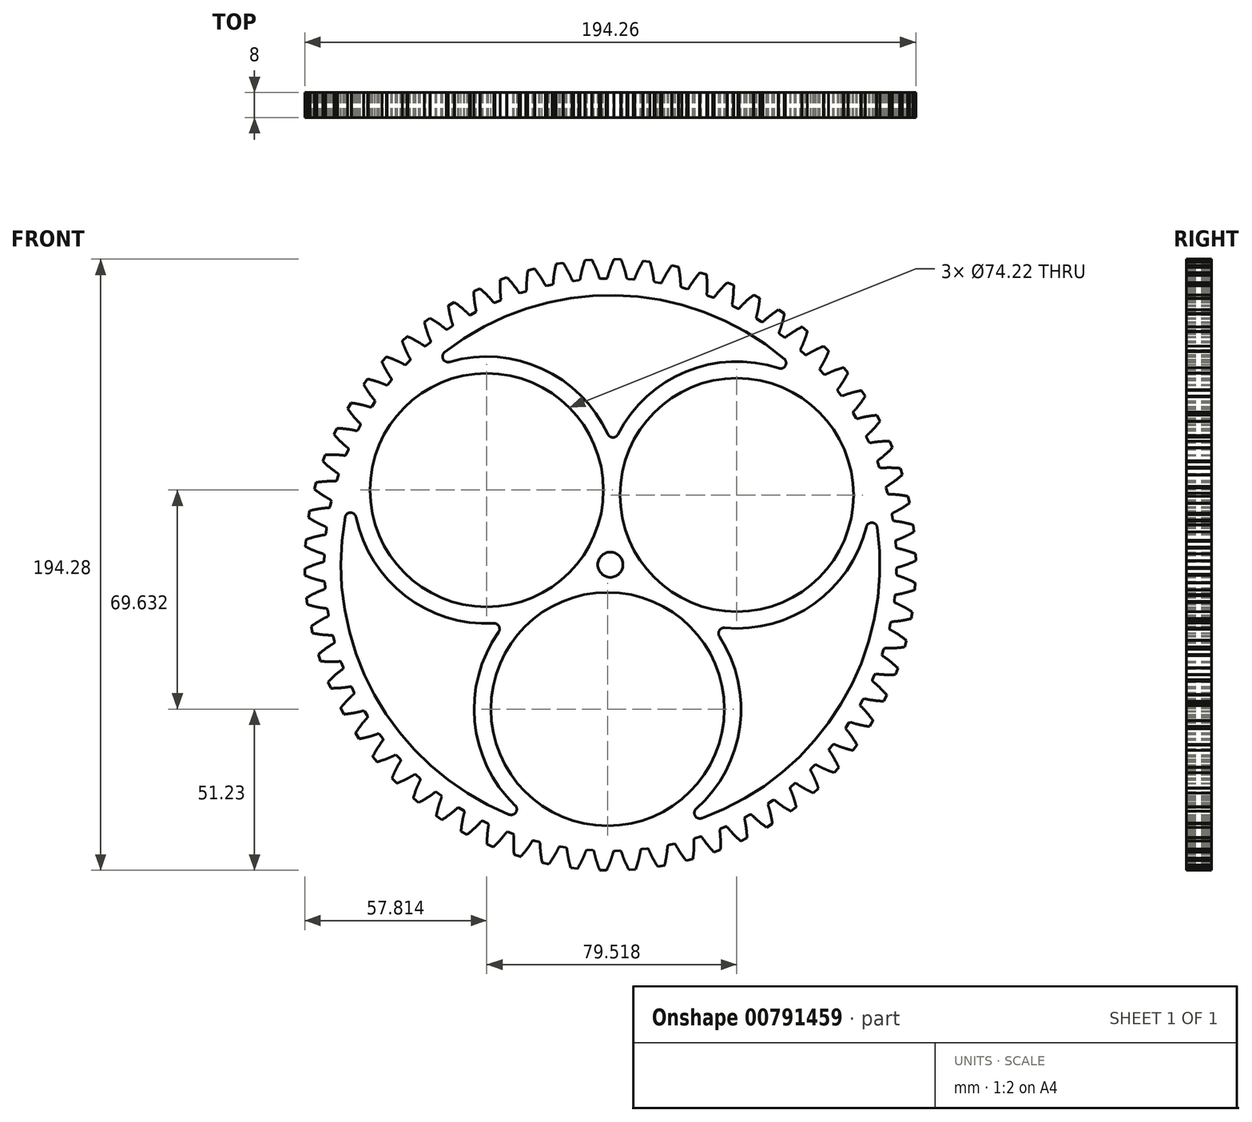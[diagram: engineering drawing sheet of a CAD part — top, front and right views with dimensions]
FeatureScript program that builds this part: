
annotation { "Feature Type Name" : "Feature", "Feature Type Description" : "" }
export const myFeature = defineFeature(function(context is Context, id is Id, definition is map)
    precondition{}
    {
        {
            var Q0;
            Q0=qCreatedBy(makeId("Front.planeOp"),FACE);
            var sketch = newSketch(context, id + "F0", { "sketchPlane" : qUnion([Q0])});
            skCircle(sketch, "E0", {"center": v(0, 0) * mm, "radius": 94.29 * mm, "construction": true});
            skArc(sketch, "E1", {"start": v(29.1, -80.6) * mm, "mid": v(73.36, -44.27) * mm, "end": v(84.86, 11.84) * mm});
            skCircle(sketch, "E2", {"center": v(-0.89, -45.9) * mm, "radius": 37.1 * mm});
            skArc(sketch, "E3", {"start": v(27.31, -77.6) * mm, "mid": v(41.16, -51.56) * mm, "end": v(34.68, -22.79) * mm});
            skArc(sketch, "E4", {"start": v(36.33, -20.06) * mm, "mid": v(64.8, -12.37) * mm, "end": v(81.39, 12.02) * mm});
            skCircle(sketch, "E5", {"center": v(40.2, 22.19) * mm, "radius": 37.1 * mm});
            skArc(sketch, "E6", {"start": v(36.33, -20.06) * mm, "mid": v(34.65, -20.9) * mm, "end": v(34.68, -22.79) * mm});
            skArc(sketch, "E7", {"start": v(84.86, 11.84) * mm, "mid": v(83.2, 13.36) * mm, "end": v(81.39, 12.02) * mm});
            skArc(sketch, "E8", {"start": v(27.31, -77.6) * mm, "mid": v(26.97, -79.83) * mm, "end": v(29.1, -80.6) * mm});
            skCircle(sketch, "E9", {"center": v(-39.32, 23.72) * mm, "radius": 37.1 * mm});
            skArc(sketch, "E10", {"start": v(-0.8, 41.5) * mm, "mid": v(0.78, 40.46) * mm, "end": v(2.4, 41.43) * mm});
            skArc(sketch, "E11", {"start": v(-52.68, 67.58) * mm, "mid": v(-53.17, 65.37) * mm, "end": v(-51.1, 64.48) * mm});
            skArc(sketch, "E12", {"start": v(53.55, 62.46) * mm, "mid": v(55.65, 63.27) * mm, "end": v(55.25, 65.5) * mm});
            skArc(sketch, "E13", {"start": v(53.55, 62.46) * mm, "mid": v(24.07, 61.43) * mm, "end": v(2.4, 41.43) * mm});
            skArc(sketch, "E14", {"start": v(-0.8, 41.5) * mm, "mid": v(-21.69, 62.3) * mm, "end": v(-51.1, 64.48) * mm});
            skArc(sketch, "E15", {"start": v(55.25, 65.5) * mm, "mid": v(1.65, 85.67) * mm, "end": v(-52.68, 67.58) * mm});
            skArc(sketch, "E16", {"start": v(-35.54, -21.43) * mm, "mid": v(-35.43, -19.56) * mm, "end": v(-37.08, -18.64) * mm});
            skArc(sketch, "E17", {"start": v(-32.18, -79.41) * mm, "mid": v(-30.03, -78.73) * mm, "end": v(-30.29, -76.5) * mm});
            skArc(sketch, "E18", {"start": v(-80.86, 15.15) * mm, "mid": v(-82.62, 16.56) * mm, "end": v(-84.34, 15.1) * mm});
            skArc(sketch, "E19", {"start": v(-80.86, 15.15) * mm, "mid": v(-65.23, -9.86) * mm, "end": v(-37.08, -18.64) * mm});
            skArc(sketch, "E20", {"start": v(-35.54, -21.43) * mm, "mid": v(-43.12, -49.94) * mm, "end": v(-30.29, -76.5) * mm});
            skArc(sketch, "E21", {"start": v(-84.34, 15.1) * mm, "mid": v(-75.02, -41.4) * mm, "end": v(-32.18, -79.41) * mm});
            skCircle(sketch, "E22", {"center": v(0, 0) * mm, "radius": 4 * mm});
            skLineSegment(sketch, "E23", {"start": v(-91, 1.29) * mm, "end": v(-91.2, 0.86) * mm});
            skLineSegment(sketch, "E24", {"start": v(-91.2, 0.86) * mm, "end": v(-91.31, 0.84) * mm});
            skLineSegment(sketch, "E25", {"start": v(-91.31, 0.84) * mm, "end": v(-91.43, 0.8) * mm});
            skLineSegment(sketch, "E26", {"start": v(-91.43, 0.8) * mm, "end": v(-91.55, 0.78) * mm});
            skLineSegment(sketch, "E27", {"start": v(-91.55, 0.78) * mm, "end": v(-91.67, 0.75) * mm});
            skLineSegment(sketch, "E28", {"start": v(-91.67, 0.75) * mm, "end": v(-91.79, 0.72) * mm});
            skLineSegment(sketch, "E29", {"start": v(-91.79, 0.72) * mm, "end": v(-91.91, 0.68) * mm});
            skLineSegment(sketch, "E30", {"start": v(-91.91, 0.68) * mm, "end": v(-92.04, 0.65) * mm});
            skLineSegment(sketch, "E31", {"start": v(-92.04, 0.65) * mm, "end": v(-92.17, 0.61) * mm});
            skLineSegment(sketch, "E32", {"start": v(-92.17, 0.61) * mm, "end": v(-92.3, 0.58) * mm});
            skLineSegment(sketch, "E33", {"start": v(-92.3, 0.58) * mm, "end": v(-92.43, 0.54) * mm});
            skLineSegment(sketch, "E34", {"start": v(-92.43, 0.54) * mm, "end": v(-92.56, 0.5) * mm});
            skLineSegment(sketch, "E35", {"start": v(-92.56, 0.5) * mm, "end": v(-92.7, 0.46) * mm});
            skLineSegment(sketch, "E36", {"start": v(-92.7, 0.46) * mm, "end": v(-92.84, 0.42) * mm});
            skLineSegment(sketch, "E37", {"start": v(-92.84, 0.42) * mm, "end": v(-92.98, 0.37) * mm});
            skLineSegment(sketch, "E38", {"start": v(-92.98, 0.37) * mm, "end": v(-93.12, 0.33) * mm});
            skLineSegment(sketch, "E39", {"start": v(-93.12, 0.33) * mm, "end": v(-93.27, 0.28) * mm});
            skLineSegment(sketch, "E40", {"start": v(-93.27, 0.28) * mm, "end": v(-93.42, 0.23) * mm});
            skLineSegment(sketch, "E41", {"start": v(-93.42, 0.23) * mm, "end": v(-93.57, 0.18) * mm});
            skLineSegment(sketch, "E42", {"start": v(-93.57, 0.18) * mm, "end": v(-93.72, 0.13) * mm});
            skLineSegment(sketch, "E43", {"start": v(-93.72, 0.13) * mm, "end": v(-93.87, 0.08) * mm});
            skLineSegment(sketch, "E44", {"start": v(-93.87, 0.08) * mm, "end": v(-94.03, 0.02) * mm});
            skLineSegment(sketch, "E45", {"start": v(-94.03, 0.02) * mm, "end": v(-94.19, -0.04) * mm});
            skLineSegment(sketch, "E46", {"start": v(-94.19, -0.04) * mm, "end": v(-94.35, -0.1) * mm});
            skLineSegment(sketch, "E47", {"start": v(-94.35, -0.1) * mm, "end": v(-94.5, -0.15) * mm});
            skLineSegment(sketch, "E48", {"start": v(-94.5, -0.15) * mm, "end": v(-94.67, -0.22) * mm});
            skLineSegment(sketch, "E49", {"start": v(-94.67, -0.22) * mm, "end": v(-94.84, -0.28) * mm});
            skLineSegment(sketch, "E50", {"start": v(-94.84, -0.28) * mm, "end": v(-95, -0.34) * mm});
            skLineSegment(sketch, "E51", {"start": v(-95, -0.34) * mm, "end": v(-95.18, -0.41) * mm});
            skLineSegment(sketch, "E52", {"start": v(-95.18, -0.41) * mm, "end": v(-95.35, -0.48) * mm});
            skLineSegment(sketch, "E53", {"start": v(-95.35, -0.48) * mm, "end": v(-95.52, -0.55) * mm});
            skLineSegment(sketch, "E54", {"start": v(-95.52, -0.55) * mm, "end": v(-95.7, -0.62) * mm});
            skLineSegment(sketch, "E55", {"start": v(-95.7, -0.62) * mm, "end": v(-95.88, -0.7) * mm});
            skLineSegment(sketch, "E56", {"start": v(-95.88, -0.7) * mm, "end": v(-96.06, -0.77) * mm});
            skLineSegment(sketch, "E57", {"start": v(-96.06, -0.77) * mm, "end": v(-96.24, -0.85) * mm});
            skLineSegment(sketch, "E58", {"start": v(-96.24, -0.85) * mm, "end": v(-96.42, -0.93) * mm});
            skLineSegment(sketch, "E59", {"start": v(-96.42, -0.93) * mm, "end": v(-96.6, -1.01) * mm});
            skLineSegment(sketch, "E60", {"start": v(-96.6, -1.01) * mm, "end": v(-96.8, -1.1) * mm});
            skLineSegment(sketch, "E61", {"start": v(-96.8, -1.1) * mm, "end": v(-96.98, -1.19) * mm});
            skLineSegment(sketch, "E62", {"start": v(-96.98, -1.19) * mm, "end": v(-97.13, -1.27) * mm});
            skLineSegment(sketch, "E63", {"start": v(-97.13, -1.27) * mm, "end": v(-97.08, -3.42) * mm});
            skLineSegment(sketch, "E64", {"start": v(-97.08, -3.42) * mm, "end": v(-96.92, -3.5) * mm});
            skLineSegment(sketch, "E65", {"start": v(-96.92, -3.5) * mm, "end": v(-96.73, -3.58) * mm});
            skLineSegment(sketch, "E66", {"start": v(-96.73, -3.58) * mm, "end": v(-96.54, -3.66) * mm});
            skLineSegment(sketch, "E67", {"start": v(-96.54, -3.66) * mm, "end": v(-96.35, -3.73) * mm});
            skLineSegment(sketch, "E68", {"start": v(-96.35, -3.73) * mm, "end": v(-96.17, -3.8) * mm});
            skLineSegment(sketch, "E69", {"start": v(-96.17, -3.8) * mm, "end": v(-95.98, -3.87) * mm});
            skLineSegment(sketch, "E70", {"start": v(-95.98, -3.87) * mm, "end": v(-95.8, -3.94) * mm});
            skLineSegment(sketch, "E71", {"start": v(-95.8, -3.94) * mm, "end": v(-95.62, -4) * mm});
            skLineSegment(sketch, "E72", {"start": v(-95.62, -4) * mm, "end": v(-95.44, -4.07) * mm});
            skLineSegment(sketch, "E73", {"start": v(-95.44, -4.07) * mm, "end": v(-95.26, -4.13) * mm});
            skLineSegment(sketch, "E74", {"start": v(-95.26, -4.13) * mm, "end": v(-95.09, -4.2) * mm});
            skLineSegment(sketch, "E75", {"start": v(-95.09, -4.2) * mm, "end": v(-94.91, -4.25) * mm});
            skLineSegment(sketch, "E76", {"start": v(-94.91, -4.25) * mm, "end": v(-94.74, -4.3) * mm});
            skLineSegment(sketch, "E77", {"start": v(-94.74, -4.3) * mm, "end": v(-94.57, -4.36) * mm});
            skLineSegment(sketch, "E78", {"start": v(-94.57, -4.36) * mm, "end": v(-94.4, -4.41) * mm});
            skLineSegment(sketch, "E79", {"start": v(-94.4, -4.41) * mm, "end": v(-94.24, -4.47) * mm});
            skLineSegment(sketch, "E80", {"start": v(-94.24, -4.47) * mm, "end": v(-94.08, -4.52) * mm});
            skLineSegment(sketch, "E81", {"start": v(-94.08, -4.52) * mm, "end": v(-93.92, -4.57) * mm});
            skLineSegment(sketch, "E82", {"start": v(-93.92, -4.57) * mm, "end": v(-93.76, -4.61) * mm});
            skLineSegment(sketch, "E83", {"start": v(-93.76, -4.61) * mm, "end": v(-93.6, -4.66) * mm});
            skLineSegment(sketch, "E84", {"start": v(-93.6, -4.66) * mm, "end": v(-93.45, -4.7) * mm});
            skLineSegment(sketch, "E85", {"start": v(-93.45, -4.7) * mm, "end": v(-93.3, -4.75) * mm});
            skLineSegment(sketch, "E86", {"start": v(-93.3, -4.75) * mm, "end": v(-93.15, -4.79) * mm});
            skLineSegment(sketch, "E87", {"start": v(-93.15, -4.79) * mm, "end": v(-93, -4.83) * mm});
            skLineSegment(sketch, "E88", {"start": v(-93, -4.83) * mm, "end": v(-92.85, -4.87) * mm});
            skLineSegment(sketch, "E89", {"start": v(-92.85, -4.87) * mm, "end": v(-92.71, -4.9) * mm});
            skLineSegment(sketch, "E90", {"start": v(-92.71, -4.9) * mm, "end": v(-92.57, -4.94) * mm});
            skLineSegment(sketch, "E91", {"start": v(-92.57, -4.94) * mm, "end": v(-92.43, -4.97) * mm});
            skLineSegment(sketch, "E92", {"start": v(-92.43, -4.97) * mm, "end": v(-92.3, -5) * mm});
            skLineSegment(sketch, "E93", {"start": v(-92.3, -5) * mm, "end": v(-92.16, -5.04) * mm});
            skLineSegment(sketch, "E94", {"start": v(-92.16, -5.04) * mm, "end": v(-92.03, -5.07) * mm});
            skLineSegment(sketch, "E95", {"start": v(-92.03, -5.07) * mm, "end": v(-91.9, -5.1) * mm});
            skLineSegment(sketch, "E96", {"start": v(-91.9, -5.1) * mm, "end": v(-91.77, -5.13) * mm});
            skLineSegment(sketch, "E97", {"start": v(-91.77, -5.13) * mm, "end": v(-91.65, -5.15) * mm});
            skLineSegment(sketch, "E98", {"start": v(-91.65, -5.15) * mm, "end": v(-91.52, -5.18) * mm});
            skLineSegment(sketch, "E99", {"start": v(-91.52, -5.18) * mm, "end": v(-91.4, -5.2) * mm});
            skLineSegment(sketch, "E100", {"start": v(-91.4, -5.2) * mm, "end": v(-91.28, -5.23) * mm});
            skLineSegment(sketch, "E101", {"start": v(-91.28, -5.23) * mm, "end": v(-91.17, -5.25) * mm});
            skLineSegment(sketch, "E102", {"start": v(-91.17, -5.25) * mm, "end": v(-91.05, -5.27) * mm});
            skLineSegment(sketch, "E103", {"start": v(-91.05, -5.27) * mm, "end": v(-90.82, -5.68) * mm});
            skLineSegment(sketch, "E104", {"start": v(-90.82, -5.68) * mm, "end": v(-90.7, -7.37) * mm});
            skLineSegment(sketch, "E105", {"start": v(-90.7, -7.37) * mm, "end": v(-90.87, -7.81) * mm});
            skLineSegment(sketch, "E106", {"start": v(-90.87, -7.81) * mm, "end": v(-90.98, -7.85) * mm});
            skLineSegment(sketch, "E107", {"start": v(-90.98, -7.85) * mm, "end": v(-91.1, -7.89) * mm});
            skLineSegment(sketch, "E108", {"start": v(-91.1, -7.89) * mm, "end": v(-91.2, -7.93) * mm});
            skLineSegment(sketch, "E109", {"start": v(-91.2, -7.93) * mm, "end": v(-91.32, -7.97) * mm});
            skLineSegment(sketch, "E110", {"start": v(-91.32, -7.97) * mm, "end": v(-91.44, -8.01) * mm});
            skLineSegment(sketch, "E111", {"start": v(-91.44, -8.01) * mm, "end": v(-91.56, -8.06) * mm});
            skLineSegment(sketch, "E112", {"start": v(-91.56, -8.06) * mm, "end": v(-91.68, -8.1) * mm});
            skLineSegment(sketch, "E113", {"start": v(-91.68, -8.1) * mm, "end": v(-91.8, -8.15) * mm});
            skLineSegment(sketch, "E114", {"start": v(-91.8, -8.15) * mm, "end": v(-91.93, -8.2) * mm});
            skLineSegment(sketch, "E115", {"start": v(-91.93, -8.2) * mm, "end": v(-92.06, -8.25) * mm});
            skLineSegment(sketch, "E116", {"start": v(-92.06, -8.25) * mm, "end": v(-92.2, -8.3) * mm});
            skLineSegment(sketch, "E117", {"start": v(-92.2, -8.3) * mm, "end": v(-92.32, -8.36) * mm});
            skLineSegment(sketch, "E118", {"start": v(-92.32, -8.36) * mm, "end": v(-92.46, -8.41) * mm});
            skLineSegment(sketch, "E119", {"start": v(-92.46, -8.41) * mm, "end": v(-92.6, -8.47) * mm});
            skLineSegment(sketch, "E120", {"start": v(-92.6, -8.47) * mm, "end": v(-92.73, -8.53) * mm});
            skLineSegment(sketch, "E121", {"start": v(-92.73, -8.53) * mm, "end": v(-92.87, -8.59) * mm});
            skLineSegment(sketch, "E122", {"start": v(-92.87, -8.59) * mm, "end": v(-93.02, -8.65) * mm});
            skLineSegment(sketch, "E123", {"start": v(-93.02, -8.65) * mm, "end": v(-93.16, -8.71) * mm});
            skLineSegment(sketch, "E124", {"start": v(-93.16, -8.71) * mm, "end": v(-93.3, -8.78) * mm});
            skLineSegment(sketch, "E125", {"start": v(-93.3, -8.78) * mm, "end": v(-93.46, -8.85) * mm});
            skLineSegment(sketch, "E126", {"start": v(-93.46, -8.85) * mm, "end": v(-93.6, -8.92) * mm});
            skLineSegment(sketch, "E127", {"start": v(-93.6, -8.92) * mm, "end": v(-93.76, -8.99) * mm});
            skLineSegment(sketch, "E128", {"start": v(-93.76, -8.99) * mm, "end": v(-93.91, -9.06) * mm});
            skLineSegment(sketch, "E129", {"start": v(-93.91, -9.06) * mm, "end": v(-94.07, -9.14) * mm});
            skLineSegment(sketch, "E130", {"start": v(-94.07, -9.14) * mm, "end": v(-94.22, -9.21) * mm});
            skLineSegment(sketch, "E131", {"start": v(-94.22, -9.21) * mm, "end": v(-94.38, -9.3) * mm});
            skLineSegment(sketch, "E132", {"start": v(-94.38, -9.3) * mm, "end": v(-94.54, -9.37) * mm});
            skLineSegment(sketch, "E133", {"start": v(-94.54, -9.37) * mm, "end": v(-94.7, -9.46) * mm});
            skLineSegment(sketch, "E134", {"start": v(-94.7, -9.46) * mm, "end": v(-94.87, -9.54) * mm});
            skLineSegment(sketch, "E135", {"start": v(-94.87, -9.54) * mm, "end": v(-95.04, -9.63) * mm});
            skLineSegment(sketch, "E136", {"start": v(-95.04, -9.63) * mm, "end": v(-95.2, -9.72) * mm});
            skLineSegment(sketch, "E137", {"start": v(-95.2, -9.72) * mm, "end": v(-95.38, -9.8) * mm});
            skLineSegment(sketch, "E138", {"start": v(-95.38, -9.8) * mm, "end": v(-95.55, -9.9) * mm});
            skLineSegment(sketch, "E139", {"start": v(-95.55, -9.9) * mm, "end": v(-95.72, -10) * mm});
            skLineSegment(sketch, "E140", {"start": v(-95.72, -10) * mm, "end": v(-95.9, -10.1) * mm});
            skLineSegment(sketch, "E141", {"start": v(-95.9, -10.1) * mm, "end": v(-96.07, -10.2) * mm});
            skLineSegment(sketch, "E142", {"start": v(-96.07, -10.2) * mm, "end": v(-96.25, -10.3) * mm});
            skLineSegment(sketch, "E143", {"start": v(-96.25, -10.3) * mm, "end": v(-96.43, -10.4) * mm});
            skLineSegment(sketch, "E144", {"start": v(-96.43, -10.4) * mm, "end": v(-96.57, -10.5) * mm});
            skLineSegment(sketch, "E145", {"start": v(-96.57, -10.5) * mm, "end": v(-96.32, -12.64) * mm});
            skLineSegment(sketch, "E146", {"start": v(-96.32, -12.64) * mm, "end": v(-96.15, -12.7) * mm});
            skLineSegment(sketch, "E147", {"start": v(-96.15, -12.7) * mm, "end": v(-95.95, -12.76) * mm});
            skLineSegment(sketch, "E148", {"start": v(-95.95, -12.76) * mm, "end": v(-95.76, -12.82) * mm});
            skLineSegment(sketch, "E149", {"start": v(-95.76, -12.82) * mm, "end": v(-95.56, -12.87) * mm});
            skLineSegment(sketch, "E150", {"start": v(-95.56, -12.87) * mm, "end": v(-95.37, -12.92) * mm});
            skLineSegment(sketch, "E151", {"start": v(-95.37, -12.92) * mm, "end": v(-95.18, -12.98) * mm});
            skLineSegment(sketch, "E152", {"start": v(-95.18, -12.98) * mm, "end": v(-94.99, -13.03) * mm});
            skLineSegment(sketch, "E153", {"start": v(-94.99, -13.03) * mm, "end": v(-94.8, -13.07) * mm});
            skLineSegment(sketch, "E154", {"start": v(-94.8, -13.07) * mm, "end": v(-94.62, -13.12) * mm});
            skLineSegment(sketch, "E155", {"start": v(-94.62, -13.12) * mm, "end": v(-94.44, -13.17) * mm});
            skLineSegment(sketch, "E156", {"start": v(-94.44, -13.17) * mm, "end": v(-94.26, -13.2) * mm});
            skLineSegment(sketch, "E157", {"start": v(-94.26, -13.2) * mm, "end": v(-94.08, -13.25) * mm});
            skLineSegment(sketch, "E158", {"start": v(-94.08, -13.25) * mm, "end": v(-93.9, -13.3) * mm});
            skLineSegment(sketch, "E159", {"start": v(-93.9, -13.3) * mm, "end": v(-93.73, -13.33) * mm});
            skLineSegment(sketch, "E160", {"start": v(-93.73, -13.33) * mm, "end": v(-93.56, -13.37) * mm});
            skLineSegment(sketch, "E161", {"start": v(-93.56, -13.37) * mm, "end": v(-93.39, -13.4) * mm});
            skLineSegment(sketch, "E162", {"start": v(-93.39, -13.4) * mm, "end": v(-93.22, -13.44) * mm});
            skLineSegment(sketch, "E163", {"start": v(-93.22, -13.44) * mm, "end": v(-93.06, -13.47) * mm});
            skLineSegment(sketch, "E164", {"start": v(-93.06, -13.47) * mm, "end": v(-92.9, -13.5) * mm});
            skLineSegment(sketch, "E165", {"start": v(-92.9, -13.5) * mm, "end": v(-92.74, -13.54) * mm});
            skLineSegment(sketch, "E166", {"start": v(-92.74, -13.54) * mm, "end": v(-92.58, -13.57) * mm});
            skLineSegment(sketch, "E167", {"start": v(-92.58, -13.57) * mm, "end": v(-92.42, -13.6) * mm});
            skLineSegment(sketch, "E168", {"start": v(-92.42, -13.6) * mm, "end": v(-92.27, -13.62) * mm});
            skLineSegment(sketch, "E169", {"start": v(-92.27, -13.62) * mm, "end": v(-92.12, -13.65) * mm});
            skLineSegment(sketch, "E170", {"start": v(-92.12, -13.65) * mm, "end": v(-91.97, -13.67) * mm});
            skLineSegment(sketch, "E171", {"start": v(-91.97, -13.67) * mm, "end": v(-91.83, -13.7) * mm});
            skLineSegment(sketch, "E172", {"start": v(-91.83, -13.7) * mm, "end": v(-91.68, -13.72) * mm});
            skLineSegment(sketch, "E173", {"start": v(-91.68, -13.72) * mm, "end": v(-91.54, -13.74) * mm});
            skLineSegment(sketch, "E174", {"start": v(-91.54, -13.74) * mm, "end": v(-91.4, -13.76) * mm});
            skLineSegment(sketch, "E175", {"start": v(-91.4, -13.76) * mm, "end": v(-91.26, -13.78) * mm});
            skLineSegment(sketch, "E176", {"start": v(-91.26, -13.78) * mm, "end": v(-91.13, -13.8) * mm});
            skLineSegment(sketch, "E177", {"start": v(-91.13, -13.8) * mm, "end": v(-91, -13.81) * mm});
            skLineSegment(sketch, "E178", {"start": v(-91, -13.81) * mm, "end": v(-90.87, -13.83) * mm});
            skLineSegment(sketch, "E179", {"start": v(-90.87, -13.83) * mm, "end": v(-90.74, -13.84) * mm});
            skLineSegment(sketch, "E180", {"start": v(-90.74, -13.84) * mm, "end": v(-90.62, -13.85) * mm});
            skLineSegment(sketch, "E181", {"start": v(-90.62, -13.85) * mm, "end": v(-90.5, -13.87) * mm});
            skLineSegment(sketch, "E182", {"start": v(-90.5, -13.87) * mm, "end": v(-90.37, -13.88) * mm});
            skLineSegment(sketch, "E183", {"start": v(-90.37, -13.88) * mm, "end": v(-90.26, -13.9) * mm});
            skLineSegment(sketch, "E184", {"start": v(-90.26, -13.9) * mm, "end": v(-90.14, -13.9) * mm});
            skLineSegment(sketch, "E185", {"start": v(-90.14, -13.9) * mm, "end": v(-89.87, -14.3) * mm});
            skLineSegment(sketch, "E186", {"start": v(-89.87, -14.3) * mm, "end": v(-89.6, -15.96) * mm});
            skLineSegment(sketch, "E187", {"start": v(-89.6, -15.96) * mm, "end": v(-89.72, -16.41) * mm});
            skLineSegment(sketch, "E188", {"start": v(-89.72, -16.41) * mm, "end": v(-89.82, -16.46) * mm});
            skLineSegment(sketch, "E189", {"start": v(-89.82, -16.46) * mm, "end": v(-89.93, -16.51) * mm});
            skLineSegment(sketch, "E190", {"start": v(-89.93, -16.51) * mm, "end": v(-90.04, -16.56) * mm});
            skLineSegment(sketch, "E191", {"start": v(-90.04, -16.56) * mm, "end": v(-90.15, -16.61) * mm});
            skLineSegment(sketch, "E192", {"start": v(-90.15, -16.61) * mm, "end": v(-90.26, -16.67) * mm});
            skLineSegment(sketch, "E193", {"start": v(-90.26, -16.67) * mm, "end": v(-90.38, -16.72) * mm});
            skLineSegment(sketch, "E194", {"start": v(-90.38, -16.72) * mm, "end": v(-90.5, -16.78) * mm});
            skLineSegment(sketch, "E195", {"start": v(-90.5, -16.78) * mm, "end": v(-90.62, -16.84) * mm});
            skLineSegment(sketch, "E196", {"start": v(-90.62, -16.84) * mm, "end": v(-90.74, -16.9) * mm});
            skLineSegment(sketch, "E197", {"start": v(-90.74, -16.9) * mm, "end": v(-90.86, -16.96) * mm});
            skLineSegment(sketch, "E198", {"start": v(-90.86, -16.96) * mm, "end": v(-90.99, -17.03) * mm});
            skLineSegment(sketch, "E199", {"start": v(-90.99, -17.03) * mm, "end": v(-91.11, -17.1) * mm});
            skLineSegment(sketch, "E200", {"start": v(-91.11, -17.1) * mm, "end": v(-91.24, -17.16) * mm});
            skLineSegment(sketch, "E201", {"start": v(-91.24, -17.16) * mm, "end": v(-91.37, -17.23) * mm});
            skLineSegment(sketch, "E202", {"start": v(-91.37, -17.23) * mm, "end": v(-91.5, -17.3) * mm});
            skLineSegment(sketch, "E203", {"start": v(-91.5, -17.3) * mm, "end": v(-91.64, -17.38) * mm});
            skLineSegment(sketch, "E204", {"start": v(-91.64, -17.38) * mm, "end": v(-91.77, -17.45) * mm});
            skLineSegment(sketch, "E205", {"start": v(-91.77, -17.45) * mm, "end": v(-91.91, -17.53) * mm});
            skLineSegment(sketch, "E206", {"start": v(-91.91, -17.53) * mm, "end": v(-92.05, -17.6) * mm});
            skLineSegment(sketch, "E207", {"start": v(-92.05, -17.6) * mm, "end": v(-92.2, -17.7) * mm});
            skLineSegment(sketch, "E208", {"start": v(-92.2, -17.7) * mm, "end": v(-92.33, -17.77) * mm});
            skLineSegment(sketch, "E209", {"start": v(-92.33, -17.77) * mm, "end": v(-92.48, -17.86) * mm});
            skLineSegment(sketch, "E210", {"start": v(-92.48, -17.86) * mm, "end": v(-92.62, -17.95) * mm});
            skLineSegment(sketch, "E211", {"start": v(-92.62, -17.95) * mm, "end": v(-92.77, -18.04) * mm});
            skLineSegment(sketch, "E212", {"start": v(-92.77, -18.04) * mm, "end": v(-92.92, -18.13) * mm});
            skLineSegment(sketch, "E213", {"start": v(-92.92, -18.13) * mm, "end": v(-93.07, -18.22) * mm});
            skLineSegment(sketch, "E214", {"start": v(-93.07, -18.22) * mm, "end": v(-93.22, -18.32) * mm});
            skLineSegment(sketch, "E215", {"start": v(-93.22, -18.32) * mm, "end": v(-93.38, -18.42) * mm});
            skLineSegment(sketch, "E216", {"start": v(-93.38, -18.42) * mm, "end": v(-93.53, -18.52) * mm});
            skLineSegment(sketch, "E217", {"start": v(-93.53, -18.52) * mm, "end": v(-93.7, -18.62) * mm});
            skLineSegment(sketch, "E218", {"start": v(-93.7, -18.62) * mm, "end": v(-93.85, -18.72) * mm});
            skLineSegment(sketch, "E219", {"start": v(-93.85, -18.72) * mm, "end": v(-94.01, -18.83) * mm});
            skLineSegment(sketch, "E220", {"start": v(-94.01, -18.83) * mm, "end": v(-94.17, -18.94) * mm});
            skLineSegment(sketch, "E221", {"start": v(-94.17, -18.94) * mm, "end": v(-94.34, -19.05) * mm});
            skLineSegment(sketch, "E222", {"start": v(-94.34, -19.05) * mm, "end": v(-94.5, -19.16) * mm});
            skLineSegment(sketch, "E223", {"start": v(-94.5, -19.16) * mm, "end": v(-94.67, -19.28) * mm});
            skLineSegment(sketch, "E224", {"start": v(-94.67, -19.28) * mm, "end": v(-94.83, -19.4) * mm});
            skLineSegment(sketch, "E225", {"start": v(-94.83, -19.4) * mm, "end": v(-95, -19.52) * mm});
            skLineSegment(sketch, "E226", {"start": v(-95, -19.52) * mm, "end": v(-95.14, -19.63) * mm});
            skLineSegment(sketch, "E227", {"start": v(-95.14, -19.63) * mm, "end": v(-94.68, -21.74) * mm});
            skLineSegment(sketch, "E228", {"start": v(-94.68, -21.74) * mm, "end": v(-94.5, -21.78) * mm});
            skLineSegment(sketch, "E229", {"start": v(-94.5, -21.78) * mm, "end": v(-94.3, -21.82) * mm});
            skLineSegment(sketch, "E230", {"start": v(-94.3, -21.82) * mm, "end": v(-94.1, -21.86) * mm});
            skLineSegment(sketch, "E231", {"start": v(-94.1, -21.86) * mm, "end": v(-93.9, -21.9) * mm});
            skLineSegment(sketch, "E232", {"start": v(-93.9, -21.9) * mm, "end": v(-93.7, -21.93) * mm});
            skLineSegment(sketch, "E233", {"start": v(-93.7, -21.93) * mm, "end": v(-93.51, -21.96) * mm});
            skLineSegment(sketch, "E234", {"start": v(-93.51, -21.96) * mm, "end": v(-93.32, -22) * mm});
            skLineSegment(sketch, "E235", {"start": v(-93.32, -22) * mm, "end": v(-93.13, -22.03) * mm});
            skLineSegment(sketch, "E236", {"start": v(-93.13, -22.03) * mm, "end": v(-92.94, -22.06) * mm});
            skLineSegment(sketch, "E237", {"start": v(-92.94, -22.06) * mm, "end": v(-92.76, -22.08) * mm});
            skLineSegment(sketch, "E238", {"start": v(-92.76, -22.08) * mm, "end": v(-92.57, -22.1) * mm});
            skLineSegment(sketch, "E239", {"start": v(-92.57, -22.1) * mm, "end": v(-92.4, -22.13) * mm});
            skLineSegment(sketch, "E240", {"start": v(-92.4, -22.13) * mm, "end": v(-92.21, -22.16) * mm});
            skLineSegment(sketch, "E241", {"start": v(-92.21, -22.16) * mm, "end": v(-92.04, -22.18) * mm});
            skLineSegment(sketch, "E242", {"start": v(-92.04, -22.18) * mm, "end": v(-91.86, -22.2) * mm});
            skLineSegment(sketch, "E243", {"start": v(-91.86, -22.2) * mm, "end": v(-91.7, -22.22) * mm});
            skLineSegment(sketch, "E244", {"start": v(-91.7, -22.22) * mm, "end": v(-91.52, -22.24) * mm});
            skLineSegment(sketch, "E245", {"start": v(-91.52, -22.24) * mm, "end": v(-91.36, -22.26) * mm});
            skLineSegment(sketch, "E246", {"start": v(-91.36, -22.26) * mm, "end": v(-91.2, -22.27) * mm});
            skLineSegment(sketch, "E247", {"start": v(-91.2, -22.27) * mm, "end": v(-91.03, -22.29) * mm});
            skLineSegment(sketch, "E248", {"start": v(-91.03, -22.29) * mm, "end": v(-90.87, -22.3) * mm});
            skLineSegment(sketch, "E249", {"start": v(-90.87, -22.3) * mm, "end": v(-90.71, -22.32) * mm});
            skLineSegment(sketch, "E250", {"start": v(-90.71, -22.32) * mm, "end": v(-90.56, -22.33) * mm});
            skLineSegment(sketch, "E251", {"start": v(-90.56, -22.33) * mm, "end": v(-90.4, -22.34) * mm});
            skLineSegment(sketch, "E252", {"start": v(-90.4, -22.34) * mm, "end": v(-90.26, -22.35) * mm});
            skLineSegment(sketch, "E253", {"start": v(-90.26, -22.35) * mm, "end": v(-90.1, -22.36) * mm});
            skLineSegment(sketch, "E254", {"start": v(-90.1, -22.36) * mm, "end": v(-89.96, -22.37) * mm});
            skLineSegment(sketch, "E255", {"start": v(-89.96, -22.37) * mm, "end": v(-89.82, -22.38) * mm});
            skLineSegment(sketch, "E256", {"start": v(-89.82, -22.38) * mm, "end": v(-89.68, -22.38) * mm});
            skLineSegment(sketch, "E257", {"start": v(-89.68, -22.38) * mm, "end": v(-89.54, -22.39) * mm});
            skLineSegment(sketch, "E258", {"start": v(-89.54, -22.39) * mm, "end": v(-89.4, -22.4) * mm});
            skLineSegment(sketch, "E259", {"start": v(-89.4, -22.4) * mm, "end": v(-89.27, -22.4) * mm});
            skLineSegment(sketch, "E260", {"start": v(-89.27, -22.4) * mm, "end": v(-89.14, -22.4) * mm});
            skLineSegment(sketch, "E261", {"start": v(-89.14, -22.4) * mm, "end": v(-89.01, -22.4) * mm});
            skLineSegment(sketch, "E262", {"start": v(-89.01, -22.4) * mm, "end": v(-88.89, -22.4) * mm});
            skLineSegment(sketch, "E263", {"start": v(-88.89, -22.4) * mm, "end": v(-88.77, -22.4) * mm});
            skLineSegment(sketch, "E264", {"start": v(-88.77, -22.4) * mm, "end": v(-88.64, -22.4) * mm});
            skLineSegment(sketch, "E265", {"start": v(-88.64, -22.4) * mm, "end": v(-88.53, -22.4) * mm});
            skLineSegment(sketch, "E266", {"start": v(-88.53, -22.4) * mm, "end": v(-88.41, -22.4) * mm});
            skLineSegment(sketch, "E267", {"start": v(-88.41, -22.4) * mm, "end": v(-88.1, -22.77) * mm});
            skLineSegment(sketch, "E268", {"start": v(-88.1, -22.77) * mm, "end": v(-87.67, -24.4) * mm});
            skLineSegment(sketch, "E269", {"start": v(-87.67, -24.4) * mm, "end": v(-87.75, -24.87) * mm});
            skLineSegment(sketch, "E270", {"start": v(-87.75, -24.87) * mm, "end": v(-87.85, -24.93) * mm});
            skLineSegment(sketch, "E271", {"start": v(-87.85, -24.93) * mm, "end": v(-87.95, -24.98) * mm});
            skLineSegment(sketch, "E272", {"start": v(-87.95, -24.98) * mm, "end": v(-88.06, -25.05) * mm});
            skLineSegment(sketch, "E273", {"start": v(-88.06, -25.05) * mm, "end": v(-88.16, -25.1) * mm});
            skLineSegment(sketch, "E274", {"start": v(-88.16, -25.1) * mm, "end": v(-88.27, -25.17) * mm});
            skLineSegment(sketch, "E275", {"start": v(-88.27, -25.17) * mm, "end": v(-88.38, -25.24) * mm});
            skLineSegment(sketch, "E276", {"start": v(-88.38, -25.24) * mm, "end": v(-88.5, -25.3) * mm});
            skLineSegment(sketch, "E277", {"start": v(-88.5, -25.3) * mm, "end": v(-88.6, -25.38) * mm});
            skLineSegment(sketch, "E278", {"start": v(-88.6, -25.38) * mm, "end": v(-88.72, -25.45) * mm});
            skLineSegment(sketch, "E279", {"start": v(-88.72, -25.45) * mm, "end": v(-88.84, -25.52) * mm});
            skLineSegment(sketch, "E280", {"start": v(-88.84, -25.52) * mm, "end": v(-88.95, -25.6) * mm});
            skLineSegment(sketch, "E281", {"start": v(-88.95, -25.6) * mm, "end": v(-89.07, -25.68) * mm});
            skLineSegment(sketch, "E282", {"start": v(-89.07, -25.68) * mm, "end": v(-89.2, -25.76) * mm});
            skLineSegment(sketch, "E283", {"start": v(-89.2, -25.76) * mm, "end": v(-89.32, -25.84) * mm});
            skLineSegment(sketch, "E284", {"start": v(-89.32, -25.84) * mm, "end": v(-89.44, -25.92) * mm});
            skLineSegment(sketch, "E285", {"start": v(-89.44, -25.92) * mm, "end": v(-89.57, -26) * mm});
            skLineSegment(sketch, "E286", {"start": v(-89.57, -26) * mm, "end": v(-89.7, -26.1) * mm});
            skLineSegment(sketch, "E287", {"start": v(-89.7, -26.1) * mm, "end": v(-89.83, -26.19) * mm});
            skLineSegment(sketch, "E288", {"start": v(-89.83, -26.19) * mm, "end": v(-89.96, -26.28) * mm});
            skLineSegment(sketch, "E289", {"start": v(-89.96, -26.28) * mm, "end": v(-90.1, -26.37) * mm});
            skLineSegment(sketch, "E290", {"start": v(-90.1, -26.37) * mm, "end": v(-90.23, -26.47) * mm});
            skLineSegment(sketch, "E291", {"start": v(-90.23, -26.47) * mm, "end": v(-90.36, -26.57) * mm});
            skLineSegment(sketch, "E292", {"start": v(-90.36, -26.57) * mm, "end": v(-90.5, -26.67) * mm});
            skLineSegment(sketch, "E293", {"start": v(-90.5, -26.67) * mm, "end": v(-90.64, -26.77) * mm});
            skLineSegment(sketch, "E294", {"start": v(-90.64, -26.77) * mm, "end": v(-90.78, -26.88) * mm});
            skLineSegment(sketch, "E295", {"start": v(-90.78, -26.88) * mm, "end": v(-90.92, -26.99) * mm});
            skLineSegment(sketch, "E296", {"start": v(-90.92, -26.99) * mm, "end": v(-91.06, -27.1) * mm});
            skLineSegment(sketch, "E297", {"start": v(-91.06, -27.1) * mm, "end": v(-91.2, -27.2) * mm});
            skLineSegment(sketch, "E298", {"start": v(-91.2, -27.2) * mm, "end": v(-91.35, -27.32) * mm});
            skLineSegment(sketch, "E299", {"start": v(-91.35, -27.32) * mm, "end": v(-91.5, -27.44) * mm});
            skLineSegment(sketch, "E300", {"start": v(-91.5, -27.44) * mm, "end": v(-91.65, -27.56) * mm});
            skLineSegment(sketch, "E301", {"start": v(-91.65, -27.56) * mm, "end": v(-91.8, -27.68) * mm});
            skLineSegment(sketch, "E302", {"start": v(-91.8, -27.68) * mm, "end": v(-91.95, -27.8) * mm});
            skLineSegment(sketch, "E303", {"start": v(-91.95, -27.8) * mm, "end": v(-92.1, -27.93) * mm});
            skLineSegment(sketch, "E304", {"start": v(-92.1, -27.93) * mm, "end": v(-92.25, -28.06) * mm});
            skLineSegment(sketch, "E305", {"start": v(-92.25, -28.06) * mm, "end": v(-92.4, -28.2) * mm});
            skLineSegment(sketch, "E306", {"start": v(-92.4, -28.2) * mm, "end": v(-92.56, -28.32) * mm});
            skLineSegment(sketch, "E307", {"start": v(-92.56, -28.32) * mm, "end": v(-92.72, -28.46) * mm});
            skLineSegment(sketch, "E308", {"start": v(-92.72, -28.46) * mm, "end": v(-92.84, -28.59) * mm});
            skLineSegment(sketch, "E309", {"start": v(-92.84, -28.59) * mm, "end": v(-92.19, -30.64) * mm});
            skLineSegment(sketch, "E310", {"start": v(-92.19, -30.64) * mm, "end": v(-92.01, -30.67) * mm});
            skLineSegment(sketch, "E311", {"start": v(-92.01, -30.67) * mm, "end": v(-91.8, -30.69) * mm});
            skLineSegment(sketch, "E312", {"start": v(-91.8, -30.69) * mm, "end": v(-91.6, -30.7) * mm});
            skLineSegment(sketch, "E313", {"start": v(-91.6, -30.7) * mm, "end": v(-91.4, -30.72) * mm});
            skLineSegment(sketch, "E314", {"start": v(-91.4, -30.72) * mm, "end": v(-91.2, -30.74) * mm});
            skLineSegment(sketch, "E315", {"start": v(-91.2, -30.74) * mm, "end": v(-91, -30.75) * mm});
            skLineSegment(sketch, "E316", {"start": v(-91, -30.75) * mm, "end": v(-90.8, -30.77) * mm});
            skLineSegment(sketch, "E317", {"start": v(-90.8, -30.77) * mm, "end": v(-90.62, -30.78) * mm});
            skLineSegment(sketch, "E318", {"start": v(-90.62, -30.78) * mm, "end": v(-90.43, -30.8) * mm});
            skLineSegment(sketch, "E319", {"start": v(-90.43, -30.8) * mm, "end": v(-90.24, -30.8) * mm});
            skLineSegment(sketch, "E320", {"start": v(-90.24, -30.8) * mm, "end": v(-90.05, -30.8) * mm});
            skLineSegment(sketch, "E321", {"start": v(-90.05, -30.8) * mm, "end": v(-89.87, -30.82) * mm});
            skLineSegment(sketch, "E322", {"start": v(-89.87, -30.82) * mm, "end": v(-89.7, -30.82) * mm});
            skLineSegment(sketch, "E323", {"start": v(-89.7, -30.82) * mm, "end": v(-89.51, -30.83) * mm});
            skLineSegment(sketch, "E324", {"start": v(-89.51, -30.83) * mm, "end": v(-89.34, -30.83) * mm});
            skLineSegment(sketch, "E325", {"start": v(-89.34, -30.83) * mm, "end": v(-89.17, -30.84) * mm});
            skLineSegment(sketch, "E326", {"start": v(-89.17, -30.84) * mm, "end": v(-89, -30.84) * mm});
            skLineSegment(sketch, "E327", {"start": v(-89, -30.84) * mm, "end": v(-88.83, -30.84) * mm});
            skLineSegment(sketch, "E328", {"start": v(-88.83, -30.84) * mm, "end": v(-88.66, -30.84) * mm});
            skLineSegment(sketch, "E329", {"start": v(-88.66, -30.84) * mm, "end": v(-88.5, -30.84) * mm});
            skLineSegment(sketch, "E330", {"start": v(-88.5, -30.84) * mm, "end": v(-88.34, -30.84) * mm});
            skLineSegment(sketch, "E331", {"start": v(-88.34, -30.84) * mm, "end": v(-88.18, -30.84) * mm});
            skLineSegment(sketch, "E332", {"start": v(-88.18, -30.84) * mm, "end": v(-88.03, -30.84) * mm});
            skLineSegment(sketch, "E333", {"start": v(-88.03, -30.84) * mm, "end": v(-87.87, -30.83) * mm});
            skLineSegment(sketch, "E334", {"start": v(-87.87, -30.83) * mm, "end": v(-87.72, -30.83) * mm});
            skLineSegment(sketch, "E335", {"start": v(-87.72, -30.83) * mm, "end": v(-87.57, -30.82) * mm});
            skLineSegment(sketch, "E336", {"start": v(-87.57, -30.82) * mm, "end": v(-87.43, -30.82) * mm});
            skLineSegment(sketch, "E337", {"start": v(-87.43, -30.82) * mm, "end": v(-87.29, -30.81) * mm});
            skLineSegment(sketch, "E338", {"start": v(-87.29, -30.81) * mm, "end": v(-87.15, -30.8) * mm});
            skLineSegment(sketch, "E339", {"start": v(-87.15, -30.8) * mm, "end": v(-87, -30.8) * mm});
            skLineSegment(sketch, "E340", {"start": v(-87, -30.8) * mm, "end": v(-86.87, -30.8) * mm});
            skLineSegment(sketch, "E341", {"start": v(-86.87, -30.8) * mm, "end": v(-86.74, -30.78) * mm});
            skLineSegment(sketch, "E342", {"start": v(-86.74, -30.78) * mm, "end": v(-86.6, -30.77) * mm});
            skLineSegment(sketch, "E343", {"start": v(-86.6, -30.77) * mm, "end": v(-86.48, -30.76) * mm});
            skLineSegment(sketch, "E344", {"start": v(-86.48, -30.76) * mm, "end": v(-86.36, -30.75) * mm});
            skLineSegment(sketch, "E345", {"start": v(-86.36, -30.75) * mm, "end": v(-86.23, -30.74) * mm});
            skLineSegment(sketch, "E346", {"start": v(-86.23, -30.74) * mm, "end": v(-86.11, -30.73) * mm});
            skLineSegment(sketch, "E347", {"start": v(-86.11, -30.73) * mm, "end": v(-86, -30.72) * mm});
            skLineSegment(sketch, "E348", {"start": v(-86, -30.72) * mm, "end": v(-85.88, -30.7) * mm});
            skLineSegment(sketch, "E349", {"start": v(-85.88, -30.7) * mm, "end": v(-85.54, -31.04) * mm});
            skLineSegment(sketch, "E350", {"start": v(-85.54, -31.04) * mm, "end": v(-84.95, -32.62) * mm});
            skLineSegment(sketch, "E351", {"start": v(-84.95, -32.62) * mm, "end": v(-84.99, -33.1) * mm});
            skLineSegment(sketch, "E352", {"start": v(-84.99, -33.1) * mm, "end": v(-85.08, -33.16) * mm});
            skLineSegment(sketch, "E353", {"start": v(-85.08, -33.16) * mm, "end": v(-85.18, -33.23) * mm});
            skLineSegment(sketch, "E354", {"start": v(-85.18, -33.23) * mm, "end": v(-85.28, -33.3) * mm});
            skLineSegment(sketch, "E355", {"start": v(-85.28, -33.3) * mm, "end": v(-85.38, -33.37) * mm});
            skLineSegment(sketch, "E356", {"start": v(-85.38, -33.37) * mm, "end": v(-85.48, -33.45) * mm});
            skLineSegment(sketch, "E357", {"start": v(-85.48, -33.45) * mm, "end": v(-85.58, -33.53) * mm});
            skLineSegment(sketch, "E358", {"start": v(-85.58, -33.53) * mm, "end": v(-85.69, -33.6) * mm});
            skLineSegment(sketch, "E359", {"start": v(-85.69, -33.6) * mm, "end": v(-85.8, -33.68) * mm});
            skLineSegment(sketch, "E360", {"start": v(-85.8, -33.68) * mm, "end": v(-85.9, -33.77) * mm});
            skLineSegment(sketch, "E361", {"start": v(-85.9, -33.77) * mm, "end": v(-86, -33.85) * mm});
            skLineSegment(sketch, "E362", {"start": v(-86, -33.85) * mm, "end": v(-86.12, -33.94) * mm});
            skLineSegment(sketch, "E363", {"start": v(-86.12, -33.94) * mm, "end": v(-86.23, -34.03) * mm});
            skLineSegment(sketch, "E364", {"start": v(-86.23, -34.03) * mm, "end": v(-86.34, -34.12) * mm});
            skLineSegment(sketch, "E365", {"start": v(-86.34, -34.12) * mm, "end": v(-86.46, -34.21) * mm});
            skLineSegment(sketch, "E366", {"start": v(-86.46, -34.21) * mm, "end": v(-86.58, -34.3) * mm});
            skLineSegment(sketch, "E367", {"start": v(-86.58, -34.3) * mm, "end": v(-86.7, -34.4) * mm});
            skLineSegment(sketch, "E368", {"start": v(-86.7, -34.4) * mm, "end": v(-86.81, -34.5) * mm});
            skLineSegment(sketch, "E369", {"start": v(-86.81, -34.5) * mm, "end": v(-86.93, -34.6) * mm});
            skLineSegment(sketch, "E370", {"start": v(-86.93, -34.6) * mm, "end": v(-87.05, -34.71) * mm});
            skLineSegment(sketch, "E371", {"start": v(-87.05, -34.71) * mm, "end": v(-87.18, -34.82) * mm});
            skLineSegment(sketch, "E372", {"start": v(-87.18, -34.82) * mm, "end": v(-87.3, -34.93) * mm});
            skLineSegment(sketch, "E373", {"start": v(-87.3, -34.93) * mm, "end": v(-87.43, -35.04) * mm});
            skLineSegment(sketch, "E374", {"start": v(-87.43, -35.04) * mm, "end": v(-87.55, -35.15) * mm});
            skLineSegment(sketch, "E375", {"start": v(-87.55, -35.15) * mm, "end": v(-87.68, -35.27) * mm});
            skLineSegment(sketch, "E376", {"start": v(-87.68, -35.27) * mm, "end": v(-87.81, -35.39) * mm});
            skLineSegment(sketch, "E377", {"start": v(-87.81, -35.39) * mm, "end": v(-87.94, -35.5) * mm});
            skLineSegment(sketch, "E378", {"start": v(-87.94, -35.5) * mm, "end": v(-88.07, -35.63) * mm});
            skLineSegment(sketch, "E379", {"start": v(-88.07, -35.63) * mm, "end": v(-88.2, -35.76) * mm});
            skLineSegment(sketch, "E380", {"start": v(-88.2, -35.76) * mm, "end": v(-88.34, -35.88) * mm});
            skLineSegment(sketch, "E381", {"start": v(-88.34, -35.88) * mm, "end": v(-88.48, -36.01) * mm});
            skLineSegment(sketch, "E382", {"start": v(-88.48, -36.01) * mm, "end": v(-88.61, -36.15) * mm});
            skLineSegment(sketch, "E383", {"start": v(-88.61, -36.15) * mm, "end": v(-88.75, -36.28) * mm});
            skLineSegment(sketch, "E384", {"start": v(-88.75, -36.28) * mm, "end": v(-88.89, -36.42) * mm});
            skLineSegment(sketch, "E385", {"start": v(-88.89, -36.42) * mm, "end": v(-89.03, -36.56) * mm});
            skLineSegment(sketch, "E386", {"start": v(-89.03, -36.56) * mm, "end": v(-89.17, -36.7) * mm});
            skLineSegment(sketch, "E387", {"start": v(-89.17, -36.7) * mm, "end": v(-89.3, -36.85) * mm});
            skLineSegment(sketch, "E388", {"start": v(-89.3, -36.85) * mm, "end": v(-89.45, -37) * mm});
            skLineSegment(sketch, "E389", {"start": v(-89.45, -37) * mm, "end": v(-89.6, -37.14) * mm});
            skLineSegment(sketch, "E390", {"start": v(-89.6, -37.14) * mm, "end": v(-89.7, -37.28) * mm});
            skLineSegment(sketch, "E391", {"start": v(-89.7, -37.28) * mm, "end": v(-88.86, -39.26) * mm});
            skLineSegment(sketch, "E392", {"start": v(-88.86, -39.26) * mm, "end": v(-88.68, -39.28) * mm});
            skLineSegment(sketch, "E393", {"start": v(-88.68, -39.28) * mm, "end": v(-88.47, -39.28) * mm});
            skLineSegment(sketch, "E394", {"start": v(-88.47, -39.28) * mm, "end": v(-88.27, -39.28) * mm});
            skLineSegment(sketch, "E395", {"start": v(-88.27, -39.28) * mm, "end": v(-88.06, -39.27) * mm});
            skLineSegment(sketch, "E396", {"start": v(-88.06, -39.27) * mm, "end": v(-87.86, -39.27) * mm});
            skLineSegment(sketch, "E397", {"start": v(-87.86, -39.27) * mm, "end": v(-87.67, -39.27) * mm});
            skLineSegment(sketch, "E398", {"start": v(-87.67, -39.27) * mm, "end": v(-87.47, -39.26) * mm});
            skLineSegment(sketch, "E399", {"start": v(-87.47, -39.26) * mm, "end": v(-87.28, -39.25) * mm});
            skLineSegment(sketch, "E400", {"start": v(-87.28, -39.25) * mm, "end": v(-87.09, -39.25) * mm});
            skLineSegment(sketch, "E401", {"start": v(-87.09, -39.25) * mm, "end": v(-86.9, -39.24) * mm});
            skLineSegment(sketch, "E402", {"start": v(-86.9, -39.24) * mm, "end": v(-86.72, -39.23) * mm});
            skLineSegment(sketch, "E403", {"start": v(-86.72, -39.23) * mm, "end": v(-86.53, -39.22) * mm});
            skLineSegment(sketch, "E404", {"start": v(-86.53, -39.22) * mm, "end": v(-86.35, -39.2) * mm});
            skLineSegment(sketch, "E405", {"start": v(-86.35, -39.2) * mm, "end": v(-86.18, -39.2) * mm});
            skLineSegment(sketch, "E406", {"start": v(-86.18, -39.2) * mm, "end": v(-86, -39.19) * mm});
            skLineSegment(sketch, "E407", {"start": v(-86, -39.19) * mm, "end": v(-85.83, -39.17) * mm});
            skLineSegment(sketch, "E408", {"start": v(-85.83, -39.17) * mm, "end": v(-85.66, -39.16) * mm});
            skLineSegment(sketch, "E409", {"start": v(-85.66, -39.16) * mm, "end": v(-85.5, -39.15) * mm});
            skLineSegment(sketch, "E410", {"start": v(-85.5, -39.15) * mm, "end": v(-85.33, -39.13) * mm});
            skLineSegment(sketch, "E411", {"start": v(-85.33, -39.13) * mm, "end": v(-85.17, -39.11) * mm});
            skLineSegment(sketch, "E412", {"start": v(-85.17, -39.11) * mm, "end": v(-85, -39.1) * mm});
            skLineSegment(sketch, "E413", {"start": v(-85, -39.1) * mm, "end": v(-84.85, -39.08) * mm});
            skLineSegment(sketch, "E414", {"start": v(-84.85, -39.08) * mm, "end": v(-84.7, -39.06) * mm});
            skLineSegment(sketch, "E415", {"start": v(-84.7, -39.06) * mm, "end": v(-84.54, -39.05) * mm});
            skLineSegment(sketch, "E416", {"start": v(-84.54, -39.05) * mm, "end": v(-84.4, -39.03) * mm});
            skLineSegment(sketch, "E417", {"start": v(-84.4, -39.03) * mm, "end": v(-84.25, -39) * mm});
            skLineSegment(sketch, "E418", {"start": v(-84.25, -39) * mm, "end": v(-84.1, -39) * mm});
            skLineSegment(sketch, "E419", {"start": v(-84.1, -39) * mm, "end": v(-83.96, -38.97) * mm});
            skLineSegment(sketch, "E420", {"start": v(-83.96, -38.97) * mm, "end": v(-83.82, -38.95) * mm});
            skLineSegment(sketch, "E421", {"start": v(-83.82, -38.95) * mm, "end": v(-83.69, -38.93) * mm});
            skLineSegment(sketch, "E422", {"start": v(-83.69, -38.93) * mm, "end": v(-83.55, -38.9) * mm});
            skLineSegment(sketch, "E423", {"start": v(-83.55, -38.9) * mm, "end": v(-83.42, -38.89) * mm});
            skLineSegment(sketch, "E424", {"start": v(-83.42, -38.89) * mm, "end": v(-83.3, -38.87) * mm});
            skLineSegment(sketch, "E425", {"start": v(-83.3, -38.87) * mm, "end": v(-83.17, -38.84) * mm});
            skLineSegment(sketch, "E426", {"start": v(-83.17, -38.84) * mm, "end": v(-83.04, -38.82) * mm});
            skLineSegment(sketch, "E427", {"start": v(-83.04, -38.82) * mm, "end": v(-82.92, -38.8) * mm});
            skLineSegment(sketch, "E428", {"start": v(-82.92, -38.8) * mm, "end": v(-82.8, -38.78) * mm});
            skLineSegment(sketch, "E429", {"start": v(-82.8, -38.78) * mm, "end": v(-82.69, -38.76) * mm});
            skLineSegment(sketch, "E430", {"start": v(-82.69, -38.76) * mm, "end": v(-82.57, -38.73) * mm});
            skLineSegment(sketch, "E431", {"start": v(-82.57, -38.73) * mm, "end": v(-82.2, -39.03) * mm});
            skLineSegment(sketch, "E432", {"start": v(-82.2, -39.03) * mm, "end": v(-81.47, -40.55) * mm});
            skLineSegment(sketch, "E433", {"start": v(-81.47, -40.55) * mm, "end": v(-81.46, -41.03) * mm});
            skLineSegment(sketch, "E434", {"start": v(-81.46, -41.03) * mm, "end": v(-81.55, -41.1) * mm});
            skLineSegment(sketch, "E435", {"start": v(-81.55, -41.1) * mm, "end": v(-81.64, -41.18) * mm});
            skLineSegment(sketch, "E436", {"start": v(-81.64, -41.18) * mm, "end": v(-81.73, -41.26) * mm});
            skLineSegment(sketch, "E437", {"start": v(-81.73, -41.26) * mm, "end": v(-81.82, -41.34) * mm});
            skLineSegment(sketch, "E438", {"start": v(-81.82, -41.34) * mm, "end": v(-81.91, -41.42) * mm});
            skLineSegment(sketch, "E439", {"start": v(-81.91, -41.42) * mm, "end": v(-82, -41.5) * mm});
            skLineSegment(sketch, "E440", {"start": v(-82, -41.5) * mm, "end": v(-82.1, -41.6) * mm});
            skLineSegment(sketch, "E441", {"start": v(-82.1, -41.6) * mm, "end": v(-82.2, -41.69) * mm});
            skLineSegment(sketch, "E442", {"start": v(-82.2, -41.69) * mm, "end": v(-82.3, -41.78) * mm});
            skLineSegment(sketch, "E443", {"start": v(-82.3, -41.78) * mm, "end": v(-82.4, -41.87) * mm});
            skLineSegment(sketch, "E444", {"start": v(-82.4, -41.87) * mm, "end": v(-82.5, -41.97) * mm});
            skLineSegment(sketch, "E445", {"start": v(-82.5, -41.97) * mm, "end": v(-82.6, -42.07) * mm});
            skLineSegment(sketch, "E446", {"start": v(-82.6, -42.07) * mm, "end": v(-82.7, -42.17) * mm});
            skLineSegment(sketch, "E447", {"start": v(-82.7, -42.17) * mm, "end": v(-82.82, -42.28) * mm});
            skLineSegment(sketch, "E448", {"start": v(-82.82, -42.28) * mm, "end": v(-82.92, -42.38) * mm});
            skLineSegment(sketch, "E449", {"start": v(-82.92, -42.38) * mm, "end": v(-83.03, -42.5) * mm});
            skLineSegment(sketch, "E450", {"start": v(-83.03, -42.5) * mm, "end": v(-83.14, -42.6) * mm});
            skLineSegment(sketch, "E451", {"start": v(-83.14, -42.6) * mm, "end": v(-83.25, -42.71) * mm});
            skLineSegment(sketch, "E452", {"start": v(-83.25, -42.71) * mm, "end": v(-83.36, -42.83) * mm});
            skLineSegment(sketch, "E453", {"start": v(-83.36, -42.83) * mm, "end": v(-83.47, -42.95) * mm});
            skLineSegment(sketch, "E454", {"start": v(-83.47, -42.95) * mm, "end": v(-83.59, -43.07) * mm});
            skLineSegment(sketch, "E455", {"start": v(-83.59, -43.07) * mm, "end": v(-83.7, -43.2) * mm});
            skLineSegment(sketch, "E456", {"start": v(-83.7, -43.2) * mm, "end": v(-83.82, -43.32) * mm});
            skLineSegment(sketch, "E457", {"start": v(-83.82, -43.32) * mm, "end": v(-83.93, -43.44) * mm});
            skLineSegment(sketch, "E458", {"start": v(-83.93, -43.44) * mm, "end": v(-84.05, -43.57) * mm});
            skLineSegment(sketch, "E459", {"start": v(-84.05, -43.57) * mm, "end": v(-84.17, -43.7) * mm});
            skLineSegment(sketch, "E460", {"start": v(-84.17, -43.7) * mm, "end": v(-84.29, -43.84) * mm});
            skLineSegment(sketch, "E461", {"start": v(-84.29, -43.84) * mm, "end": v(-84.4, -43.98) * mm});
            skLineSegment(sketch, "E462", {"start": v(-84.4, -43.98) * mm, "end": v(-84.53, -44.12) * mm});
            skLineSegment(sketch, "E463", {"start": v(-84.53, -44.12) * mm, "end": v(-84.65, -44.26) * mm});
            skLineSegment(sketch, "E464", {"start": v(-84.65, -44.26) * mm, "end": v(-84.77, -44.4) * mm});
            skLineSegment(sketch, "E465", {"start": v(-84.77, -44.4) * mm, "end": v(-84.9, -44.55) * mm});
            skLineSegment(sketch, "E466", {"start": v(-84.9, -44.55) * mm, "end": v(-85.02, -44.7) * mm});
            skLineSegment(sketch, "E467", {"start": v(-85.02, -44.7) * mm, "end": v(-85.15, -44.86) * mm});
            skLineSegment(sketch, "E468", {"start": v(-85.15, -44.86) * mm, "end": v(-85.27, -45.01) * mm});
            skLineSegment(sketch, "E469", {"start": v(-85.27, -45.01) * mm, "end": v(-85.4, -45.17) * mm});
            skLineSegment(sketch, "E470", {"start": v(-85.4, -45.17) * mm, "end": v(-85.53, -45.33) * mm});
            skLineSegment(sketch, "E471", {"start": v(-85.53, -45.33) * mm, "end": v(-85.66, -45.5) * mm});
            skLineSegment(sketch, "E472", {"start": v(-85.66, -45.5) * mm, "end": v(-85.75, -45.64) * mm});
            skLineSegment(sketch, "E473", {"start": v(-85.75, -45.64) * mm, "end": v(-84.72, -47.53) * mm});
            skLineSegment(sketch, "E474", {"start": v(-84.72, -47.53) * mm, "end": v(-84.54, -47.53) * mm});
            skLineSegment(sketch, "E475", {"start": v(-84.54, -47.53) * mm, "end": v(-84.34, -47.5) * mm});
            skLineSegment(sketch, "E476", {"start": v(-84.34, -47.5) * mm, "end": v(-84.13, -47.49) * mm});
            skLineSegment(sketch, "E477", {"start": v(-84.13, -47.49) * mm, "end": v(-83.93, -47.47) * mm});
            skLineSegment(sketch, "E478", {"start": v(-83.93, -47.47) * mm, "end": v(-83.73, -47.44) * mm});
            skLineSegment(sketch, "E479", {"start": v(-83.73, -47.44) * mm, "end": v(-83.54, -47.42) * mm});
            skLineSegment(sketch, "E480", {"start": v(-83.54, -47.42) * mm, "end": v(-83.34, -47.4) * mm});
            skLineSegment(sketch, "E481", {"start": v(-83.34, -47.4) * mm, "end": v(-83.15, -47.37) * mm});
            skLineSegment(sketch, "E482", {"start": v(-83.15, -47.37) * mm, "end": v(-82.96, -47.35) * mm});
            skLineSegment(sketch, "E483", {"start": v(-82.96, -47.35) * mm, "end": v(-82.78, -47.32) * mm});
            skLineSegment(sketch, "E484", {"start": v(-82.78, -47.32) * mm, "end": v(-82.6, -47.3) * mm});
            skLineSegment(sketch, "E485", {"start": v(-82.6, -47.3) * mm, "end": v(-82.41, -47.27) * mm});
            skLineSegment(sketch, "E486", {"start": v(-82.41, -47.27) * mm, "end": v(-82.24, -47.24) * mm});
            skLineSegment(sketch, "E487", {"start": v(-82.24, -47.24) * mm, "end": v(-82.06, -47.21) * mm});
            skLineSegment(sketch, "E488", {"start": v(-82.06, -47.21) * mm, "end": v(-81.89, -47.18) * mm});
            skLineSegment(sketch, "E489", {"start": v(-81.89, -47.18) * mm, "end": v(-81.72, -47.15) * mm});
            skLineSegment(sketch, "E490", {"start": v(-81.72, -47.15) * mm, "end": v(-81.55, -47.12) * mm});
            skLineSegment(sketch, "E491", {"start": v(-81.55, -47.12) * mm, "end": v(-81.39, -47.1) * mm});
            skLineSegment(sketch, "E492", {"start": v(-81.39, -47.1) * mm, "end": v(-81.22, -47.06) * mm});
            skLineSegment(sketch, "E493", {"start": v(-81.22, -47.06) * mm, "end": v(-81.06, -47.03) * mm});
            skLineSegment(sketch, "E494", {"start": v(-81.06, -47.03) * mm, "end": v(-80.9, -47) * mm});
            skLineSegment(sketch, "E495", {"start": v(-80.9, -47) * mm, "end": v(-80.75, -46.97) * mm});
            skLineSegment(sketch, "E496", {"start": v(-80.75, -46.97) * mm, "end": v(-80.6, -46.94) * mm});
            skLineSegment(sketch, "E497", {"start": v(-80.6, -46.94) * mm, "end": v(-80.45, -46.9) * mm});
            skLineSegment(sketch, "E498", {"start": v(-80.45, -46.9) * mm, "end": v(-80.3, -46.87) * mm});
            skLineSegment(sketch, "E499", {"start": v(-80.3, -46.87) * mm, "end": v(-80.16, -46.84) * mm});
            skLineSegment(sketch, "E500", {"start": v(-80.16, -46.84) * mm, "end": v(-80.02, -46.8) * mm});
            skLineSegment(sketch, "E501", {"start": v(-80.02, -46.8) * mm, "end": v(-79.88, -46.77) * mm});
            skLineSegment(sketch, "E502", {"start": v(-79.88, -46.77) * mm, "end": v(-79.74, -46.74) * mm});
            skLineSegment(sketch, "E503", {"start": v(-79.74, -46.74) * mm, "end": v(-79.6, -46.7) * mm});
            skLineSegment(sketch, "E504", {"start": v(-79.6, -46.7) * mm, "end": v(-79.48, -46.68) * mm});
            skLineSegment(sketch, "E505", {"start": v(-79.48, -46.68) * mm, "end": v(-79.35, -46.64) * mm});
            skLineSegment(sketch, "E506", {"start": v(-79.35, -46.64) * mm, "end": v(-79.22, -46.6) * mm});
            skLineSegment(sketch, "E507", {"start": v(-79.22, -46.6) * mm, "end": v(-79.1, -46.57) * mm});
            skLineSegment(sketch, "E508", {"start": v(-79.1, -46.57) * mm, "end": v(-78.98, -46.54) * mm});
            skLineSegment(sketch, "E509", {"start": v(-78.98, -46.54) * mm, "end": v(-78.86, -46.5) * mm});
            skLineSegment(sketch, "E510", {"start": v(-78.86, -46.5) * mm, "end": v(-78.74, -46.47) * mm});
            skLineSegment(sketch, "E511", {"start": v(-78.74, -46.47) * mm, "end": v(-78.63, -46.44) * mm});
            skLineSegment(sketch, "E512", {"start": v(-78.63, -46.44) * mm, "end": v(-78.52, -46.4) * mm});
            skLineSegment(sketch, "E513", {"start": v(-78.52, -46.4) * mm, "end": v(-78.12, -46.67) * mm});
            skLineSegment(sketch, "E514", {"start": v(-78.12, -46.67) * mm, "end": v(-77.24, -48.11) * mm});
            skLineSegment(sketch, "E515", {"start": v(-77.24, -48.11) * mm, "end": v(-77.19, -48.58) * mm});
            skLineSegment(sketch, "E516", {"start": v(-77.19, -48.58) * mm, "end": v(-77.27, -48.67) * mm});
            skLineSegment(sketch, "E517", {"start": v(-77.27, -48.67) * mm, "end": v(-77.35, -48.75) * mm});
            skLineSegment(sketch, "E518", {"start": v(-77.35, -48.75) * mm, "end": v(-77.43, -48.84) * mm});
            skLineSegment(sketch, "E519", {"start": v(-77.43, -48.84) * mm, "end": v(-77.52, -48.93) * mm});
            skLineSegment(sketch, "E520", {"start": v(-77.52, -48.93) * mm, "end": v(-77.6, -49.02) * mm});
            skLineSegment(sketch, "E521", {"start": v(-77.6, -49.02) * mm, "end": v(-77.7, -49.12) * mm});
            skLineSegment(sketch, "E522", {"start": v(-77.7, -49.12) * mm, "end": v(-77.78, -49.21) * mm});
            skLineSegment(sketch, "E523", {"start": v(-77.78, -49.21) * mm, "end": v(-77.87, -49.31) * mm});
            skLineSegment(sketch, "E524", {"start": v(-77.87, -49.31) * mm, "end": v(-77.96, -49.41) * mm});
            skLineSegment(sketch, "E525", {"start": v(-77.96, -49.41) * mm, "end": v(-78.05, -49.52) * mm});
            skLineSegment(sketch, "E526", {"start": v(-78.05, -49.52) * mm, "end": v(-78.14, -49.62) * mm});
            skLineSegment(sketch, "E527", {"start": v(-78.14, -49.62) * mm, "end": v(-78.23, -49.73) * mm});
            skLineSegment(sketch, "E528", {"start": v(-78.23, -49.73) * mm, "end": v(-78.33, -49.84) * mm});
            skLineSegment(sketch, "E529", {"start": v(-78.33, -49.84) * mm, "end": v(-78.42, -49.96) * mm});
            skLineSegment(sketch, "E530", {"start": v(-78.42, -49.96) * mm, "end": v(-78.52, -50.07) * mm});
            skLineSegment(sketch, "E531", {"start": v(-78.52, -50.07) * mm, "end": v(-78.61, -50.2) * mm});
            skLineSegment(sketch, "E532", {"start": v(-78.61, -50.2) * mm, "end": v(-78.71, -50.31) * mm});
            skLineSegment(sketch, "E533", {"start": v(-78.71, -50.31) * mm, "end": v(-78.81, -50.43) * mm});
            skLineSegment(sketch, "E534", {"start": v(-78.81, -50.43) * mm, "end": v(-78.91, -50.56) * mm});
            skLineSegment(sketch, "E535", {"start": v(-78.91, -50.56) * mm, "end": v(-79.01, -50.69) * mm});
            skLineSegment(sketch, "E536", {"start": v(-79.01, -50.69) * mm, "end": v(-79.11, -50.82) * mm});
            skLineSegment(sketch, "E537", {"start": v(-79.11, -50.82) * mm, "end": v(-79.22, -50.95) * mm});
            skLineSegment(sketch, "E538", {"start": v(-79.22, -50.95) * mm, "end": v(-79.32, -51.09) * mm});
            skLineSegment(sketch, "E539", {"start": v(-79.32, -51.09) * mm, "end": v(-79.42, -51.23) * mm});
            skLineSegment(sketch, "E540", {"start": v(-79.42, -51.23) * mm, "end": v(-79.53, -51.37) * mm});
            skLineSegment(sketch, "E541", {"start": v(-79.53, -51.37) * mm, "end": v(-79.63, -51.5) * mm});
            skLineSegment(sketch, "E542", {"start": v(-79.63, -51.5) * mm, "end": v(-79.74, -51.65) * mm});
            skLineSegment(sketch, "E543", {"start": v(-79.74, -51.65) * mm, "end": v(-79.85, -51.8) * mm});
            skLineSegment(sketch, "E544", {"start": v(-79.85, -51.8) * mm, "end": v(-79.95, -51.95) * mm});
            skLineSegment(sketch, "E545", {"start": v(-79.95, -51.95) * mm, "end": v(-80.06, -52.1) * mm});
            skLineSegment(sketch, "E546", {"start": v(-80.06, -52.1) * mm, "end": v(-80.17, -52.26) * mm});
            skLineSegment(sketch, "E547", {"start": v(-80.17, -52.26) * mm, "end": v(-80.28, -52.42) * mm});
            skLineSegment(sketch, "E548", {"start": v(-80.28, -52.42) * mm, "end": v(-80.39, -52.58) * mm});
            skLineSegment(sketch, "E549", {"start": v(-80.39, -52.58) * mm, "end": v(-80.5, -52.75) * mm});
            skLineSegment(sketch, "E550", {"start": v(-80.5, -52.75) * mm, "end": v(-80.6, -52.91) * mm});
            skLineSegment(sketch, "E551", {"start": v(-80.6, -52.91) * mm, "end": v(-80.72, -53.08) * mm});
            skLineSegment(sketch, "E552", {"start": v(-80.72, -53.08) * mm, "end": v(-80.83, -53.25) * mm});
            skLineSegment(sketch, "E553", {"start": v(-80.83, -53.25) * mm, "end": v(-80.94, -53.43) * mm});
            skLineSegment(sketch, "E554", {"start": v(-80.94, -53.43) * mm, "end": v(-81.03, -53.59) * mm});
            skLineSegment(sketch, "E555", {"start": v(-81.03, -53.59) * mm, "end": v(-79.82, -55.37) * mm});
            skLineSegment(sketch, "E556", {"start": v(-79.82, -55.37) * mm, "end": v(-79.64, -55.35) * mm});
            skLineSegment(sketch, "E557", {"start": v(-79.64, -55.35) * mm, "end": v(-79.44, -55.31) * mm});
            skLineSegment(sketch, "E558", {"start": v(-79.44, -55.31) * mm, "end": v(-79.24, -55.27) * mm});
            skLineSegment(sketch, "E559", {"start": v(-79.24, -55.27) * mm, "end": v(-79.04, -55.23) * mm});
            skLineSegment(sketch, "E560", {"start": v(-79.04, -55.23) * mm, "end": v(-78.84, -55.19) * mm});
            skLineSegment(sketch, "E561", {"start": v(-78.84, -55.19) * mm, "end": v(-78.65, -55.15) * mm});
            skLineSegment(sketch, "E562", {"start": v(-78.65, -55.15) * mm, "end": v(-78.46, -55.1) * mm});
            skLineSegment(sketch, "E563", {"start": v(-78.46, -55.1) * mm, "end": v(-78.27, -55.06) * mm});
            skLineSegment(sketch, "E564", {"start": v(-78.27, -55.06) * mm, "end": v(-78.09, -55.02) * mm});
            skLineSegment(sketch, "E565", {"start": v(-78.09, -55.02) * mm, "end": v(-77.9, -54.98) * mm});
            skLineSegment(sketch, "E566", {"start": v(-77.9, -54.98) * mm, "end": v(-77.73, -54.93) * mm});
            skLineSegment(sketch, "E567", {"start": v(-77.73, -54.93) * mm, "end": v(-77.55, -54.89) * mm});
            skLineSegment(sketch, "E568", {"start": v(-77.55, -54.89) * mm, "end": v(-77.37, -54.84) * mm});
            skLineSegment(sketch, "E569", {"start": v(-77.37, -54.84) * mm, "end": v(-77.2, -54.8) * mm});
            skLineSegment(sketch, "E570", {"start": v(-77.2, -54.8) * mm, "end": v(-77.03, -54.75) * mm});
            skLineSegment(sketch, "E571", {"start": v(-77.03, -54.75) * mm, "end": v(-76.87, -54.7) * mm});
            skLineSegment(sketch, "E572", {"start": v(-76.87, -54.7) * mm, "end": v(-76.7, -54.66) * mm});
            skLineSegment(sketch, "E573", {"start": v(-76.7, -54.66) * mm, "end": v(-76.54, -54.62) * mm});
            skLineSegment(sketch, "E574", {"start": v(-76.54, -54.62) * mm, "end": v(-76.38, -54.57) * mm});
            skLineSegment(sketch, "E575", {"start": v(-76.38, -54.57) * mm, "end": v(-76.23, -54.53) * mm});
            skLineSegment(sketch, "E576", {"start": v(-76.23, -54.53) * mm, "end": v(-76.07, -54.48) * mm});
            skLineSegment(sketch, "E577", {"start": v(-76.07, -54.48) * mm, "end": v(-75.92, -54.43) * mm});
            skLineSegment(sketch, "E578", {"start": v(-75.92, -54.43) * mm, "end": v(-75.77, -54.39) * mm});
            skLineSegment(sketch, "E579", {"start": v(-75.77, -54.39) * mm, "end": v(-75.63, -54.34) * mm});
            skLineSegment(sketch, "E580", {"start": v(-75.63, -54.34) * mm, "end": v(-75.48, -54.3) * mm});
            skLineSegment(sketch, "E581", {"start": v(-75.48, -54.3) * mm, "end": v(-75.34, -54.25) * mm});
            skLineSegment(sketch, "E582", {"start": v(-75.34, -54.25) * mm, "end": v(-75.2, -54.2) * mm});
            skLineSegment(sketch, "E583", {"start": v(-75.2, -54.2) * mm, "end": v(-75.07, -54.16) * mm});
            skLineSegment(sketch, "E584", {"start": v(-75.07, -54.16) * mm, "end": v(-74.94, -54.1) * mm});
            skLineSegment(sketch, "E585", {"start": v(-74.94, -54.1) * mm, "end": v(-74.8, -54.06) * mm});
            skLineSegment(sketch, "E586", {"start": v(-74.8, -54.06) * mm, "end": v(-74.68, -54.02) * mm});
            skLineSegment(sketch, "E587", {"start": v(-74.68, -54.02) * mm, "end": v(-74.55, -53.97) * mm});
            skLineSegment(sketch, "E588", {"start": v(-74.55, -53.97) * mm, "end": v(-74.43, -53.93) * mm});
            skLineSegment(sketch, "E589", {"start": v(-74.43, -53.93) * mm, "end": v(-74.31, -53.88) * mm});
            skLineSegment(sketch, "E590", {"start": v(-74.31, -53.88) * mm, "end": v(-74.2, -53.84) * mm});
            skLineSegment(sketch, "E591", {"start": v(-74.2, -53.84) * mm, "end": v(-74.08, -53.8) * mm});
            skLineSegment(sketch, "E592", {"start": v(-74.08, -53.8) * mm, "end": v(-73.97, -53.75) * mm});
            skLineSegment(sketch, "E593", {"start": v(-73.97, -53.75) * mm, "end": v(-73.86, -53.7) * mm});
            skLineSegment(sketch, "E594", {"start": v(-73.86, -53.7) * mm, "end": v(-73.75, -53.66) * mm});
            skLineSegment(sketch, "E595", {"start": v(-73.75, -53.66) * mm, "end": v(-73.33, -53.88) * mm});
            skLineSegment(sketch, "E596", {"start": v(-73.33, -53.88) * mm, "end": v(-72.32, -55.24) * mm});
            skLineSegment(sketch, "E597", {"start": v(-72.32, -55.24) * mm, "end": v(-72.22, -55.7) * mm});
            skLineSegment(sketch, "E598", {"start": v(-72.22, -55.7) * mm, "end": v(-72.3, -55.8) * mm});
            skLineSegment(sketch, "E599", {"start": v(-72.3, -55.8) * mm, "end": v(-72.37, -55.88) * mm});
            skLineSegment(sketch, "E600", {"start": v(-72.37, -55.88) * mm, "end": v(-72.44, -55.98) * mm});
            skLineSegment(sketch, "E601", {"start": v(-72.44, -55.98) * mm, "end": v(-72.52, -56.08) * mm});
            skLineSegment(sketch, "E602", {"start": v(-72.52, -56.08) * mm, "end": v(-72.6, -56.18) * mm});
            skLineSegment(sketch, "E603", {"start": v(-72.6, -56.18) * mm, "end": v(-72.67, -56.28) * mm});
            skLineSegment(sketch, "E604", {"start": v(-72.67, -56.28) * mm, "end": v(-72.75, -56.38) * mm});
            skLineSegment(sketch, "E605", {"start": v(-72.75, -56.38) * mm, "end": v(-72.83, -56.5) * mm});
            skLineSegment(sketch, "E606", {"start": v(-72.83, -56.5) * mm, "end": v(-72.9, -56.6) * mm});
            skLineSegment(sketch, "E607", {"start": v(-72.9, -56.6) * mm, "end": v(-72.99, -56.71) * mm});
            skLineSegment(sketch, "E608", {"start": v(-72.99, -56.71) * mm, "end": v(-73.07, -56.83) * mm});
            skLineSegment(sketch, "E609", {"start": v(-73.07, -56.83) * mm, "end": v(-73.15, -56.94) * mm});
            skLineSegment(sketch, "E610", {"start": v(-73.15, -56.94) * mm, "end": v(-73.23, -57.06) * mm});
            skLineSegment(sketch, "E611", {"start": v(-73.23, -57.06) * mm, "end": v(-73.32, -57.19) * mm});
            skLineSegment(sketch, "E612", {"start": v(-73.32, -57.19) * mm, "end": v(-73.4, -57.3) * mm});
            skLineSegment(sketch, "E613", {"start": v(-73.4, -57.3) * mm, "end": v(-73.49, -57.44) * mm});
            skLineSegment(sketch, "E614", {"start": v(-73.49, -57.44) * mm, "end": v(-73.57, -57.57) * mm});
            skLineSegment(sketch, "E615", {"start": v(-73.57, -57.57) * mm, "end": v(-73.66, -57.7) * mm});
            skLineSegment(sketch, "E616", {"start": v(-73.66, -57.7) * mm, "end": v(-73.75, -57.83) * mm});
            skLineSegment(sketch, "E617", {"start": v(-73.75, -57.83) * mm, "end": v(-73.84, -57.97) * mm});
            skLineSegment(sketch, "E618", {"start": v(-73.84, -57.97) * mm, "end": v(-73.92, -58.1) * mm});
            skLineSegment(sketch, "E619", {"start": v(-73.92, -58.1) * mm, "end": v(-74.01, -58.25) * mm});
            skLineSegment(sketch, "E620", {"start": v(-74.01, -58.25) * mm, "end": v(-74.1, -58.4) * mm});
            skLineSegment(sketch, "E621", {"start": v(-74.1, -58.4) * mm, "end": v(-74.2, -58.54) * mm});
            skLineSegment(sketch, "E622", {"start": v(-74.2, -58.54) * mm, "end": v(-74.28, -58.7) * mm});
            skLineSegment(sketch, "E623", {"start": v(-74.28, -58.7) * mm, "end": v(-74.38, -58.85) * mm});
            skLineSegment(sketch, "E624", {"start": v(-74.38, -58.85) * mm, "end": v(-74.47, -59) * mm});
            skLineSegment(sketch, "E625", {"start": v(-74.47, -59) * mm, "end": v(-74.56, -59.16) * mm});
            skLineSegment(sketch, "E626", {"start": v(-74.56, -59.16) * mm, "end": v(-74.65, -59.32) * mm});
            skLineSegment(sketch, "E627", {"start": v(-74.65, -59.32) * mm, "end": v(-74.75, -59.48) * mm});
            skLineSegment(sketch, "E628", {"start": v(-74.75, -59.48) * mm, "end": v(-74.84, -59.65) * mm});
            skLineSegment(sketch, "E629", {"start": v(-74.84, -59.65) * mm, "end": v(-74.93, -59.82) * mm});
            skLineSegment(sketch, "E630", {"start": v(-74.93, -59.82) * mm, "end": v(-75.03, -59.99) * mm});
            skLineSegment(sketch, "E631", {"start": v(-75.03, -59.99) * mm, "end": v(-75.12, -60.16) * mm});
            skLineSegment(sketch, "E632", {"start": v(-75.12, -60.16) * mm, "end": v(-75.21, -60.34) * mm});
            skLineSegment(sketch, "E633", {"start": v(-75.21, -60.34) * mm, "end": v(-75.3, -60.52) * mm});
            skLineSegment(sketch, "E634", {"start": v(-75.3, -60.52) * mm, "end": v(-75.4, -60.7) * mm});
            skLineSegment(sketch, "E635", {"start": v(-75.4, -60.7) * mm, "end": v(-75.5, -60.88) * mm});
            skLineSegment(sketch, "E636", {"start": v(-75.5, -60.88) * mm, "end": v(-75.57, -61.05) * mm});
            skLineSegment(sketch, "E637", {"start": v(-75.57, -61.05) * mm, "end": v(-74.2, -62.7) * mm});
            skLineSegment(sketch, "E638", {"start": v(-74.2, -62.7) * mm, "end": v(-74.02, -62.67) * mm});
            skLineSegment(sketch, "E639", {"start": v(-74.02, -62.67) * mm, "end": v(-73.82, -62.61) * mm});
            skLineSegment(sketch, "E640", {"start": v(-73.82, -62.61) * mm, "end": v(-73.63, -62.55) * mm});
            skLineSegment(sketch, "E641", {"start": v(-73.63, -62.55) * mm, "end": v(-73.43, -62.5) * mm});
            skLineSegment(sketch, "E642", {"start": v(-73.43, -62.5) * mm, "end": v(-73.24, -62.43) * mm});
            skLineSegment(sketch, "E643", {"start": v(-73.24, -62.43) * mm, "end": v(-73.05, -62.37) * mm});
            skLineSegment(sketch, "E644", {"start": v(-73.05, -62.37) * mm, "end": v(-72.87, -62.31) * mm});
            skLineSegment(sketch, "E645", {"start": v(-72.87, -62.31) * mm, "end": v(-72.68, -62.25) * mm});
            skLineSegment(sketch, "E646", {"start": v(-72.68, -62.25) * mm, "end": v(-72.5, -62.2) * mm});
            skLineSegment(sketch, "E647", {"start": v(-72.5, -62.2) * mm, "end": v(-72.33, -62.13) * mm});
            skLineSegment(sketch, "E648", {"start": v(-72.33, -62.13) * mm, "end": v(-72.15, -62.07) * mm});
            skLineSegment(sketch, "E649", {"start": v(-72.15, -62.07) * mm, "end": v(-71.98, -62.01) * mm});
            skLineSegment(sketch, "E650", {"start": v(-71.98, -62.01) * mm, "end": v(-71.81, -61.95) * mm});
            skLineSegment(sketch, "E651", {"start": v(-71.81, -61.95) * mm, "end": v(-71.64, -61.89) * mm});
            skLineSegment(sketch, "E652", {"start": v(-71.64, -61.89) * mm, "end": v(-71.48, -61.83) * mm});
            skLineSegment(sketch, "E653", {"start": v(-71.48, -61.83) * mm, "end": v(-71.32, -61.77) * mm});
            skLineSegment(sketch, "E654", {"start": v(-71.32, -61.77) * mm, "end": v(-71.16, -61.7) * mm});
            skLineSegment(sketch, "E655", {"start": v(-71.16, -61.7) * mm, "end": v(-71, -61.65) * mm});
            skLineSegment(sketch, "E656", {"start": v(-71, -61.65) * mm, "end": v(-70.85, -61.59) * mm});
            skLineSegment(sketch, "E657", {"start": v(-70.85, -61.59) * mm, "end": v(-70.7, -61.52) * mm});
            skLineSegment(sketch, "E658", {"start": v(-70.7, -61.52) * mm, "end": v(-70.55, -61.46) * mm});
            skLineSegment(sketch, "E659", {"start": v(-70.55, -61.46) * mm, "end": v(-70.4, -61.4) * mm});
            skLineSegment(sketch, "E660", {"start": v(-70.4, -61.4) * mm, "end": v(-70.26, -61.34) * mm});
            skLineSegment(sketch, "E661", {"start": v(-70.26, -61.34) * mm, "end": v(-70.12, -61.28) * mm});
            skLineSegment(sketch, "E662", {"start": v(-70.12, -61.28) * mm, "end": v(-69.98, -61.22) * mm});
            skLineSegment(sketch, "E663", {"start": v(-69.98, -61.22) * mm, "end": v(-69.85, -61.16) * mm});
            skLineSegment(sketch, "E664", {"start": v(-69.85, -61.16) * mm, "end": v(-69.71, -61.1) * mm});
            skLineSegment(sketch, "E665", {"start": v(-69.71, -61.1) * mm, "end": v(-69.58, -61.05) * mm});
            skLineSegment(sketch, "E666", {"start": v(-69.58, -61.05) * mm, "end": v(-69.45, -60.99) * mm});
            skLineSegment(sketch, "E667", {"start": v(-69.45, -60.99) * mm, "end": v(-69.33, -60.93) * mm});
            skLineSegment(sketch, "E668", {"start": v(-69.33, -60.93) * mm, "end": v(-69.2, -60.87) * mm});
            skLineSegment(sketch, "E669", {"start": v(-69.2, -60.87) * mm, "end": v(-69.09, -60.82) * mm});
            skLineSegment(sketch, "E670", {"start": v(-69.09, -60.82) * mm, "end": v(-68.97, -60.76) * mm});
            skLineSegment(sketch, "E671", {"start": v(-68.97, -60.76) * mm, "end": v(-68.85, -60.7) * mm});
            skLineSegment(sketch, "E672", {"start": v(-68.85, -60.7) * mm, "end": v(-68.74, -60.65) * mm});
            skLineSegment(sketch, "E673", {"start": v(-68.74, -60.65) * mm, "end": v(-68.63, -60.6) * mm});
            skLineSegment(sketch, "E674", {"start": v(-68.63, -60.6) * mm, "end": v(-68.52, -60.54) * mm});
            skLineSegment(sketch, "E675", {"start": v(-68.52, -60.54) * mm, "end": v(-68.42, -60.48) * mm});
            skLineSegment(sketch, "E676", {"start": v(-68.42, -60.48) * mm, "end": v(-68.32, -60.43) * mm});
            skLineSegment(sketch, "E677", {"start": v(-68.32, -60.43) * mm, "end": v(-67.88, -60.61) * mm});
            skLineSegment(sketch, "E678", {"start": v(-67.88, -60.61) * mm, "end": v(-66.74, -61.86) * mm});
            skLineSegment(sketch, "E679", {"start": v(-66.74, -61.86) * mm, "end": v(-66.6, -62.31) * mm});
            skLineSegment(sketch, "E680", {"start": v(-66.6, -62.31) * mm, "end": v(-66.66, -62.41) * mm});
            skLineSegment(sketch, "E681", {"start": v(-66.66, -62.41) * mm, "end": v(-66.73, -62.5) * mm});
            skLineSegment(sketch, "E682", {"start": v(-66.73, -62.5) * mm, "end": v(-66.8, -62.61) * mm});
            skLineSegment(sketch, "E683", {"start": v(-66.8, -62.61) * mm, "end": v(-66.86, -62.72) * mm});
            skLineSegment(sketch, "E684", {"start": v(-66.86, -62.72) * mm, "end": v(-66.92, -62.82) * mm});
            skLineSegment(sketch, "E685", {"start": v(-66.92, -62.82) * mm, "end": v(-67, -62.93) * mm});
            skLineSegment(sketch, "E686", {"start": v(-67, -62.93) * mm, "end": v(-67.06, -63.04) * mm});
            skLineSegment(sketch, "E687", {"start": v(-67.06, -63.04) * mm, "end": v(-67.13, -63.16) * mm});
            skLineSegment(sketch, "E688", {"start": v(-67.13, -63.16) * mm, "end": v(-67.2, -63.27) * mm});
            skLineSegment(sketch, "E689", {"start": v(-67.2, -63.27) * mm, "end": v(-67.27, -63.4) * mm});
            skLineSegment(sketch, "E690", {"start": v(-67.27, -63.4) * mm, "end": v(-67.34, -63.52) * mm});
            skLineSegment(sketch, "E691", {"start": v(-67.34, -63.52) * mm, "end": v(-67.4, -63.64) * mm});
            skLineSegment(sketch, "E692", {"start": v(-67.4, -63.64) * mm, "end": v(-67.48, -63.77) * mm});
            skLineSegment(sketch, "E693", {"start": v(-67.48, -63.77) * mm, "end": v(-67.55, -63.9) * mm});
            skLineSegment(sketch, "E694", {"start": v(-67.55, -63.9) * mm, "end": v(-67.62, -64.03) * mm});
            skLineSegment(sketch, "E695", {"start": v(-67.62, -64.03) * mm, "end": v(-67.7, -64.16) * mm});
            skLineSegment(sketch, "E696", {"start": v(-67.7, -64.16) * mm, "end": v(-67.77, -64.3) * mm});
            skLineSegment(sketch, "E697", {"start": v(-67.77, -64.3) * mm, "end": v(-67.84, -64.44) * mm});
            skLineSegment(sketch, "E698", {"start": v(-67.84, -64.44) * mm, "end": v(-67.92, -64.58) * mm});
            skLineSegment(sketch, "E699", {"start": v(-67.92, -64.58) * mm, "end": v(-68, -64.73) * mm});
            skLineSegment(sketch, "E700", {"start": v(-68, -64.73) * mm, "end": v(-68.07, -64.87) * mm});
            skLineSegment(sketch, "E701", {"start": v(-68.07, -64.87) * mm, "end": v(-68.14, -65.02) * mm});
            skLineSegment(sketch, "E702", {"start": v(-68.14, -65.02) * mm, "end": v(-68.22, -65.18) * mm});
            skLineSegment(sketch, "E703", {"start": v(-68.22, -65.18) * mm, "end": v(-68.3, -65.33) * mm});
            skLineSegment(sketch, "E704", {"start": v(-68.3, -65.33) * mm, "end": v(-68.37, -65.49) * mm});
            skLineSegment(sketch, "E705", {"start": v(-68.37, -65.49) * mm, "end": v(-68.45, -65.65) * mm});
            skLineSegment(sketch, "E706", {"start": v(-68.45, -65.65) * mm, "end": v(-68.52, -65.81) * mm});
            skLineSegment(sketch, "E707", {"start": v(-68.52, -65.81) * mm, "end": v(-68.6, -65.98) * mm});
            skLineSegment(sketch, "E708", {"start": v(-68.6, -65.98) * mm, "end": v(-68.68, -66.15) * mm});
            skLineSegment(sketch, "E709", {"start": v(-68.68, -66.15) * mm, "end": v(-68.75, -66.32) * mm});
            skLineSegment(sketch, "E710", {"start": v(-68.75, -66.32) * mm, "end": v(-68.83, -66.5) * mm});
            skLineSegment(sketch, "E711", {"start": v(-68.83, -66.5) * mm, "end": v(-68.9, -66.67) * mm});
            skLineSegment(sketch, "E712", {"start": v(-68.9, -66.67) * mm, "end": v(-68.98, -66.85) * mm});
            skLineSegment(sketch, "E713", {"start": v(-68.98, -66.85) * mm, "end": v(-69.06, -67.03) * mm});
            skLineSegment(sketch, "E714", {"start": v(-69.06, -67.03) * mm, "end": v(-69.14, -67.21) * mm});
            skLineSegment(sketch, "E715", {"start": v(-69.14, -67.21) * mm, "end": v(-69.22, -67.4) * mm});
            skLineSegment(sketch, "E716", {"start": v(-69.22, -67.4) * mm, "end": v(-69.3, -67.59) * mm});
            skLineSegment(sketch, "E717", {"start": v(-69.3, -67.59) * mm, "end": v(-69.37, -67.78) * mm});
            skLineSegment(sketch, "E718", {"start": v(-69.37, -67.78) * mm, "end": v(-69.42, -67.95) * mm});
            skLineSegment(sketch, "E719", {"start": v(-69.42, -67.95) * mm, "end": v(-67.9, -69.47) * mm});
            skLineSegment(sketch, "E720", {"start": v(-67.9, -69.47) * mm, "end": v(-67.73, -69.42) * mm});
            skLineSegment(sketch, "E721", {"start": v(-67.73, -69.42) * mm, "end": v(-67.54, -69.34) * mm});
            skLineSegment(sketch, "E722", {"start": v(-67.54, -69.34) * mm, "end": v(-67.35, -69.27) * mm});
            skLineSegment(sketch, "E723", {"start": v(-67.35, -69.27) * mm, "end": v(-67.16, -69.19) * mm});
            skLineSegment(sketch, "E724", {"start": v(-67.16, -69.19) * mm, "end": v(-66.98, -69.11) * mm});
            skLineSegment(sketch, "E725", {"start": v(-66.98, -69.11) * mm, "end": v(-66.8, -69.04) * mm});
            skLineSegment(sketch, "E726", {"start": v(-66.8, -69.04) * mm, "end": v(-66.61, -68.96) * mm});
            skLineSegment(sketch, "E727", {"start": v(-66.61, -68.96) * mm, "end": v(-66.44, -68.88) * mm});
            skLineSegment(sketch, "E728", {"start": v(-66.44, -68.88) * mm, "end": v(-66.26, -68.8) * mm});
            skLineSegment(sketch, "E729", {"start": v(-66.26, -68.8) * mm, "end": v(-66.1, -68.73) * mm});
            skLineSegment(sketch, "E730", {"start": v(-66.1, -68.73) * mm, "end": v(-65.93, -68.65) * mm});
            skLineSegment(sketch, "E731", {"start": v(-65.93, -68.65) * mm, "end": v(-65.76, -68.57) * mm});
            skLineSegment(sketch, "E732", {"start": v(-65.76, -68.57) * mm, "end": v(-65.6, -68.5) * mm});
            skLineSegment(sketch, "E733", {"start": v(-65.6, -68.5) * mm, "end": v(-65.44, -68.42) * mm});
            skLineSegment(sketch, "E734", {"start": v(-65.44, -68.42) * mm, "end": v(-65.28, -68.34) * mm});
            skLineSegment(sketch, "E735", {"start": v(-65.28, -68.34) * mm, "end": v(-65.12, -68.27) * mm});
            skLineSegment(sketch, "E736", {"start": v(-65.12, -68.27) * mm, "end": v(-64.97, -68.2) * mm});
            skLineSegment(sketch, "E737", {"start": v(-64.97, -68.2) * mm, "end": v(-64.82, -68.12) * mm});
            skLineSegment(sketch, "E738", {"start": v(-64.82, -68.12) * mm, "end": v(-64.67, -68.04) * mm});
            skLineSegment(sketch, "E739", {"start": v(-64.67, -68.04) * mm, "end": v(-64.53, -67.97) * mm});
            skLineSegment(sketch, "E740", {"start": v(-64.53, -67.97) * mm, "end": v(-64.39, -67.9) * mm});
            skLineSegment(sketch, "E741", {"start": v(-64.39, -67.9) * mm, "end": v(-64.25, -67.82) * mm});
            skLineSegment(sketch, "E742", {"start": v(-64.25, -67.82) * mm, "end": v(-64.11, -67.74) * mm});
            skLineSegment(sketch, "E743", {"start": v(-64.11, -67.74) * mm, "end": v(-63.98, -67.67) * mm});
            skLineSegment(sketch, "E744", {"start": v(-63.98, -67.67) * mm, "end": v(-63.84, -67.6) * mm});
            skLineSegment(sketch, "E745", {"start": v(-63.84, -67.6) * mm, "end": v(-63.71, -67.53) * mm});
            skLineSegment(sketch, "E746", {"start": v(-63.71, -67.53) * mm, "end": v(-63.59, -67.46) * mm});
            skLineSegment(sketch, "E747", {"start": v(-63.59, -67.46) * mm, "end": v(-63.46, -67.38) * mm});
            skLineSegment(sketch, "E748", {"start": v(-63.46, -67.38) * mm, "end": v(-63.34, -67.31) * mm});
            skLineSegment(sketch, "E749", {"start": v(-63.34, -67.31) * mm, "end": v(-63.22, -67.24) * mm});
            skLineSegment(sketch, "E750", {"start": v(-63.22, -67.24) * mm, "end": v(-63.1, -67.18) * mm});
            skLineSegment(sketch, "E751", {"start": v(-63.1, -67.18) * mm, "end": v(-63, -67.1) * mm});
            skLineSegment(sketch, "E752", {"start": v(-63, -67.1) * mm, "end": v(-62.88, -67.04) * mm});
            skLineSegment(sketch, "E753", {"start": v(-62.88, -67.04) * mm, "end": v(-62.77, -66.97) * mm});
            skLineSegment(sketch, "E754", {"start": v(-62.77, -66.97) * mm, "end": v(-62.66, -66.9) * mm});
            skLineSegment(sketch, "E755", {"start": v(-62.66, -66.9) * mm, "end": v(-62.56, -66.84) * mm});
            skLineSegment(sketch, "E756", {"start": v(-62.56, -66.84) * mm, "end": v(-62.46, -66.78) * mm});
            skLineSegment(sketch, "E757", {"start": v(-62.46, -66.78) * mm, "end": v(-62.36, -66.71) * mm});
            skLineSegment(sketch, "E758", {"start": v(-62.36, -66.71) * mm, "end": v(-62.26, -66.65) * mm});
            skLineSegment(sketch, "E759", {"start": v(-62.26, -66.65) * mm, "end": v(-61.8, -66.79) * mm});
            skLineSegment(sketch, "E760", {"start": v(-61.8, -66.79) * mm, "end": v(-60.56, -67.92) * mm});
            skLineSegment(sketch, "E761", {"start": v(-60.56, -67.92) * mm, "end": v(-60.38, -68.36) * mm});
            skLineSegment(sketch, "E762", {"start": v(-60.38, -68.36) * mm, "end": v(-60.43, -68.46) * mm});
            skLineSegment(sketch, "E763", {"start": v(-60.43, -68.46) * mm, "end": v(-60.48, -68.57) * mm});
            skLineSegment(sketch, "E764", {"start": v(-60.48, -68.57) * mm, "end": v(-60.54, -68.68) * mm});
            skLineSegment(sketch, "E765", {"start": v(-60.54, -68.68) * mm, "end": v(-60.6, -68.79) * mm});
            skLineSegment(sketch, "E766", {"start": v(-60.6, -68.79) * mm, "end": v(-60.65, -68.9) * mm});
            skLineSegment(sketch, "E767", {"start": v(-60.65, -68.9) * mm, "end": v(-60.7, -69.01) * mm});
            skLineSegment(sketch, "E768", {"start": v(-60.7, -69.01) * mm, "end": v(-60.76, -69.13) * mm});
            skLineSegment(sketch, "E769", {"start": v(-60.76, -69.13) * mm, "end": v(-60.82, -69.25) * mm});
            skLineSegment(sketch, "E770", {"start": v(-60.82, -69.25) * mm, "end": v(-60.88, -69.38) * mm});
            skLineSegment(sketch, "E771", {"start": v(-60.88, -69.38) * mm, "end": v(-60.94, -69.5) * mm});
            skLineSegment(sketch, "E772", {"start": v(-60.94, -69.5) * mm, "end": v(-61, -69.63) * mm});
            skLineSegment(sketch, "E773", {"start": v(-61, -69.63) * mm, "end": v(-61.05, -69.76) * mm});
            skLineSegment(sketch, "E774", {"start": v(-61.05, -69.76) * mm, "end": v(-61.11, -69.9) * mm});
            skLineSegment(sketch, "E775", {"start": v(-61.11, -69.9) * mm, "end": v(-61.17, -70.03) * mm});
            skLineSegment(sketch, "E776", {"start": v(-61.17, -70.03) * mm, "end": v(-61.23, -70.17) * mm});
            skLineSegment(sketch, "E777", {"start": v(-61.23, -70.17) * mm, "end": v(-61.29, -70.3) * mm});
            skLineSegment(sketch, "E778", {"start": v(-61.29, -70.3) * mm, "end": v(-61.35, -70.45) * mm});
            skLineSegment(sketch, "E779", {"start": v(-61.35, -70.45) * mm, "end": v(-61.41, -70.6) * mm});
            skLineSegment(sketch, "E780", {"start": v(-61.41, -70.6) * mm, "end": v(-61.47, -70.74) * mm});
            skLineSegment(sketch, "E781", {"start": v(-61.47, -70.74) * mm, "end": v(-61.53, -70.9) * mm});
            skLineSegment(sketch, "E782", {"start": v(-61.53, -70.9) * mm, "end": v(-61.6, -71.05) * mm});
            skLineSegment(sketch, "E783", {"start": v(-61.6, -71.05) * mm, "end": v(-61.65, -71.2) * mm});
            skLineSegment(sketch, "E784", {"start": v(-61.65, -71.2) * mm, "end": v(-61.71, -71.36) * mm});
            skLineSegment(sketch, "E785", {"start": v(-61.71, -71.36) * mm, "end": v(-61.77, -71.53) * mm});
            skLineSegment(sketch, "E786", {"start": v(-61.77, -71.53) * mm, "end": v(-61.83, -71.7) * mm});
            skLineSegment(sketch, "E787", {"start": v(-61.83, -71.7) * mm, "end": v(-61.9, -71.86) * mm});
            skLineSegment(sketch, "E788", {"start": v(-61.9, -71.86) * mm, "end": v(-61.96, -72.03) * mm});
            skLineSegment(sketch, "E789", {"start": v(-61.96, -72.03) * mm, "end": v(-62.02, -72.2) * mm});
            skLineSegment(sketch, "E790", {"start": v(-62.02, -72.2) * mm, "end": v(-62.08, -72.37) * mm});
            skLineSegment(sketch, "E791", {"start": v(-62.08, -72.37) * mm, "end": v(-62.14, -72.55) * mm});
            skLineSegment(sketch, "E792", {"start": v(-62.14, -72.55) * mm, "end": v(-62.2, -72.73) * mm});
            skLineSegment(sketch, "E793", {"start": v(-62.2, -72.73) * mm, "end": v(-62.26, -72.92) * mm});
            skLineSegment(sketch, "E794", {"start": v(-62.26, -72.92) * mm, "end": v(-62.32, -73.1) * mm});
            skLineSegment(sketch, "E795", {"start": v(-62.32, -73.1) * mm, "end": v(-62.38, -73.29) * mm});
            skLineSegment(sketch, "E796", {"start": v(-62.38, -73.29) * mm, "end": v(-62.44, -73.48) * mm});
            skLineSegment(sketch, "E797", {"start": v(-62.44, -73.48) * mm, "end": v(-62.5, -73.67) * mm});
            skLineSegment(sketch, "E798", {"start": v(-62.5, -73.67) * mm, "end": v(-62.55, -73.87) * mm});
            skLineSegment(sketch, "E799", {"start": v(-62.55, -73.87) * mm, "end": v(-62.61, -74.07) * mm});
            skLineSegment(sketch, "E800", {"start": v(-62.61, -74.07) * mm, "end": v(-62.65, -74.24) * mm});
            skLineSegment(sketch, "E801", {"start": v(-62.65, -74.24) * mm, "end": v(-60.99, -75.61) * mm});
            skLineSegment(sketch, "E802", {"start": v(-60.99, -75.61) * mm, "end": v(-60.82, -75.55) * mm});
            skLineSegment(sketch, "E803", {"start": v(-60.82, -75.55) * mm, "end": v(-60.64, -75.45) * mm});
            skLineSegment(sketch, "E804", {"start": v(-60.64, -75.45) * mm, "end": v(-60.46, -75.36) * mm});
            skLineSegment(sketch, "E805", {"start": v(-60.46, -75.36) * mm, "end": v(-60.28, -75.26) * mm});
            skLineSegment(sketch, "E806", {"start": v(-60.28, -75.26) * mm, "end": v(-60.1, -75.17) * mm});
            skLineSegment(sketch, "E807", {"start": v(-60.1, -75.17) * mm, "end": v(-59.93, -75.07) * mm});
            skLineSegment(sketch, "E808", {"start": v(-59.93, -75.07) * mm, "end": v(-59.76, -74.98) * mm});
            skLineSegment(sketch, "E809", {"start": v(-59.76, -74.98) * mm, "end": v(-59.59, -74.88) * mm});
            skLineSegment(sketch, "E810", {"start": v(-59.59, -74.88) * mm, "end": v(-59.42, -74.8) * mm});
            skLineSegment(sketch, "E811", {"start": v(-59.42, -74.8) * mm, "end": v(-59.26, -74.7) * mm});
            skLineSegment(sketch, "E812", {"start": v(-59.26, -74.7) * mm, "end": v(-59.1, -74.6) * mm});
            skLineSegment(sketch, "E813", {"start": v(-59.1, -74.6) * mm, "end": v(-58.94, -74.51) * mm});
            skLineSegment(sketch, "E814", {"start": v(-58.94, -74.51) * mm, "end": v(-58.79, -74.42) * mm});
            skLineSegment(sketch, "E815", {"start": v(-58.79, -74.42) * mm, "end": v(-58.64, -74.33) * mm});
            skLineSegment(sketch, "E816", {"start": v(-58.64, -74.33) * mm, "end": v(-58.49, -74.24) * mm});
            skLineSegment(sketch, "E817", {"start": v(-58.49, -74.24) * mm, "end": v(-58.34, -74.15) * mm});
            skLineSegment(sketch, "E818", {"start": v(-58.34, -74.15) * mm, "end": v(-58.2, -74.06) * mm});
            skLineSegment(sketch, "E819", {"start": v(-58.2, -74.06) * mm, "end": v(-58.05, -73.97) * mm});
            skLineSegment(sketch, "E820", {"start": v(-58.05, -73.97) * mm, "end": v(-57.91, -73.88) * mm});
            skLineSegment(sketch, "E821", {"start": v(-57.91, -73.88) * mm, "end": v(-57.78, -73.8) * mm});
            skLineSegment(sketch, "E822", {"start": v(-57.78, -73.8) * mm, "end": v(-57.64, -73.7) * mm});
            skLineSegment(sketch, "E823", {"start": v(-57.64, -73.7) * mm, "end": v(-57.5, -73.62) * mm});
            skLineSegment(sketch, "E824", {"start": v(-57.5, -73.62) * mm, "end": v(-57.38, -73.53) * mm});
            skLineSegment(sketch, "E825", {"start": v(-57.38, -73.53) * mm, "end": v(-57.25, -73.45) * mm});
            skLineSegment(sketch, "E826", {"start": v(-57.25, -73.45) * mm, "end": v(-57.13, -73.36) * mm});
            skLineSegment(sketch, "E827", {"start": v(-57.13, -73.36) * mm, "end": v(-57, -73.28) * mm});
            skLineSegment(sketch, "E828", {"start": v(-57, -73.28) * mm, "end": v(-56.89, -73.2) * mm});
            skLineSegment(sketch, "E829", {"start": v(-56.89, -73.2) * mm, "end": v(-56.77, -73.11) * mm});
            skLineSegment(sketch, "E830", {"start": v(-56.77, -73.11) * mm, "end": v(-56.66, -73.03) * mm});
            skLineSegment(sketch, "E831", {"start": v(-56.66, -73.03) * mm, "end": v(-56.54, -72.95) * mm});
            skLineSegment(sketch, "E832", {"start": v(-56.54, -72.95) * mm, "end": v(-56.44, -72.87) * mm});
            skLineSegment(sketch, "E833", {"start": v(-56.44, -72.87) * mm, "end": v(-56.33, -72.8) * mm});
            skLineSegment(sketch, "E834", {"start": v(-56.33, -72.8) * mm, "end": v(-56.22, -72.71) * mm});
            skLineSegment(sketch, "E835", {"start": v(-56.22, -72.71) * mm, "end": v(-56.12, -72.64) * mm});
            skLineSegment(sketch, "E836", {"start": v(-56.12, -72.64) * mm, "end": v(-56.02, -72.56) * mm});
            skLineSegment(sketch, "E837", {"start": v(-56.02, -72.56) * mm, "end": v(-55.92, -72.48) * mm});
            skLineSegment(sketch, "E838", {"start": v(-55.92, -72.48) * mm, "end": v(-55.83, -72.41) * mm});
            skLineSegment(sketch, "E839", {"start": v(-55.83, -72.41) * mm, "end": v(-55.74, -72.34) * mm});
            skLineSegment(sketch, "E840", {"start": v(-55.74, -72.34) * mm, "end": v(-55.64, -72.26) * mm});
            skLineSegment(sketch, "E841", {"start": v(-55.64, -72.26) * mm, "end": v(-55.18, -72.36) * mm});
            skLineSegment(sketch, "E842", {"start": v(-55.18, -72.36) * mm, "end": v(-53.83, -73.37) * mm});
            skLineSegment(sketch, "E843", {"start": v(-53.83, -73.37) * mm, "end": v(-53.6, -73.8) * mm});
            skLineSegment(sketch, "E844", {"start": v(-53.6, -73.8) * mm, "end": v(-53.65, -73.9) * mm});
            skLineSegment(sketch, "E845", {"start": v(-53.65, -73.9) * mm, "end": v(-53.7, -74) * mm});
            skLineSegment(sketch, "E846", {"start": v(-53.7, -74) * mm, "end": v(-53.74, -74.12) * mm});
            skLineSegment(sketch, "E847", {"start": v(-53.74, -74.12) * mm, "end": v(-53.78, -74.24) * mm});
            skLineSegment(sketch, "E848", {"start": v(-53.78, -74.24) * mm, "end": v(-53.83, -74.35) * mm});
            skLineSegment(sketch, "E849", {"start": v(-53.83, -74.35) * mm, "end": v(-53.87, -74.47) * mm});
            skLineSegment(sketch, "E850", {"start": v(-53.87, -74.47) * mm, "end": v(-53.92, -74.6) * mm});
            skLineSegment(sketch, "E851", {"start": v(-53.92, -74.6) * mm, "end": v(-53.96, -74.72) * mm});
            skLineSegment(sketch, "E852", {"start": v(-53.96, -74.72) * mm, "end": v(-54, -74.85) * mm});
            skLineSegment(sketch, "E853", {"start": v(-54, -74.85) * mm, "end": v(-54.05, -74.98) * mm});
            skLineSegment(sketch, "E854", {"start": v(-54.05, -74.98) * mm, "end": v(-54.1, -75.11) * mm});
            skLineSegment(sketch, "E855", {"start": v(-54.1, -75.11) * mm, "end": v(-54.14, -75.25) * mm});
            skLineSegment(sketch, "E856", {"start": v(-54.14, -75.25) * mm, "end": v(-54.2, -75.38) * mm});
            skLineSegment(sketch, "E857", {"start": v(-54.2, -75.38) * mm, "end": v(-54.24, -75.52) * mm});
            skLineSegment(sketch, "E858", {"start": v(-54.24, -75.52) * mm, "end": v(-54.28, -75.67) * mm});
            skLineSegment(sketch, "E859", {"start": v(-54.28, -75.67) * mm, "end": v(-54.33, -75.81) * mm});
            skLineSegment(sketch, "E860", {"start": v(-54.33, -75.81) * mm, "end": v(-54.38, -75.96) * mm});
            skLineSegment(sketch, "E861", {"start": v(-54.38, -75.96) * mm, "end": v(-54.42, -76.11) * mm});
            skLineSegment(sketch, "E862", {"start": v(-54.42, -76.11) * mm, "end": v(-54.47, -76.27) * mm});
            skLineSegment(sketch, "E863", {"start": v(-54.47, -76.27) * mm, "end": v(-54.51, -76.42) * mm});
            skLineSegment(sketch, "E864", {"start": v(-54.51, -76.42) * mm, "end": v(-54.56, -76.58) * mm});
            skLineSegment(sketch, "E865", {"start": v(-54.56, -76.58) * mm, "end": v(-54.6, -76.74) * mm});
            skLineSegment(sketch, "E866", {"start": v(-54.6, -76.74) * mm, "end": v(-54.65, -76.9) * mm});
            skLineSegment(sketch, "E867", {"start": v(-54.65, -76.9) * mm, "end": v(-54.7, -77.07) * mm});
            skLineSegment(sketch, "E868", {"start": v(-54.7, -77.07) * mm, "end": v(-54.74, -77.24) * mm});
            skLineSegment(sketch, "E869", {"start": v(-54.74, -77.24) * mm, "end": v(-54.78, -77.42) * mm});
            skLineSegment(sketch, "E870", {"start": v(-54.78, -77.42) * mm, "end": v(-54.83, -77.6) * mm});
            skLineSegment(sketch, "E871", {"start": v(-54.83, -77.6) * mm, "end": v(-54.87, -77.77) * mm});
            skLineSegment(sketch, "E872", {"start": v(-54.87, -77.77) * mm, "end": v(-54.92, -77.95) * mm});
            skLineSegment(sketch, "E873", {"start": v(-54.92, -77.95) * mm, "end": v(-54.96, -78.13) * mm});
            skLineSegment(sketch, "E874", {"start": v(-54.96, -78.13) * mm, "end": v(-55, -78.32) * mm});
            skLineSegment(sketch, "E875", {"start": v(-55, -78.32) * mm, "end": v(-55.04, -78.5) * mm});
            skLineSegment(sketch, "E876", {"start": v(-55.04, -78.5) * mm, "end": v(-55.09, -78.7) * mm});
            skLineSegment(sketch, "E877", {"start": v(-55.09, -78.7) * mm, "end": v(-55.13, -78.89) * mm});
            skLineSegment(sketch, "E878", {"start": v(-55.13, -78.89) * mm, "end": v(-55.17, -79.08) * mm});
            skLineSegment(sketch, "E879", {"start": v(-55.17, -79.08) * mm, "end": v(-55.2, -79.28) * mm});
            skLineSegment(sketch, "E880", {"start": v(-55.2, -79.28) * mm, "end": v(-55.25, -79.48) * mm});
            skLineSegment(sketch, "E881", {"start": v(-55.25, -79.48) * mm, "end": v(-55.29, -79.69) * mm});
            skLineSegment(sketch, "E882", {"start": v(-55.29, -79.69) * mm, "end": v(-55.3, -79.86) * mm});
            skLineSegment(sketch, "E883", {"start": v(-55.3, -79.86) * mm, "end": v(-53.52, -81.07) * mm});
            skLineSegment(sketch, "E884", {"start": v(-53.52, -81.07) * mm, "end": v(-53.37, -80.99) * mm});
            skLineSegment(sketch, "E885", {"start": v(-53.37, -80.99) * mm, "end": v(-53.2, -80.87) * mm});
            skLineSegment(sketch, "E886", {"start": v(-53.2, -80.87) * mm, "end": v(-53.02, -80.76) * mm});
            skLineSegment(sketch, "E887", {"start": v(-53.02, -80.76) * mm, "end": v(-52.85, -80.65) * mm});
            skLineSegment(sketch, "E888", {"start": v(-52.85, -80.65) * mm, "end": v(-52.69, -80.54) * mm});
            skLineSegment(sketch, "E889", {"start": v(-52.69, -80.54) * mm, "end": v(-52.52, -80.43) * mm});
            skLineSegment(sketch, "E890", {"start": v(-52.52, -80.43) * mm, "end": v(-52.36, -80.32) * mm});
            skLineSegment(sketch, "E891", {"start": v(-52.36, -80.32) * mm, "end": v(-52.2, -80.2) * mm});
            skLineSegment(sketch, "E892", {"start": v(-52.2, -80.2) * mm, "end": v(-52.05, -80.1) * mm});
            skLineSegment(sketch, "E893", {"start": v(-52.05, -80.1) * mm, "end": v(-51.9, -80) * mm});
            skLineSegment(sketch, "E894", {"start": v(-51.9, -80) * mm, "end": v(-51.74, -79.88) * mm});
            skLineSegment(sketch, "E895", {"start": v(-51.74, -79.88) * mm, "end": v(-51.6, -79.78) * mm});
            skLineSegment(sketch, "E896", {"start": v(-51.6, -79.78) * mm, "end": v(-51.45, -79.67) * mm});
            skLineSegment(sketch, "E897", {"start": v(-51.45, -79.67) * mm, "end": v(-51.3, -79.57) * mm});
            skLineSegment(sketch, "E898", {"start": v(-51.3, -79.57) * mm, "end": v(-51.16, -79.46) * mm});
            skLineSegment(sketch, "E899", {"start": v(-51.16, -79.46) * mm, "end": v(-51.03, -79.36) * mm});
            skLineSegment(sketch, "E900", {"start": v(-51.03, -79.36) * mm, "end": v(-50.9, -79.25) * mm});
            skLineSegment(sketch, "E901", {"start": v(-50.9, -79.25) * mm, "end": v(-50.76, -79.15) * mm});
            skLineSegment(sketch, "E902", {"start": v(-50.76, -79.15) * mm, "end": v(-50.63, -79.05) * mm});
            skLineSegment(sketch, "E903", {"start": v(-50.63, -79.05) * mm, "end": v(-50.5, -78.95) * mm});
            skLineSegment(sketch, "E904", {"start": v(-50.5, -78.95) * mm, "end": v(-50.37, -78.85) * mm});
            skLineSegment(sketch, "E905", {"start": v(-50.37, -78.85) * mm, "end": v(-50.25, -78.75) * mm});
            skLineSegment(sketch, "E906", {"start": v(-50.25, -78.75) * mm, "end": v(-50.13, -78.65) * mm});
            skLineSegment(sketch, "E907", {"start": v(-50.13, -78.65) * mm, "end": v(-50.01, -78.56) * mm});
            skLineSegment(sketch, "E908", {"start": v(-50.01, -78.56) * mm, "end": v(-49.9, -78.46) * mm});
            skLineSegment(sketch, "E909", {"start": v(-49.9, -78.46) * mm, "end": v(-49.78, -78.36) * mm});
            skLineSegment(sketch, "E910", {"start": v(-49.78, -78.36) * mm, "end": v(-49.67, -78.27) * mm});
            skLineSegment(sketch, "E911", {"start": v(-49.67, -78.27) * mm, "end": v(-49.56, -78.18) * mm});
            skLineSegment(sketch, "E912", {"start": v(-49.56, -78.18) * mm, "end": v(-49.46, -78.09) * mm});
            skLineSegment(sketch, "E913", {"start": v(-49.46, -78.09) * mm, "end": v(-49.35, -78) * mm});
            skLineSegment(sketch, "E914", {"start": v(-49.35, -78) * mm, "end": v(-49.25, -77.9) * mm});
            skLineSegment(sketch, "E915", {"start": v(-49.25, -77.9) * mm, "end": v(-49.15, -77.82) * mm});
            skLineSegment(sketch, "E916", {"start": v(-49.15, -77.82) * mm, "end": v(-49.06, -77.73) * mm});
            skLineSegment(sketch, "E917", {"start": v(-49.06, -77.73) * mm, "end": v(-48.96, -77.64) * mm});
            skLineSegment(sketch, "E918", {"start": v(-48.96, -77.64) * mm, "end": v(-48.87, -77.56) * mm});
            skLineSegment(sketch, "E919", {"start": v(-48.87, -77.56) * mm, "end": v(-48.78, -77.47) * mm});
            skLineSegment(sketch, "E920", {"start": v(-48.78, -77.47) * mm, "end": v(-48.7, -77.39) * mm});
            skLineSegment(sketch, "E921", {"start": v(-48.7, -77.39) * mm, "end": v(-48.6, -77.3) * mm});
            skLineSegment(sketch, "E922", {"start": v(-48.6, -77.3) * mm, "end": v(-48.52, -77.23) * mm});
            skLineSegment(sketch, "E923", {"start": v(-48.52, -77.23) * mm, "end": v(-48.05, -77.28) * mm});
            skLineSegment(sketch, "E924", {"start": v(-48.05, -77.28) * mm, "end": v(-46.61, -78.16) * mm});
            skLineSegment(sketch, "E925", {"start": v(-46.61, -78.16) * mm, "end": v(-46.35, -78.55) * mm});
            skLineSegment(sketch, "E926", {"start": v(-46.35, -78.55) * mm, "end": v(-46.38, -78.66) * mm});
            skLineSegment(sketch, "E927", {"start": v(-46.38, -78.66) * mm, "end": v(-46.41, -78.78) * mm});
            skLineSegment(sketch, "E928", {"start": v(-46.41, -78.78) * mm, "end": v(-46.45, -78.9) * mm});
            skLineSegment(sketch, "E929", {"start": v(-46.45, -78.9) * mm, "end": v(-46.48, -79.01) * mm});
            skLineSegment(sketch, "E930", {"start": v(-46.48, -79.01) * mm, "end": v(-46.51, -79.13) * mm});
            skLineSegment(sketch, "E931", {"start": v(-46.51, -79.13) * mm, "end": v(-46.55, -79.26) * mm});
            skLineSegment(sketch, "E932", {"start": v(-46.55, -79.26) * mm, "end": v(-46.58, -79.38) * mm});
            skLineSegment(sketch, "E933", {"start": v(-46.58, -79.38) * mm, "end": v(-46.61, -79.51) * mm});
            skLineSegment(sketch, "E934", {"start": v(-46.61, -79.51) * mm, "end": v(-46.65, -79.64) * mm});
            skLineSegment(sketch, "E935", {"start": v(-46.65, -79.64) * mm, "end": v(-46.68, -79.78) * mm});
            skLineSegment(sketch, "E936", {"start": v(-46.68, -79.78) * mm, "end": v(-46.71, -79.91) * mm});
            skLineSegment(sketch, "E937", {"start": v(-46.71, -79.91) * mm, "end": v(-46.75, -80.05) * mm});
            skLineSegment(sketch, "E938", {"start": v(-46.75, -80.05) * mm, "end": v(-46.78, -80.2) * mm});
            skLineSegment(sketch, "E939", {"start": v(-46.78, -80.2) * mm, "end": v(-46.81, -80.34) * mm});
            skLineSegment(sketch, "E940", {"start": v(-46.81, -80.34) * mm, "end": v(-46.84, -80.49) * mm});
            skLineSegment(sketch, "E941", {"start": v(-46.84, -80.49) * mm, "end": v(-46.88, -80.63) * mm});
            skLineSegment(sketch, "E942", {"start": v(-46.88, -80.63) * mm, "end": v(-46.9, -80.79) * mm});
            skLineSegment(sketch, "E943", {"start": v(-46.9, -80.79) * mm, "end": v(-46.94, -80.94) * mm});
            skLineSegment(sketch, "E944", {"start": v(-46.94, -80.94) * mm, "end": v(-46.97, -81.1) * mm});
            skLineSegment(sketch, "E945", {"start": v(-46.97, -81.1) * mm, "end": v(-47, -81.26) * mm});
            skLineSegment(sketch, "E946", {"start": v(-47, -81.26) * mm, "end": v(-47.03, -81.42) * mm});
            skLineSegment(sketch, "E947", {"start": v(-47.03, -81.42) * mm, "end": v(-47.06, -81.59) * mm});
            skLineSegment(sketch, "E948", {"start": v(-47.06, -81.59) * mm, "end": v(-47.1, -81.75) * mm});
            skLineSegment(sketch, "E949", {"start": v(-47.1, -81.75) * mm, "end": v(-47.12, -81.92) * mm});
            skLineSegment(sketch, "E950", {"start": v(-47.12, -81.92) * mm, "end": v(-47.15, -82.1) * mm});
            skLineSegment(sketch, "E951", {"start": v(-47.15, -82.1) * mm, "end": v(-47.18, -82.27) * mm});
            skLineSegment(sketch, "E952", {"start": v(-47.18, -82.27) * mm, "end": v(-47.2, -82.45) * mm});
            skLineSegment(sketch, "E953", {"start": v(-47.2, -82.45) * mm, "end": v(-47.23, -82.63) * mm});
            skLineSegment(sketch, "E954", {"start": v(-47.23, -82.63) * mm, "end": v(-47.26, -82.81) * mm});
            skLineSegment(sketch, "E955", {"start": v(-47.26, -82.81) * mm, "end": v(-47.28, -83) * mm});
            skLineSegment(sketch, "E956", {"start": v(-47.28, -83) * mm, "end": v(-47.3, -83.19) * mm});
            skLineSegment(sketch, "E957", {"start": v(-47.3, -83.19) * mm, "end": v(-47.33, -83.38) * mm});
            skLineSegment(sketch, "E958", {"start": v(-47.33, -83.38) * mm, "end": v(-47.36, -83.57) * mm});
            skLineSegment(sketch, "E959", {"start": v(-47.36, -83.57) * mm, "end": v(-47.38, -83.77) * mm});
            skLineSegment(sketch, "E960", {"start": v(-47.38, -83.77) * mm, "end": v(-47.4, -83.97) * mm});
            skLineSegment(sketch, "E961", {"start": v(-47.4, -83.97) * mm, "end": v(-47.42, -84.17) * mm});
            skLineSegment(sketch, "E962", {"start": v(-47.42, -84.17) * mm, "end": v(-47.44, -84.37) * mm});
            skLineSegment(sketch, "E963", {"start": v(-47.44, -84.37) * mm, "end": v(-47.46, -84.58) * mm});
            skLineSegment(sketch, "E964", {"start": v(-47.46, -84.58) * mm, "end": v(-47.46, -84.76) * mm});
            skLineSegment(sketch, "E965", {"start": v(-47.46, -84.76) * mm, "end": v(-45.58, -85.79) * mm});
            skLineSegment(sketch, "E966", {"start": v(-45.58, -85.79) * mm, "end": v(-45.43, -85.7) * mm});
            skLineSegment(sketch, "E967", {"start": v(-45.43, -85.7) * mm, "end": v(-45.26, -85.56) * mm});
            skLineSegment(sketch, "E968", {"start": v(-45.26, -85.56) * mm, "end": v(-45.1, -85.44) * mm});
            skLineSegment(sketch, "E969", {"start": v(-45.1, -85.44) * mm, "end": v(-44.95, -85.3) * mm});
            skLineSegment(sketch, "E970", {"start": v(-44.95, -85.3) * mm, "end": v(-44.8, -85.18) * mm});
            skLineSegment(sketch, "E971", {"start": v(-44.8, -85.18) * mm, "end": v(-44.64, -85.06) * mm});
            skLineSegment(sketch, "E972", {"start": v(-44.64, -85.06) * mm, "end": v(-44.49, -84.93) * mm});
            skLineSegment(sketch, "E973", {"start": v(-44.49, -84.93) * mm, "end": v(-44.34, -84.8) * mm});
            skLineSegment(sketch, "E974", {"start": v(-44.34, -84.8) * mm, "end": v(-44.2, -84.69) * mm});
            skLineSegment(sketch, "E975", {"start": v(-44.2, -84.69) * mm, "end": v(-44.05, -84.56) * mm});
            skLineSegment(sketch, "E976", {"start": v(-44.05, -84.56) * mm, "end": v(-43.91, -84.44) * mm});
            skLineSegment(sketch, "E977", {"start": v(-43.91, -84.44) * mm, "end": v(-43.78, -84.32) * mm});
            skLineSegment(sketch, "E978", {"start": v(-43.78, -84.32) * mm, "end": v(-43.64, -84.2) * mm});
            skLineSegment(sketch, "E979", {"start": v(-43.64, -84.2) * mm, "end": v(-43.5, -84.08) * mm});
            skLineSegment(sketch, "E980", {"start": v(-43.5, -84.08) * mm, "end": v(-43.38, -83.97) * mm});
            skLineSegment(sketch, "E981", {"start": v(-43.38, -83.97) * mm, "end": v(-43.25, -83.85) * mm});
            skLineSegment(sketch, "E982", {"start": v(-43.25, -83.85) * mm, "end": v(-43.13, -83.73) * mm});
            skLineSegment(sketch, "E983", {"start": v(-43.13, -83.73) * mm, "end": v(-43, -83.62) * mm});
            skLineSegment(sketch, "E984", {"start": v(-43, -83.62) * mm, "end": v(-42.88, -83.5) * mm});
            skLineSegment(sketch, "E985", {"start": v(-42.88, -83.5) * mm, "end": v(-42.77, -83.4) * mm});
            skLineSegment(sketch, "E986", {"start": v(-42.77, -83.4) * mm, "end": v(-42.65, -83.28) * mm});
            skLineSegment(sketch, "E987", {"start": v(-42.65, -83.28) * mm, "end": v(-42.54, -83.17) * mm});
            skLineSegment(sketch, "E988", {"start": v(-42.54, -83.17) * mm, "end": v(-42.43, -83.06) * mm});
            skLineSegment(sketch, "E989", {"start": v(-42.43, -83.06) * mm, "end": v(-42.32, -82.95) * mm});
            skLineSegment(sketch, "E990", {"start": v(-42.32, -82.95) * mm, "end": v(-42.21, -82.85) * mm});
            skLineSegment(sketch, "E991", {"start": v(-42.21, -82.85) * mm, "end": v(-42.1, -82.74) * mm});
            skLineSegment(sketch, "E992", {"start": v(-42.1, -82.74) * mm, "end": v(-42, -82.64) * mm});
            skLineSegment(sketch, "E993", {"start": v(-42, -82.64) * mm, "end": v(-41.9, -82.53) * mm});
            skLineSegment(sketch, "E994", {"start": v(-41.9, -82.53) * mm, "end": v(-41.81, -82.43) * mm});
            skLineSegment(sketch, "E995", {"start": v(-41.81, -82.43) * mm, "end": v(-41.72, -82.33) * mm});
            skLineSegment(sketch, "E996", {"start": v(-41.72, -82.33) * mm, "end": v(-41.62, -82.23) * mm});
            skLineSegment(sketch, "E997", {"start": v(-41.62, -82.23) * mm, "end": v(-41.53, -82.14) * mm});
            skLineSegment(sketch, "E998", {"start": v(-41.53, -82.14) * mm, "end": v(-41.45, -82.04) * mm});
            skLineSegment(sketch, "E999", {"start": v(-41.45, -82.04) * mm, "end": v(-41.36, -81.94) * mm});
            skLineSegment(sketch, "E1000", {"start": v(-41.36, -81.94) * mm, "end": v(-41.28, -81.85) * mm});
            skLineSegment(sketch, "E1001", {"start": v(-41.28, -81.85) * mm, "end": v(-41.2, -81.76) * mm});
            skLineSegment(sketch, "E1002", {"start": v(-41.2, -81.76) * mm, "end": v(-41.12, -81.67) * mm});
            skLineSegment(sketch, "E1003", {"start": v(-41.12, -81.67) * mm, "end": v(-41.04, -81.58) * mm});
            skLineSegment(sketch, "E1004", {"start": v(-41.04, -81.58) * mm, "end": v(-40.96, -81.49) * mm});
            skLineSegment(sketch, "E1005", {"start": v(-40.96, -81.49) * mm, "end": v(-40.49, -81.5) * mm});
            skLineSegment(sketch, "E1006", {"start": v(-40.49, -81.5) * mm, "end": v(-38.97, -82.23) * mm});
            skLineSegment(sketch, "E1007", {"start": v(-38.97, -82.23) * mm, "end": v(-38.67, -82.6) * mm});
            skLineSegment(sketch, "E1008", {"start": v(-38.67, -82.6) * mm, "end": v(-38.7, -82.72) * mm});
            skLineSegment(sketch, "E1009", {"start": v(-38.7, -82.72) * mm, "end": v(-38.72, -82.83) * mm});
            skLineSegment(sketch, "E1010", {"start": v(-38.72, -82.83) * mm, "end": v(-38.74, -82.95) * mm});
            skLineSegment(sketch, "E1011", {"start": v(-38.74, -82.95) * mm, "end": v(-38.76, -83.07) * mm});
            skLineSegment(sketch, "E1012", {"start": v(-38.76, -83.07) * mm, "end": v(-38.78, -83.2) * mm});
            skLineSegment(sketch, "E1013", {"start": v(-38.78, -83.2) * mm, "end": v(-38.8, -83.32) * mm});
            skLineSegment(sketch, "E1014", {"start": v(-38.8, -83.32) * mm, "end": v(-38.82, -83.45) * mm});
            skLineSegment(sketch, "E1015", {"start": v(-38.82, -83.45) * mm, "end": v(-38.85, -83.58) * mm});
            skLineSegment(sketch, "E1016", {"start": v(-38.85, -83.58) * mm, "end": v(-38.87, -83.72) * mm});
            skLineSegment(sketch, "E1017", {"start": v(-38.87, -83.72) * mm, "end": v(-38.89, -83.85) * mm});
            skLineSegment(sketch, "E1018", {"start": v(-38.89, -83.85) * mm, "end": v(-38.9, -84) * mm});
            skLineSegment(sketch, "E1019", {"start": v(-38.9, -84) * mm, "end": v(-38.93, -84.13) * mm});
            skLineSegment(sketch, "E1020", {"start": v(-38.93, -84.13) * mm, "end": v(-38.95, -84.28) * mm});
            skLineSegment(sketch, "E1021", {"start": v(-38.95, -84.28) * mm, "end": v(-38.96, -84.42) * mm});
            skLineSegment(sketch, "E1022", {"start": v(-38.96, -84.42) * mm, "end": v(-38.98, -84.57) * mm});
            skLineSegment(sketch, "E1023", {"start": v(-38.98, -84.57) * mm, "end": v(-39, -84.73) * mm});
            skLineSegment(sketch, "E1024", {"start": v(-39, -84.73) * mm, "end": v(-39.02, -84.88) * mm});
            skLineSegment(sketch, "E1025", {"start": v(-39.02, -84.88) * mm, "end": v(-39.03, -85.04) * mm});
            skLineSegment(sketch, "E1026", {"start": v(-39.03, -85.04) * mm, "end": v(-39.05, -85.2) * mm});
            skLineSegment(sketch, "E1027", {"start": v(-39.05, -85.2) * mm, "end": v(-39.07, -85.36) * mm});
            skLineSegment(sketch, "E1028", {"start": v(-39.07, -85.36) * mm, "end": v(-39.08, -85.52) * mm});
            skLineSegment(sketch, "E1029", {"start": v(-39.08, -85.52) * mm, "end": v(-39.1, -85.7) * mm});
            skLineSegment(sketch, "E1030", {"start": v(-39.1, -85.7) * mm, "end": v(-39.1, -85.86) * mm});
            skLineSegment(sketch, "E1031", {"start": v(-39.1, -85.86) * mm, "end": v(-39.12, -86.03) * mm});
            skLineSegment(sketch, "E1032", {"start": v(-39.12, -86.03) * mm, "end": v(-39.13, -86.2) * mm});
            skLineSegment(sketch, "E1033", {"start": v(-39.13, -86.2) * mm, "end": v(-39.14, -86.38) * mm});
            skLineSegment(sketch, "E1034", {"start": v(-39.14, -86.38) * mm, "end": v(-39.15, -86.56) * mm});
            skLineSegment(sketch, "E1035", {"start": v(-39.15, -86.56) * mm, "end": v(-39.16, -86.75) * mm});
            skLineSegment(sketch, "E1036", {"start": v(-39.16, -86.75) * mm, "end": v(-39.17, -86.93) * mm});
            skLineSegment(sketch, "E1037", {"start": v(-39.17, -86.93) * mm, "end": v(-39.18, -87.12) * mm});
            skLineSegment(sketch, "E1038", {"start": v(-39.18, -87.12) * mm, "end": v(-39.19, -87.3) * mm});
            skLineSegment(sketch, "E1039", {"start": v(-39.19, -87.3) * mm, "end": v(-39.2, -87.5) * mm});
            skLineSegment(sketch, "E1040", {"start": v(-39.2, -87.5) * mm, "end": v(-39.2, -87.7) * mm});
            skLineSegment(sketch, "E1041", {"start": v(-39.2, -87.7) * mm, "end": v(-39.2, -87.9) * mm});
            skLineSegment(sketch, "E1042", {"start": v(-39.2, -87.9) * mm, "end": v(-39.2, -88.1) * mm});
            skLineSegment(sketch, "E1043", {"start": v(-39.2, -88.1) * mm, "end": v(-39.2, -88.3) * mm});
            skLineSegment(sketch, "E1044", {"start": v(-39.2, -88.3) * mm, "end": v(-39.2, -88.5) * mm});
            skLineSegment(sketch, "E1045", {"start": v(-39.2, -88.5) * mm, "end": v(-39.2, -88.7) * mm});
            skLineSegment(sketch, "E1046", {"start": v(-39.2, -88.7) * mm, "end": v(-39.2, -88.89) * mm});
            skLineSegment(sketch, "E1047", {"start": v(-39.2, -88.89) * mm, "end": v(-37.21, -89.73) * mm});
            skLineSegment(sketch, "E1048", {"start": v(-37.21, -89.73) * mm, "end": v(-37.08, -89.62) * mm});
            skLineSegment(sketch, "E1049", {"start": v(-37.08, -89.62) * mm, "end": v(-36.93, -89.48) * mm});
            skLineSegment(sketch, "E1050", {"start": v(-36.93, -89.48) * mm, "end": v(-36.78, -89.34) * mm});
            skLineSegment(sketch, "E1051", {"start": v(-36.78, -89.34) * mm, "end": v(-36.63, -89.2) * mm});
            skLineSegment(sketch, "E1052", {"start": v(-36.63, -89.2) * mm, "end": v(-36.5, -89.05) * mm});
            skLineSegment(sketch, "E1053", {"start": v(-36.5, -89.05) * mm, "end": v(-36.35, -88.91) * mm});
            skLineSegment(sketch, "E1054", {"start": v(-36.35, -88.91) * mm, "end": v(-36.21, -88.78) * mm});
            skLineSegment(sketch, "E1055", {"start": v(-36.21, -88.78) * mm, "end": v(-36.08, -88.64) * mm});
            skLineSegment(sketch, "E1056", {"start": v(-36.08, -88.64) * mm, "end": v(-35.95, -88.5) * mm});
            skLineSegment(sketch, "E1057", {"start": v(-35.95, -88.5) * mm, "end": v(-35.82, -88.37) * mm});
            skLineSegment(sketch, "E1058", {"start": v(-35.82, -88.37) * mm, "end": v(-35.69, -88.23) * mm});
            skLineSegment(sketch, "E1059", {"start": v(-35.69, -88.23) * mm, "end": v(-35.56, -88.1) * mm});
            skLineSegment(sketch, "E1060", {"start": v(-35.56, -88.1) * mm, "end": v(-35.44, -87.97) * mm});
            skLineSegment(sketch, "E1061", {"start": v(-35.44, -87.97) * mm, "end": v(-35.32, -87.84) * mm});
            skLineSegment(sketch, "E1062", {"start": v(-35.32, -87.84) * mm, "end": v(-35.2, -87.7) * mm});
            skLineSegment(sketch, "E1063", {"start": v(-35.2, -87.7) * mm, "end": v(-35.09, -87.58) * mm});
            skLineSegment(sketch, "E1064", {"start": v(-35.09, -87.58) * mm, "end": v(-34.97, -87.45) * mm});
            skLineSegment(sketch, "E1065", {"start": v(-34.97, -87.45) * mm, "end": v(-34.86, -87.33) * mm});
            skLineSegment(sketch, "E1066", {"start": v(-34.86, -87.33) * mm, "end": v(-34.75, -87.2) * mm});
            skLineSegment(sketch, "E1067", {"start": v(-34.75, -87.2) * mm, "end": v(-34.65, -87.08) * mm});
            skLineSegment(sketch, "E1068", {"start": v(-34.65, -87.08) * mm, "end": v(-34.54, -86.96) * mm});
            skLineSegment(sketch, "E1069", {"start": v(-34.54, -86.96) * mm, "end": v(-34.44, -86.84) * mm});
            skLineSegment(sketch, "E1070", {"start": v(-34.44, -86.84) * mm, "end": v(-34.34, -86.72) * mm});
            skLineSegment(sketch, "E1071", {"start": v(-34.34, -86.72) * mm, "end": v(-34.24, -86.6) * mm});
            skLineSegment(sketch, "E1072", {"start": v(-34.24, -86.6) * mm, "end": v(-34.15, -86.48) * mm});
            skLineSegment(sketch, "E1073", {"start": v(-34.15, -86.48) * mm, "end": v(-34.05, -86.37) * mm});
            skLineSegment(sketch, "E1074", {"start": v(-34.05, -86.37) * mm, "end": v(-33.96, -86.26) * mm});
            skLineSegment(sketch, "E1075", {"start": v(-33.96, -86.26) * mm, "end": v(-33.87, -86.14) * mm});
            skLineSegment(sketch, "E1076", {"start": v(-33.87, -86.14) * mm, "end": v(-33.79, -86.03) * mm});
            skLineSegment(sketch, "E1077", {"start": v(-33.79, -86.03) * mm, "end": v(-33.7, -85.93) * mm});
            skLineSegment(sketch, "E1078", {"start": v(-33.7, -85.93) * mm, "end": v(-33.62, -85.82) * mm});
            skLineSegment(sketch, "E1079", {"start": v(-33.62, -85.82) * mm, "end": v(-33.54, -85.71) * mm});
            skLineSegment(sketch, "E1080", {"start": v(-33.54, -85.71) * mm, "end": v(-33.46, -85.6) * mm});
            skLineSegment(sketch, "E1081", {"start": v(-33.46, -85.6) * mm, "end": v(-33.38, -85.5) * mm});
            skLineSegment(sketch, "E1082", {"start": v(-33.38, -85.5) * mm, "end": v(-33.3, -85.4) * mm});
            skLineSegment(sketch, "E1083", {"start": v(-33.3, -85.4) * mm, "end": v(-33.24, -85.3) * mm});
            skLineSegment(sketch, "E1084", {"start": v(-33.24, -85.3) * mm, "end": v(-33.17, -85.2) * mm});
            skLineSegment(sketch, "E1085", {"start": v(-33.17, -85.2) * mm, "end": v(-33.1, -85.1) * mm});
            skLineSegment(sketch, "E1086", {"start": v(-33.1, -85.1) * mm, "end": v(-33.03, -85.01) * mm});
            skLineSegment(sketch, "E1087", {"start": v(-33.03, -85.01) * mm, "end": v(-32.56, -84.98) * mm});
            skLineSegment(sketch, "E1088", {"start": v(-32.56, -84.98) * mm, "end": v(-30.98, -85.57) * mm});
            skLineSegment(sketch, "E1089", {"start": v(-30.98, -85.57) * mm, "end": v(-30.64, -85.9) * mm});
            skLineSegment(sketch, "E1090", {"start": v(-30.64, -85.9) * mm, "end": v(-30.66, -86.02) * mm});
            skLineSegment(sketch, "E1091", {"start": v(-30.66, -86.02) * mm, "end": v(-30.67, -86.14) * mm});
            skLineSegment(sketch, "E1092", {"start": v(-30.67, -86.14) * mm, "end": v(-30.68, -86.26) * mm});
            skLineSegment(sketch, "E1093", {"start": v(-30.68, -86.26) * mm, "end": v(-30.69, -86.38) * mm});
            skLineSegment(sketch, "E1094", {"start": v(-30.69, -86.38) * mm, "end": v(-30.7, -86.5) * mm});
            skLineSegment(sketch, "E1095", {"start": v(-30.7, -86.5) * mm, "end": v(-30.7, -86.63) * mm});
            skLineSegment(sketch, "E1096", {"start": v(-30.7, -86.63) * mm, "end": v(-30.72, -86.76) * mm});
            skLineSegment(sketch, "E1097", {"start": v(-30.72, -86.76) * mm, "end": v(-30.72, -86.9) * mm});
            skLineSegment(sketch, "E1098", {"start": v(-30.72, -86.9) * mm, "end": v(-30.73, -87.03) * mm});
            skLineSegment(sketch, "E1099", {"start": v(-30.73, -87.03) * mm, "end": v(-30.74, -87.17) * mm});
            skLineSegment(sketch, "E1100", {"start": v(-30.74, -87.17) * mm, "end": v(-30.75, -87.3) * mm});
            skLineSegment(sketch, "E1101", {"start": v(-30.75, -87.3) * mm, "end": v(-30.75, -87.45) * mm});
            skLineSegment(sketch, "E1102", {"start": v(-30.75, -87.45) * mm, "end": v(-30.76, -87.6) * mm});
            skLineSegment(sketch, "E1103", {"start": v(-30.76, -87.6) * mm, "end": v(-30.76, -87.75) * mm});
            skLineSegment(sketch, "E1104", {"start": v(-30.76, -87.75) * mm, "end": v(-30.77, -87.9) * mm});
            skLineSegment(sketch, "E1105", {"start": v(-30.77, -87.9) * mm, "end": v(-30.77, -88.05) * mm});
            skLineSegment(sketch, "E1106", {"start": v(-30.77, -88.05) * mm, "end": v(-30.77, -88.2) * mm});
            skLineSegment(sketch, "E1107", {"start": v(-30.77, -88.2) * mm, "end": v(-30.77, -88.36) * mm});
            skLineSegment(sketch, "E1108", {"start": v(-30.77, -88.36) * mm, "end": v(-30.77, -88.52) * mm});
            skLineSegment(sketch, "E1109", {"start": v(-30.77, -88.52) * mm, "end": v(-30.77, -88.69) * mm});
            skLineSegment(sketch, "E1110", {"start": v(-30.77, -88.69) * mm, "end": v(-30.77, -88.85) * mm});
            skLineSegment(sketch, "E1111", {"start": v(-30.77, -88.85) * mm, "end": v(-30.77, -89.02) * mm});
            skLineSegment(sketch, "E1112", {"start": v(-30.77, -89.02) * mm, "end": v(-30.77, -89.19) * mm});
            skLineSegment(sketch, "E1113", {"start": v(-30.77, -89.19) * mm, "end": v(-30.77, -89.36) * mm});
            skLineSegment(sketch, "E1114", {"start": v(-30.77, -89.36) * mm, "end": v(-30.76, -89.54) * mm});
            skLineSegment(sketch, "E1115", {"start": v(-30.76, -89.54) * mm, "end": v(-30.75, -89.71) * mm});
            skLineSegment(sketch, "E1116", {"start": v(-30.75, -89.71) * mm, "end": v(-30.75, -89.9) * mm});
            skLineSegment(sketch, "E1117", {"start": v(-30.75, -89.9) * mm, "end": v(-30.74, -90.08) * mm});
            skLineSegment(sketch, "E1118", {"start": v(-30.74, -90.08) * mm, "end": v(-30.73, -90.26) * mm});
            skLineSegment(sketch, "E1119", {"start": v(-30.73, -90.26) * mm, "end": v(-30.72, -90.45) * mm});
            skLineSegment(sketch, "E1120", {"start": v(-30.72, -90.45) * mm, "end": v(-30.71, -90.64) * mm});
            skLineSegment(sketch, "E1121", {"start": v(-30.71, -90.64) * mm, "end": v(-30.7, -90.83) * mm});
            skLineSegment(sketch, "E1122", {"start": v(-30.7, -90.83) * mm, "end": v(-30.68, -91.03) * mm});
            skLineSegment(sketch, "E1123", {"start": v(-30.68, -91.03) * mm, "end": v(-30.67, -91.22) * mm});
            skLineSegment(sketch, "E1124", {"start": v(-30.67, -91.22) * mm, "end": v(-30.65, -91.42) * mm});
            skLineSegment(sketch, "E1125", {"start": v(-30.65, -91.42) * mm, "end": v(-30.64, -91.62) * mm});
            skLineSegment(sketch, "E1126", {"start": v(-30.64, -91.62) * mm, "end": v(-30.62, -91.83) * mm});
            skLineSegment(sketch, "E1127", {"start": v(-30.62, -91.83) * mm, "end": v(-30.6, -92.03) * mm});
            skLineSegment(sketch, "E1128", {"start": v(-30.6, -92.03) * mm, "end": v(-30.57, -92.2) * mm});
            skLineSegment(sketch, "E1129", {"start": v(-30.57, -92.2) * mm, "end": v(-28.52, -92.86) * mm});
            skLineSegment(sketch, "E1130", {"start": v(-28.52, -92.86) * mm, "end": v(-28.39, -92.74) * mm});
            skLineSegment(sketch, "E1131", {"start": v(-28.39, -92.74) * mm, "end": v(-28.25, -92.58) * mm});
            skLineSegment(sketch, "E1132", {"start": v(-28.25, -92.58) * mm, "end": v(-28.12, -92.43) * mm});
            skLineSegment(sketch, "E1133", {"start": v(-28.12, -92.43) * mm, "end": v(-27.99, -92.27) * mm});
            skLineSegment(sketch, "E1134", {"start": v(-27.99, -92.27) * mm, "end": v(-27.86, -92.12) * mm});
            skLineSegment(sketch, "E1135", {"start": v(-27.86, -92.12) * mm, "end": v(-27.73, -91.97) * mm});
            skLineSegment(sketch, "E1136", {"start": v(-27.73, -91.97) * mm, "end": v(-27.61, -91.82) * mm});
            skLineSegment(sketch, "E1137", {"start": v(-27.61, -91.82) * mm, "end": v(-27.49, -91.67) * mm});
            skLineSegment(sketch, "E1138", {"start": v(-27.49, -91.67) * mm, "end": v(-27.37, -91.52) * mm});
            skLineSegment(sketch, "E1139", {"start": v(-27.37, -91.52) * mm, "end": v(-27.25, -91.37) * mm});
            skLineSegment(sketch, "E1140", {"start": v(-27.25, -91.37) * mm, "end": v(-27.14, -91.23) * mm});
            skLineSegment(sketch, "E1141", {"start": v(-27.14, -91.23) * mm, "end": v(-27.03, -91.08) * mm});
            skLineSegment(sketch, "E1142", {"start": v(-27.03, -91.08) * mm, "end": v(-26.92, -90.94) * mm});
            skLineSegment(sketch, "E1143", {"start": v(-26.92, -90.94) * mm, "end": v(-26.81, -90.8) * mm});
            skLineSegment(sketch, "E1144", {"start": v(-26.81, -90.8) * mm, "end": v(-26.7, -90.66) * mm});
            skLineSegment(sketch, "E1145", {"start": v(-26.7, -90.66) * mm, "end": v(-26.6, -90.52) * mm});
            skLineSegment(sketch, "E1146", {"start": v(-26.6, -90.52) * mm, "end": v(-26.5, -90.38) * mm});
            skLineSegment(sketch, "E1147", {"start": v(-26.5, -90.38) * mm, "end": v(-26.4, -90.25) * mm});
            skLineSegment(sketch, "E1148", {"start": v(-26.4, -90.25) * mm, "end": v(-26.3, -90.11) * mm});
            skLineSegment(sketch, "E1149", {"start": v(-26.3, -90.11) * mm, "end": v(-26.21, -89.98) * mm});
            skLineSegment(sketch, "E1150", {"start": v(-26.21, -89.98) * mm, "end": v(-26.12, -89.85) * mm});
            skLineSegment(sketch, "E1151", {"start": v(-26.12, -89.85) * mm, "end": v(-26.03, -89.72) * mm});
            skLineSegment(sketch, "E1152", {"start": v(-26.03, -89.72) * mm, "end": v(-25.94, -89.6) * mm});
            skLineSegment(sketch, "E1153", {"start": v(-25.94, -89.6) * mm, "end": v(-25.86, -89.46) * mm});
            skLineSegment(sketch, "E1154", {"start": v(-25.86, -89.46) * mm, "end": v(-25.77, -89.34) * mm});
            skLineSegment(sketch, "E1155", {"start": v(-25.77, -89.34) * mm, "end": v(-25.69, -89.22) * mm});
            skLineSegment(sketch, "E1156", {"start": v(-25.69, -89.22) * mm, "end": v(-25.6, -89.1) * mm});
            skLineSegment(sketch, "E1157", {"start": v(-25.6, -89.1) * mm, "end": v(-25.53, -88.97) * mm});
            skLineSegment(sketch, "E1158", {"start": v(-25.53, -88.97) * mm, "end": v(-25.46, -88.86) * mm});
            skLineSegment(sketch, "E1159", {"start": v(-25.46, -88.86) * mm, "end": v(-25.38, -88.74) * mm});
            skLineSegment(sketch, "E1160", {"start": v(-25.38, -88.74) * mm, "end": v(-25.3, -88.62) * mm});
            skLineSegment(sketch, "E1161", {"start": v(-25.3, -88.62) * mm, "end": v(-25.24, -88.51) * mm});
            skLineSegment(sketch, "E1162", {"start": v(-25.24, -88.51) * mm, "end": v(-25.17, -88.4) * mm});
            skLineSegment(sketch, "E1163", {"start": v(-25.17, -88.4) * mm, "end": v(-25.1, -88.3) * mm});
            skLineSegment(sketch, "E1164", {"start": v(-25.1, -88.3) * mm, "end": v(-25.04, -88.18) * mm});
            skLineSegment(sketch, "E1165", {"start": v(-25.04, -88.18) * mm, "end": v(-24.98, -88.08) * mm});
            skLineSegment(sketch, "E1166", {"start": v(-24.98, -88.08) * mm, "end": v(-24.92, -87.97) * mm});
            skLineSegment(sketch, "E1167", {"start": v(-24.92, -87.97) * mm, "end": v(-24.86, -87.87) * mm});
            skLineSegment(sketch, "E1168", {"start": v(-24.86, -87.87) * mm, "end": v(-24.8, -87.77) * mm});
            skLineSegment(sketch, "E1169", {"start": v(-24.8, -87.77) * mm, "end": v(-24.33, -87.69) * mm});
            skLineSegment(sketch, "E1170", {"start": v(-24.33, -87.69) * mm, "end": v(-22.7, -88.12) * mm});
            skLineSegment(sketch, "E1171", {"start": v(-22.7, -88.12) * mm, "end": v(-22.34, -88.43) * mm});
            skLineSegment(sketch, "E1172", {"start": v(-22.34, -88.43) * mm, "end": v(-22.34, -88.54) * mm});
            skLineSegment(sketch, "E1173", {"start": v(-22.34, -88.54) * mm, "end": v(-22.34, -88.66) * mm});
            skLineSegment(sketch, "E1174", {"start": v(-22.34, -88.66) * mm, "end": v(-22.34, -88.78) * mm});
            skLineSegment(sketch, "E1175", {"start": v(-22.34, -88.78) * mm, "end": v(-22.34, -88.9) * mm});
            skLineSegment(sketch, "E1176", {"start": v(-22.34, -88.9) * mm, "end": v(-22.34, -89.03) * mm});
            skLineSegment(sketch, "E1177", {"start": v(-22.34, -89.03) * mm, "end": v(-22.33, -89.16) * mm});
            skLineSegment(sketch, "E1178", {"start": v(-22.33, -89.16) * mm, "end": v(-22.33, -89.3) * mm});
            skLineSegment(sketch, "E1179", {"start": v(-22.33, -89.3) * mm, "end": v(-22.33, -89.42) * mm});
            skLineSegment(sketch, "E1180", {"start": v(-22.33, -89.42) * mm, "end": v(-22.32, -89.56) * mm});
            skLineSegment(sketch, "E1181", {"start": v(-22.32, -89.56) * mm, "end": v(-22.31, -89.7) * mm});
            skLineSegment(sketch, "E1182", {"start": v(-22.31, -89.7) * mm, "end": v(-22.3, -89.84) * mm});
            skLineSegment(sketch, "E1183", {"start": v(-22.3, -89.84) * mm, "end": v(-22.3, -89.98) * mm});
            skLineSegment(sketch, "E1184", {"start": v(-22.3, -89.98) * mm, "end": v(-22.3, -90.12) * mm});
            skLineSegment(sketch, "E1185", {"start": v(-22.3, -90.12) * mm, "end": v(-22.28, -90.27) * mm});
            skLineSegment(sketch, "E1186", {"start": v(-22.28, -90.27) * mm, "end": v(-22.27, -90.42) * mm});
            skLineSegment(sketch, "E1187", {"start": v(-22.27, -90.42) * mm, "end": v(-22.26, -90.58) * mm});
            skLineSegment(sketch, "E1188", {"start": v(-22.26, -90.58) * mm, "end": v(-22.25, -90.73) * mm});
            skLineSegment(sketch, "E1189", {"start": v(-22.25, -90.73) * mm, "end": v(-22.23, -90.89) * mm});
            skLineSegment(sketch, "E1190", {"start": v(-22.23, -90.89) * mm, "end": v(-22.22, -91.05) * mm});
            skLineSegment(sketch, "E1191", {"start": v(-22.22, -91.05) * mm, "end": v(-22.2, -91.2) * mm});
            skLineSegment(sketch, "E1192", {"start": v(-22.2, -91.2) * mm, "end": v(-22.19, -91.37) * mm});
            skLineSegment(sketch, "E1193", {"start": v(-22.19, -91.37) * mm, "end": v(-22.17, -91.54) * mm});
            skLineSegment(sketch, "E1194", {"start": v(-22.17, -91.54) * mm, "end": v(-22.15, -91.7) * mm});
            skLineSegment(sketch, "E1195", {"start": v(-22.15, -91.7) * mm, "end": v(-22.13, -91.88) * mm});
            skLineSegment(sketch, "E1196", {"start": v(-22.13, -91.88) * mm, "end": v(-22.11, -92.06) * mm});
            skLineSegment(sketch, "E1197", {"start": v(-22.11, -92.06) * mm, "end": v(-22.09, -92.23) * mm});
            skLineSegment(sketch, "E1198", {"start": v(-22.09, -92.23) * mm, "end": v(-22.06, -92.41) * mm});
            skLineSegment(sketch, "E1199", {"start": v(-22.06, -92.41) * mm, "end": v(-22.04, -92.6) * mm});
            skLineSegment(sketch, "E1200", {"start": v(-22.04, -92.6) * mm, "end": v(-22.01, -92.77) * mm});
            skLineSegment(sketch, "E1201", {"start": v(-22.01, -92.77) * mm, "end": v(-21.98, -92.96) * mm});
            skLineSegment(sketch, "E1202", {"start": v(-21.98, -92.96) * mm, "end": v(-21.96, -93.15) * mm});
            skLineSegment(sketch, "E1203", {"start": v(-21.96, -93.15) * mm, "end": v(-21.93, -93.34) * mm});
            skLineSegment(sketch, "E1204", {"start": v(-21.93, -93.34) * mm, "end": v(-21.9, -93.53) * mm});
            skLineSegment(sketch, "E1205", {"start": v(-21.9, -93.53) * mm, "end": v(-21.86, -93.72) * mm});
            skLineSegment(sketch, "E1206", {"start": v(-21.86, -93.72) * mm, "end": v(-21.83, -93.92) * mm});
            skLineSegment(sketch, "E1207", {"start": v(-21.83, -93.92) * mm, "end": v(-21.79, -94.12) * mm});
            skLineSegment(sketch, "E1208", {"start": v(-21.79, -94.12) * mm, "end": v(-21.75, -94.32) * mm});
            skLineSegment(sketch, "E1209", {"start": v(-21.75, -94.32) * mm, "end": v(-21.71, -94.53) * mm});
            skLineSegment(sketch, "E1210", {"start": v(-21.71, -94.53) * mm, "end": v(-21.66, -94.7) * mm});
            skLineSegment(sketch, "E1211", {"start": v(-21.66, -94.7) * mm, "end": v(-19.56, -95.15) * mm});
            skLineSegment(sketch, "E1212", {"start": v(-19.56, -95.15) * mm, "end": v(-19.45, -95.02) * mm});
            skLineSegment(sketch, "E1213", {"start": v(-19.45, -95.02) * mm, "end": v(-19.32, -94.85) * mm});
            skLineSegment(sketch, "E1214", {"start": v(-19.32, -94.85) * mm, "end": v(-19.2, -94.68) * mm});
            skLineSegment(sketch, "E1215", {"start": v(-19.2, -94.68) * mm, "end": v(-19.1, -94.52) * mm});
            skLineSegment(sketch, "E1216", {"start": v(-19.1, -94.52) * mm, "end": v(-18.98, -94.35) * mm});
            skLineSegment(sketch, "E1217", {"start": v(-18.98, -94.35) * mm, "end": v(-18.87, -94.19) * mm});
            skLineSegment(sketch, "E1218", {"start": v(-18.87, -94.19) * mm, "end": v(-18.76, -94.03) * mm});
            skLineSegment(sketch, "E1219", {"start": v(-18.76, -94.03) * mm, "end": v(-18.65, -93.87) * mm});
            skLineSegment(sketch, "E1220", {"start": v(-18.65, -93.87) * mm, "end": v(-18.55, -93.7) * mm});
            skLineSegment(sketch, "E1221", {"start": v(-18.55, -93.7) * mm, "end": v(-18.45, -93.55) * mm});
            skLineSegment(sketch, "E1222", {"start": v(-18.45, -93.55) * mm, "end": v(-18.35, -93.4) * mm});
            skLineSegment(sketch, "E1223", {"start": v(-18.35, -93.4) * mm, "end": v(-18.25, -93.24) * mm});
            skLineSegment(sketch, "E1224", {"start": v(-18.25, -93.24) * mm, "end": v(-18.15, -93.09) * mm});
            skLineSegment(sketch, "E1225", {"start": v(-18.15, -93.09) * mm, "end": v(-18.06, -92.94) * mm});
            skLineSegment(sketch, "E1226", {"start": v(-18.06, -92.94) * mm, "end": v(-17.97, -92.79) * mm});
            skLineSegment(sketch, "E1227", {"start": v(-17.97, -92.79) * mm, "end": v(-17.88, -92.64) * mm});
            skLineSegment(sketch, "E1228", {"start": v(-17.88, -92.64) * mm, "end": v(-17.79, -92.5) * mm});
            skLineSegment(sketch, "E1229", {"start": v(-17.79, -92.5) * mm, "end": v(-17.7, -92.35) * mm});
            skLineSegment(sketch, "E1230", {"start": v(-17.7, -92.35) * mm, "end": v(-17.62, -92.2) * mm});
            skLineSegment(sketch, "E1231", {"start": v(-17.62, -92.2) * mm, "end": v(-17.54, -92.06) * mm});
            skLineSegment(sketch, "E1232", {"start": v(-17.54, -92.06) * mm, "end": v(-17.46, -91.92) * mm});
            skLineSegment(sketch, "E1233", {"start": v(-17.46, -91.92) * mm, "end": v(-17.38, -91.79) * mm});
            skLineSegment(sketch, "E1234", {"start": v(-17.38, -91.79) * mm, "end": v(-17.3, -91.65) * mm});
            skLineSegment(sketch, "E1235", {"start": v(-17.3, -91.65) * mm, "end": v(-17.23, -91.52) * mm});
            skLineSegment(sketch, "E1236", {"start": v(-17.23, -91.52) * mm, "end": v(-17.16, -91.38) * mm});
            skLineSegment(sketch, "E1237", {"start": v(-17.16, -91.38) * mm, "end": v(-17.1, -91.25) * mm});
            skLineSegment(sketch, "E1238", {"start": v(-17.1, -91.25) * mm, "end": v(-17.02, -91.13) * mm});
            skLineSegment(sketch, "E1239", {"start": v(-17.02, -91.13) * mm, "end": v(-16.96, -91) * mm});
            skLineSegment(sketch, "E1240", {"start": v(-16.96, -91) * mm, "end": v(-16.9, -90.87) * mm});
            skLineSegment(sketch, "E1241", {"start": v(-16.9, -90.87) * mm, "end": v(-16.83, -90.75) * mm});
            skLineSegment(sketch, "E1242", {"start": v(-16.83, -90.75) * mm, "end": v(-16.77, -90.63) * mm});
            skLineSegment(sketch, "E1243", {"start": v(-16.77, -90.63) * mm, "end": v(-16.71, -90.5) * mm});
            skLineSegment(sketch, "E1244", {"start": v(-16.71, -90.5) * mm, "end": v(-16.65, -90.4) * mm});
            skLineSegment(sketch, "E1245", {"start": v(-16.65, -90.4) * mm, "end": v(-16.6, -90.28) * mm});
            skLineSegment(sketch, "E1246", {"start": v(-16.6, -90.28) * mm, "end": v(-16.55, -90.16) * mm});
            skLineSegment(sketch, "E1247", {"start": v(-16.55, -90.16) * mm, "end": v(-16.5, -90.05) * mm});
            skLineSegment(sketch, "E1248", {"start": v(-16.5, -90.05) * mm, "end": v(-16.44, -89.94) * mm});
            skLineSegment(sketch, "E1249", {"start": v(-16.44, -89.94) * mm, "end": v(-16.4, -89.84) * mm});
            skLineSegment(sketch, "E1250", {"start": v(-16.4, -89.84) * mm, "end": v(-16.35, -89.73) * mm});
            skLineSegment(sketch, "E1251", {"start": v(-16.35, -89.73) * mm, "end": v(-15.89, -89.6) * mm});
            skLineSegment(sketch, "E1252", {"start": v(-15.89, -89.6) * mm, "end": v(-14.22, -89.88) * mm});
            skLineSegment(sketch, "E1253", {"start": v(-14.22, -89.88) * mm, "end": v(-13.83, -90.15) * mm});
            skLineSegment(sketch, "E1254", {"start": v(-13.83, -90.15) * mm, "end": v(-13.82, -90.27) * mm});
            skLineSegment(sketch, "E1255", {"start": v(-13.82, -90.27) * mm, "end": v(-13.81, -90.38) * mm});
            skLineSegment(sketch, "E1256", {"start": v(-13.81, -90.38) * mm, "end": v(-13.8, -90.5) * mm});
            skLineSegment(sketch, "E1257", {"start": v(-13.8, -90.5) * mm, "end": v(-13.79, -90.63) * mm});
            skLineSegment(sketch, "E1258", {"start": v(-13.79, -90.63) * mm, "end": v(-13.77, -90.75) * mm});
            skLineSegment(sketch, "E1259", {"start": v(-13.77, -90.75) * mm, "end": v(-13.76, -90.88) * mm});
            skLineSegment(sketch, "E1260", {"start": v(-13.76, -90.88) * mm, "end": v(-13.74, -91) * mm});
            skLineSegment(sketch, "E1261", {"start": v(-13.74, -91) * mm, "end": v(-13.72, -91.14) * mm});
            skLineSegment(sketch, "E1262", {"start": v(-13.72, -91.14) * mm, "end": v(-13.7, -91.27) * mm});
            skLineSegment(sketch, "E1263", {"start": v(-13.7, -91.27) * mm, "end": v(-13.69, -91.41) * mm});
            skLineSegment(sketch, "E1264", {"start": v(-13.69, -91.41) * mm, "end": v(-13.67, -91.55) * mm});
            skLineSegment(sketch, "E1265", {"start": v(-13.67, -91.55) * mm, "end": v(-13.65, -91.7) * mm});
            skLineSegment(sketch, "E1266", {"start": v(-13.65, -91.7) * mm, "end": v(-13.62, -91.84) * mm});
            skLineSegment(sketch, "E1267", {"start": v(-13.62, -91.84) * mm, "end": v(-13.6, -91.98) * mm});
            skLineSegment(sketch, "E1268", {"start": v(-13.6, -91.98) * mm, "end": v(-13.58, -92.13) * mm});
            skLineSegment(sketch, "E1269", {"start": v(-13.58, -92.13) * mm, "end": v(-13.55, -92.28) * mm});
            skLineSegment(sketch, "E1270", {"start": v(-13.55, -92.28) * mm, "end": v(-13.52, -92.43) * mm});
            skLineSegment(sketch, "E1271", {"start": v(-13.52, -92.43) * mm, "end": v(-13.5, -92.59) * mm});
            skLineSegment(sketch, "E1272", {"start": v(-13.5, -92.59) * mm, "end": v(-13.47, -92.75) * mm});
            skLineSegment(sketch, "E1273", {"start": v(-13.47, -92.75) * mm, "end": v(-13.43, -92.9) * mm});
            skLineSegment(sketch, "E1274", {"start": v(-13.43, -92.9) * mm, "end": v(-13.4, -93.07) * mm});
            skLineSegment(sketch, "E1275", {"start": v(-13.4, -93.07) * mm, "end": v(-13.37, -93.23) * mm});
            skLineSegment(sketch, "E1276", {"start": v(-13.37, -93.23) * mm, "end": v(-13.33, -93.4) * mm});
            skLineSegment(sketch, "E1277", {"start": v(-13.33, -93.4) * mm, "end": v(-13.3, -93.57) * mm});
            skLineSegment(sketch, "E1278", {"start": v(-13.3, -93.57) * mm, "end": v(-13.26, -93.74) * mm});
            skLineSegment(sketch, "E1279", {"start": v(-13.26, -93.74) * mm, "end": v(-13.22, -93.91) * mm});
            skLineSegment(sketch, "E1280", {"start": v(-13.22, -93.91) * mm, "end": v(-13.18, -94.09) * mm});
            skLineSegment(sketch, "E1281", {"start": v(-13.18, -94.09) * mm, "end": v(-13.14, -94.27) * mm});
            skLineSegment(sketch, "E1282", {"start": v(-13.14, -94.27) * mm, "end": v(-13.1, -94.45) * mm});
            skLineSegment(sketch, "E1283", {"start": v(-13.1, -94.45) * mm, "end": v(-13.05, -94.63) * mm});
            skLineSegment(sketch, "E1284", {"start": v(-13.05, -94.63) * mm, "end": v(-13, -94.81) * mm});
            skLineSegment(sketch, "E1285", {"start": v(-13, -94.81) * mm, "end": v(-12.95, -95) * mm});
            skLineSegment(sketch, "E1286", {"start": v(-12.95, -95) * mm, "end": v(-12.9, -95.19) * mm});
            skLineSegment(sketch, "E1287", {"start": v(-12.9, -95.19) * mm, "end": v(-12.85, -95.38) * mm});
            skLineSegment(sketch, "E1288", {"start": v(-12.85, -95.38) * mm, "end": v(-12.8, -95.57) * mm});
            skLineSegment(sketch, "E1289", {"start": v(-12.8, -95.57) * mm, "end": v(-12.74, -95.77) * mm});
            skLineSegment(sketch, "E1290", {"start": v(-12.74, -95.77) * mm, "end": v(-12.69, -95.96) * mm});
            skLineSegment(sketch, "E1291", {"start": v(-12.69, -95.96) * mm, "end": v(-12.63, -96.16) * mm});
            skLineSegment(sketch, "E1292", {"start": v(-12.63, -96.16) * mm, "end": v(-12.56, -96.33) * mm});
            skLineSegment(sketch, "E1293", {"start": v(-12.56, -96.33) * mm, "end": v(-10.43, -96.58) * mm});
            skLineSegment(sketch, "E1294", {"start": v(-10.43, -96.58) * mm, "end": v(-10.33, -96.44) * mm});
            skLineSegment(sketch, "E1295", {"start": v(-10.33, -96.44) * mm, "end": v(-10.22, -96.26) * mm});
            skLineSegment(sketch, "E1296", {"start": v(-10.22, -96.26) * mm, "end": v(-10.12, -96.08) * mm});
            skLineSegment(sketch, "E1297", {"start": v(-10.12, -96.08) * mm, "end": v(-10.02, -95.9) * mm});
            skLineSegment(sketch, "E1298", {"start": v(-10.02, -95.9) * mm, "end": v(-9.92, -95.73) * mm});
            skLineSegment(sketch, "E1299", {"start": v(-9.92, -95.73) * mm, "end": v(-9.83, -95.55) * mm});
            skLineSegment(sketch, "E1300", {"start": v(-9.83, -95.55) * mm, "end": v(-9.74, -95.38) * mm});
            skLineSegment(sketch, "E1301", {"start": v(-9.74, -95.38) * mm, "end": v(-9.64, -95.21) * mm});
            skLineSegment(sketch, "E1302", {"start": v(-9.64, -95.21) * mm, "end": v(-9.56, -95.04) * mm});
            skLineSegment(sketch, "E1303", {"start": v(-9.56, -95.04) * mm, "end": v(-9.47, -94.88) * mm});
            skLineSegment(sketch, "E1304", {"start": v(-9.47, -94.88) * mm, "end": v(-9.38, -94.71) * mm});
            skLineSegment(sketch, "E1305", {"start": v(-9.38, -94.71) * mm, "end": v(-9.3, -94.55) * mm});
            skLineSegment(sketch, "E1306", {"start": v(-9.3, -94.55) * mm, "end": v(-9.22, -94.4) * mm});
            skLineSegment(sketch, "E1307", {"start": v(-9.22, -94.4) * mm, "end": v(-9.14, -94.23) * mm});
            skLineSegment(sketch, "E1308", {"start": v(-9.14, -94.23) * mm, "end": v(-9.07, -94.07) * mm});
            skLineSegment(sketch, "E1309", {"start": v(-9.07, -94.07) * mm, "end": v(-9, -93.92) * mm});
            skLineSegment(sketch, "E1310", {"start": v(-9, -93.92) * mm, "end": v(-8.92, -93.76) * mm});
            skLineSegment(sketch, "E1311", {"start": v(-8.92, -93.76) * mm, "end": v(-8.85, -93.61) * mm});
            skLineSegment(sketch, "E1312", {"start": v(-8.85, -93.61) * mm, "end": v(-8.78, -93.46) * mm});
            skLineSegment(sketch, "E1313", {"start": v(-8.78, -93.46) * mm, "end": v(-8.7, -93.31) * mm});
            skLineSegment(sketch, "E1314", {"start": v(-8.7, -93.31) * mm, "end": v(-8.64, -93.17) * mm});
            skLineSegment(sketch, "E1315", {"start": v(-8.64, -93.17) * mm, "end": v(-8.58, -93.02) * mm});
            skLineSegment(sketch, "E1316", {"start": v(-8.58, -93.02) * mm, "end": v(-8.52, -92.88) * mm});
            skLineSegment(sketch, "E1317", {"start": v(-8.52, -92.88) * mm, "end": v(-8.46, -92.74) * mm});
            skLineSegment(sketch, "E1318", {"start": v(-8.46, -92.74) * mm, "end": v(-8.4, -92.6) * mm});
            skLineSegment(sketch, "E1319", {"start": v(-8.4, -92.6) * mm, "end": v(-8.34, -92.47) * mm});
            skLineSegment(sketch, "E1320", {"start": v(-8.34, -92.47) * mm, "end": v(-8.29, -92.33) * mm});
            skLineSegment(sketch, "E1321", {"start": v(-8.29, -92.33) * mm, "end": v(-8.23, -92.2) * mm});
            skLineSegment(sketch, "E1322", {"start": v(-8.23, -92.2) * mm, "end": v(-8.18, -92.07) * mm});
            skLineSegment(sketch, "E1323", {"start": v(-8.18, -92.07) * mm, "end": v(-8.13, -91.94) * mm});
            skLineSegment(sketch, "E1324", {"start": v(-8.13, -91.94) * mm, "end": v(-8.08, -91.81) * mm});
            skLineSegment(sketch, "E1325", {"start": v(-8.08, -91.81) * mm, "end": v(-8.03, -91.69) * mm});
            skLineSegment(sketch, "E1326", {"start": v(-8.03, -91.69) * mm, "end": v(-7.99, -91.57) * mm});
            skLineSegment(sketch, "E1327", {"start": v(-7.99, -91.57) * mm, "end": v(-7.94, -91.45) * mm});
            skLineSegment(sketch, "E1328", {"start": v(-7.94, -91.45) * mm, "end": v(-7.9, -91.33) * mm});
            skLineSegment(sketch, "E1329", {"start": v(-7.9, -91.33) * mm, "end": v(-7.86, -91.21) * mm});
            skLineSegment(sketch, "E1330", {"start": v(-7.86, -91.21) * mm, "end": v(-7.82, -91.1) * mm});
            skLineSegment(sketch, "E1331", {"start": v(-7.82, -91.1) * mm, "end": v(-7.78, -90.99) * mm});
            skLineSegment(sketch, "E1332", {"start": v(-7.78, -90.99) * mm, "end": v(-7.74, -90.88) * mm});
            skLineSegment(sketch, "E1333", {"start": v(-7.74, -90.88) * mm, "end": v(-7.3, -90.7) * mm});
            skLineSegment(sketch, "E1334", {"start": v(-7.3, -90.7) * mm, "end": v(-5.62, -90.83) * mm});
            skLineSegment(sketch, "E1335", {"start": v(-5.62, -90.83) * mm, "end": v(-5.2, -91.06) * mm});
            skLineSegment(sketch, "E1336", {"start": v(-5.2, -91.06) * mm, "end": v(-5.18, -91.17) * mm});
            skLineSegment(sketch, "E1337", {"start": v(-5.18, -91.17) * mm, "end": v(-5.16, -91.29) * mm});
            skLineSegment(sketch, "E1338", {"start": v(-5.16, -91.29) * mm, "end": v(-5.13, -91.4) * mm});
            skLineSegment(sketch, "E1339", {"start": v(-5.13, -91.4) * mm, "end": v(-5.1, -91.53) * mm});
            skLineSegment(sketch, "E1340", {"start": v(-5.1, -91.53) * mm, "end": v(-5.08, -91.65) * mm});
            skLineSegment(sketch, "E1341", {"start": v(-5.08, -91.65) * mm, "end": v(-5.06, -91.77) * mm});
            skLineSegment(sketch, "E1342", {"start": v(-5.06, -91.77) * mm, "end": v(-5.03, -91.9) * mm});
            skLineSegment(sketch, "E1343", {"start": v(-5.03, -91.9) * mm, "end": v(-5, -92.03) * mm});
            skLineSegment(sketch, "E1344", {"start": v(-5, -92.03) * mm, "end": v(-4.97, -92.16) * mm});
            skLineSegment(sketch, "E1345", {"start": v(-4.97, -92.16) * mm, "end": v(-4.94, -92.3) * mm});
            skLineSegment(sketch, "E1346", {"start": v(-4.94, -92.3) * mm, "end": v(-4.9, -92.44) * mm});
            skLineSegment(sketch, "E1347", {"start": v(-4.9, -92.44) * mm, "end": v(-4.87, -92.57) * mm});
            skLineSegment(sketch, "E1348", {"start": v(-4.87, -92.57) * mm, "end": v(-4.83, -92.71) * mm});
            skLineSegment(sketch, "E1349", {"start": v(-4.83, -92.71) * mm, "end": v(-4.8, -92.86) * mm});
            skLineSegment(sketch, "E1350", {"start": v(-4.8, -92.86) * mm, "end": v(-4.76, -93) * mm});
            skLineSegment(sketch, "E1351", {"start": v(-4.76, -93) * mm, "end": v(-4.72, -93.15) * mm});
            skLineSegment(sketch, "E1352", {"start": v(-4.72, -93.15) * mm, "end": v(-4.68, -93.3) * mm});
            skLineSegment(sketch, "E1353", {"start": v(-4.68, -93.3) * mm, "end": v(-4.63, -93.45) * mm});
            skLineSegment(sketch, "E1354", {"start": v(-4.63, -93.45) * mm, "end": v(-4.59, -93.6) * mm});
            skLineSegment(sketch, "E1355", {"start": v(-4.59, -93.6) * mm, "end": v(-4.54, -93.76) * mm});
            skLineSegment(sketch, "E1356", {"start": v(-4.54, -93.76) * mm, "end": v(-4.5, -93.92) * mm});
            skLineSegment(sketch, "E1357", {"start": v(-4.5, -93.92) * mm, "end": v(-4.45, -94.08) * mm});
            skLineSegment(sketch, "E1358", {"start": v(-4.45, -94.08) * mm, "end": v(-4.4, -94.24) * mm});
            skLineSegment(sketch, "E1359", {"start": v(-4.4, -94.24) * mm, "end": v(-4.34, -94.4) * mm});
            skLineSegment(sketch, "E1360", {"start": v(-4.34, -94.4) * mm, "end": v(-4.29, -94.58) * mm});
            skLineSegment(sketch, "E1361", {"start": v(-4.29, -94.58) * mm, "end": v(-4.23, -94.74) * mm});
            skLineSegment(sketch, "E1362", {"start": v(-4.23, -94.74) * mm, "end": v(-4.18, -94.92) * mm});
            skLineSegment(sketch, "E1363", {"start": v(-4.18, -94.92) * mm, "end": v(-4.12, -95.09) * mm});
            skLineSegment(sketch, "E1364", {"start": v(-4.12, -95.09) * mm, "end": v(-4.06, -95.26) * mm});
            skLineSegment(sketch, "E1365", {"start": v(-4.06, -95.26) * mm, "end": v(-4, -95.44) * mm});
            skLineSegment(sketch, "E1366", {"start": v(-4, -95.44) * mm, "end": v(-3.93, -95.62) * mm});
            skLineSegment(sketch, "E1367", {"start": v(-3.93, -95.62) * mm, "end": v(-3.86, -95.8) * mm});
            skLineSegment(sketch, "E1368", {"start": v(-3.86, -95.8) * mm, "end": v(-3.8, -95.98) * mm});
            skLineSegment(sketch, "E1369", {"start": v(-3.8, -95.98) * mm, "end": v(-3.73, -96.17) * mm});
            skLineSegment(sketch, "E1370", {"start": v(-3.73, -96.17) * mm, "end": v(-3.66, -96.36) * mm});
            skLineSegment(sketch, "E1371", {"start": v(-3.66, -96.36) * mm, "end": v(-3.58, -96.54) * mm});
            skLineSegment(sketch, "E1372", {"start": v(-3.58, -96.54) * mm, "end": v(-3.5, -96.73) * mm});
            skLineSegment(sketch, "E1373", {"start": v(-3.5, -96.73) * mm, "end": v(-3.43, -96.93) * mm});
            skLineSegment(sketch, "E1374", {"start": v(-3.43, -96.93) * mm, "end": v(-3.35, -97.09) * mm});
            skLineSegment(sketch, "E1375", {"start": v(-3.35, -97.09) * mm, "end": v(-1.2, -97.14) * mm});
            skLineSegment(sketch, "E1376", {"start": v(-1.2, -97.14) * mm, "end": v(-1.11, -96.98) * mm});
            skLineSegment(sketch, "E1377", {"start": v(-1.11, -96.98) * mm, "end": v(-1.03, -96.8) * mm});
            skLineSegment(sketch, "E1378", {"start": v(-1.03, -96.8) * mm, "end": v(-0.94, -96.6) * mm});
            skLineSegment(sketch, "E1379", {"start": v(-0.94, -96.6) * mm, "end": v(-0.86, -96.42) * mm});
            skLineSegment(sketch, "E1380", {"start": v(-0.86, -96.42) * mm, "end": v(-0.78, -96.24) * mm});
            skLineSegment(sketch, "E1381", {"start": v(-0.78, -96.24) * mm, "end": v(-0.7, -96.06) * mm});
            skLineSegment(sketch, "E1382", {"start": v(-0.7, -96.06) * mm, "end": v(-0.62, -95.88) * mm});
            skLineSegment(sketch, "E1383", {"start": v(-0.62, -95.88) * mm, "end": v(-0.55, -95.7) * mm});
            skLineSegment(sketch, "E1384", {"start": v(-0.55, -95.7) * mm, "end": v(-0.48, -95.52) * mm});
            skLineSegment(sketch, "E1385", {"start": v(-0.48, -95.52) * mm, "end": v(-0.4, -95.35) * mm});
            skLineSegment(sketch, "E1386", {"start": v(-0.4, -95.35) * mm, "end": v(-0.34, -95.18) * mm});
            skLineSegment(sketch, "E1387", {"start": v(-0.34, -95.18) * mm, "end": v(-0.27, -95) * mm});
            skLineSegment(sketch, "E1388", {"start": v(-0.27, -95) * mm, "end": v(-0.2, -94.84) * mm});
            skLineSegment(sketch, "E1389", {"start": v(-0.2, -94.84) * mm, "end": v(-0.14, -94.67) * mm});
            skLineSegment(sketch, "E1390", {"start": v(-0.14, -94.67) * mm, "end": v(-0.08, -94.5) * mm});
            skLineSegment(sketch, "E1391", {"start": v(-0.08, -94.5) * mm, "end": v(-0.02, -94.35) * mm});
            skLineSegment(sketch, "E1392", {"start": v(-0.02, -94.35) * mm, "end": v(0.04, -94.19) * mm});
            skLineSegment(sketch, "E1393", {"start": v(0.04, -94.19) * mm, "end": v(0.1, -94.03) * mm});
            skLineSegment(sketch, "E1394", {"start": v(0.1, -94.03) * mm, "end": v(0.15, -93.87) * mm});
            skLineSegment(sketch, "E1395", {"start": v(0.15, -93.87) * mm, "end": v(0.2, -93.72) * mm});
            skLineSegment(sketch, "E1396", {"start": v(0.2, -93.72) * mm, "end": v(0.25, -93.57) * mm});
            skLineSegment(sketch, "E1397", {"start": v(0.25, -93.57) * mm, "end": v(0.3, -93.42) * mm});
            skLineSegment(sketch, "E1398", {"start": v(0.3, -93.42) * mm, "end": v(0.35, -93.27) * mm});
            skLineSegment(sketch, "E1399", {"start": v(0.35, -93.27) * mm, "end": v(0.4, -93.12) * mm});
            skLineSegment(sketch, "E1400", {"start": v(0.4, -93.12) * mm, "end": v(0.44, -92.98) * mm});
            skLineSegment(sketch, "E1401", {"start": v(0.44, -92.98) * mm, "end": v(0.49, -92.84) * mm});
            skLineSegment(sketch, "E1402", {"start": v(0.49, -92.84) * mm, "end": v(0.53, -92.7) * mm});
            skLineSegment(sketch, "E1403", {"start": v(0.53, -92.7) * mm, "end": v(0.57, -92.56) * mm});
            skLineSegment(sketch, "E1404", {"start": v(0.57, -92.56) * mm, "end": v(0.6, -92.43) * mm});
            skLineSegment(sketch, "E1405", {"start": v(0.6, -92.43) * mm, "end": v(0.65, -92.3) * mm});
            skLineSegment(sketch, "E1406", {"start": v(0.65, -92.3) * mm, "end": v(0.68, -92.17) * mm});
            skLineSegment(sketch, "E1407", {"start": v(0.68, -92.17) * mm, "end": v(0.72, -92.04) * mm});
            skLineSegment(sketch, "E1408", {"start": v(0.72, -92.04) * mm, "end": v(0.75, -91.91) * mm});
            skLineSegment(sketch, "E1409", {"start": v(0.75, -91.91) * mm, "end": v(0.79, -91.79) * mm});
            skLineSegment(sketch, "E1410", {"start": v(0.79, -91.79) * mm, "end": v(0.82, -91.67) * mm});
            skLineSegment(sketch, "E1411", {"start": v(0.82, -91.67) * mm, "end": v(0.85, -91.55) * mm});
            skLineSegment(sketch, "E1412", {"start": v(0.85, -91.55) * mm, "end": v(0.88, -91.43) * mm});
            skLineSegment(sketch, "E1413", {"start": v(0.88, -91.43) * mm, "end": v(0.9, -91.31) * mm});
            skLineSegment(sketch, "E1414", {"start": v(0.9, -91.31) * mm, "end": v(0.93, -91.2) * mm});
            skLineSegment(sketch, "E1415", {"start": v(0.93, -91.2) * mm, "end": v(1.36, -90.99) * mm});
            skLineSegment(sketch, "E1416", {"start": v(1.36, -90.99) * mm, "end": v(3.04, -90.95) * mm});
            skLineSegment(sketch, "E1417", {"start": v(3.04, -90.95) * mm, "end": v(3.48, -91.14) * mm});
            skLineSegment(sketch, "E1418", {"start": v(3.48, -91.14) * mm, "end": v(3.51, -91.25) * mm});
            skLineSegment(sketch, "E1419", {"start": v(3.51, -91.25) * mm, "end": v(3.54, -91.36) * mm});
            skLineSegment(sketch, "E1420", {"start": v(3.54, -91.36) * mm, "end": v(3.58, -91.48) * mm});
            skLineSegment(sketch, "E1421", {"start": v(3.58, -91.48) * mm, "end": v(3.61, -91.6) * mm});
            skLineSegment(sketch, "E1422", {"start": v(3.61, -91.6) * mm, "end": v(3.65, -91.72) * mm});
            skLineSegment(sketch, "E1423", {"start": v(3.65, -91.72) * mm, "end": v(3.7, -91.84) * mm});
            skLineSegment(sketch, "E1424", {"start": v(3.7, -91.84) * mm, "end": v(3.73, -91.96) * mm});
            skLineSegment(sketch, "E1425", {"start": v(3.73, -91.96) * mm, "end": v(3.77, -92.1) * mm});
            skLineSegment(sketch, "E1426", {"start": v(3.77, -92.1) * mm, "end": v(3.82, -92.22) * mm});
            skLineSegment(sketch, "E1427", {"start": v(3.82, -92.22) * mm, "end": v(3.86, -92.35) * mm});
            skLineSegment(sketch, "E1428", {"start": v(3.86, -92.35) * mm, "end": v(3.9, -92.48) * mm});
            skLineSegment(sketch, "E1429", {"start": v(3.9, -92.48) * mm, "end": v(3.95, -92.62) * mm});
            skLineSegment(sketch, "E1430", {"start": v(3.95, -92.62) * mm, "end": v(4, -92.75) * mm});
            skLineSegment(sketch, "E1431", {"start": v(4, -92.75) * mm, "end": v(4.05, -92.9) * mm});
            skLineSegment(sketch, "E1432", {"start": v(4.05, -92.9) * mm, "end": v(4.1, -93.03) * mm});
            skLineSegment(sketch, "E1433", {"start": v(4.1, -93.03) * mm, "end": v(4.16, -93.18) * mm});
            skLineSegment(sketch, "E1434", {"start": v(4.16, -93.18) * mm, "end": v(4.21, -93.32) * mm});
            skLineSegment(sketch, "E1435", {"start": v(4.21, -93.32) * mm, "end": v(4.27, -93.47) * mm});
            skLineSegment(sketch, "E1436", {"start": v(4.27, -93.47) * mm, "end": v(4.33, -93.62) * mm});
            skLineSegment(sketch, "E1437", {"start": v(4.33, -93.62) * mm, "end": v(4.4, -93.77) * mm});
            skLineSegment(sketch, "E1438", {"start": v(4.4, -93.77) * mm, "end": v(4.45, -93.92) * mm});
            skLineSegment(sketch, "E1439", {"start": v(4.45, -93.92) * mm, "end": v(4.52, -94.08) * mm});
            skLineSegment(sketch, "E1440", {"start": v(4.52, -94.08) * mm, "end": v(4.58, -94.24) * mm});
            skLineSegment(sketch, "E1441", {"start": v(4.58, -94.24) * mm, "end": v(4.65, -94.4) * mm});
            skLineSegment(sketch, "E1442", {"start": v(4.65, -94.4) * mm, "end": v(4.72, -94.56) * mm});
            skLineSegment(sketch, "E1443", {"start": v(4.72, -94.56) * mm, "end": v(4.8, -94.72) * mm});
            skLineSegment(sketch, "E1444", {"start": v(4.8, -94.72) * mm, "end": v(4.86, -94.88) * mm});
            skLineSegment(sketch, "E1445", {"start": v(4.86, -94.88) * mm, "end": v(4.94, -95.05) * mm});
            skLineSegment(sketch, "E1446", {"start": v(4.94, -95.05) * mm, "end": v(5.02, -95.22) * mm});
            skLineSegment(sketch, "E1447", {"start": v(5.02, -95.22) * mm, "end": v(5.1, -95.39) * mm});
            skLineSegment(sketch, "E1448", {"start": v(5.1, -95.39) * mm, "end": v(5.18, -95.56) * mm});
            skLineSegment(sketch, "E1449", {"start": v(5.18, -95.56) * mm, "end": v(5.26, -95.73) * mm});
            skLineSegment(sketch, "E1450", {"start": v(5.26, -95.73) * mm, "end": v(5.34, -95.9) * mm});
            skLineSegment(sketch, "E1451", {"start": v(5.34, -95.9) * mm, "end": v(5.43, -96.09) * mm});
            skLineSegment(sketch, "E1452", {"start": v(5.43, -96.09) * mm, "end": v(5.52, -96.27) * mm});
            skLineSegment(sketch, "E1453", {"start": v(5.52, -96.27) * mm, "end": v(5.61, -96.45) * mm});
            skLineSegment(sketch, "E1454", {"start": v(5.61, -96.45) * mm, "end": v(5.7, -96.63) * mm});
            skLineSegment(sketch, "E1455", {"start": v(5.7, -96.63) * mm, "end": v(5.8, -96.81) * mm});
            skLineSegment(sketch, "E1456", {"start": v(5.8, -96.81) * mm, "end": v(5.9, -96.96) * mm});
            skLineSegment(sketch, "E1457", {"start": v(5.9, -96.96) * mm, "end": v(8.04, -96.8) * mm});
            skLineSegment(sketch, "E1458", {"start": v(8.04, -96.8) * mm, "end": v(8.11, -96.65) * mm});
            skLineSegment(sketch, "E1459", {"start": v(8.11, -96.65) * mm, "end": v(8.18, -96.45) * mm});
            skLineSegment(sketch, "E1460", {"start": v(8.18, -96.45) * mm, "end": v(8.25, -96.26) * mm});
            skLineSegment(sketch, "E1461", {"start": v(8.25, -96.26) * mm, "end": v(8.3, -96.07) * mm});
            skLineSegment(sketch, "E1462", {"start": v(8.3, -96.07) * mm, "end": v(8.37, -95.88) * mm});
            skLineSegment(sketch, "E1463", {"start": v(8.37, -95.88) * mm, "end": v(8.43, -95.69) * mm});
            skLineSegment(sketch, "E1464", {"start": v(8.43, -95.69) * mm, "end": v(8.5, -95.5) * mm});
            skLineSegment(sketch, "E1465", {"start": v(8.5, -95.5) * mm, "end": v(8.55, -95.32) * mm});
            skLineSegment(sketch, "E1466", {"start": v(8.55, -95.32) * mm, "end": v(8.6, -95.14) * mm});
            skLineSegment(sketch, "E1467", {"start": v(8.6, -95.14) * mm, "end": v(8.66, -94.96) * mm});
            skLineSegment(sketch, "E1468", {"start": v(8.66, -94.96) * mm, "end": v(8.7, -94.78) * mm});
            skLineSegment(sketch, "E1469", {"start": v(8.7, -94.78) * mm, "end": v(8.76, -94.6) * mm});
            skLineSegment(sketch, "E1470", {"start": v(8.76, -94.6) * mm, "end": v(8.8, -94.43) * mm});
            skLineSegment(sketch, "E1471", {"start": v(8.8, -94.43) * mm, "end": v(8.86, -94.26) * mm});
            skLineSegment(sketch, "E1472", {"start": v(8.86, -94.26) * mm, "end": v(8.9, -94.09) * mm});
            skLineSegment(sketch, "E1473", {"start": v(8.9, -94.09) * mm, "end": v(8.95, -93.92) * mm});
            skLineSegment(sketch, "E1474", {"start": v(8.95, -93.92) * mm, "end": v(8.99, -93.76) * mm});
            skLineSegment(sketch, "E1475", {"start": v(8.99, -93.76) * mm, "end": v(9.03, -93.6) * mm});
            skLineSegment(sketch, "E1476", {"start": v(9.03, -93.6) * mm, "end": v(9.07, -93.43) * mm});
            skLineSegment(sketch, "E1477", {"start": v(9.07, -93.43) * mm, "end": v(9.1, -93.28) * mm});
            skLineSegment(sketch, "E1478", {"start": v(9.1, -93.28) * mm, "end": v(9.14, -93.12) * mm});
            skLineSegment(sketch, "E1479", {"start": v(9.14, -93.12) * mm, "end": v(9.18, -92.97) * mm});
            skLineSegment(sketch, "E1480", {"start": v(9.18, -92.97) * mm, "end": v(9.21, -92.81) * mm});
            skLineSegment(sketch, "E1481", {"start": v(9.21, -92.81) * mm, "end": v(9.25, -92.66) * mm});
            skLineSegment(sketch, "E1482", {"start": v(9.25, -92.66) * mm, "end": v(9.28, -92.52) * mm});
            skLineSegment(sketch, "E1483", {"start": v(9.28, -92.52) * mm, "end": v(9.3, -92.37) * mm});
            skLineSegment(sketch, "E1484", {"start": v(9.3, -92.37) * mm, "end": v(9.34, -92.23) * mm});
            skLineSegment(sketch, "E1485", {"start": v(9.34, -92.23) * mm, "end": v(9.37, -92.1) * mm});
            skLineSegment(sketch, "E1486", {"start": v(9.37, -92.1) * mm, "end": v(9.4, -91.95) * mm});
            skLineSegment(sketch, "E1487", {"start": v(9.4, -91.95) * mm, "end": v(9.42, -91.82) * mm});
            skLineSegment(sketch, "E1488", {"start": v(9.42, -91.82) * mm, "end": v(9.44, -91.68) * mm});
            skLineSegment(sketch, "E1489", {"start": v(9.44, -91.68) * mm, "end": v(9.46, -91.55) * mm});
            skLineSegment(sketch, "E1490", {"start": v(9.46, -91.55) * mm, "end": v(9.49, -91.42) * mm});
            skLineSegment(sketch, "E1491", {"start": v(9.49, -91.42) * mm, "end": v(9.5, -91.3) * mm});
            skLineSegment(sketch, "E1492", {"start": v(9.5, -91.3) * mm, "end": v(9.53, -91.17) * mm});
            skLineSegment(sketch, "E1493", {"start": v(9.53, -91.17) * mm, "end": v(9.55, -91.05) * mm});
            skLineSegment(sketch, "E1494", {"start": v(9.55, -91.05) * mm, "end": v(9.56, -90.93) * mm});
            skLineSegment(sketch, "E1495", {"start": v(9.56, -90.93) * mm, "end": v(9.58, -90.81) * mm});
            skLineSegment(sketch, "E1496", {"start": v(9.58, -90.81) * mm, "end": v(9.6, -90.7) * mm});
            skLineSegment(sketch, "E1497", {"start": v(9.6, -90.7) * mm, "end": v(10, -90.45) * mm});
            skLineSegment(sketch, "E1498", {"start": v(10, -90.45) * mm, "end": v(11.68, -90.25) * mm});
            skLineSegment(sketch, "E1499", {"start": v(11.68, -90.25) * mm, "end": v(12.13, -90.4) * mm});
            skLineSegment(sketch, "E1500", {"start": v(12.13, -90.4) * mm, "end": v(12.17, -90.5) * mm});
            skLineSegment(sketch, "E1501", {"start": v(12.17, -90.5) * mm, "end": v(12.21, -90.61) * mm});
            skLineSegment(sketch, "E1502", {"start": v(12.21, -90.61) * mm, "end": v(12.26, -90.73) * mm});
            skLineSegment(sketch, "E1503", {"start": v(12.26, -90.73) * mm, "end": v(12.3, -90.84) * mm});
            skLineSegment(sketch, "E1504", {"start": v(12.3, -90.84) * mm, "end": v(12.35, -90.96) * mm});
            skLineSegment(sketch, "E1505", {"start": v(12.35, -90.96) * mm, "end": v(12.4, -91.07) * mm});
            skLineSegment(sketch, "E1506", {"start": v(12.4, -91.07) * mm, "end": v(12.46, -91.2) * mm});
            skLineSegment(sketch, "E1507", {"start": v(12.46, -91.2) * mm, "end": v(12.5, -91.32) * mm});
            skLineSegment(sketch, "E1508", {"start": v(12.5, -91.32) * mm, "end": v(12.56, -91.44) * mm});
            skLineSegment(sketch, "E1509", {"start": v(12.56, -91.44) * mm, "end": v(12.62, -91.56) * mm});
            skLineSegment(sketch, "E1510", {"start": v(12.62, -91.56) * mm, "end": v(12.68, -91.7) * mm});
            skLineSegment(sketch, "E1511", {"start": v(12.68, -91.7) * mm, "end": v(12.74, -91.82) * mm});
            skLineSegment(sketch, "E1512", {"start": v(12.74, -91.82) * mm, "end": v(12.8, -91.95) * mm});
            skLineSegment(sketch, "E1513", {"start": v(12.8, -91.95) * mm, "end": v(12.86, -92.09) * mm});
            skLineSegment(sketch, "E1514", {"start": v(12.86, -92.09) * mm, "end": v(12.93, -92.22) * mm});
            skLineSegment(sketch, "E1515", {"start": v(12.93, -92.22) * mm, "end": v(13, -92.36) * mm});
            skLineSegment(sketch, "E1516", {"start": v(13, -92.36) * mm, "end": v(13.07, -92.5) * mm});
            skLineSegment(sketch, "E1517", {"start": v(13.07, -92.5) * mm, "end": v(13.14, -92.64) * mm});
            skLineSegment(sketch, "E1518", {"start": v(13.14, -92.64) * mm, "end": v(13.21, -92.78) * mm});
            skLineSegment(sketch, "E1519", {"start": v(13.21, -92.78) * mm, "end": v(13.28, -92.93) * mm});
            skLineSegment(sketch, "E1520", {"start": v(13.28, -92.93) * mm, "end": v(13.36, -93.07) * mm});
            skLineSegment(sketch, "E1521", {"start": v(13.36, -93.07) * mm, "end": v(13.44, -93.22) * mm});
            skLineSegment(sketch, "E1522", {"start": v(13.44, -93.22) * mm, "end": v(13.52, -93.37) * mm});
            skLineSegment(sketch, "E1523", {"start": v(13.52, -93.37) * mm, "end": v(13.6, -93.53) * mm});
            skLineSegment(sketch, "E1524", {"start": v(13.6, -93.53) * mm, "end": v(13.69, -93.68) * mm});
            skLineSegment(sketch, "E1525", {"start": v(13.69, -93.68) * mm, "end": v(13.77, -93.83) * mm});
            skLineSegment(sketch, "E1526", {"start": v(13.77, -93.83) * mm, "end": v(13.86, -94) * mm});
            skLineSegment(sketch, "E1527", {"start": v(13.86, -94) * mm, "end": v(13.95, -94.15) * mm});
            skLineSegment(sketch, "E1528", {"start": v(13.95, -94.15) * mm, "end": v(14.04, -94.3) * mm});
            skLineSegment(sketch, "E1529", {"start": v(14.04, -94.3) * mm, "end": v(14.14, -94.47) * mm});
            skLineSegment(sketch, "E1530", {"start": v(14.14, -94.47) * mm, "end": v(14.24, -94.64) * mm});
            skLineSegment(sketch, "E1531", {"start": v(14.24, -94.64) * mm, "end": v(14.34, -94.8) * mm});
            skLineSegment(sketch, "E1532", {"start": v(14.34, -94.8) * mm, "end": v(14.44, -94.97) * mm});
            skLineSegment(sketch, "E1533", {"start": v(14.44, -94.97) * mm, "end": v(14.54, -95.14) * mm});
            skLineSegment(sketch, "E1534", {"start": v(14.54, -95.14) * mm, "end": v(14.65, -95.3) * mm});
            skLineSegment(sketch, "E1535", {"start": v(14.65, -95.3) * mm, "end": v(14.75, -95.48) * mm});
            skLineSegment(sketch, "E1536", {"start": v(14.75, -95.48) * mm, "end": v(14.86, -95.65) * mm});
            skLineSegment(sketch, "E1537", {"start": v(14.86, -95.65) * mm, "end": v(14.97, -95.82) * mm});
            skLineSegment(sketch, "E1538", {"start": v(14.97, -95.82) * mm, "end": v(15.08, -95.96) * mm});
            skLineSegment(sketch, "E1539", {"start": v(15.08, -95.96) * mm, "end": v(17.2, -95.6) * mm});
            skLineSegment(sketch, "E1540", {"start": v(17.2, -95.6) * mm, "end": v(17.26, -95.44) * mm});
            skLineSegment(sketch, "E1541", {"start": v(17.26, -95.44) * mm, "end": v(17.31, -95.24) * mm});
            skLineSegment(sketch, "E1542", {"start": v(17.31, -95.24) * mm, "end": v(17.36, -95.04) * mm});
            skLineSegment(sketch, "E1543", {"start": v(17.36, -95.04) * mm, "end": v(17.4, -94.84) * mm});
            skLineSegment(sketch, "E1544", {"start": v(17.4, -94.84) * mm, "end": v(17.45, -94.65) * mm});
            skLineSegment(sketch, "E1545", {"start": v(17.45, -94.65) * mm, "end": v(17.5, -94.45) * mm});
            skLineSegment(sketch, "E1546", {"start": v(17.5, -94.45) * mm, "end": v(17.53, -94.26) * mm});
            skLineSegment(sketch, "E1547", {"start": v(17.53, -94.26) * mm, "end": v(17.57, -94.07) * mm});
            skLineSegment(sketch, "E1548", {"start": v(17.57, -94.07) * mm, "end": v(17.6, -93.89) * mm});
            skLineSegment(sketch, "E1549", {"start": v(17.6, -93.89) * mm, "end": v(17.64, -93.7) * mm});
            skLineSegment(sketch, "E1550", {"start": v(17.64, -93.7) * mm, "end": v(17.68, -93.52) * mm});
            skLineSegment(sketch, "E1551", {"start": v(17.68, -93.52) * mm, "end": v(17.71, -93.34) * mm});
            skLineSegment(sketch, "E1552", {"start": v(17.71, -93.34) * mm, "end": v(17.75, -93.16) * mm});
            skLineSegment(sketch, "E1553", {"start": v(17.75, -93.16) * mm, "end": v(17.78, -92.99) * mm});
            skLineSegment(sketch, "E1554", {"start": v(17.78, -92.99) * mm, "end": v(17.8, -92.82) * mm});
            skLineSegment(sketch, "E1555", {"start": v(17.8, -92.82) * mm, "end": v(17.83, -92.65) * mm});
            skLineSegment(sketch, "E1556", {"start": v(17.83, -92.65) * mm, "end": v(17.86, -92.48) * mm});
            skLineSegment(sketch, "E1557", {"start": v(17.86, -92.48) * mm, "end": v(17.89, -92.31) * mm});
            skLineSegment(sketch, "E1558", {"start": v(17.89, -92.31) * mm, "end": v(17.91, -92.15) * mm});
            skLineSegment(sketch, "E1559", {"start": v(17.91, -92.15) * mm, "end": v(17.93, -91.99) * mm});
            skLineSegment(sketch, "E1560", {"start": v(17.93, -91.99) * mm, "end": v(17.96, -91.83) * mm});
            skLineSegment(sketch, "E1561", {"start": v(17.96, -91.83) * mm, "end": v(17.98, -91.67) * mm});
            skLineSegment(sketch, "E1562", {"start": v(17.98, -91.67) * mm, "end": v(18, -91.52) * mm});
            skLineSegment(sketch, "E1563", {"start": v(18, -91.52) * mm, "end": v(18.01, -91.37) * mm});
            skLineSegment(sketch, "E1564", {"start": v(18.01, -91.37) * mm, "end": v(18.03, -91.22) * mm});
            skLineSegment(sketch, "E1565", {"start": v(18.03, -91.22) * mm, "end": v(18.05, -91.07) * mm});
            skLineSegment(sketch, "E1566", {"start": v(18.05, -91.07) * mm, "end": v(18.06, -90.93) * mm});
            skLineSegment(sketch, "E1567", {"start": v(18.06, -90.93) * mm, "end": v(18.08, -90.78) * mm});
            skLineSegment(sketch, "E1568", {"start": v(18.08, -90.78) * mm, "end": v(18.1, -90.64) * mm});
            skLineSegment(sketch, "E1569", {"start": v(18.1, -90.64) * mm, "end": v(18.1, -90.5) * mm});
            skLineSegment(sketch, "E1570", {"start": v(18.1, -90.5) * mm, "end": v(18.11, -90.37) * mm});
            skLineSegment(sketch, "E1571", {"start": v(18.11, -90.37) * mm, "end": v(18.12, -90.24) * mm});
            skLineSegment(sketch, "E1572", {"start": v(18.12, -90.24) * mm, "end": v(18.13, -90.1) * mm});
            skLineSegment(sketch, "E1573", {"start": v(18.13, -90.1) * mm, "end": v(18.14, -89.98) * mm});
            skLineSegment(sketch, "E1574", {"start": v(18.14, -89.98) * mm, "end": v(18.15, -89.85) * mm});
            skLineSegment(sketch, "E1575", {"start": v(18.15, -89.85) * mm, "end": v(18.16, -89.73) * mm});
            skLineSegment(sketch, "E1576", {"start": v(18.16, -89.73) * mm, "end": v(18.16, -89.61) * mm});
            skLineSegment(sketch, "E1577", {"start": v(18.16, -89.61) * mm, "end": v(18.17, -89.5) * mm});
            skLineSegment(sketch, "E1578", {"start": v(18.17, -89.5) * mm, "end": v(18.17, -89.38) * mm});
            skLineSegment(sketch, "E1579", {"start": v(18.17, -89.38) * mm, "end": v(18.55, -89.09) * mm});
            skLineSegment(sketch, "E1580", {"start": v(18.55, -89.09) * mm, "end": v(20.2, -88.73) * mm});
            skLineSegment(sketch, "E1581", {"start": v(20.2, -88.73) * mm, "end": v(20.66, -88.83) * mm});
            skLineSegment(sketch, "E1582", {"start": v(20.66, -88.83) * mm, "end": v(20.72, -88.94) * mm});
            skLineSegment(sketch, "E1583", {"start": v(20.72, -88.94) * mm, "end": v(20.77, -89.04) * mm});
            skLineSegment(sketch, "E1584", {"start": v(20.77, -89.04) * mm, "end": v(20.83, -89.15) * mm});
            skLineSegment(sketch, "E1585", {"start": v(20.83, -89.15) * mm, "end": v(20.88, -89.26) * mm});
            skLineSegment(sketch, "E1586", {"start": v(20.88, -89.26) * mm, "end": v(20.94, -89.37) * mm});
            skLineSegment(sketch, "E1587", {"start": v(20.94, -89.37) * mm, "end": v(21, -89.48) * mm});
            skLineSegment(sketch, "E1588", {"start": v(21, -89.48) * mm, "end": v(21.07, -89.6) * mm});
            skLineSegment(sketch, "E1589", {"start": v(21.07, -89.6) * mm, "end": v(21.13, -89.71) * mm});
            skLineSegment(sketch, "E1590", {"start": v(21.13, -89.71) * mm, "end": v(21.2, -89.83) * mm});
            skLineSegment(sketch, "E1591", {"start": v(21.2, -89.83) * mm, "end": v(21.27, -89.95) * mm});
            skLineSegment(sketch, "E1592", {"start": v(21.27, -89.95) * mm, "end": v(21.34, -90.07) * mm});
            skLineSegment(sketch, "E1593", {"start": v(21.34, -90.07) * mm, "end": v(21.4, -90.2) * mm});
            skLineSegment(sketch, "E1594", {"start": v(21.4, -90.2) * mm, "end": v(21.48, -90.32) * mm});
            skLineSegment(sketch, "E1595", {"start": v(21.48, -90.32) * mm, "end": v(21.56, -90.45) * mm});
            skLineSegment(sketch, "E1596", {"start": v(21.56, -90.45) * mm, "end": v(21.64, -90.58) * mm});
            skLineSegment(sketch, "E1597", {"start": v(21.64, -90.58) * mm, "end": v(21.72, -90.7) * mm});
            skLineSegment(sketch, "E1598", {"start": v(21.72, -90.7) * mm, "end": v(21.8, -90.84) * mm});
            skLineSegment(sketch, "E1599", {"start": v(21.8, -90.84) * mm, "end": v(21.88, -90.97) * mm});
            skLineSegment(sketch, "E1600", {"start": v(21.88, -90.97) * mm, "end": v(21.97, -91.1) * mm});
            skLineSegment(sketch, "E1601", {"start": v(21.97, -91.1) * mm, "end": v(22.06, -91.24) * mm});
            skLineSegment(sketch, "E1602", {"start": v(22.06, -91.24) * mm, "end": v(22.15, -91.38) * mm});
            skLineSegment(sketch, "E1603", {"start": v(22.15, -91.38) * mm, "end": v(22.24, -91.52) * mm});
            skLineSegment(sketch, "E1604", {"start": v(22.24, -91.52) * mm, "end": v(22.33, -91.67) * mm});
            skLineSegment(sketch, "E1605", {"start": v(22.33, -91.67) * mm, "end": v(22.43, -91.8) * mm});
            skLineSegment(sketch, "E1606", {"start": v(22.43, -91.8) * mm, "end": v(22.53, -91.95) * mm});
            skLineSegment(sketch, "E1607", {"start": v(22.53, -91.95) * mm, "end": v(22.63, -92.1) * mm});
            skLineSegment(sketch, "E1608", {"start": v(22.63, -92.1) * mm, "end": v(22.73, -92.25) * mm});
            skLineSegment(sketch, "E1609", {"start": v(22.73, -92.25) * mm, "end": v(22.84, -92.4) * mm});
            skLineSegment(sketch, "E1610", {"start": v(22.84, -92.4) * mm, "end": v(22.95, -92.55) * mm});
            skLineSegment(sketch, "E1611", {"start": v(22.95, -92.55) * mm, "end": v(23.06, -92.7) * mm});
            skLineSegment(sketch, "E1612", {"start": v(23.06, -92.7) * mm, "end": v(23.17, -92.85) * mm});
            skLineSegment(sketch, "E1613", {"start": v(23.17, -92.85) * mm, "end": v(23.28, -93) * mm});
            skLineSegment(sketch, "E1614", {"start": v(23.28, -93) * mm, "end": v(23.4, -93.17) * mm});
            skLineSegment(sketch, "E1615", {"start": v(23.4, -93.17) * mm, "end": v(23.52, -93.32) * mm});
            skLineSegment(sketch, "E1616", {"start": v(23.52, -93.32) * mm, "end": v(23.64, -93.48) * mm});
            skLineSegment(sketch, "E1617", {"start": v(23.64, -93.48) * mm, "end": v(23.76, -93.64) * mm});
            skLineSegment(sketch, "E1618", {"start": v(23.76, -93.64) * mm, "end": v(23.89, -93.8) * mm});
            skLineSegment(sketch, "E1619", {"start": v(23.89, -93.8) * mm, "end": v(24.02, -93.97) * mm});
            skLineSegment(sketch, "E1620", {"start": v(24.02, -93.97) * mm, "end": v(24.14, -94.1) * mm});
            skLineSegment(sketch, "E1621", {"start": v(24.14, -94.1) * mm, "end": v(26.22, -93.54) * mm});
            skLineSegment(sketch, "E1622", {"start": v(26.22, -93.54) * mm, "end": v(26.26, -93.37) * mm});
            skLineSegment(sketch, "E1623", {"start": v(26.26, -93.37) * mm, "end": v(26.29, -93.16) * mm});
            skLineSegment(sketch, "E1624", {"start": v(26.29, -93.16) * mm, "end": v(26.31, -92.96) * mm});
            skLineSegment(sketch, "E1625", {"start": v(26.31, -92.96) * mm, "end": v(26.34, -92.76) * mm});
            skLineSegment(sketch, "E1626", {"start": v(26.34, -92.76) * mm, "end": v(26.37, -92.56) * mm});
            skLineSegment(sketch, "E1627", {"start": v(26.37, -92.56) * mm, "end": v(26.39, -92.36) * mm});
            skLineSegment(sketch, "E1628", {"start": v(26.39, -92.36) * mm, "end": v(26.41, -92.17) * mm});
            skLineSegment(sketch, "E1629", {"start": v(26.41, -92.17) * mm, "end": v(26.43, -91.98) * mm});
            skLineSegment(sketch, "E1630", {"start": v(26.43, -91.98) * mm, "end": v(26.45, -91.79) * mm});
            skLineSegment(sketch, "E1631", {"start": v(26.45, -91.79) * mm, "end": v(26.47, -91.6) * mm});
            skLineSegment(sketch, "E1632", {"start": v(26.47, -91.6) * mm, "end": v(26.49, -91.42) * mm});
            skLineSegment(sketch, "E1633", {"start": v(26.49, -91.42) * mm, "end": v(26.5, -91.24) * mm});
            skLineSegment(sketch, "E1634", {"start": v(26.5, -91.24) * mm, "end": v(26.52, -91.06) * mm});
            skLineSegment(sketch, "E1635", {"start": v(26.52, -91.06) * mm, "end": v(26.53, -90.88) * mm});
            skLineSegment(sketch, "E1636", {"start": v(26.53, -90.88) * mm, "end": v(26.55, -90.7) * mm});
            skLineSegment(sketch, "E1637", {"start": v(26.55, -90.7) * mm, "end": v(26.56, -90.53) * mm});
            skLineSegment(sketch, "E1638", {"start": v(26.56, -90.53) * mm, "end": v(26.57, -90.36) * mm});
            skLineSegment(sketch, "E1639", {"start": v(26.57, -90.36) * mm, "end": v(26.58, -90.2) * mm});
            skLineSegment(sketch, "E1640", {"start": v(26.58, -90.2) * mm, "end": v(26.59, -90.03) * mm});
            skLineSegment(sketch, "E1641", {"start": v(26.59, -90.03) * mm, "end": v(26.6, -89.87) * mm});
            skLineSegment(sketch, "E1642", {"start": v(26.6, -89.87) * mm, "end": v(26.6, -89.7) * mm});
            skLineSegment(sketch, "E1643", {"start": v(26.6, -89.7) * mm, "end": v(26.6, -89.55) * mm});
            skLineSegment(sketch, "E1644", {"start": v(26.6, -89.55) * mm, "end": v(26.61, -89.4) * mm});
            skLineSegment(sketch, "E1645", {"start": v(26.61, -89.4) * mm, "end": v(26.62, -89.24) * mm});
            skLineSegment(sketch, "E1646", {"start": v(26.62, -89.24) * mm, "end": v(26.62, -89.09) * mm});
            skLineSegment(sketch, "E1647", {"start": v(26.62, -89.09) * mm, "end": v(26.62, -88.94) * mm});
            skLineSegment(sketch, "E1648", {"start": v(26.62, -88.94) * mm, "end": v(26.62, -88.8) * mm});
            skLineSegment(sketch, "E1649", {"start": v(26.62, -88.8) * mm, "end": v(26.62, -88.65) * mm});
            skLineSegment(sketch, "E1650", {"start": v(26.62, -88.65) * mm, "end": v(26.62, -88.51) * mm});
            skLineSegment(sketch, "E1651", {"start": v(26.62, -88.51) * mm, "end": v(26.62, -88.37) * mm});
            skLineSegment(sketch, "E1652", {"start": v(26.62, -88.37) * mm, "end": v(26.62, -88.24) * mm});
            skLineSegment(sketch, "E1653", {"start": v(26.62, -88.24) * mm, "end": v(26.62, -88.1) * mm});
            skLineSegment(sketch, "E1654", {"start": v(26.62, -88.1) * mm, "end": v(26.62, -87.98) * mm});
            skLineSegment(sketch, "E1655", {"start": v(26.62, -87.98) * mm, "end": v(26.61, -87.85) * mm});
            skLineSegment(sketch, "E1656", {"start": v(26.61, -87.85) * mm, "end": v(26.6, -87.72) * mm});
            skLineSegment(sketch, "E1657", {"start": v(26.6, -87.72) * mm, "end": v(26.6, -87.6) * mm});
            skLineSegment(sketch, "E1658", {"start": v(26.6, -87.6) * mm, "end": v(26.6, -87.48) * mm});
            skLineSegment(sketch, "E1659", {"start": v(26.6, -87.48) * mm, "end": v(26.6, -87.36) * mm});
            skLineSegment(sketch, "E1660", {"start": v(26.6, -87.36) * mm, "end": v(26.59, -87.24) * mm});
            skLineSegment(sketch, "E1661", {"start": v(26.59, -87.24) * mm, "end": v(26.94, -86.92) * mm});
            skLineSegment(sketch, "E1662", {"start": v(26.94, -86.92) * mm, "end": v(28.54, -86.4) * mm});
            skLineSegment(sketch, "E1663", {"start": v(28.54, -86.4) * mm, "end": v(29.02, -86.47) * mm});
            skLineSegment(sketch, "E1664", {"start": v(29.02, -86.47) * mm, "end": v(29.08, -86.57) * mm});
            skLineSegment(sketch, "E1665", {"start": v(29.08, -86.57) * mm, "end": v(29.14, -86.66) * mm});
            skLineSegment(sketch, "E1666", {"start": v(29.14, -86.66) * mm, "end": v(29.2, -86.77) * mm});
            skLineSegment(sketch, "E1667", {"start": v(29.2, -86.77) * mm, "end": v(29.27, -86.87) * mm});
            skLineSegment(sketch, "E1668", {"start": v(29.27, -86.87) * mm, "end": v(29.34, -86.97) * mm});
            skLineSegment(sketch, "E1669", {"start": v(29.34, -86.97) * mm, "end": v(29.42, -87.08) * mm});
            skLineSegment(sketch, "E1670", {"start": v(29.42, -87.08) * mm, "end": v(29.49, -87.19) * mm});
            skLineSegment(sketch, "E1671", {"start": v(29.49, -87.19) * mm, "end": v(29.56, -87.3) * mm});
            skLineSegment(sketch, "E1672", {"start": v(29.56, -87.3) * mm, "end": v(29.64, -87.4) * mm});
            skLineSegment(sketch, "E1673", {"start": v(29.64, -87.4) * mm, "end": v(29.72, -87.52) * mm});
            skLineSegment(sketch, "E1674", {"start": v(29.72, -87.52) * mm, "end": v(29.8, -87.64) * mm});
            skLineSegment(sketch, "E1675", {"start": v(29.8, -87.64) * mm, "end": v(29.89, -87.75) * mm});
            skLineSegment(sketch, "E1676", {"start": v(29.89, -87.75) * mm, "end": v(29.97, -87.87) * mm});
            skLineSegment(sketch, "E1677", {"start": v(29.97, -87.87) * mm, "end": v(30.06, -87.99) * mm});
            skLineSegment(sketch, "E1678", {"start": v(30.06, -87.99) * mm, "end": v(30.15, -88.1) * mm});
            skLineSegment(sketch, "E1679", {"start": v(30.15, -88.1) * mm, "end": v(30.24, -88.23) * mm});
            skLineSegment(sketch, "E1680", {"start": v(30.24, -88.23) * mm, "end": v(30.34, -88.36) * mm});
            skLineSegment(sketch, "E1681", {"start": v(30.34, -88.36) * mm, "end": v(30.43, -88.48) * mm});
            skLineSegment(sketch, "E1682", {"start": v(30.43, -88.48) * mm, "end": v(30.53, -88.6) * mm});
            skLineSegment(sketch, "E1683", {"start": v(30.53, -88.6) * mm, "end": v(30.63, -88.73) * mm});
            skLineSegment(sketch, "E1684", {"start": v(30.63, -88.73) * mm, "end": v(30.73, -88.86) * mm});
            skLineSegment(sketch, "E1685", {"start": v(30.73, -88.86) * mm, "end": v(30.84, -89) * mm});
            skLineSegment(sketch, "E1686", {"start": v(30.84, -89) * mm, "end": v(30.95, -89.13) * mm});
            skLineSegment(sketch, "E1687", {"start": v(30.95, -89.13) * mm, "end": v(31.06, -89.26) * mm});
            skLineSegment(sketch, "E1688", {"start": v(31.06, -89.26) * mm, "end": v(31.17, -89.4) * mm});
            skLineSegment(sketch, "E1689", {"start": v(31.17, -89.4) * mm, "end": v(31.28, -89.53) * mm});
            skLineSegment(sketch, "E1690", {"start": v(31.28, -89.53) * mm, "end": v(31.4, -89.67) * mm});
            skLineSegment(sketch, "E1691", {"start": v(31.4, -89.67) * mm, "end": v(31.52, -89.8) * mm});
            skLineSegment(sketch, "E1692", {"start": v(31.52, -89.8) * mm, "end": v(31.64, -89.95) * mm});
            skLineSegment(sketch, "E1693", {"start": v(31.64, -89.95) * mm, "end": v(31.76, -90.09) * mm});
            skLineSegment(sketch, "E1694", {"start": v(31.76, -90.09) * mm, "end": v(31.89, -90.23) * mm});
            skLineSegment(sketch, "E1695", {"start": v(31.89, -90.23) * mm, "end": v(32.02, -90.37) * mm});
            skLineSegment(sketch, "E1696", {"start": v(32.02, -90.37) * mm, "end": v(32.15, -90.52) * mm});
            skLineSegment(sketch, "E1697", {"start": v(32.15, -90.52) * mm, "end": v(32.28, -90.66) * mm});
            skLineSegment(sketch, "E1698", {"start": v(32.28, -90.66) * mm, "end": v(32.42, -90.81) * mm});
            skLineSegment(sketch, "E1699", {"start": v(32.42, -90.81) * mm, "end": v(32.56, -90.96) * mm});
            skLineSegment(sketch, "E1700", {"start": v(32.56, -90.96) * mm, "end": v(32.7, -91.1) * mm});
            skLineSegment(sketch, "E1701", {"start": v(32.7, -91.1) * mm, "end": v(32.84, -91.26) * mm});
            skLineSegment(sketch, "E1702", {"start": v(32.84, -91.26) * mm, "end": v(32.97, -91.38) * mm});
            skLineSegment(sketch, "E1703", {"start": v(32.97, -91.38) * mm, "end": v(34.99, -90.62) * mm});
            skLineSegment(sketch, "E1704", {"start": v(34.99, -90.62) * mm, "end": v(35.01, -90.45) * mm});
            skLineSegment(sketch, "E1705", {"start": v(35.01, -90.45) * mm, "end": v(35.02, -90.24) * mm});
            skLineSegment(sketch, "E1706", {"start": v(35.02, -90.24) * mm, "end": v(35.03, -90.04) * mm});
            skLineSegment(sketch, "E1707", {"start": v(35.03, -90.04) * mm, "end": v(35.04, -89.83) * mm});
            skLineSegment(sketch, "E1708", {"start": v(35.04, -89.83) * mm, "end": v(35.04, -89.63) * mm});
            skLineSegment(sketch, "E1709", {"start": v(35.04, -89.63) * mm, "end": v(35.05, -89.44) * mm});
            skLineSegment(sketch, "E1710", {"start": v(35.05, -89.44) * mm, "end": v(35.05, -89.24) * mm});
            skLineSegment(sketch, "E1711", {"start": v(35.05, -89.24) * mm, "end": v(35.06, -89.05) * mm});
            skLineSegment(sketch, "E1712", {"start": v(35.06, -89.05) * mm, "end": v(35.06, -88.86) * mm});
            skLineSegment(sketch, "E1713", {"start": v(35.06, -88.86) * mm, "end": v(35.06, -88.67) * mm});
            skLineSegment(sketch, "E1714", {"start": v(35.06, -88.67) * mm, "end": v(35.06, -88.49) * mm});
            skLineSegment(sketch, "E1715", {"start": v(35.06, -88.49) * mm, "end": v(35.06, -88.3) * mm});
            skLineSegment(sketch, "E1716", {"start": v(35.06, -88.3) * mm, "end": v(35.06, -88.12) * mm});
            skLineSegment(sketch, "E1717", {"start": v(35.06, -88.12) * mm, "end": v(35.05, -87.94) * mm});
            skLineSegment(sketch, "E1718", {"start": v(35.05, -87.94) * mm, "end": v(35.05, -87.77) * mm});
            skLineSegment(sketch, "E1719", {"start": v(35.05, -87.77) * mm, "end": v(35.04, -87.6) * mm});
            skLineSegment(sketch, "E1720", {"start": v(35.04, -87.6) * mm, "end": v(35.04, -87.43) * mm});
            skLineSegment(sketch, "E1721", {"start": v(35.04, -87.43) * mm, "end": v(35.03, -87.26) * mm});
            skLineSegment(sketch, "E1722", {"start": v(35.03, -87.26) * mm, "end": v(35.03, -87.1) * mm});
            skLineSegment(sketch, "E1723", {"start": v(35.03, -87.1) * mm, "end": v(35.02, -86.93) * mm});
            skLineSegment(sketch, "E1724", {"start": v(35.02, -86.93) * mm, "end": v(35, -86.77) * mm});
            skLineSegment(sketch, "E1725", {"start": v(35, -86.77) * mm, "end": v(35, -86.61) * mm});
            skLineSegment(sketch, "E1726", {"start": v(35, -86.61) * mm, "end": v(35, -86.46) * mm});
            skLineSegment(sketch, "E1727", {"start": v(35, -86.46) * mm, "end": v(34.98, -86.3) * mm});
            skLineSegment(sketch, "E1728", {"start": v(34.98, -86.3) * mm, "end": v(34.97, -86.16) * mm});
            skLineSegment(sketch, "E1729", {"start": v(34.97, -86.16) * mm, "end": v(34.96, -86) * mm});
            skLineSegment(sketch, "E1730", {"start": v(34.96, -86) * mm, "end": v(34.94, -85.86) * mm});
            skLineSegment(sketch, "E1731", {"start": v(34.94, -85.86) * mm, "end": v(34.93, -85.72) * mm});
            skLineSegment(sketch, "E1732", {"start": v(34.93, -85.72) * mm, "end": v(34.92, -85.58) * mm});
            skLineSegment(sketch, "E1733", {"start": v(34.92, -85.58) * mm, "end": v(34.9, -85.44) * mm});
            skLineSegment(sketch, "E1734", {"start": v(34.9, -85.44) * mm, "end": v(34.89, -85.3) * mm});
            skLineSegment(sketch, "E1735", {"start": v(34.89, -85.3) * mm, "end": v(34.87, -85.18) * mm});
            skLineSegment(sketch, "E1736", {"start": v(34.87, -85.18) * mm, "end": v(34.86, -85.05) * mm});
            skLineSegment(sketch, "E1737", {"start": v(34.86, -85.05) * mm, "end": v(34.84, -84.92) * mm});
            skLineSegment(sketch, "E1738", {"start": v(34.84, -84.92) * mm, "end": v(34.83, -84.8) * mm});
            skLineSegment(sketch, "E1739", {"start": v(34.83, -84.8) * mm, "end": v(34.81, -84.67) * mm});
            skLineSegment(sketch, "E1740", {"start": v(34.81, -84.67) * mm, "end": v(34.8, -84.55) * mm});
            skLineSegment(sketch, "E1741", {"start": v(34.8, -84.55) * mm, "end": v(34.78, -84.44) * mm});
            skLineSegment(sketch, "E1742", {"start": v(34.78, -84.44) * mm, "end": v(34.76, -84.32) * mm});
            skLineSegment(sketch, "E1743", {"start": v(34.76, -84.32) * mm, "end": v(35.08, -83.97) * mm});
            skLineSegment(sketch, "E1744", {"start": v(35.08, -83.97) * mm, "end": v(36.63, -83.3) * mm});
            skLineSegment(sketch, "E1745", {"start": v(36.63, -83.3) * mm, "end": v(37.1, -83.32) * mm});
            skLineSegment(sketch, "E1746", {"start": v(37.1, -83.32) * mm, "end": v(37.17, -83.4) * mm});
            skLineSegment(sketch, "E1747", {"start": v(37.17, -83.4) * mm, "end": v(37.25, -83.5) * mm});
            skLineSegment(sketch, "E1748", {"start": v(37.25, -83.5) * mm, "end": v(37.32, -83.6) * mm});
            skLineSegment(sketch, "E1749", {"start": v(37.32, -83.6) * mm, "end": v(37.4, -83.7) * mm});
            skLineSegment(sketch, "E1750", {"start": v(37.4, -83.7) * mm, "end": v(37.48, -83.8) * mm});
            skLineSegment(sketch, "E1751", {"start": v(37.48, -83.8) * mm, "end": v(37.56, -83.89) * mm});
            skLineSegment(sketch, "E1752", {"start": v(37.56, -83.89) * mm, "end": v(37.64, -83.99) * mm});
            skLineSegment(sketch, "E1753", {"start": v(37.64, -83.99) * mm, "end": v(37.73, -84.1) * mm});
            skLineSegment(sketch, "E1754", {"start": v(37.73, -84.1) * mm, "end": v(37.82, -84.2) * mm});
            skLineSegment(sketch, "E1755", {"start": v(37.82, -84.2) * mm, "end": v(37.9, -84.3) * mm});
            skLineSegment(sketch, "E1756", {"start": v(37.9, -84.3) * mm, "end": v(38, -84.4) * mm});
            skLineSegment(sketch, "E1757", {"start": v(38, -84.4) * mm, "end": v(38.1, -84.51) * mm});
            skLineSegment(sketch, "E1758", {"start": v(38.1, -84.51) * mm, "end": v(38.19, -84.62) * mm});
            skLineSegment(sketch, "E1759", {"start": v(38.19, -84.62) * mm, "end": v(38.29, -84.73) * mm});
            skLineSegment(sketch, "E1760", {"start": v(38.29, -84.73) * mm, "end": v(38.39, -84.84) * mm});
            skLineSegment(sketch, "E1761", {"start": v(38.39, -84.84) * mm, "end": v(38.5, -84.96) * mm});
            skLineSegment(sketch, "E1762", {"start": v(38.5, -84.96) * mm, "end": v(38.6, -85.07) * mm});
            skLineSegment(sketch, "E1763", {"start": v(38.6, -85.07) * mm, "end": v(38.7, -85.19) * mm});
            skLineSegment(sketch, "E1764", {"start": v(38.7, -85.19) * mm, "end": v(38.82, -85.3) * mm});
            skLineSegment(sketch, "E1765", {"start": v(38.82, -85.3) * mm, "end": v(38.93, -85.42) * mm});
            skLineSegment(sketch, "E1766", {"start": v(38.93, -85.42) * mm, "end": v(39.04, -85.54) * mm});
            skLineSegment(sketch, "E1767", {"start": v(39.04, -85.54) * mm, "end": v(39.16, -85.66) * mm});
            skLineSegment(sketch, "E1768", {"start": v(39.16, -85.66) * mm, "end": v(39.28, -85.78) * mm});
            skLineSegment(sketch, "E1769", {"start": v(39.28, -85.78) * mm, "end": v(39.4, -85.9) * mm});
            skLineSegment(sketch, "E1770", {"start": v(39.4, -85.9) * mm, "end": v(39.52, -86.03) * mm});
            skLineSegment(sketch, "E1771", {"start": v(39.52, -86.03) * mm, "end": v(39.65, -86.15) * mm});
            skLineSegment(sketch, "E1772", {"start": v(39.65, -86.15) * mm, "end": v(39.78, -86.28) * mm});
            skLineSegment(sketch, "E1773", {"start": v(39.78, -86.28) * mm, "end": v(39.91, -86.4) * mm});
            skLineSegment(sketch, "E1774", {"start": v(39.91, -86.4) * mm, "end": v(40.05, -86.53) * mm});
            skLineSegment(sketch, "E1775", {"start": v(40.05, -86.53) * mm, "end": v(40.18, -86.66) * mm});
            skLineSegment(sketch, "E1776", {"start": v(40.18, -86.66) * mm, "end": v(40.32, -86.8) * mm});
            skLineSegment(sketch, "E1777", {"start": v(40.32, -86.8) * mm, "end": v(40.46, -86.92) * mm});
            skLineSegment(sketch, "E1778", {"start": v(40.46, -86.92) * mm, "end": v(40.6, -87.05) * mm});
            skLineSegment(sketch, "E1779", {"start": v(40.6, -87.05) * mm, "end": v(40.75, -87.19) * mm});
            skLineSegment(sketch, "E1780", {"start": v(40.75, -87.19) * mm, "end": v(40.9, -87.32) * mm});
            skLineSegment(sketch, "E1781", {"start": v(40.9, -87.32) * mm, "end": v(41.05, -87.45) * mm});
            skLineSegment(sketch, "E1782", {"start": v(41.05, -87.45) * mm, "end": v(41.2, -87.59) * mm});
            skLineSegment(sketch, "E1783", {"start": v(41.2, -87.59) * mm, "end": v(41.37, -87.72) * mm});
            skLineSegment(sketch, "E1784", {"start": v(41.37, -87.72) * mm, "end": v(41.5, -87.83) * mm});
            skLineSegment(sketch, "E1785", {"start": v(41.5, -87.83) * mm, "end": v(43.44, -86.89) * mm});
            skLineSegment(sketch, "E1786", {"start": v(43.44, -86.89) * mm, "end": v(43.45, -86.7) * mm});
            skLineSegment(sketch, "E1787", {"start": v(43.45, -86.7) * mm, "end": v(43.44, -86.5) * mm});
            skLineSegment(sketch, "E1788", {"start": v(43.44, -86.5) * mm, "end": v(43.43, -86.3) * mm});
            skLineSegment(sketch, "E1789", {"start": v(43.43, -86.3) * mm, "end": v(43.42, -86.1) * mm});
            skLineSegment(sketch, "E1790", {"start": v(43.42, -86.1) * mm, "end": v(43.4, -85.9) * mm});
            skLineSegment(sketch, "E1791", {"start": v(43.4, -85.9) * mm, "end": v(43.4, -85.7) * mm});
            skLineSegment(sketch, "E1792", {"start": v(43.4, -85.7) * mm, "end": v(43.38, -85.5) * mm});
            skLineSegment(sketch, "E1793", {"start": v(43.38, -85.5) * mm, "end": v(43.36, -85.31) * mm});
            skLineSegment(sketch, "E1794", {"start": v(43.36, -85.31) * mm, "end": v(43.35, -85.12) * mm});
            skLineSegment(sketch, "E1795", {"start": v(43.35, -85.12) * mm, "end": v(43.33, -84.94) * mm});
            skLineSegment(sketch, "E1796", {"start": v(43.33, -84.94) * mm, "end": v(43.31, -84.75) * mm});
            skLineSegment(sketch, "E1797", {"start": v(43.31, -84.75) * mm, "end": v(43.3, -84.57) * mm});
            skLineSegment(sketch, "E1798", {"start": v(43.3, -84.57) * mm, "end": v(43.27, -84.4) * mm});
            skLineSegment(sketch, "E1799", {"start": v(43.27, -84.4) * mm, "end": v(43.25, -84.21) * mm});
            skLineSegment(sketch, "E1800", {"start": v(43.25, -84.21) * mm, "end": v(43.23, -84.04) * mm});
            skLineSegment(sketch, "E1801", {"start": v(43.23, -84.04) * mm, "end": v(43.21, -83.87) * mm});
            skLineSegment(sketch, "E1802", {"start": v(43.21, -83.87) * mm, "end": v(43.2, -83.7) * mm});
            skLineSegment(sketch, "E1803", {"start": v(43.2, -83.7) * mm, "end": v(43.17, -83.53) * mm});
            skLineSegment(sketch, "E1804", {"start": v(43.17, -83.53) * mm, "end": v(43.15, -83.37) * mm});
            skLineSegment(sketch, "E1805", {"start": v(43.15, -83.37) * mm, "end": v(43.12, -83.2) * mm});
            skLineSegment(sketch, "E1806", {"start": v(43.12, -83.2) * mm, "end": v(43.1, -83.05) * mm});
            skLineSegment(sketch, "E1807", {"start": v(43.1, -83.05) * mm, "end": v(43.07, -82.9) * mm});
            skLineSegment(sketch, "E1808", {"start": v(43.07, -82.9) * mm, "end": v(43.05, -82.74) * mm});
            skLineSegment(sketch, "E1809", {"start": v(43.05, -82.74) * mm, "end": v(43.03, -82.6) * mm});
            skLineSegment(sketch, "E1810", {"start": v(43.03, -82.6) * mm, "end": v(43, -82.44) * mm});
            skLineSegment(sketch, "E1811", {"start": v(43, -82.44) * mm, "end": v(42.97, -82.3) * mm});
            skLineSegment(sketch, "E1812", {"start": v(42.97, -82.3) * mm, "end": v(42.95, -82.15) * mm});
            skLineSegment(sketch, "E1813", {"start": v(42.95, -82.15) * mm, "end": v(42.92, -82.01) * mm});
            skLineSegment(sketch, "E1814", {"start": v(42.92, -82.01) * mm, "end": v(42.9, -81.87) * mm});
            skLineSegment(sketch, "E1815", {"start": v(42.9, -81.87) * mm, "end": v(42.87, -81.74) * mm});
            skLineSegment(sketch, "E1816", {"start": v(42.87, -81.74) * mm, "end": v(42.84, -81.6) * mm});
            skLineSegment(sketch, "E1817", {"start": v(42.84, -81.6) * mm, "end": v(42.81, -81.48) * mm});
            skLineSegment(sketch, "E1818", {"start": v(42.81, -81.48) * mm, "end": v(42.79, -81.35) * mm});
            skLineSegment(sketch, "E1819", {"start": v(42.79, -81.35) * mm, "end": v(42.76, -81.22) * mm});
            skLineSegment(sketch, "E1820", {"start": v(42.76, -81.22) * mm, "end": v(42.73, -81.1) * mm});
            skLineSegment(sketch, "E1821", {"start": v(42.73, -81.1) * mm, "end": v(42.7, -80.98) * mm});
            skLineSegment(sketch, "E1822", {"start": v(42.7, -80.98) * mm, "end": v(42.67, -80.86) * mm});
            skLineSegment(sketch, "E1823", {"start": v(42.67, -80.86) * mm, "end": v(42.65, -80.75) * mm});
            skLineSegment(sketch, "E1824", {"start": v(42.65, -80.75) * mm, "end": v(42.62, -80.64) * mm});
            skLineSegment(sketch, "E1825", {"start": v(42.62, -80.64) * mm, "end": v(42.9, -80.25) * mm});
            skLineSegment(sketch, "E1826", {"start": v(42.9, -80.25) * mm, "end": v(44.38, -79.44) * mm});
            skLineSegment(sketch, "E1827", {"start": v(44.38, -79.44) * mm, "end": v(44.85, -79.41) * mm});
            skLineSegment(sketch, "E1828", {"start": v(44.85, -79.41) * mm, "end": v(44.93, -79.5) * mm});
            skLineSegment(sketch, "E1829", {"start": v(44.93, -79.5) * mm, "end": v(45.02, -79.58) * mm});
            skLineSegment(sketch, "E1830", {"start": v(45.02, -79.58) * mm, "end": v(45.1, -79.67) * mm});
            skLineSegment(sketch, "E1831", {"start": v(45.1, -79.67) * mm, "end": v(45.19, -79.76) * mm});
            skLineSegment(sketch, "E1832", {"start": v(45.19, -79.76) * mm, "end": v(45.27, -79.85) * mm});
            skLineSegment(sketch, "E1833", {"start": v(45.27, -79.85) * mm, "end": v(45.36, -79.94) * mm});
            skLineSegment(sketch, "E1834", {"start": v(45.36, -79.94) * mm, "end": v(45.46, -80.03) * mm});
            skLineSegment(sketch, "E1835", {"start": v(45.46, -80.03) * mm, "end": v(45.55, -80.12) * mm});
            skLineSegment(sketch, "E1836", {"start": v(45.55, -80.12) * mm, "end": v(45.65, -80.22) * mm});
            skLineSegment(sketch, "E1837", {"start": v(45.65, -80.22) * mm, "end": v(45.75, -80.32) * mm});
            skLineSegment(sketch, "E1838", {"start": v(45.75, -80.32) * mm, "end": v(45.85, -80.41) * mm});
            skLineSegment(sketch, "E1839", {"start": v(45.85, -80.41) * mm, "end": v(45.95, -80.51) * mm});
            skLineSegment(sketch, "E1840", {"start": v(45.95, -80.51) * mm, "end": v(46.06, -80.6) * mm});
            skLineSegment(sketch, "E1841", {"start": v(46.06, -80.6) * mm, "end": v(46.17, -80.7) * mm});
            skLineSegment(sketch, "E1842", {"start": v(46.17, -80.7) * mm, "end": v(46.28, -80.81) * mm});
            skLineSegment(sketch, "E1843", {"start": v(46.28, -80.81) * mm, "end": v(46.4, -80.91) * mm});
            skLineSegment(sketch, "E1844", {"start": v(46.4, -80.91) * mm, "end": v(46.5, -81.02) * mm});
            skLineSegment(sketch, "E1845", {"start": v(46.5, -81.02) * mm, "end": v(46.63, -81.12) * mm});
            skLineSegment(sketch, "E1846", {"start": v(46.63, -81.12) * mm, "end": v(46.75, -81.23) * mm});
            skLineSegment(sketch, "E1847", {"start": v(46.75, -81.23) * mm, "end": v(46.87, -81.33) * mm});
            skLineSegment(sketch, "E1848", {"start": v(46.87, -81.33) * mm, "end": v(47, -81.44) * mm});
            skLineSegment(sketch, "E1849", {"start": v(47, -81.44) * mm, "end": v(47.12, -81.55) * mm});
            skLineSegment(sketch, "E1850", {"start": v(47.12, -81.55) * mm, "end": v(47.26, -81.66) * mm});
            skLineSegment(sketch, "E1851", {"start": v(47.26, -81.66) * mm, "end": v(47.39, -81.77) * mm});
            skLineSegment(sketch, "E1852", {"start": v(47.39, -81.77) * mm, "end": v(47.52, -81.88) * mm});
            skLineSegment(sketch, "E1853", {"start": v(47.52, -81.88) * mm, "end": v(47.66, -82) * mm});
            skLineSegment(sketch, "E1854", {"start": v(47.66, -82) * mm, "end": v(47.8, -82.1) * mm});
            skLineSegment(sketch, "E1855", {"start": v(47.8, -82.1) * mm, "end": v(47.94, -82.22) * mm});
            skLineSegment(sketch, "E1856", {"start": v(47.94, -82.22) * mm, "end": v(48.1, -82.33) * mm});
            skLineSegment(sketch, "E1857", {"start": v(48.1, -82.33) * mm, "end": v(48.24, -82.45) * mm});
            skLineSegment(sketch, "E1858", {"start": v(48.24, -82.45) * mm, "end": v(48.39, -82.57) * mm});
            skLineSegment(sketch, "E1859", {"start": v(48.39, -82.57) * mm, "end": v(48.54, -82.68) * mm});
            skLineSegment(sketch, "E1860", {"start": v(48.54, -82.68) * mm, "end": v(48.7, -82.8) * mm});
            skLineSegment(sketch, "E1861", {"start": v(48.7, -82.8) * mm, "end": v(48.86, -82.92) * mm});
            skLineSegment(sketch, "E1862", {"start": v(48.86, -82.92) * mm, "end": v(49.02, -83.04) * mm});
            skLineSegment(sketch, "E1863", {"start": v(49.02, -83.04) * mm, "end": v(49.18, -83.15) * mm});
            skLineSegment(sketch, "E1864", {"start": v(49.18, -83.15) * mm, "end": v(49.35, -83.27) * mm});
            skLineSegment(sketch, "E1865", {"start": v(49.35, -83.27) * mm, "end": v(49.52, -83.4) * mm});
            skLineSegment(sketch, "E1866", {"start": v(49.52, -83.4) * mm, "end": v(49.67, -83.48) * mm});
            skLineSegment(sketch, "E1867", {"start": v(49.67, -83.48) * mm, "end": v(51.5, -82.36) * mm});
            skLineSegment(sketch, "E1868", {"start": v(51.5, -82.36) * mm, "end": v(51.5, -82.19) * mm});
            skLineSegment(sketch, "E1869", {"start": v(51.5, -82.19) * mm, "end": v(51.47, -81.98) * mm});
            skLineSegment(sketch, "E1870", {"start": v(51.47, -81.98) * mm, "end": v(51.44, -81.78) * mm});
            skLineSegment(sketch, "E1871", {"start": v(51.44, -81.78) * mm, "end": v(51.4, -81.58) * mm});
            skLineSegment(sketch, "E1872", {"start": v(51.4, -81.58) * mm, "end": v(51.37, -81.38) * mm});
            skLineSegment(sketch, "E1873", {"start": v(51.37, -81.38) * mm, "end": v(51.34, -81.19) * mm});
            skLineSegment(sketch, "E1874", {"start": v(51.34, -81.19) * mm, "end": v(51.3, -81) * mm});
            skLineSegment(sketch, "E1875", {"start": v(51.3, -81) * mm, "end": v(51.28, -80.8) * mm});
            skLineSegment(sketch, "E1876", {"start": v(51.28, -80.8) * mm, "end": v(51.24, -80.62) * mm});
            skLineSegment(sketch, "E1877", {"start": v(51.24, -80.62) * mm, "end": v(51.2, -80.43) * mm});
            skLineSegment(sketch, "E1878", {"start": v(51.2, -80.43) * mm, "end": v(51.17, -80.25) * mm});
            skLineSegment(sketch, "E1879", {"start": v(51.17, -80.25) * mm, "end": v(51.14, -80.07) * mm});
            skLineSegment(sketch, "E1880", {"start": v(51.14, -80.07) * mm, "end": v(51.1, -79.9) * mm});
            skLineSegment(sketch, "E1881", {"start": v(51.1, -79.9) * mm, "end": v(51.06, -79.72) * mm});
            skLineSegment(sketch, "E1882", {"start": v(51.06, -79.72) * mm, "end": v(51.03, -79.55) * mm});
            skLineSegment(sketch, "E1883", {"start": v(51.03, -79.55) * mm, "end": v(50.99, -79.38) * mm});
            skLineSegment(sketch, "E1884", {"start": v(50.99, -79.38) * mm, "end": v(50.95, -79.22) * mm});
            skLineSegment(sketch, "E1885", {"start": v(50.95, -79.22) * mm, "end": v(50.91, -79.05) * mm});
            skLineSegment(sketch, "E1886", {"start": v(50.91, -79.05) * mm, "end": v(50.88, -78.9) * mm});
            skLineSegment(sketch, "E1887", {"start": v(50.88, -78.9) * mm, "end": v(50.84, -78.73) * mm});
            skLineSegment(sketch, "E1888", {"start": v(50.84, -78.73) * mm, "end": v(50.8, -78.58) * mm});
            skLineSegment(sketch, "E1889", {"start": v(50.8, -78.58) * mm, "end": v(50.76, -78.42) * mm});
            skLineSegment(sketch, "E1890", {"start": v(50.76, -78.42) * mm, "end": v(50.72, -78.27) * mm});
            skLineSegment(sketch, "E1891", {"start": v(50.72, -78.27) * mm, "end": v(50.68, -78.13) * mm});
            skLineSegment(sketch, "E1892", {"start": v(50.68, -78.13) * mm, "end": v(50.64, -77.98) * mm});
            skLineSegment(sketch, "E1893", {"start": v(50.64, -77.98) * mm, "end": v(50.6, -77.84) * mm});
            skLineSegment(sketch, "E1894", {"start": v(50.6, -77.84) * mm, "end": v(50.56, -77.7) * mm});
            skLineSegment(sketch, "E1895", {"start": v(50.56, -77.7) * mm, "end": v(50.52, -77.56) * mm});
            skLineSegment(sketch, "E1896", {"start": v(50.52, -77.56) * mm, "end": v(50.48, -77.43) * mm});
            skLineSegment(sketch, "E1897", {"start": v(50.48, -77.43) * mm, "end": v(50.44, -77.3) * mm});
            skLineSegment(sketch, "E1898", {"start": v(50.44, -77.3) * mm, "end": v(50.4, -77.16) * mm});
            skLineSegment(sketch, "E1899", {"start": v(50.4, -77.16) * mm, "end": v(50.36, -77.04) * mm});
            skLineSegment(sketch, "E1900", {"start": v(50.36, -77.04) * mm, "end": v(50.32, -76.91) * mm});
            skLineSegment(sketch, "E1901", {"start": v(50.32, -76.91) * mm, "end": v(50.29, -76.8) * mm});
            skLineSegment(sketch, "E1902", {"start": v(50.29, -76.8) * mm, "end": v(50.25, -76.67) * mm});
            skLineSegment(sketch, "E1903", {"start": v(50.25, -76.67) * mm, "end": v(50.2, -76.56) * mm});
            skLineSegment(sketch, "E1904", {"start": v(50.2, -76.56) * mm, "end": v(50.17, -76.44) * mm});
            skLineSegment(sketch, "E1905", {"start": v(50.17, -76.44) * mm, "end": v(50.13, -76.33) * mm});
            skLineSegment(sketch, "E1906", {"start": v(50.13, -76.33) * mm, "end": v(50.1, -76.22) * mm});
            skLineSegment(sketch, "E1907", {"start": v(50.1, -76.22) * mm, "end": v(50.33, -75.81) * mm});
            skLineSegment(sketch, "E1908", {"start": v(50.33, -75.81) * mm, "end": v(51.73, -74.87) * mm});
            skLineSegment(sketch, "E1909", {"start": v(51.73, -74.87) * mm, "end": v(52.2, -74.8) * mm});
            skLineSegment(sketch, "E1910", {"start": v(52.2, -74.8) * mm, "end": v(52.29, -74.87) * mm});
            skLineSegment(sketch, "E1911", {"start": v(52.29, -74.87) * mm, "end": v(52.38, -74.94) * mm});
            skLineSegment(sketch, "E1912", {"start": v(52.38, -74.94) * mm, "end": v(52.47, -75.02) * mm});
            skLineSegment(sketch, "E1913", {"start": v(52.47, -75.02) * mm, "end": v(52.56, -75.1) * mm});
            skLineSegment(sketch, "E1914", {"start": v(52.56, -75.1) * mm, "end": v(52.66, -75.18) * mm});
            skLineSegment(sketch, "E1915", {"start": v(52.66, -75.18) * mm, "end": v(52.76, -75.27) * mm});
            skLineSegment(sketch, "E1916", {"start": v(52.76, -75.27) * mm, "end": v(52.86, -75.35) * mm});
            skLineSegment(sketch, "E1917", {"start": v(52.86, -75.35) * mm, "end": v(52.96, -75.43) * mm});
            skLineSegment(sketch, "E1918", {"start": v(52.96, -75.43) * mm, "end": v(53.07, -75.52) * mm});
            skLineSegment(sketch, "E1919", {"start": v(53.07, -75.52) * mm, "end": v(53.18, -75.6) * mm});
            skLineSegment(sketch, "E1920", {"start": v(53.18, -75.6) * mm, "end": v(53.29, -75.69) * mm});
            skLineSegment(sketch, "E1921", {"start": v(53.29, -75.69) * mm, "end": v(53.4, -75.78) * mm});
            skLineSegment(sketch, "E1922", {"start": v(53.4, -75.78) * mm, "end": v(53.51, -75.87) * mm});
            skLineSegment(sketch, "E1923", {"start": v(53.51, -75.87) * mm, "end": v(53.63, -75.96) * mm});
            skLineSegment(sketch, "E1924", {"start": v(53.63, -75.96) * mm, "end": v(53.75, -76.05) * mm});
            skLineSegment(sketch, "E1925", {"start": v(53.75, -76.05) * mm, "end": v(53.87, -76.14) * mm});
            skLineSegment(sketch, "E1926", {"start": v(53.87, -76.14) * mm, "end": v(54, -76.23) * mm});
            skLineSegment(sketch, "E1927", {"start": v(54, -76.23) * mm, "end": v(54.13, -76.32) * mm});
            skLineSegment(sketch, "E1928", {"start": v(54.13, -76.32) * mm, "end": v(54.26, -76.42) * mm});
            skLineSegment(sketch, "E1929", {"start": v(54.26, -76.42) * mm, "end": v(54.4, -76.51) * mm});
            skLineSegment(sketch, "E1930", {"start": v(54.4, -76.51) * mm, "end": v(54.53, -76.6) * mm});
            skLineSegment(sketch, "E1931", {"start": v(54.53, -76.6) * mm, "end": v(54.66, -76.7) * mm});
            skLineSegment(sketch, "E1932", {"start": v(54.66, -76.7) * mm, "end": v(54.8, -76.8) * mm});
            skLineSegment(sketch, "E1933", {"start": v(54.8, -76.8) * mm, "end": v(54.95, -76.9) * mm});
            skLineSegment(sketch, "E1934", {"start": v(54.95, -76.9) * mm, "end": v(55.1, -77) * mm});
            skLineSegment(sketch, "E1935", {"start": v(55.1, -77) * mm, "end": v(55.24, -77.1) * mm});
            skLineSegment(sketch, "E1936", {"start": v(55.24, -77.1) * mm, "end": v(55.4, -77.2) * mm});
            skLineSegment(sketch, "E1937", {"start": v(55.4, -77.2) * mm, "end": v(55.54, -77.3) * mm});
            skLineSegment(sketch, "E1938", {"start": v(55.54, -77.3) * mm, "end": v(55.7, -77.4) * mm});
            skLineSegment(sketch, "E1939", {"start": v(55.7, -77.4) * mm, "end": v(55.86, -77.5) * mm});
            skLineSegment(sketch, "E1940", {"start": v(55.86, -77.5) * mm, "end": v(56.02, -77.6) * mm});
            skLineSegment(sketch, "E1941", {"start": v(56.02, -77.6) * mm, "end": v(56.18, -77.7) * mm});
            skLineSegment(sketch, "E1942", {"start": v(56.18, -77.7) * mm, "end": v(56.35, -77.8) * mm});
            skLineSegment(sketch, "E1943", {"start": v(56.35, -77.8) * mm, "end": v(56.52, -77.9) * mm});
            skLineSegment(sketch, "E1944", {"start": v(56.52, -77.9) * mm, "end": v(56.69, -78) * mm});
            skLineSegment(sketch, "E1945", {"start": v(56.69, -78) * mm, "end": v(56.86, -78.1) * mm});
            skLineSegment(sketch, "E1946", {"start": v(56.86, -78.1) * mm, "end": v(57.04, -78.2) * mm});
            skLineSegment(sketch, "E1947", {"start": v(57.04, -78.2) * mm, "end": v(57.22, -78.31) * mm});
            skLineSegment(sketch, "E1948", {"start": v(57.22, -78.31) * mm, "end": v(57.38, -78.38) * mm});
            skLineSegment(sketch, "E1949", {"start": v(57.38, -78.38) * mm, "end": v(59.1, -77.1) * mm});
            skLineSegment(sketch, "E1950", {"start": v(59.1, -77.1) * mm, "end": v(59.08, -76.92) * mm});
            skLineSegment(sketch, "E1951", {"start": v(59.08, -76.92) * mm, "end": v(59.03, -76.72) * mm});
            skLineSegment(sketch, "E1952", {"start": v(59.03, -76.72) * mm, "end": v(58.98, -76.52) * mm});
            skLineSegment(sketch, "E1953", {"start": v(58.98, -76.52) * mm, "end": v(58.93, -76.32) * mm});
            skLineSegment(sketch, "E1954", {"start": v(58.93, -76.32) * mm, "end": v(58.88, -76.13) * mm});
            skLineSegment(sketch, "E1955", {"start": v(58.88, -76.13) * mm, "end": v(58.83, -75.94) * mm});
            skLineSegment(sketch, "E1956", {"start": v(58.83, -75.94) * mm, "end": v(58.78, -75.75) * mm});
            skLineSegment(sketch, "E1957", {"start": v(58.78, -75.75) * mm, "end": v(58.72, -75.56) * mm});
            skLineSegment(sketch, "E1958", {"start": v(58.72, -75.56) * mm, "end": v(58.67, -75.38) * mm});
            skLineSegment(sketch, "E1959", {"start": v(58.67, -75.38) * mm, "end": v(58.62, -75.2) * mm});
            skLineSegment(sketch, "E1960", {"start": v(58.62, -75.2) * mm, "end": v(58.57, -75.02) * mm});
            skLineSegment(sketch, "E1961", {"start": v(58.57, -75.02) * mm, "end": v(58.52, -74.85) * mm});
            skLineSegment(sketch, "E1962", {"start": v(58.52, -74.85) * mm, "end": v(58.46, -74.68) * mm});
            skLineSegment(sketch, "E1963", {"start": v(58.46, -74.68) * mm, "end": v(58.41, -74.5) * mm});
            skLineSegment(sketch, "E1964", {"start": v(58.41, -74.5) * mm, "end": v(58.36, -74.34) * mm});
            skLineSegment(sketch, "E1965", {"start": v(58.36, -74.34) * mm, "end": v(58.3, -74.18) * mm});
            skLineSegment(sketch, "E1966", {"start": v(58.3, -74.18) * mm, "end": v(58.25, -74.01) * mm});
            skLineSegment(sketch, "E1967", {"start": v(58.25, -74.01) * mm, "end": v(58.2, -73.85) * mm});
            skLineSegment(sketch, "E1968", {"start": v(58.2, -73.85) * mm, "end": v(58.14, -73.7) * mm});
            skLineSegment(sketch, "E1969", {"start": v(58.14, -73.7) * mm, "end": v(58.1, -73.54) * mm});
            skLineSegment(sketch, "E1970", {"start": v(58.1, -73.54) * mm, "end": v(58.04, -73.4) * mm});
            skLineSegment(sketch, "E1971", {"start": v(58.04, -73.4) * mm, "end": v(57.98, -73.24) * mm});
            skLineSegment(sketch, "E1972", {"start": v(57.98, -73.24) * mm, "end": v(57.93, -73.1) * mm});
            skLineSegment(sketch, "E1973", {"start": v(57.93, -73.1) * mm, "end": v(57.88, -72.96) * mm});
            skLineSegment(sketch, "E1974", {"start": v(57.88, -72.96) * mm, "end": v(57.82, -72.81) * mm});
            skLineSegment(sketch, "E1975", {"start": v(57.82, -72.81) * mm, "end": v(57.77, -72.68) * mm});
            skLineSegment(sketch, "E1976", {"start": v(57.77, -72.68) * mm, "end": v(57.72, -72.54) * mm});
            skLineSegment(sketch, "E1977", {"start": v(57.72, -72.54) * mm, "end": v(57.67, -72.4) * mm});
            skLineSegment(sketch, "E1978", {"start": v(57.67, -72.4) * mm, "end": v(57.61, -72.28) * mm});
            skLineSegment(sketch, "E1979", {"start": v(57.61, -72.28) * mm, "end": v(57.56, -72.15) * mm});
            skLineSegment(sketch, "E1980", {"start": v(57.56, -72.15) * mm, "end": v(57.51, -72.02) * mm});
            skLineSegment(sketch, "E1981", {"start": v(57.51, -72.02) * mm, "end": v(57.46, -71.9) * mm});
            skLineSegment(sketch, "E1982", {"start": v(57.46, -71.9) * mm, "end": v(57.4, -71.78) * mm});
            skLineSegment(sketch, "E1983", {"start": v(57.4, -71.78) * mm, "end": v(57.36, -71.66) * mm});
            skLineSegment(sketch, "E1984", {"start": v(57.36, -71.66) * mm, "end": v(57.3, -71.55) * mm});
            skLineSegment(sketch, "E1985", {"start": v(57.3, -71.55) * mm, "end": v(57.26, -71.44) * mm});
            skLineSegment(sketch, "E1986", {"start": v(57.26, -71.44) * mm, "end": v(57.2, -71.33) * mm});
            skLineSegment(sketch, "E1987", {"start": v(57.2, -71.33) * mm, "end": v(57.16, -71.22) * mm});
            skLineSegment(sketch, "E1988", {"start": v(57.16, -71.22) * mm, "end": v(57.1, -71.11) * mm});
            skLineSegment(sketch, "E1989", {"start": v(57.1, -71.11) * mm, "end": v(57.31, -70.68) * mm});
            skLineSegment(sketch, "E1990", {"start": v(57.31, -70.68) * mm, "end": v(58.61, -69.6) * mm});
            skLineSegment(sketch, "E1991", {"start": v(58.61, -69.6) * mm, "end": v(59.07, -69.5) * mm});
            skLineSegment(sketch, "E1992", {"start": v(59.07, -69.5) * mm, "end": v(59.17, -69.56) * mm});
            skLineSegment(sketch, "E1993", {"start": v(59.17, -69.56) * mm, "end": v(59.26, -69.63) * mm});
            skLineSegment(sketch, "E1994", {"start": v(59.26, -69.63) * mm, "end": v(59.36, -69.7) * mm});
            skLineSegment(sketch, "E1995", {"start": v(59.36, -69.7) * mm, "end": v(59.46, -69.77) * mm});
            skLineSegment(sketch, "E1996", {"start": v(59.46, -69.77) * mm, "end": v(59.57, -69.84) * mm});
            skLineSegment(sketch, "E1997", {"start": v(59.57, -69.84) * mm, "end": v(59.67, -69.9) * mm});
            skLineSegment(sketch, "E1998", {"start": v(59.67, -69.9) * mm, "end": v(59.78, -69.98) * mm});
            skLineSegment(sketch, "E1999", {"start": v(59.78, -69.98) * mm, "end": v(59.9, -70.06) * mm});
            skLineSegment(sketch, "E2000", {"start": v(59.9, -70.06) * mm, "end": v(60, -70.13) * mm});
            skLineSegment(sketch, "E2001", {"start": v(60, -70.13) * mm, "end": v(60.12, -70.2) * mm});
            skLineSegment(sketch, "E2002", {"start": v(60.12, -70.2) * mm, "end": v(60.24, -70.28) * mm});
            skLineSegment(sketch, "E2003", {"start": v(60.24, -70.28) * mm, "end": v(60.36, -70.36) * mm});
            skLineSegment(sketch, "E2004", {"start": v(60.36, -70.36) * mm, "end": v(60.48, -70.44) * mm});
            skLineSegment(sketch, "E2005", {"start": v(60.48, -70.44) * mm, "end": v(60.6, -70.51) * mm});
            skLineSegment(sketch, "E2006", {"start": v(60.6, -70.51) * mm, "end": v(60.74, -70.6) * mm});
            skLineSegment(sketch, "E2007", {"start": v(60.74, -70.6) * mm, "end": v(60.87, -70.67) * mm});
            skLineSegment(sketch, "E2008", {"start": v(60.87, -70.67) * mm, "end": v(61, -70.75) * mm});
            skLineSegment(sketch, "E2009", {"start": v(61, -70.75) * mm, "end": v(61.14, -70.83) * mm});
            skLineSegment(sketch, "E2010", {"start": v(61.14, -70.83) * mm, "end": v(61.28, -70.91) * mm});
            skLineSegment(sketch, "E2011", {"start": v(61.28, -70.91) * mm, "end": v(61.42, -71) * mm});
            skLineSegment(sketch, "E2012", {"start": v(61.42, -71) * mm, "end": v(61.56, -71.08) * mm});
            skLineSegment(sketch, "E2013", {"start": v(61.56, -71.08) * mm, "end": v(61.7, -71.16) * mm});
            skLineSegment(sketch, "E2014", {"start": v(61.7, -71.16) * mm, "end": v(61.86, -71.24) * mm});
            skLineSegment(sketch, "E2015", {"start": v(61.86, -71.24) * mm, "end": v(62, -71.32) * mm});
            skLineSegment(sketch, "E2016", {"start": v(62, -71.32) * mm, "end": v(62.16, -71.4) * mm});
            skLineSegment(sketch, "E2017", {"start": v(62.16, -71.4) * mm, "end": v(62.32, -71.5) * mm});
            skLineSegment(sketch, "E2018", {"start": v(62.32, -71.5) * mm, "end": v(62.48, -71.58) * mm});
            skLineSegment(sketch, "E2019", {"start": v(62.48, -71.58) * mm, "end": v(62.64, -71.66) * mm});
            skLineSegment(sketch, "E2020", {"start": v(62.64, -71.66) * mm, "end": v(62.8, -71.75) * mm});
            skLineSegment(sketch, "E2021", {"start": v(62.8, -71.75) * mm, "end": v(62.97, -71.83) * mm});
            skLineSegment(sketch, "E2022", {"start": v(62.97, -71.83) * mm, "end": v(63.14, -71.92) * mm});
            skLineSegment(sketch, "E2023", {"start": v(63.14, -71.92) * mm, "end": v(63.31, -72) * mm});
            skLineSegment(sketch, "E2024", {"start": v(63.31, -72) * mm, "end": v(63.49, -72.09) * mm});
            skLineSegment(sketch, "E2025", {"start": v(63.49, -72.09) * mm, "end": v(63.67, -72.17) * mm});
            skLineSegment(sketch, "E2026", {"start": v(63.67, -72.17) * mm, "end": v(63.85, -72.26) * mm});
            skLineSegment(sketch, "E2027", {"start": v(63.85, -72.26) * mm, "end": v(64.03, -72.34) * mm});
            skLineSegment(sketch, "E2028", {"start": v(64.03, -72.34) * mm, "end": v(64.22, -72.43) * mm});
            skLineSegment(sketch, "E2029", {"start": v(64.22, -72.43) * mm, "end": v(64.4, -72.52) * mm});
            skLineSegment(sketch, "E2030", {"start": v(64.4, -72.52) * mm, "end": v(64.57, -72.58) * mm});
            skLineSegment(sketch, "E2031", {"start": v(64.57, -72.58) * mm, "end": v(66.16, -71.13) * mm});
            skLineSegment(sketch, "E2032", {"start": v(66.16, -71.13) * mm, "end": v(66.12, -70.96) * mm});
            skLineSegment(sketch, "E2033", {"start": v(66.12, -70.96) * mm, "end": v(66.05, -70.76) * mm});
            skLineSegment(sketch, "E2034", {"start": v(66.05, -70.76) * mm, "end": v(65.98, -70.57) * mm});
            skLineSegment(sketch, "E2035", {"start": v(65.98, -70.57) * mm, "end": v(65.92, -70.38) * mm});
            skLineSegment(sketch, "E2036", {"start": v(65.92, -70.38) * mm, "end": v(65.85, -70.19) * mm});
            skLineSegment(sketch, "E2037", {"start": v(65.85, -70.19) * mm, "end": v(65.78, -70) * mm});
            skLineSegment(sketch, "E2038", {"start": v(65.78, -70) * mm, "end": v(65.71, -69.82) * mm});
            skLineSegment(sketch, "E2039", {"start": v(65.71, -69.82) * mm, "end": v(65.64, -69.64) * mm});
            skLineSegment(sketch, "E2040", {"start": v(65.64, -69.64) * mm, "end": v(65.57, -69.46) * mm});
            skLineSegment(sketch, "E2041", {"start": v(65.57, -69.46) * mm, "end": v(65.5, -69.29) * mm});
            skLineSegment(sketch, "E2042", {"start": v(65.5, -69.29) * mm, "end": v(65.43, -69.12) * mm});
            skLineSegment(sketch, "E2043", {"start": v(65.43, -69.12) * mm, "end": v(65.37, -68.95) * mm});
            skLineSegment(sketch, "E2044", {"start": v(65.37, -68.95) * mm, "end": v(65.3, -68.78) * mm});
            skLineSegment(sketch, "E2045", {"start": v(65.3, -68.78) * mm, "end": v(65.23, -68.62) * mm});
            skLineSegment(sketch, "E2046", {"start": v(65.23, -68.62) * mm, "end": v(65.16, -68.46) * mm});
            skLineSegment(sketch, "E2047", {"start": v(65.16, -68.46) * mm, "end": v(65.1, -68.3) * mm});
            skLineSegment(sketch, "E2048", {"start": v(65.1, -68.3) * mm, "end": v(65.02, -68.14) * mm});
            skLineSegment(sketch, "E2049", {"start": v(65.02, -68.14) * mm, "end": v(64.95, -67.99) * mm});
            skLineSegment(sketch, "E2050", {"start": v(64.95, -67.99) * mm, "end": v(64.89, -67.84) * mm});
            skLineSegment(sketch, "E2051", {"start": v(64.89, -67.84) * mm, "end": v(64.82, -67.69) * mm});
            skLineSegment(sketch, "E2052", {"start": v(64.82, -67.69) * mm, "end": v(64.75, -67.54) * mm});
            skLineSegment(sketch, "E2053", {"start": v(64.75, -67.54) * mm, "end": v(64.68, -67.4) * mm});
            skLineSegment(sketch, "E2054", {"start": v(64.68, -67.4) * mm, "end": v(64.62, -67.26) * mm});
            skLineSegment(sketch, "E2055", {"start": v(64.62, -67.26) * mm, "end": v(64.55, -67.12) * mm});
            skLineSegment(sketch, "E2056", {"start": v(64.55, -67.12) * mm, "end": v(64.48, -66.99) * mm});
            skLineSegment(sketch, "E2057", {"start": v(64.48, -66.99) * mm, "end": v(64.42, -66.86) * mm});
            skLineSegment(sketch, "E2058", {"start": v(64.42, -66.86) * mm, "end": v(64.35, -66.73) * mm});
            skLineSegment(sketch, "E2059", {"start": v(64.35, -66.73) * mm, "end": v(64.29, -66.6) * mm});
            skLineSegment(sketch, "E2060", {"start": v(64.29, -66.6) * mm, "end": v(64.22, -66.47) * mm});
            skLineSegment(sketch, "E2061", {"start": v(64.22, -66.47) * mm, "end": v(64.16, -66.35) * mm});
            skLineSegment(sketch, "E2062", {"start": v(64.16, -66.35) * mm, "end": v(64.1, -66.23) * mm});
            skLineSegment(sketch, "E2063", {"start": v(64.1, -66.23) * mm, "end": v(64.03, -66.11) * mm});
            skLineSegment(sketch, "E2064", {"start": v(64.03, -66.11) * mm, "end": v(63.97, -66) * mm});
            skLineSegment(sketch, "E2065", {"start": v(63.97, -66) * mm, "end": v(63.9, -65.89) * mm});
            skLineSegment(sketch, "E2066", {"start": v(63.9, -65.89) * mm, "end": v(63.85, -65.78) * mm});
            skLineSegment(sketch, "E2067", {"start": v(63.85, -65.78) * mm, "end": v(63.79, -65.67) * mm});
            skLineSegment(sketch, "E2068", {"start": v(63.79, -65.67) * mm, "end": v(63.73, -65.57) * mm});
            skLineSegment(sketch, "E2069", {"start": v(63.73, -65.57) * mm, "end": v(63.67, -65.46) * mm});
            skLineSegment(sketch, "E2070", {"start": v(63.67, -65.46) * mm, "end": v(63.61, -65.36) * mm});
            skLineSegment(sketch, "E2071", {"start": v(63.61, -65.36) * mm, "end": v(63.77, -64.92) * mm});
            skLineSegment(sketch, "E2072", {"start": v(63.77, -64.92) * mm, "end": v(64.97, -63.72) * mm});
            skLineSegment(sketch, "E2073", {"start": v(64.97, -63.72) * mm, "end": v(65.41, -63.56) * mm});
            skLineSegment(sketch, "E2074", {"start": v(65.41, -63.56) * mm, "end": v(65.51, -63.62) * mm});
            skLineSegment(sketch, "E2075", {"start": v(65.51, -63.62) * mm, "end": v(65.61, -63.68) * mm});
            skLineSegment(sketch, "E2076", {"start": v(65.61, -63.68) * mm, "end": v(65.72, -63.74) * mm});
            skLineSegment(sketch, "E2077", {"start": v(65.72, -63.74) * mm, "end": v(65.83, -63.8) * mm});
            skLineSegment(sketch, "E2078", {"start": v(65.83, -63.8) * mm, "end": v(65.94, -63.86) * mm});
            skLineSegment(sketch, "E2079", {"start": v(65.94, -63.86) * mm, "end": v(66.05, -63.92) * mm});
            skLineSegment(sketch, "E2080", {"start": v(66.05, -63.92) * mm, "end": v(66.16, -63.98) * mm});
            skLineSegment(sketch, "E2081", {"start": v(66.16, -63.98) * mm, "end": v(66.28, -64.05) * mm});
            skLineSegment(sketch, "E2082", {"start": v(66.28, -64.05) * mm, "end": v(66.4, -64.1) * mm});
            skLineSegment(sketch, "E2083", {"start": v(66.4, -64.1) * mm, "end": v(66.52, -64.17) * mm});
            skLineSegment(sketch, "E2084", {"start": v(66.52, -64.17) * mm, "end": v(66.65, -64.24) * mm});
            skLineSegment(sketch, "E2085", {"start": v(66.65, -64.24) * mm, "end": v(66.77, -64.3) * mm});
            skLineSegment(sketch, "E2086", {"start": v(66.77, -64.3) * mm, "end": v(66.9, -64.37) * mm});
            skLineSegment(sketch, "E2087", {"start": v(66.9, -64.37) * mm, "end": v(67.04, -64.43) * mm});
            skLineSegment(sketch, "E2088", {"start": v(67.04, -64.43) * mm, "end": v(67.17, -64.5) * mm});
            skLineSegment(sketch, "E2089", {"start": v(67.17, -64.5) * mm, "end": v(67.31, -64.57) * mm});
            skLineSegment(sketch, "E2090", {"start": v(67.31, -64.57) * mm, "end": v(67.45, -64.63) * mm});
            skLineSegment(sketch, "E2091", {"start": v(67.45, -64.63) * mm, "end": v(67.6, -64.7) * mm});
            skLineSegment(sketch, "E2092", {"start": v(67.6, -64.7) * mm, "end": v(67.74, -64.77) * mm});
            skLineSegment(sketch, "E2093", {"start": v(67.74, -64.77) * mm, "end": v(67.89, -64.83) * mm});
            skLineSegment(sketch, "E2094", {"start": v(67.89, -64.83) * mm, "end": v(68.04, -64.9) * mm});
            skLineSegment(sketch, "E2095", {"start": v(68.04, -64.9) * mm, "end": v(68.2, -64.97) * mm});
            skLineSegment(sketch, "E2096", {"start": v(68.2, -64.97) * mm, "end": v(68.35, -65.04) * mm});
            skLineSegment(sketch, "E2097", {"start": v(68.35, -65.04) * mm, "end": v(68.5, -65.1) * mm});
            skLineSegment(sketch, "E2098", {"start": v(68.5, -65.1) * mm, "end": v(68.67, -65.18) * mm});
            skLineSegment(sketch, "E2099", {"start": v(68.67, -65.18) * mm, "end": v(68.83, -65.24) * mm});
            skLineSegment(sketch, "E2100", {"start": v(68.83, -65.24) * mm, "end": v(69, -65.31) * mm});
            skLineSegment(sketch, "E2101", {"start": v(69, -65.31) * mm, "end": v(69.17, -65.38) * mm});
            skLineSegment(sketch, "E2102", {"start": v(69.17, -65.38) * mm, "end": v(69.34, -65.45) * mm});
            skLineSegment(sketch, "E2103", {"start": v(69.34, -65.45) * mm, "end": v(69.51, -65.52) * mm});
            skLineSegment(sketch, "E2104", {"start": v(69.51, -65.52) * mm, "end": v(69.7, -65.59) * mm});
            skLineSegment(sketch, "E2105", {"start": v(69.7, -65.59) * mm, "end": v(69.87, -65.66) * mm});
            skLineSegment(sketch, "E2106", {"start": v(69.87, -65.66) * mm, "end": v(70.05, -65.73) * mm});
            skLineSegment(sketch, "E2107", {"start": v(70.05, -65.73) * mm, "end": v(70.24, -65.8) * mm});
            skLineSegment(sketch, "E2108", {"start": v(70.24, -65.8) * mm, "end": v(70.43, -65.86) * mm});
            skLineSegment(sketch, "E2109", {"start": v(70.43, -65.86) * mm, "end": v(70.62, -65.93) * mm});
            skLineSegment(sketch, "E2110", {"start": v(70.62, -65.93) * mm, "end": v(70.81, -66) * mm});
            skLineSegment(sketch, "E2111", {"start": v(70.81, -66) * mm, "end": v(71, -66.07) * mm});
            skLineSegment(sketch, "E2112", {"start": v(71, -66.07) * mm, "end": v(71.18, -66.1) * mm});
            skLineSegment(sketch, "E2113", {"start": v(71.18, -66.1) * mm, "end": v(72.62, -64.52) * mm});
            skLineSegment(sketch, "E2114", {"start": v(72.62, -64.52) * mm, "end": v(72.57, -64.35) * mm});
            skLineSegment(sketch, "E2115", {"start": v(72.57, -64.35) * mm, "end": v(72.48, -64.16) * mm});
            skLineSegment(sketch, "E2116", {"start": v(72.48, -64.16) * mm, "end": v(72.4, -63.97) * mm});
            skLineSegment(sketch, "E2117", {"start": v(72.4, -63.97) * mm, "end": v(72.3, -63.8) * mm});
            skLineSegment(sketch, "E2118", {"start": v(72.3, -63.8) * mm, "end": v(72.22, -63.61) * mm});
            skLineSegment(sketch, "E2119", {"start": v(72.22, -63.61) * mm, "end": v(72.14, -63.43) * mm});
            skLineSegment(sketch, "E2120", {"start": v(72.14, -63.43) * mm, "end": v(72.05, -63.26) * mm});
            skLineSegment(sketch, "E2121", {"start": v(72.05, -63.26) * mm, "end": v(71.96, -63.09) * mm});
            skLineSegment(sketch, "E2122", {"start": v(71.96, -63.09) * mm, "end": v(71.88, -62.92) * mm});
            skLineSegment(sketch, "E2123", {"start": v(71.88, -62.92) * mm, "end": v(71.8, -62.75) * mm});
            skLineSegment(sketch, "E2124", {"start": v(71.8, -62.75) * mm, "end": v(71.7, -62.58) * mm});
            skLineSegment(sketch, "E2125", {"start": v(71.7, -62.58) * mm, "end": v(71.62, -62.42) * mm});
            skLineSegment(sketch, "E2126", {"start": v(71.62, -62.42) * mm, "end": v(71.54, -62.26) * mm});
            skLineSegment(sketch, "E2127", {"start": v(71.54, -62.26) * mm, "end": v(71.46, -62.1) * mm});
            skLineSegment(sketch, "E2128", {"start": v(71.46, -62.1) * mm, "end": v(71.37, -61.95) * mm});
            skLineSegment(sketch, "E2129", {"start": v(71.37, -61.95) * mm, "end": v(71.29, -61.8) * mm});
            skLineSegment(sketch, "E2130", {"start": v(71.29, -61.8) * mm, "end": v(71.2, -61.65) * mm});
            skLineSegment(sketch, "E2131", {"start": v(71.2, -61.65) * mm, "end": v(71.12, -61.5) * mm});
            skLineSegment(sketch, "E2132", {"start": v(71.12, -61.5) * mm, "end": v(71.04, -61.36) * mm});
            skLineSegment(sketch, "E2133", {"start": v(71.04, -61.36) * mm, "end": v(70.96, -61.22) * mm});
            skLineSegment(sketch, "E2134", {"start": v(70.96, -61.22) * mm, "end": v(70.88, -61.08) * mm});
            skLineSegment(sketch, "E2135", {"start": v(70.88, -61.08) * mm, "end": v(70.8, -60.95) * mm});
            skLineSegment(sketch, "E2136", {"start": v(70.8, -60.95) * mm, "end": v(70.72, -60.81) * mm});
            skLineSegment(sketch, "E2137", {"start": v(70.72, -60.81) * mm, "end": v(70.64, -60.68) * mm});
            skLineSegment(sketch, "E2138", {"start": v(70.64, -60.68) * mm, "end": v(70.56, -60.56) * mm});
            skLineSegment(sketch, "E2139", {"start": v(70.56, -60.56) * mm, "end": v(70.48, -60.43) * mm});
            skLineSegment(sketch, "E2140", {"start": v(70.48, -60.43) * mm, "end": v(70.4, -60.3) * mm});
            skLineSegment(sketch, "E2141", {"start": v(70.4, -60.3) * mm, "end": v(70.33, -60.19) * mm});
            skLineSegment(sketch, "E2142", {"start": v(70.33, -60.19) * mm, "end": v(70.25, -60.07) * mm});
            skLineSegment(sketch, "E2143", {"start": v(70.25, -60.07) * mm, "end": v(70.18, -59.95) * mm});
            skLineSegment(sketch, "E2144", {"start": v(70.18, -59.95) * mm, "end": v(70.1, -59.84) * mm});
            skLineSegment(sketch, "E2145", {"start": v(70.1, -59.84) * mm, "end": v(70.03, -59.73) * mm});
            skLineSegment(sketch, "E2146", {"start": v(70.03, -59.73) * mm, "end": v(69.96, -59.62) * mm});
            skLineSegment(sketch, "E2147", {"start": v(69.96, -59.62) * mm, "end": v(69.88, -59.51) * mm});
            skLineSegment(sketch, "E2148", {"start": v(69.88, -59.51) * mm, "end": v(69.81, -59.41) * mm});
            skLineSegment(sketch, "E2149", {"start": v(69.81, -59.41) * mm, "end": v(69.74, -59.3) * mm});
            skLineSegment(sketch, "E2150", {"start": v(69.74, -59.3) * mm, "end": v(69.67, -59.21) * mm});
            skLineSegment(sketch, "E2151", {"start": v(69.67, -59.21) * mm, "end": v(69.6, -59.11) * mm});
            skLineSegment(sketch, "E2152", {"start": v(69.6, -59.11) * mm, "end": v(69.54, -59.02) * mm});
            skLineSegment(sketch, "E2153", {"start": v(69.54, -59.02) * mm, "end": v(69.65, -58.56) * mm});
            skLineSegment(sketch, "E2154", {"start": v(69.65, -58.56) * mm, "end": v(70.73, -57.26) * mm});
            skLineSegment(sketch, "E2155", {"start": v(70.73, -57.26) * mm, "end": v(71.16, -57.05) * mm});
            skLineSegment(sketch, "E2156", {"start": v(71.16, -57.05) * mm, "end": v(71.26, -57.1) * mm});
            skLineSegment(sketch, "E2157", {"start": v(71.26, -57.1) * mm, "end": v(71.37, -57.15) * mm});
            skLineSegment(sketch, "E2158", {"start": v(71.37, -57.15) * mm, "end": v(71.48, -57.2) * mm});
            skLineSegment(sketch, "E2159", {"start": v(71.48, -57.2) * mm, "end": v(71.6, -57.25) * mm});
            skLineSegment(sketch, "E2160", {"start": v(71.6, -57.25) * mm, "end": v(71.7, -57.3) * mm});
            skLineSegment(sketch, "E2161", {"start": v(71.7, -57.3) * mm, "end": v(71.83, -57.35) * mm});
            skLineSegment(sketch, "E2162", {"start": v(71.83, -57.35) * mm, "end": v(71.95, -57.4) * mm});
            skLineSegment(sketch, "E2163", {"start": v(71.95, -57.4) * mm, "end": v(72.07, -57.46) * mm});
            skLineSegment(sketch, "E2164", {"start": v(72.07, -57.46) * mm, "end": v(72.2, -57.5) * mm});
            skLineSegment(sketch, "E2165", {"start": v(72.2, -57.5) * mm, "end": v(72.32, -57.56) * mm});
            skLineSegment(sketch, "E2166", {"start": v(72.32, -57.56) * mm, "end": v(72.45, -57.61) * mm});
            skLineSegment(sketch, "E2167", {"start": v(72.45, -57.61) * mm, "end": v(72.58, -57.66) * mm});
            skLineSegment(sketch, "E2168", {"start": v(72.58, -57.66) * mm, "end": v(72.72, -57.72) * mm});
            skLineSegment(sketch, "E2169", {"start": v(72.72, -57.72) * mm, "end": v(72.86, -57.77) * mm});
            skLineSegment(sketch, "E2170", {"start": v(72.86, -57.77) * mm, "end": v(73, -57.82) * mm});
            skLineSegment(sketch, "E2171", {"start": v(73, -57.82) * mm, "end": v(73.14, -57.88) * mm});
            skLineSegment(sketch, "E2172", {"start": v(73.14, -57.88) * mm, "end": v(73.29, -57.93) * mm});
            skLineSegment(sketch, "E2173", {"start": v(73.29, -57.93) * mm, "end": v(73.44, -57.98) * mm});
            skLineSegment(sketch, "E2174", {"start": v(73.44, -57.98) * mm, "end": v(73.59, -58.03) * mm});
            skLineSegment(sketch, "E2175", {"start": v(73.59, -58.03) * mm, "end": v(73.74, -58.09) * mm});
            skLineSegment(sketch, "E2176", {"start": v(73.74, -58.09) * mm, "end": v(73.9, -58.14) * mm});
            skLineSegment(sketch, "E2177", {"start": v(73.9, -58.14) * mm, "end": v(74.06, -58.2) * mm});
            skLineSegment(sketch, "E2178", {"start": v(74.06, -58.2) * mm, "end": v(74.22, -58.25) * mm});
            skLineSegment(sketch, "E2179", {"start": v(74.22, -58.25) * mm, "end": v(74.38, -58.3) * mm});
            skLineSegment(sketch, "E2180", {"start": v(74.38, -58.3) * mm, "end": v(74.55, -58.35) * mm});
            skLineSegment(sketch, "E2181", {"start": v(74.55, -58.35) * mm, "end": v(74.72, -58.4) * mm});
            skLineSegment(sketch, "E2182", {"start": v(74.72, -58.4) * mm, "end": v(74.9, -58.46) * mm});
            skLineSegment(sketch, "E2183", {"start": v(74.9, -58.46) * mm, "end": v(75.07, -58.51) * mm});
            skLineSegment(sketch, "E2184", {"start": v(75.07, -58.51) * mm, "end": v(75.25, -58.56) * mm});
            skLineSegment(sketch, "E2185", {"start": v(75.25, -58.56) * mm, "end": v(75.43, -58.61) * mm});
            skLineSegment(sketch, "E2186", {"start": v(75.43, -58.61) * mm, "end": v(75.6, -58.67) * mm});
            skLineSegment(sketch, "E2187", {"start": v(75.6, -58.67) * mm, "end": v(75.8, -58.72) * mm});
            skLineSegment(sketch, "E2188", {"start": v(75.8, -58.72) * mm, "end": v(75.98, -58.77) * mm});
            skLineSegment(sketch, "E2189", {"start": v(75.98, -58.77) * mm, "end": v(76.17, -58.82) * mm});
            skLineSegment(sketch, "E2190", {"start": v(76.17, -58.82) * mm, "end": v(76.37, -58.87) * mm});
            skLineSegment(sketch, "E2191", {"start": v(76.37, -58.87) * mm, "end": v(76.56, -58.92) * mm});
            skLineSegment(sketch, "E2192", {"start": v(76.56, -58.92) * mm, "end": v(76.76, -58.97) * mm});
            skLineSegment(sketch, "E2193", {"start": v(76.76, -58.97) * mm, "end": v(76.96, -59.02) * mm});
            skLineSegment(sketch, "E2194", {"start": v(76.96, -59.02) * mm, "end": v(77.14, -59.04) * mm});
            skLineSegment(sketch, "E2195", {"start": v(77.14, -59.04) * mm, "end": v(78.43, -57.32) * mm});
            skLineSegment(sketch, "E2196", {"start": v(78.43, -57.32) * mm, "end": v(78.35, -57.16) * mm});
            skLineSegment(sketch, "E2197", {"start": v(78.35, -57.16) * mm, "end": v(78.25, -56.98) * mm});
            skLineSegment(sketch, "E2198", {"start": v(78.25, -56.98) * mm, "end": v(78.15, -56.8) * mm});
            skLineSegment(sketch, "E2199", {"start": v(78.15, -56.8) * mm, "end": v(78.04, -56.63) * mm});
            skLineSegment(sketch, "E2200", {"start": v(78.04, -56.63) * mm, "end": v(77.94, -56.46) * mm});
            skLineSegment(sketch, "E2201", {"start": v(77.94, -56.46) * mm, "end": v(77.84, -56.29) * mm});
            skLineSegment(sketch, "E2202", {"start": v(77.84, -56.29) * mm, "end": v(77.74, -56.12) * mm});
            skLineSegment(sketch, "E2203", {"start": v(77.74, -56.12) * mm, "end": v(77.63, -55.96) * mm});
            skLineSegment(sketch, "E2204", {"start": v(77.63, -55.96) * mm, "end": v(77.53, -55.8) * mm});
            skLineSegment(sketch, "E2205", {"start": v(77.53, -55.8) * mm, "end": v(77.43, -55.64) * mm});
            skLineSegment(sketch, "E2206", {"start": v(77.43, -55.64) * mm, "end": v(77.33, -55.48) * mm});
            skLineSegment(sketch, "E2207", {"start": v(77.33, -55.48) * mm, "end": v(77.23, -55.33) * mm});
            skLineSegment(sketch, "E2208", {"start": v(77.23, -55.33) * mm, "end": v(77.13, -55.18) * mm});
            skLineSegment(sketch, "E2209", {"start": v(77.13, -55.18) * mm, "end": v(77.04, -55.03) * mm});
            skLineSegment(sketch, "E2210", {"start": v(77.04, -55.03) * mm, "end": v(76.94, -54.89) * mm});
            skLineSegment(sketch, "E2211", {"start": v(76.94, -54.89) * mm, "end": v(76.84, -54.74) * mm});
            skLineSegment(sketch, "E2212", {"start": v(76.84, -54.74) * mm, "end": v(76.74, -54.6) * mm});
            skLineSegment(sketch, "E2213", {"start": v(76.74, -54.6) * mm, "end": v(76.65, -54.47) * mm});
            skLineSegment(sketch, "E2214", {"start": v(76.65, -54.47) * mm, "end": v(76.55, -54.33) * mm});
            skLineSegment(sketch, "E2215", {"start": v(76.55, -54.33) * mm, "end": v(76.46, -54.2) * mm});
            skLineSegment(sketch, "E2216", {"start": v(76.46, -54.2) * mm, "end": v(76.36, -54.07) * mm});
            skLineSegment(sketch, "E2217", {"start": v(76.36, -54.07) * mm, "end": v(76.27, -53.94) * mm});
            skLineSegment(sketch, "E2218", {"start": v(76.27, -53.94) * mm, "end": v(76.18, -53.82) * mm});
            skLineSegment(sketch, "E2219", {"start": v(76.18, -53.82) * mm, "end": v(76.09, -53.7) * mm});
            skLineSegment(sketch, "E2220", {"start": v(76.09, -53.7) * mm, "end": v(76, -53.57) * mm});
            skLineSegment(sketch, "E2221", {"start": v(76, -53.57) * mm, "end": v(75.9, -53.46) * mm});
            skLineSegment(sketch, "E2222", {"start": v(75.9, -53.46) * mm, "end": v(75.82, -53.34) * mm});
            skLineSegment(sketch, "E2223", {"start": v(75.82, -53.34) * mm, "end": v(75.73, -53.23) * mm});
            skLineSegment(sketch, "E2224", {"start": v(75.73, -53.23) * mm, "end": v(75.64, -53.12) * mm});
            skLineSegment(sketch, "E2225", {"start": v(75.64, -53.12) * mm, "end": v(75.56, -53) * mm});
            skLineSegment(sketch, "E2226", {"start": v(75.56, -53) * mm, "end": v(75.47, -52.9) * mm});
            skLineSegment(sketch, "E2227", {"start": v(75.47, -52.9) * mm, "end": v(75.39, -52.8) * mm});
            skLineSegment(sketch, "E2228", {"start": v(75.39, -52.8) * mm, "end": v(75.3, -52.7) * mm});
            skLineSegment(sketch, "E2229", {"start": v(75.3, -52.7) * mm, "end": v(75.22, -52.6) * mm});
            skLineSegment(sketch, "E2230", {"start": v(75.22, -52.6) * mm, "end": v(75.14, -52.5) * mm});
            skLineSegment(sketch, "E2231", {"start": v(75.14, -52.5) * mm, "end": v(75.06, -52.41) * mm});
            skLineSegment(sketch, "E2232", {"start": v(75.06, -52.41) * mm, "end": v(74.98, -52.32) * mm});
            skLineSegment(sketch, "E2233", {"start": v(74.98, -52.32) * mm, "end": v(74.9, -52.23) * mm});
            skLineSegment(sketch, "E2234", {"start": v(74.9, -52.23) * mm, "end": v(74.83, -52.14) * mm});
            skLineSegment(sketch, "E2235", {"start": v(74.83, -52.14) * mm, "end": v(74.9, -51.67) * mm});
            skLineSegment(sketch, "E2236", {"start": v(74.9, -51.67) * mm, "end": v(75.85, -50.28) * mm});
            skLineSegment(sketch, "E2237", {"start": v(75.85, -50.28) * mm, "end": v(76.26, -50.03) * mm});
            skLineSegment(sketch, "E2238", {"start": v(76.26, -50.03) * mm, "end": v(76.37, -50.07) * mm});
            skLineSegment(sketch, "E2239", {"start": v(76.37, -50.07) * mm, "end": v(76.48, -50.1) * mm});
            skLineSegment(sketch, "E2240", {"start": v(76.48, -50.1) * mm, "end": v(76.6, -50.15) * mm});
            skLineSegment(sketch, "E2241", {"start": v(76.6, -50.15) * mm, "end": v(76.71, -50.19) * mm});
            skLineSegment(sketch, "E2242", {"start": v(76.71, -50.19) * mm, "end": v(76.83, -50.23) * mm});
            skLineSegment(sketch, "E2243", {"start": v(76.83, -50.23) * mm, "end": v(76.95, -50.27) * mm});
            skLineSegment(sketch, "E2244", {"start": v(76.95, -50.27) * mm, "end": v(77.08, -50.3) * mm});
            skLineSegment(sketch, "E2245", {"start": v(77.08, -50.3) * mm, "end": v(77.2, -50.34) * mm});
            skLineSegment(sketch, "E2246", {"start": v(77.2, -50.34) * mm, "end": v(77.33, -50.38) * mm});
            skLineSegment(sketch, "E2247", {"start": v(77.33, -50.38) * mm, "end": v(77.47, -50.42) * mm});
            skLineSegment(sketch, "E2248", {"start": v(77.47, -50.42) * mm, "end": v(77.6, -50.46) * mm});
            skLineSegment(sketch, "E2249", {"start": v(77.6, -50.46) * mm, "end": v(77.74, -50.5) * mm});
            skLineSegment(sketch, "E2250", {"start": v(77.74, -50.5) * mm, "end": v(77.88, -50.54) * mm});
            skLineSegment(sketch, "E2251", {"start": v(77.88, -50.54) * mm, "end": v(78.02, -50.58) * mm});
            skLineSegment(sketch, "E2252", {"start": v(78.02, -50.58) * mm, "end": v(78.17, -50.62) * mm});
            skLineSegment(sketch, "E2253", {"start": v(78.17, -50.62) * mm, "end": v(78.31, -50.66) * mm});
            skLineSegment(sketch, "E2254", {"start": v(78.31, -50.66) * mm, "end": v(78.46, -50.7) * mm});
            skLineSegment(sketch, "E2255", {"start": v(78.46, -50.7) * mm, "end": v(78.62, -50.74) * mm});
            skLineSegment(sketch, "E2256", {"start": v(78.62, -50.74) * mm, "end": v(78.77, -50.78) * mm});
            skLineSegment(sketch, "E2257", {"start": v(78.77, -50.78) * mm, "end": v(78.93, -50.82) * mm});
            skLineSegment(sketch, "E2258", {"start": v(78.93, -50.82) * mm, "end": v(79.1, -50.85) * mm});
            skLineSegment(sketch, "E2259", {"start": v(79.1, -50.85) * mm, "end": v(79.25, -50.9) * mm});
            skLineSegment(sketch, "E2260", {"start": v(79.25, -50.9) * mm, "end": v(79.42, -50.93) * mm});
            skLineSegment(sketch, "E2261", {"start": v(79.42, -50.93) * mm, "end": v(79.59, -50.97) * mm});
            skLineSegment(sketch, "E2262", {"start": v(79.59, -50.97) * mm, "end": v(79.76, -51) * mm});
            skLineSegment(sketch, "E2263", {"start": v(79.76, -51) * mm, "end": v(79.93, -51.04) * mm});
            skLineSegment(sketch, "E2264", {"start": v(79.93, -51.04) * mm, "end": v(80.11, -51.07) * mm});
            skLineSegment(sketch, "E2265", {"start": v(80.11, -51.07) * mm, "end": v(80.3, -51.11) * mm});
            skLineSegment(sketch, "E2266", {"start": v(80.3, -51.11) * mm, "end": v(80.47, -51.15) * mm});
            skLineSegment(sketch, "E2267", {"start": v(80.47, -51.15) * mm, "end": v(80.66, -51.18) * mm});
            skLineSegment(sketch, "E2268", {"start": v(80.66, -51.18) * mm, "end": v(80.84, -51.21) * mm});
            skLineSegment(sketch, "E2269", {"start": v(80.84, -51.21) * mm, "end": v(81.03, -51.25) * mm});
            skLineSegment(sketch, "E2270", {"start": v(81.03, -51.25) * mm, "end": v(81.23, -51.28) * mm});
            skLineSegment(sketch, "E2271", {"start": v(81.23, -51.28) * mm, "end": v(81.42, -51.31) * mm});
            skLineSegment(sketch, "E2272", {"start": v(81.42, -51.31) * mm, "end": v(81.62, -51.34) * mm});
            skLineSegment(sketch, "E2273", {"start": v(81.62, -51.34) * mm, "end": v(81.82, -51.37) * mm});
            skLineSegment(sketch, "E2274", {"start": v(81.82, -51.37) * mm, "end": v(82.02, -51.4) * mm});
            skLineSegment(sketch, "E2275", {"start": v(82.02, -51.4) * mm, "end": v(82.23, -51.43) * mm});
            skLineSegment(sketch, "E2276", {"start": v(82.23, -51.43) * mm, "end": v(82.4, -51.44) * mm});
            skLineSegment(sketch, "E2277", {"start": v(82.4, -51.44) * mm, "end": v(83.52, -49.6) * mm});
            skLineSegment(sketch, "E2278", {"start": v(83.52, -49.6) * mm, "end": v(83.43, -49.45) * mm});
            skLineSegment(sketch, "E2279", {"start": v(83.43, -49.45) * mm, "end": v(83.31, -49.28) * mm});
            skLineSegment(sketch, "E2280", {"start": v(83.31, -49.28) * mm, "end": v(83.2, -49.12) * mm});
            skLineSegment(sketch, "E2281", {"start": v(83.2, -49.12) * mm, "end": v(83.07, -48.95) * mm});
            skLineSegment(sketch, "E2282", {"start": v(83.07, -48.95) * mm, "end": v(82.95, -48.8) * mm});
            skLineSegment(sketch, "E2283", {"start": v(82.95, -48.8) * mm, "end": v(82.84, -48.64) * mm});
            skLineSegment(sketch, "E2284", {"start": v(82.84, -48.64) * mm, "end": v(82.72, -48.48) * mm});
            skLineSegment(sketch, "E2285", {"start": v(82.72, -48.48) * mm, "end": v(82.6, -48.33) * mm});
            skLineSegment(sketch, "E2286", {"start": v(82.6, -48.33) * mm, "end": v(82.49, -48.18) * mm});
            skLineSegment(sketch, "E2287", {"start": v(82.49, -48.18) * mm, "end": v(82.37, -48.03) * mm});
            skLineSegment(sketch, "E2288", {"start": v(82.37, -48.03) * mm, "end": v(82.26, -47.88) * mm});
            skLineSegment(sketch, "E2289", {"start": v(82.26, -47.88) * mm, "end": v(82.14, -47.74) * mm});
            skLineSegment(sketch, "E2290", {"start": v(82.14, -47.74) * mm, "end": v(82.03, -47.6) * mm});
            skLineSegment(sketch, "E2291", {"start": v(82.03, -47.6) * mm, "end": v(81.92, -47.46) * mm});
            skLineSegment(sketch, "E2292", {"start": v(81.92, -47.46) * mm, "end": v(81.8, -47.33) * mm});
            skLineSegment(sketch, "E2293", {"start": v(81.8, -47.33) * mm, "end": v(81.7, -47.2) * mm});
            skLineSegment(sketch, "E2294", {"start": v(81.7, -47.2) * mm, "end": v(81.59, -47.06) * mm});
            skLineSegment(sketch, "E2295", {"start": v(81.59, -47.06) * mm, "end": v(81.48, -46.93) * mm});
            skLineSegment(sketch, "E2296", {"start": v(81.48, -46.93) * mm, "end": v(81.37, -46.8) * mm});
            skLineSegment(sketch, "E2297", {"start": v(81.37, -46.8) * mm, "end": v(81.26, -46.69) * mm});
            skLineSegment(sketch, "E2298", {"start": v(81.26, -46.69) * mm, "end": v(81.16, -46.57) * mm});
            skLineSegment(sketch, "E2299", {"start": v(81.16, -46.57) * mm, "end": v(81.05, -46.45) * mm});
            skLineSegment(sketch, "E2300", {"start": v(81.05, -46.45) * mm, "end": v(80.95, -46.33) * mm});
            skLineSegment(sketch, "E2301", {"start": v(80.95, -46.33) * mm, "end": v(80.85, -46.22) * mm});
            skLineSegment(sketch, "E2302", {"start": v(80.85, -46.22) * mm, "end": v(80.75, -46.1) * mm});
            skLineSegment(sketch, "E2303", {"start": v(80.75, -46.1) * mm, "end": v(80.64, -46) * mm});
            skLineSegment(sketch, "E2304", {"start": v(80.64, -46) * mm, "end": v(80.55, -45.9) * mm});
            skLineSegment(sketch, "E2305", {"start": v(80.55, -45.9) * mm, "end": v(80.45, -45.79) * mm});
            skLineSegment(sketch, "E2306", {"start": v(80.45, -45.79) * mm, "end": v(80.35, -45.69) * mm});
            skLineSegment(sketch, "E2307", {"start": v(80.35, -45.69) * mm, "end": v(80.25, -45.59) * mm});
            skLineSegment(sketch, "E2308", {"start": v(80.25, -45.59) * mm, "end": v(80.16, -45.5) * mm});
            skLineSegment(sketch, "E2309", {"start": v(80.16, -45.5) * mm, "end": v(80.07, -45.4) * mm});
            skLineSegment(sketch, "E2310", {"start": v(80.07, -45.4) * mm, "end": v(79.97, -45.3) * mm});
            skLineSegment(sketch, "E2311", {"start": v(79.97, -45.3) * mm, "end": v(79.88, -45.21) * mm});
            skLineSegment(sketch, "E2312", {"start": v(79.88, -45.21) * mm, "end": v(79.8, -45.12) * mm});
            skLineSegment(sketch, "E2313", {"start": v(79.8, -45.12) * mm, "end": v(79.7, -45.04) * mm});
            skLineSegment(sketch, "E2314", {"start": v(79.7, -45.04) * mm, "end": v(79.62, -44.96) * mm});
            skLineSegment(sketch, "E2315", {"start": v(79.62, -44.96) * mm, "end": v(79.53, -44.87) * mm});
            skLineSegment(sketch, "E2316", {"start": v(79.53, -44.87) * mm, "end": v(79.45, -44.8) * mm});
            skLineSegment(sketch, "E2317", {"start": v(79.45, -44.8) * mm, "end": v(79.48, -44.32) * mm});
            skLineSegment(sketch, "E2318", {"start": v(79.48, -44.32) * mm, "end": v(80.29, -42.84) * mm});
            skLineSegment(sketch, "E2319", {"start": v(80.29, -42.84) * mm, "end": v(80.67, -42.56) * mm});
            skLineSegment(sketch, "E2320", {"start": v(80.67, -42.56) * mm, "end": v(80.78, -42.58) * mm});
            skLineSegment(sketch, "E2321", {"start": v(80.78, -42.58) * mm, "end": v(80.9, -42.61) * mm});
            skLineSegment(sketch, "E2322", {"start": v(80.9, -42.61) * mm, "end": v(81.01, -42.64) * mm});
            skLineSegment(sketch, "E2323", {"start": v(81.01, -42.64) * mm, "end": v(81.13, -42.67) * mm});
            skLineSegment(sketch, "E2324", {"start": v(81.13, -42.67) * mm, "end": v(81.26, -42.7) * mm});
            skLineSegment(sketch, "E2325", {"start": v(81.26, -42.7) * mm, "end": v(81.38, -42.72) * mm});
            skLineSegment(sketch, "E2326", {"start": v(81.38, -42.72) * mm, "end": v(81.5, -42.75) * mm});
            skLineSegment(sketch, "E2327", {"start": v(81.5, -42.75) * mm, "end": v(81.64, -42.78) * mm});
            skLineSegment(sketch, "E2328", {"start": v(81.64, -42.78) * mm, "end": v(81.77, -42.8) * mm});
            skLineSegment(sketch, "E2329", {"start": v(81.77, -42.8) * mm, "end": v(81.9, -42.83) * mm});
            skLineSegment(sketch, "E2330", {"start": v(81.9, -42.83) * mm, "end": v(82.05, -42.86) * mm});
            skLineSegment(sketch, "E2331", {"start": v(82.05, -42.86) * mm, "end": v(82.19, -42.88) * mm});
            skLineSegment(sketch, "E2332", {"start": v(82.19, -42.88) * mm, "end": v(82.33, -42.91) * mm});
            skLineSegment(sketch, "E2333", {"start": v(82.33, -42.91) * mm, "end": v(82.47, -42.94) * mm});
            skLineSegment(sketch, "E2334", {"start": v(82.47, -42.94) * mm, "end": v(82.62, -42.96) * mm});
            skLineSegment(sketch, "E2335", {"start": v(82.62, -42.96) * mm, "end": v(82.77, -42.99) * mm});
            skLineSegment(sketch, "E2336", {"start": v(82.77, -42.99) * mm, "end": v(82.93, -43.01) * mm});
            skLineSegment(sketch, "E2337", {"start": v(82.93, -43.01) * mm, "end": v(83.08, -43.04) * mm});
            skLineSegment(sketch, "E2338", {"start": v(83.08, -43.04) * mm, "end": v(83.24, -43.06) * mm});
            skLineSegment(sketch, "E2339", {"start": v(83.24, -43.06) * mm, "end": v(83.4, -43.08) * mm});
            skLineSegment(sketch, "E2340", {"start": v(83.4, -43.08) * mm, "end": v(83.57, -43.1) * mm});
            skLineSegment(sketch, "E2341", {"start": v(83.57, -43.1) * mm, "end": v(83.73, -43.13) * mm});
            skLineSegment(sketch, "E2342", {"start": v(83.73, -43.13) * mm, "end": v(83.9, -43.15) * mm});
            skLineSegment(sketch, "E2343", {"start": v(83.9, -43.15) * mm, "end": v(84.07, -43.17) * mm});
            skLineSegment(sketch, "E2344", {"start": v(84.07, -43.17) * mm, "end": v(84.25, -43.19) * mm});
            skLineSegment(sketch, "E2345", {"start": v(84.25, -43.19) * mm, "end": v(84.42, -43.2) * mm});
            skLineSegment(sketch, "E2346", {"start": v(84.42, -43.2) * mm, "end": v(84.6, -43.23) * mm});
            skLineSegment(sketch, "E2347", {"start": v(84.6, -43.23) * mm, "end": v(84.79, -43.25) * mm});
            skLineSegment(sketch, "E2348", {"start": v(84.79, -43.25) * mm, "end": v(84.97, -43.26) * mm});
            skLineSegment(sketch, "E2349", {"start": v(84.97, -43.26) * mm, "end": v(85.16, -43.28) * mm});
            skLineSegment(sketch, "E2350", {"start": v(85.16, -43.28) * mm, "end": v(85.35, -43.3) * mm});
            skLineSegment(sketch, "E2351", {"start": v(85.35, -43.3) * mm, "end": v(85.54, -43.31) * mm});
            skLineSegment(sketch, "E2352", {"start": v(85.54, -43.31) * mm, "end": v(85.73, -43.33) * mm});
            skLineSegment(sketch, "E2353", {"start": v(85.73, -43.33) * mm, "end": v(85.93, -43.34) * mm});
            skLineSegment(sketch, "E2354", {"start": v(85.93, -43.34) * mm, "end": v(86.13, -43.35) * mm});
            skLineSegment(sketch, "E2355", {"start": v(86.13, -43.35) * mm, "end": v(86.33, -43.36) * mm});
            skLineSegment(sketch, "E2356", {"start": v(86.33, -43.36) * mm, "end": v(86.54, -43.38) * mm});
            skLineSegment(sketch, "E2357", {"start": v(86.54, -43.38) * mm, "end": v(86.74, -43.39) * mm});
            skLineSegment(sketch, "E2358", {"start": v(86.74, -43.39) * mm, "end": v(86.92, -43.38) * mm});
            skLineSegment(sketch, "E2359", {"start": v(86.92, -43.38) * mm, "end": v(87.86, -41.44) * mm});
            skLineSegment(sketch, "E2360", {"start": v(87.86, -41.44) * mm, "end": v(87.76, -41.3) * mm});
            skLineSegment(sketch, "E2361", {"start": v(87.76, -41.3) * mm, "end": v(87.62, -41.14) * mm});
            skLineSegment(sketch, "E2362", {"start": v(87.62, -41.14) * mm, "end": v(87.48, -40.99) * mm});
            skLineSegment(sketch, "E2363", {"start": v(87.48, -40.99) * mm, "end": v(87.35, -40.84) * mm});
            skLineSegment(sketch, "E2364", {"start": v(87.35, -40.84) * mm, "end": v(87.22, -40.69) * mm});
            skLineSegment(sketch, "E2365", {"start": v(87.22, -40.69) * mm, "end": v(87.08, -40.54) * mm});
            skLineSegment(sketch, "E2366", {"start": v(87.08, -40.54) * mm, "end": v(86.95, -40.4) * mm});
            skLineSegment(sketch, "E2367", {"start": v(86.95, -40.4) * mm, "end": v(86.82, -40.26) * mm});
            skLineSegment(sketch, "E2368", {"start": v(86.82, -40.26) * mm, "end": v(86.7, -40.12) * mm});
            skLineSegment(sketch, "E2369", {"start": v(86.7, -40.12) * mm, "end": v(86.56, -39.98) * mm});
            skLineSegment(sketch, "E2370", {"start": v(86.56, -39.98) * mm, "end": v(86.44, -39.85) * mm});
            skLineSegment(sketch, "E2371", {"start": v(86.44, -39.85) * mm, "end": v(86.3, -39.71) * mm});
            skLineSegment(sketch, "E2372", {"start": v(86.3, -39.71) * mm, "end": v(86.18, -39.59) * mm});
            skLineSegment(sketch, "E2373", {"start": v(86.18, -39.59) * mm, "end": v(86.06, -39.46) * mm});
            skLineSegment(sketch, "E2374", {"start": v(86.06, -39.46) * mm, "end": v(85.93, -39.34) * mm});
            skLineSegment(sketch, "E2375", {"start": v(85.93, -39.34) * mm, "end": v(85.81, -39.21) * mm});
            skLineSegment(sketch, "E2376", {"start": v(85.81, -39.21) * mm, "end": v(85.7, -39.1) * mm});
            skLineSegment(sketch, "E2377", {"start": v(85.7, -39.1) * mm, "end": v(85.57, -38.98) * mm});
            skLineSegment(sketch, "E2378", {"start": v(85.57, -38.98) * mm, "end": v(85.45, -38.86) * mm});
            skLineSegment(sketch, "E2379", {"start": v(85.45, -38.86) * mm, "end": v(85.33, -38.75) * mm});
            skLineSegment(sketch, "E2380", {"start": v(85.33, -38.75) * mm, "end": v(85.22, -38.64) * mm});
            skLineSegment(sketch, "E2381", {"start": v(85.22, -38.64) * mm, "end": v(85.1, -38.53) * mm});
            skLineSegment(sketch, "E2382", {"start": v(85.1, -38.53) * mm, "end": v(84.99, -38.43) * mm});
            skLineSegment(sketch, "E2383", {"start": v(84.99, -38.43) * mm, "end": v(84.87, -38.32) * mm});
            skLineSegment(sketch, "E2384", {"start": v(84.87, -38.32) * mm, "end": v(84.76, -38.22) * mm});
            skLineSegment(sketch, "E2385", {"start": v(84.76, -38.22) * mm, "end": v(84.65, -38.12) * mm});
            skLineSegment(sketch, "E2386", {"start": v(84.65, -38.12) * mm, "end": v(84.54, -38.03) * mm});
            skLineSegment(sketch, "E2387", {"start": v(84.54, -38.03) * mm, "end": v(84.44, -37.93) * mm});
            skLineSegment(sketch, "E2388", {"start": v(84.44, -37.93) * mm, "end": v(84.33, -37.84) * mm});
            skLineSegment(sketch, "E2389", {"start": v(84.33, -37.84) * mm, "end": v(84.22, -37.75) * mm});
            skLineSegment(sketch, "E2390", {"start": v(84.22, -37.75) * mm, "end": v(84.12, -37.66) * mm});
            skLineSegment(sketch, "E2391", {"start": v(84.12, -37.66) * mm, "end": v(84.02, -37.58) * mm});
            skLineSegment(sketch, "E2392", {"start": v(84.02, -37.58) * mm, "end": v(83.92, -37.5) * mm});
            skLineSegment(sketch, "E2393", {"start": v(83.92, -37.5) * mm, "end": v(83.82, -37.41) * mm});
            skLineSegment(sketch, "E2394", {"start": v(83.82, -37.41) * mm, "end": v(83.72, -37.34) * mm});
            skLineSegment(sketch, "E2395", {"start": v(83.72, -37.34) * mm, "end": v(83.63, -37.26) * mm});
            skLineSegment(sketch, "E2396", {"start": v(83.63, -37.26) * mm, "end": v(83.53, -37.18) * mm});
            skLineSegment(sketch, "E2397", {"start": v(83.53, -37.18) * mm, "end": v(83.44, -37.11) * mm});
            skLineSegment(sketch, "E2398", {"start": v(83.44, -37.11) * mm, "end": v(83.35, -37.04) * mm});
            skLineSegment(sketch, "E2399", {"start": v(83.35, -37.04) * mm, "end": v(83.33, -36.56) * mm});
            skLineSegment(sketch, "E2400", {"start": v(83.33, -36.56) * mm, "end": v(84, -35.01) * mm});
            skLineSegment(sketch, "E2401", {"start": v(84, -35.01) * mm, "end": v(84.35, -34.7) * mm});
            skLineSegment(sketch, "E2402", {"start": v(84.35, -34.7) * mm, "end": v(84.46, -34.71) * mm});
            skLineSegment(sketch, "E2403", {"start": v(84.46, -34.71) * mm, "end": v(84.58, -34.73) * mm});
            skLineSegment(sketch, "E2404", {"start": v(84.58, -34.73) * mm, "end": v(84.7, -34.75) * mm});
            skLineSegment(sketch, "E2405", {"start": v(84.7, -34.75) * mm, "end": v(84.82, -34.76) * mm});
            skLineSegment(sketch, "E2406", {"start": v(84.82, -34.76) * mm, "end": v(84.95, -34.78) * mm});
            skLineSegment(sketch, "E2407", {"start": v(84.95, -34.78) * mm, "end": v(85.07, -34.8) * mm});
            skLineSegment(sketch, "E2408", {"start": v(85.07, -34.8) * mm, "end": v(85.2, -34.8) * mm});
            skLineSegment(sketch, "E2409", {"start": v(85.2, -34.8) * mm, "end": v(85.34, -34.82) * mm});
            skLineSegment(sketch, "E2410", {"start": v(85.34, -34.82) * mm, "end": v(85.47, -34.84) * mm});
            skLineSegment(sketch, "E2411", {"start": v(85.47, -34.84) * mm, "end": v(85.6, -34.85) * mm});
            skLineSegment(sketch, "E2412", {"start": v(85.6, -34.85) * mm, "end": v(85.75, -34.87) * mm});
            skLineSegment(sketch, "E2413", {"start": v(85.75, -34.87) * mm, "end": v(85.9, -34.88) * mm});
            skLineSegment(sketch, "E2414", {"start": v(85.9, -34.88) * mm, "end": v(86.04, -34.9) * mm});
            skLineSegment(sketch, "E2415", {"start": v(86.04, -34.9) * mm, "end": v(86.18, -34.9) * mm});
            skLineSegment(sketch, "E2416", {"start": v(86.18, -34.9) * mm, "end": v(86.33, -34.91) * mm});
            skLineSegment(sketch, "E2417", {"start": v(86.33, -34.91) * mm, "end": v(86.49, -34.92) * mm});
            skLineSegment(sketch, "E2418", {"start": v(86.49, -34.92) * mm, "end": v(86.64, -34.93) * mm});
            skLineSegment(sketch, "E2419", {"start": v(86.64, -34.93) * mm, "end": v(86.8, -34.94) * mm});
            skLineSegment(sketch, "E2420", {"start": v(86.8, -34.94) * mm, "end": v(86.96, -34.95) * mm});
            skLineSegment(sketch, "E2421", {"start": v(86.96, -34.95) * mm, "end": v(87.12, -34.96) * mm});
            skLineSegment(sketch, "E2422", {"start": v(87.12, -34.96) * mm, "end": v(87.29, -34.97) * mm});
            skLineSegment(sketch, "E2423", {"start": v(87.29, -34.97) * mm, "end": v(87.45, -34.97) * mm});
            skLineSegment(sketch, "E2424", {"start": v(87.45, -34.97) * mm, "end": v(87.62, -34.98) * mm});
            skLineSegment(sketch, "E2425", {"start": v(87.62, -34.98) * mm, "end": v(87.8, -34.98) * mm});
            skLineSegment(sketch, "E2426", {"start": v(87.8, -34.98) * mm, "end": v(87.97, -34.99) * mm});
            skLineSegment(sketch, "E2427", {"start": v(87.97, -34.99) * mm, "end": v(88.15, -34.99) * mm});
            skLineSegment(sketch, "E2428", {"start": v(88.15, -34.99) * mm, "end": v(88.33, -35) * mm});
            skLineSegment(sketch, "E2429", {"start": v(88.33, -35) * mm, "end": v(88.51, -35) * mm});
            skLineSegment(sketch, "E2430", {"start": v(88.51, -35) * mm, "end": v(88.7, -35) * mm});
            skLineSegment(sketch, "E2431", {"start": v(88.7, -35) * mm, "end": v(88.88, -35) * mm});
            skLineSegment(sketch, "E2432", {"start": v(88.88, -35) * mm, "end": v(89.08, -34.99) * mm});
            skLineSegment(sketch, "E2433", {"start": v(89.08, -34.99) * mm, "end": v(89.27, -34.99) * mm});
            skLineSegment(sketch, "E2434", {"start": v(89.27, -34.99) * mm, "end": v(89.46, -34.98) * mm});
            skLineSegment(sketch, "E2435", {"start": v(89.46, -34.98) * mm, "end": v(89.66, -34.98) * mm});
            skLineSegment(sketch, "E2436", {"start": v(89.66, -34.98) * mm, "end": v(89.86, -34.97) * mm});
            skLineSegment(sketch, "E2437", {"start": v(89.86, -34.97) * mm, "end": v(90.06, -34.96) * mm});
            skLineSegment(sketch, "E2438", {"start": v(90.06, -34.96) * mm, "end": v(90.27, -34.95) * mm});
            skLineSegment(sketch, "E2439", {"start": v(90.27, -34.95) * mm, "end": v(90.47, -34.94) * mm});
            skLineSegment(sketch, "E2440", {"start": v(90.47, -34.94) * mm, "end": v(90.65, -34.92) * mm});
            skLineSegment(sketch, "E2441", {"start": v(90.65, -34.92) * mm, "end": v(91.4, -32.9) * mm});
            skLineSegment(sketch, "E2442", {"start": v(91.4, -32.9) * mm, "end": v(91.28, -32.77) * mm});
            skLineSegment(sketch, "E2443", {"start": v(91.28, -32.77) * mm, "end": v(91.13, -32.63) * mm});
            skLineSegment(sketch, "E2444", {"start": v(91.13, -32.63) * mm, "end": v(90.98, -32.49) * mm});
            skLineSegment(sketch, "E2445", {"start": v(90.98, -32.49) * mm, "end": v(90.84, -32.35) * mm});
            skLineSegment(sketch, "E2446", {"start": v(90.84, -32.35) * mm, "end": v(90.69, -32.21) * mm});
            skLineSegment(sketch, "E2447", {"start": v(90.69, -32.21) * mm, "end": v(90.54, -32.08) * mm});
            skLineSegment(sketch, "E2448", {"start": v(90.54, -32.08) * mm, "end": v(90.4, -31.95) * mm});
            skLineSegment(sketch, "E2449", {"start": v(90.4, -31.95) * mm, "end": v(90.26, -31.82) * mm});
            skLineSegment(sketch, "E2450", {"start": v(90.26, -31.82) * mm, "end": v(90.11, -31.7) * mm});
            skLineSegment(sketch, "E2451", {"start": v(90.11, -31.7) * mm, "end": v(89.97, -31.57) * mm});
            skLineSegment(sketch, "E2452", {"start": v(89.97, -31.57) * mm, "end": v(89.83, -31.45) * mm});
            skLineSegment(sketch, "E2453", {"start": v(89.83, -31.45) * mm, "end": v(89.7, -31.33) * mm});
            skLineSegment(sketch, "E2454", {"start": v(89.7, -31.33) * mm, "end": v(89.56, -31.21) * mm});
            skLineSegment(sketch, "E2455", {"start": v(89.56, -31.21) * mm, "end": v(89.42, -31.1) * mm});
            skLineSegment(sketch, "E2456", {"start": v(89.42, -31.1) * mm, "end": v(89.28, -30.99) * mm});
            skLineSegment(sketch, "E2457", {"start": v(89.28, -30.99) * mm, "end": v(89.15, -30.88) * mm});
            skLineSegment(sketch, "E2458", {"start": v(89.15, -30.88) * mm, "end": v(89.02, -30.77) * mm});
            skLineSegment(sketch, "E2459", {"start": v(89.02, -30.77) * mm, "end": v(88.89, -30.67) * mm});
            skLineSegment(sketch, "E2460", {"start": v(88.89, -30.67) * mm, "end": v(88.76, -30.56) * mm});
            skLineSegment(sketch, "E2461", {"start": v(88.76, -30.56) * mm, "end": v(88.63, -30.46) * mm});
            skLineSegment(sketch, "E2462", {"start": v(88.63, -30.46) * mm, "end": v(88.5, -30.36) * mm});
            skLineSegment(sketch, "E2463", {"start": v(88.5, -30.36) * mm, "end": v(88.38, -30.27) * mm});
            skLineSegment(sketch, "E2464", {"start": v(88.38, -30.27) * mm, "end": v(88.25, -30.17) * mm});
            skLineSegment(sketch, "E2465", {"start": v(88.25, -30.17) * mm, "end": v(88.13, -30.08) * mm});
            skLineSegment(sketch, "E2466", {"start": v(88.13, -30.08) * mm, "end": v(88.01, -30) * mm});
            skLineSegment(sketch, "E2467", {"start": v(88.01, -30) * mm, "end": v(87.9, -29.9) * mm});
            skLineSegment(sketch, "E2468", {"start": v(87.9, -29.9) * mm, "end": v(87.78, -29.82) * mm});
            skLineSegment(sketch, "E2469", {"start": v(87.78, -29.82) * mm, "end": v(87.66, -29.74) * mm});
            skLineSegment(sketch, "E2470", {"start": v(87.66, -29.74) * mm, "end": v(87.54, -29.65) * mm});
            skLineSegment(sketch, "E2471", {"start": v(87.54, -29.65) * mm, "end": v(87.43, -29.58) * mm});
            skLineSegment(sketch, "E2472", {"start": v(87.43, -29.58) * mm, "end": v(87.32, -29.5) * mm});
            skLineSegment(sketch, "E2473", {"start": v(87.32, -29.5) * mm, "end": v(87.21, -29.42) * mm});
            skLineSegment(sketch, "E2474", {"start": v(87.21, -29.42) * mm, "end": v(87.1, -29.35) * mm});
            skLineSegment(sketch, "E2475", {"start": v(87.1, -29.35) * mm, "end": v(87, -29.28) * mm});
            skLineSegment(sketch, "E2476", {"start": v(87, -29.28) * mm, "end": v(86.9, -29.2) * mm});
            skLineSegment(sketch, "E2477", {"start": v(86.9, -29.2) * mm, "end": v(86.79, -29.14) * mm});
            skLineSegment(sketch, "E2478", {"start": v(86.79, -29.14) * mm, "end": v(86.69, -29.07) * mm});
            skLineSegment(sketch, "E2479", {"start": v(86.69, -29.07) * mm, "end": v(86.59, -29.01) * mm});
            skLineSegment(sketch, "E2480", {"start": v(86.59, -29.01) * mm, "end": v(86.5, -28.95) * mm});
            skLineSegment(sketch, "E2481", {"start": v(86.5, -28.95) * mm, "end": v(86.43, -28.48) * mm});
            skLineSegment(sketch, "E2482", {"start": v(86.43, -28.48) * mm, "end": v(86.94, -26.87) * mm});
            skLineSegment(sketch, "E2483", {"start": v(86.94, -26.87) * mm, "end": v(87.27, -26.52) * mm});
            skLineSegment(sketch, "E2484", {"start": v(87.27, -26.52) * mm, "end": v(87.38, -26.53) * mm});
            skLineSegment(sketch, "E2485", {"start": v(87.38, -26.53) * mm, "end": v(87.5, -26.53) * mm});
            skLineSegment(sketch, "E2486", {"start": v(87.5, -26.53) * mm, "end": v(87.62, -26.54) * mm});
            skLineSegment(sketch, "E2487", {"start": v(87.62, -26.54) * mm, "end": v(87.74, -26.54) * mm});
            skLineSegment(sketch, "E2488", {"start": v(87.74, -26.54) * mm, "end": v(87.87, -26.55) * mm});
            skLineSegment(sketch, "E2489", {"start": v(87.87, -26.55) * mm, "end": v(88, -26.55) * mm});
            skLineSegment(sketch, "E2490", {"start": v(88, -26.55) * mm, "end": v(88.13, -26.55) * mm});
            skLineSegment(sketch, "E2491", {"start": v(88.13, -26.55) * mm, "end": v(88.26, -26.55) * mm});
            skLineSegment(sketch, "E2492", {"start": v(88.26, -26.55) * mm, "end": v(88.4, -26.56) * mm});
            skLineSegment(sketch, "E2493", {"start": v(88.4, -26.56) * mm, "end": v(88.53, -26.56) * mm});
            skLineSegment(sketch, "E2494", {"start": v(88.53, -26.56) * mm, "end": v(88.67, -26.56) * mm});
            skLineSegment(sketch, "E2495", {"start": v(88.67, -26.56) * mm, "end": v(88.82, -26.56) * mm});
            skLineSegment(sketch, "E2496", {"start": v(88.82, -26.56) * mm, "end": v(88.96, -26.55) * mm});
            skLineSegment(sketch, "E2497", {"start": v(88.96, -26.55) * mm, "end": v(89.11, -26.55) * mm});
            skLineSegment(sketch, "E2498", {"start": v(89.11, -26.55) * mm, "end": v(89.26, -26.55) * mm});
            skLineSegment(sketch, "E2499", {"start": v(89.26, -26.55) * mm, "end": v(89.41, -26.55) * mm});
            skLineSegment(sketch, "E2500", {"start": v(89.41, -26.55) * mm, "end": v(89.57, -26.54) * mm});
            skLineSegment(sketch, "E2501", {"start": v(89.57, -26.54) * mm, "end": v(89.73, -26.53) * mm});
            skLineSegment(sketch, "E2502", {"start": v(89.73, -26.53) * mm, "end": v(89.89, -26.53) * mm});
            skLineSegment(sketch, "E2503", {"start": v(89.89, -26.53) * mm, "end": v(90.05, -26.52) * mm});
            skLineSegment(sketch, "E2504", {"start": v(90.05, -26.52) * mm, "end": v(90.21, -26.51) * mm});
            skLineSegment(sketch, "E2505", {"start": v(90.21, -26.51) * mm, "end": v(90.38, -26.5) * mm});
            skLineSegment(sketch, "E2506", {"start": v(90.38, -26.5) * mm, "end": v(90.55, -26.5) * mm});
            skLineSegment(sketch, "E2507", {"start": v(90.55, -26.5) * mm, "end": v(90.72, -26.48) * mm});
            skLineSegment(sketch, "E2508", {"start": v(90.72, -26.48) * mm, "end": v(90.9, -26.47) * mm});
            skLineSegment(sketch, "E2509", {"start": v(90.9, -26.47) * mm, "end": v(91.08, -26.45) * mm});
            skLineSegment(sketch, "E2510", {"start": v(91.08, -26.45) * mm, "end": v(91.26, -26.44) * mm});
            skLineSegment(sketch, "E2511", {"start": v(91.26, -26.44) * mm, "end": v(91.44, -26.42) * mm});
            skLineSegment(sketch, "E2512", {"start": v(91.44, -26.42) * mm, "end": v(91.62, -26.4) * mm});
            skLineSegment(sketch, "E2513", {"start": v(91.62, -26.4) * mm, "end": v(91.8, -26.38) * mm});
            skLineSegment(sketch, "E2514", {"start": v(91.8, -26.38) * mm, "end": v(92, -26.36) * mm});
            skLineSegment(sketch, "E2515", {"start": v(92, -26.36) * mm, "end": v(92.19, -26.34) * mm});
            skLineSegment(sketch, "E2516", {"start": v(92.19, -26.34) * mm, "end": v(92.38, -26.32) * mm});
            skLineSegment(sketch, "E2517", {"start": v(92.38, -26.32) * mm, "end": v(92.58, -26.3) * mm});
            skLineSegment(sketch, "E2518", {"start": v(92.58, -26.3) * mm, "end": v(92.78, -26.27) * mm});
            skLineSegment(sketch, "E2519", {"start": v(92.78, -26.27) * mm, "end": v(92.98, -26.24) * mm});
            skLineSegment(sketch, "E2520", {"start": v(92.98, -26.24) * mm, "end": v(93.18, -26.21) * mm});
            skLineSegment(sketch, "E2521", {"start": v(93.18, -26.21) * mm, "end": v(93.39, -26.19) * mm});
            skLineSegment(sketch, "E2522", {"start": v(93.39, -26.19) * mm, "end": v(93.56, -26.14) * mm});
            skLineSegment(sketch, "E2523", {"start": v(93.56, -26.14) * mm, "end": v(94.11, -24.07) * mm});
            skLineSegment(sketch, "E2524", {"start": v(94.11, -24.07) * mm, "end": v(93.99, -23.94) * mm});
            skLineSegment(sketch, "E2525", {"start": v(93.99, -23.94) * mm, "end": v(93.82, -23.82) * mm});
            skLineSegment(sketch, "E2526", {"start": v(93.82, -23.82) * mm, "end": v(93.66, -23.7) * mm});
            skLineSegment(sketch, "E2527", {"start": v(93.66, -23.7) * mm, "end": v(93.5, -23.57) * mm});
            skLineSegment(sketch, "E2528", {"start": v(93.5, -23.57) * mm, "end": v(93.34, -23.45) * mm});
            skLineSegment(sketch, "E2529", {"start": v(93.34, -23.45) * mm, "end": v(93.18, -23.33) * mm});
            skLineSegment(sketch, "E2530", {"start": v(93.18, -23.33) * mm, "end": v(93.03, -23.21) * mm});
            skLineSegment(sketch, "E2531", {"start": v(93.03, -23.21) * mm, "end": v(92.87, -23.1) * mm});
            skLineSegment(sketch, "E2532", {"start": v(92.87, -23.1) * mm, "end": v(92.72, -22.99) * mm});
            skLineSegment(sketch, "E2533", {"start": v(92.72, -22.99) * mm, "end": v(92.57, -22.88) * mm});
            skLineSegment(sketch, "E2534", {"start": v(92.57, -22.88) * mm, "end": v(92.41, -22.77) * mm});
            skLineSegment(sketch, "E2535", {"start": v(92.41, -22.77) * mm, "end": v(92.27, -22.66) * mm});
            skLineSegment(sketch, "E2536", {"start": v(92.27, -22.66) * mm, "end": v(92.12, -22.56) * mm});
            skLineSegment(sketch, "E2537", {"start": v(92.12, -22.56) * mm, "end": v(91.97, -22.46) * mm});
            skLineSegment(sketch, "E2538", {"start": v(91.97, -22.46) * mm, "end": v(91.83, -22.36) * mm});
            skLineSegment(sketch, "E2539", {"start": v(91.83, -22.36) * mm, "end": v(91.68, -22.26) * mm});
            skLineSegment(sketch, "E2540", {"start": v(91.68, -22.26) * mm, "end": v(91.54, -22.17) * mm});
            skLineSegment(sketch, "E2541", {"start": v(91.54, -22.17) * mm, "end": v(91.4, -22.08) * mm});
            skLineSegment(sketch, "E2542", {"start": v(91.4, -22.08) * mm, "end": v(91.26, -21.99) * mm});
            skLineSegment(sketch, "E2543", {"start": v(91.26, -21.99) * mm, "end": v(91.12, -21.9) * mm});
            skLineSegment(sketch, "E2544", {"start": v(91.12, -21.9) * mm, "end": v(90.99, -21.81) * mm});
            skLineSegment(sketch, "E2545", {"start": v(90.99, -21.81) * mm, "end": v(90.86, -21.73) * mm});
            skLineSegment(sketch, "E2546", {"start": v(90.86, -21.73) * mm, "end": v(90.72, -21.65) * mm});
            skLineSegment(sketch, "E2547", {"start": v(90.72, -21.65) * mm, "end": v(90.6, -21.57) * mm});
            skLineSegment(sketch, "E2548", {"start": v(90.6, -21.57) * mm, "end": v(90.46, -21.5) * mm});
            skLineSegment(sketch, "E2549", {"start": v(90.46, -21.5) * mm, "end": v(90.34, -21.42) * mm});
            skLineSegment(sketch, "E2550", {"start": v(90.34, -21.42) * mm, "end": v(90.21, -21.34) * mm});
            skLineSegment(sketch, "E2551", {"start": v(90.21, -21.34) * mm, "end": v(90.09, -21.27) * mm});
            skLineSegment(sketch, "E2552", {"start": v(90.09, -21.27) * mm, "end": v(89.97, -21.2) * mm});
            skLineSegment(sketch, "E2553", {"start": v(89.97, -21.2) * mm, "end": v(89.85, -21.13) * mm});
            skLineSegment(sketch, "E2554", {"start": v(89.85, -21.13) * mm, "end": v(89.73, -21.06) * mm});
            skLineSegment(sketch, "E2555", {"start": v(89.73, -21.06) * mm, "end": v(89.61, -21) * mm});
            skLineSegment(sketch, "E2556", {"start": v(89.61, -21) * mm, "end": v(89.5, -20.94) * mm});
            skLineSegment(sketch, "E2557", {"start": v(89.5, -20.94) * mm, "end": v(89.39, -20.88) * mm});
            skLineSegment(sketch, "E2558", {"start": v(89.39, -20.88) * mm, "end": v(89.27, -20.82) * mm});
            skLineSegment(sketch, "E2559", {"start": v(89.27, -20.82) * mm, "end": v(89.17, -20.76) * mm});
            skLineSegment(sketch, "E2560", {"start": v(89.17, -20.76) * mm, "end": v(89.06, -20.7) * mm});
            skLineSegment(sketch, "E2561", {"start": v(89.06, -20.7) * mm, "end": v(88.95, -20.65) * mm});
            skLineSegment(sketch, "E2562", {"start": v(88.95, -20.65) * mm, "end": v(88.85, -20.6) * mm});
            skLineSegment(sketch, "E2563", {"start": v(88.85, -20.6) * mm, "end": v(88.74, -20.13) * mm});
            skLineSegment(sketch, "E2564", {"start": v(88.74, -20.13) * mm, "end": v(89.1, -18.48) * mm});
            skLineSegment(sketch, "E2565", {"start": v(89.1, -18.48) * mm, "end": v(89.4, -18.1) * mm});
            skLineSegment(sketch, "E2566", {"start": v(89.4, -18.1) * mm, "end": v(89.5, -18.1) * mm});
            skLineSegment(sketch, "E2567", {"start": v(89.5, -18.1) * mm, "end": v(89.62, -18.1) * mm});
            skLineSegment(sketch, "E2568", {"start": v(89.62, -18.1) * mm, "end": v(89.75, -18.09) * mm});
            skLineSegment(sketch, "E2569", {"start": v(89.75, -18.09) * mm, "end": v(89.87, -18.08) * mm});
            skLineSegment(sketch, "E2570", {"start": v(89.87, -18.08) * mm, "end": v(90, -18.07) * mm});
            skLineSegment(sketch, "E2571", {"start": v(90, -18.07) * mm, "end": v(90.12, -18.07) * mm});
            skLineSegment(sketch, "E2572", {"start": v(90.12, -18.07) * mm, "end": v(90.25, -18.06) * mm});
            skLineSegment(sketch, "E2573", {"start": v(90.25, -18.06) * mm, "end": v(90.38, -18.05) * mm});
            skLineSegment(sketch, "E2574", {"start": v(90.38, -18.05) * mm, "end": v(90.52, -18.03) * mm});
            skLineSegment(sketch, "E2575", {"start": v(90.52, -18.03) * mm, "end": v(90.66, -18.02) * mm});
            skLineSegment(sketch, "E2576", {"start": v(90.66, -18.02) * mm, "end": v(90.8, -18) * mm});
            skLineSegment(sketch, "E2577", {"start": v(90.8, -18) * mm, "end": v(90.94, -18) * mm});
            skLineSegment(sketch, "E2578", {"start": v(90.94, -18) * mm, "end": v(91.08, -17.98) * mm});
            skLineSegment(sketch, "E2579", {"start": v(91.08, -17.98) * mm, "end": v(91.23, -17.96) * mm});
            skLineSegment(sketch, "E2580", {"start": v(91.23, -17.96) * mm, "end": v(91.38, -17.94) * mm});
            skLineSegment(sketch, "E2581", {"start": v(91.38, -17.94) * mm, "end": v(91.53, -17.93) * mm});
            skLineSegment(sketch, "E2582", {"start": v(91.53, -17.93) * mm, "end": v(91.69, -17.9) * mm});
            skLineSegment(sketch, "E2583", {"start": v(91.69, -17.9) * mm, "end": v(91.84, -17.89) * mm});
            skLineSegment(sketch, "E2584", {"start": v(91.84, -17.89) * mm, "end": v(92, -17.86) * mm});
            skLineSegment(sketch, "E2585", {"start": v(92, -17.86) * mm, "end": v(92.16, -17.84) * mm});
            skLineSegment(sketch, "E2586", {"start": v(92.16, -17.84) * mm, "end": v(92.33, -17.82) * mm});
            skLineSegment(sketch, "E2587", {"start": v(92.33, -17.82) * mm, "end": v(92.5, -17.79) * mm});
            skLineSegment(sketch, "E2588", {"start": v(92.5, -17.79) * mm, "end": v(92.66, -17.76) * mm});
            skLineSegment(sketch, "E2589", {"start": v(92.66, -17.76) * mm, "end": v(92.83, -17.73) * mm});
            skLineSegment(sketch, "E2590", {"start": v(92.83, -17.73) * mm, "end": v(93, -17.7) * mm});
            skLineSegment(sketch, "E2591", {"start": v(93, -17.7) * mm, "end": v(93.18, -17.67) * mm});
            skLineSegment(sketch, "E2592", {"start": v(93.18, -17.67) * mm, "end": v(93.36, -17.64) * mm});
            skLineSegment(sketch, "E2593", {"start": v(93.36, -17.64) * mm, "end": v(93.53, -17.6) * mm});
            skLineSegment(sketch, "E2594", {"start": v(93.53, -17.6) * mm, "end": v(93.72, -17.57) * mm});
            skLineSegment(sketch, "E2595", {"start": v(93.72, -17.57) * mm, "end": v(93.9, -17.54) * mm});
            skLineSegment(sketch, "E2596", {"start": v(93.9, -17.54) * mm, "end": v(94.09, -17.5) * mm});
            skLineSegment(sketch, "E2597", {"start": v(94.09, -17.5) * mm, "end": v(94.28, -17.46) * mm});
            skLineSegment(sketch, "E2598", {"start": v(94.28, -17.46) * mm, "end": v(94.47, -17.42) * mm});
            skLineSegment(sketch, "E2599", {"start": v(94.47, -17.42) * mm, "end": v(94.66, -17.38) * mm});
            skLineSegment(sketch, "E2600", {"start": v(94.66, -17.38) * mm, "end": v(94.85, -17.33) * mm});
            skLineSegment(sketch, "E2601", {"start": v(94.85, -17.33) * mm, "end": v(95.05, -17.29) * mm});
            skLineSegment(sketch, "E2602", {"start": v(95.05, -17.29) * mm, "end": v(95.25, -17.24) * mm});
            skLineSegment(sketch, "E2603", {"start": v(95.25, -17.24) * mm, "end": v(95.45, -17.19) * mm});
            skLineSegment(sketch, "E2604", {"start": v(95.45, -17.19) * mm, "end": v(95.62, -17.13) * mm});
            skLineSegment(sketch, "E2605", {"start": v(95.62, -17.13) * mm, "end": v(95.98, -15.01) * mm});
            skLineSegment(sketch, "E2606", {"start": v(95.98, -15.01) * mm, "end": v(95.84, -14.9) * mm});
            skLineSegment(sketch, "E2607", {"start": v(95.84, -14.9) * mm, "end": v(95.66, -14.79) * mm});
            skLineSegment(sketch, "E2608", {"start": v(95.66, -14.79) * mm, "end": v(95.49, -14.68) * mm});
            skLineSegment(sketch, "E2609", {"start": v(95.49, -14.68) * mm, "end": v(95.32, -14.57) * mm});
            skLineSegment(sketch, "E2610", {"start": v(95.32, -14.57) * mm, "end": v(95.15, -14.47) * mm});
            skLineSegment(sketch, "E2611", {"start": v(95.15, -14.47) * mm, "end": v(94.98, -14.36) * mm});
            skLineSegment(sketch, "E2612", {"start": v(94.98, -14.36) * mm, "end": v(94.81, -14.26) * mm});
            skLineSegment(sketch, "E2613", {"start": v(94.81, -14.26) * mm, "end": v(94.65, -14.16) * mm});
            skLineSegment(sketch, "E2614", {"start": v(94.65, -14.16) * mm, "end": v(94.48, -14.07) * mm});
            skLineSegment(sketch, "E2615", {"start": v(94.48, -14.07) * mm, "end": v(94.32, -13.97) * mm});
            skLineSegment(sketch, "E2616", {"start": v(94.32, -13.97) * mm, "end": v(94.16, -13.88) * mm});
            skLineSegment(sketch, "E2617", {"start": v(94.16, -13.88) * mm, "end": v(94, -13.8) * mm});
            skLineSegment(sketch, "E2618", {"start": v(94, -13.8) * mm, "end": v(93.84, -13.7) * mm});
            skLineSegment(sketch, "E2619", {"start": v(93.84, -13.7) * mm, "end": v(93.69, -13.62) * mm});
            skLineSegment(sketch, "E2620", {"start": v(93.69, -13.62) * mm, "end": v(93.54, -13.53) * mm});
            skLineSegment(sketch, "E2621", {"start": v(93.54, -13.53) * mm, "end": v(93.38, -13.45) * mm});
            skLineSegment(sketch, "E2622", {"start": v(93.38, -13.45) * mm, "end": v(93.23, -13.37) * mm});
            skLineSegment(sketch, "E2623", {"start": v(93.23, -13.37) * mm, "end": v(93.09, -13.3) * mm});
            skLineSegment(sketch, "E2624", {"start": v(93.09, -13.3) * mm, "end": v(92.94, -13.21) * mm});
            skLineSegment(sketch, "E2625", {"start": v(92.94, -13.21) * mm, "end": v(92.8, -13.14) * mm});
            skLineSegment(sketch, "E2626", {"start": v(92.8, -13.14) * mm, "end": v(92.65, -13.07) * mm});
            skLineSegment(sketch, "E2627", {"start": v(92.65, -13.07) * mm, "end": v(92.5, -13) * mm});
            skLineSegment(sketch, "E2628", {"start": v(92.5, -13) * mm, "end": v(92.37, -12.93) * mm});
            skLineSegment(sketch, "E2629", {"start": v(92.37, -12.93) * mm, "end": v(92.23, -12.86) * mm});
            skLineSegment(sketch, "E2630", {"start": v(92.23, -12.86) * mm, "end": v(92.1, -12.8) * mm});
            skLineSegment(sketch, "E2631", {"start": v(92.1, -12.8) * mm, "end": v(91.96, -12.73) * mm});
            skLineSegment(sketch, "E2632", {"start": v(91.96, -12.73) * mm, "end": v(91.83, -12.67) * mm});
            skLineSegment(sketch, "E2633", {"start": v(91.83, -12.67) * mm, "end": v(91.7, -12.6) * mm});
            skLineSegment(sketch, "E2634", {"start": v(91.7, -12.6) * mm, "end": v(91.57, -12.55) * mm});
            skLineSegment(sketch, "E2635", {"start": v(91.57, -12.55) * mm, "end": v(91.45, -12.5) * mm});
            skLineSegment(sketch, "E2636", {"start": v(91.45, -12.5) * mm, "end": v(91.32, -12.44) * mm});
            skLineSegment(sketch, "E2637", {"start": v(91.32, -12.44) * mm, "end": v(91.2, -12.39) * mm});
            skLineSegment(sketch, "E2638", {"start": v(91.2, -12.39) * mm, "end": v(91.08, -12.33) * mm});
            skLineSegment(sketch, "E2639", {"start": v(91.08, -12.33) * mm, "end": v(90.96, -12.28) * mm});
            skLineSegment(sketch, "E2640", {"start": v(90.96, -12.28) * mm, "end": v(90.85, -12.24) * mm});
            skLineSegment(sketch, "E2641", {"start": v(90.85, -12.24) * mm, "end": v(90.74, -12.19) * mm});
            skLineSegment(sketch, "E2642", {"start": v(90.74, -12.19) * mm, "end": v(90.62, -12.14) * mm});
            skLineSegment(sketch, "E2643", {"start": v(90.62, -12.14) * mm, "end": v(90.51, -12.1) * mm});
            skLineSegment(sketch, "E2644", {"start": v(90.51, -12.1) * mm, "end": v(90.4, -12.06) * mm});
            skLineSegment(sketch, "E2645", {"start": v(90.4, -12.06) * mm, "end": v(90.26, -11.6) * mm});
            skLineSegment(sketch, "E2646", {"start": v(90.26, -11.6) * mm, "end": v(90.46, -9.93) * mm});
            skLineSegment(sketch, "E2647", {"start": v(90.46, -9.93) * mm, "end": v(90.7, -9.53) * mm});
            skLineSegment(sketch, "E2648", {"start": v(90.7, -9.53) * mm, "end": v(90.82, -9.51) * mm});
            skLineSegment(sketch, "E2649", {"start": v(90.82, -9.51) * mm, "end": v(90.94, -9.5) * mm});
            skLineSegment(sketch, "E2650", {"start": v(90.94, -9.5) * mm, "end": v(91.06, -9.48) * mm});
            skLineSegment(sketch, "E2651", {"start": v(91.06, -9.48) * mm, "end": v(91.18, -9.46) * mm});
            skLineSegment(sketch, "E2652", {"start": v(91.18, -9.46) * mm, "end": v(91.3, -9.44) * mm});
            skLineSegment(sketch, "E2653", {"start": v(91.3, -9.44) * mm, "end": v(91.43, -9.42) * mm});
            skLineSegment(sketch, "E2654", {"start": v(91.43, -9.42) * mm, "end": v(91.56, -9.4) * mm});
            skLineSegment(sketch, "E2655", {"start": v(91.56, -9.4) * mm, "end": v(91.7, -9.37) * mm});
            skLineSegment(sketch, "E2656", {"start": v(91.7, -9.37) * mm, "end": v(91.82, -9.35) * mm});
            skLineSegment(sketch, "E2657", {"start": v(91.82, -9.35) * mm, "end": v(91.96, -9.32) * mm});
            skLineSegment(sketch, "E2658", {"start": v(91.96, -9.32) * mm, "end": v(92.1, -9.3) * mm});
            skLineSegment(sketch, "E2659", {"start": v(92.1, -9.3) * mm, "end": v(92.24, -9.27) * mm});
            skLineSegment(sketch, "E2660", {"start": v(92.24, -9.27) * mm, "end": v(92.38, -9.24) * mm});
            skLineSegment(sketch, "E2661", {"start": v(92.38, -9.24) * mm, "end": v(92.53, -9.2) * mm});
            skLineSegment(sketch, "E2662", {"start": v(92.53, -9.2) * mm, "end": v(92.67, -9.18) * mm});
            skLineSegment(sketch, "E2663", {"start": v(92.67, -9.18) * mm, "end": v(92.82, -9.14) * mm});
            skLineSegment(sketch, "E2664", {"start": v(92.82, -9.14) * mm, "end": v(92.97, -9.1) * mm});
            skLineSegment(sketch, "E2665", {"start": v(92.97, -9.1) * mm, "end": v(93.13, -9.07) * mm});
            skLineSegment(sketch, "E2666", {"start": v(93.13, -9.07) * mm, "end": v(93.28, -9.04) * mm});
            skLineSegment(sketch, "E2667", {"start": v(93.28, -9.04) * mm, "end": v(93.44, -9) * mm});
            skLineSegment(sketch, "E2668", {"start": v(93.44, -9) * mm, "end": v(93.6, -8.96) * mm});
            skLineSegment(sketch, "E2669", {"start": v(93.6, -8.96) * mm, "end": v(93.76, -8.92) * mm});
            skLineSegment(sketch, "E2670", {"start": v(93.76, -8.92) * mm, "end": v(93.93, -8.87) * mm});
            skLineSegment(sketch, "E2671", {"start": v(93.93, -8.87) * mm, "end": v(94.1, -8.83) * mm});
            skLineSegment(sketch, "E2672", {"start": v(94.1, -8.83) * mm, "end": v(94.26, -8.78) * mm});
            skLineSegment(sketch, "E2673", {"start": v(94.26, -8.78) * mm, "end": v(94.44, -8.74) * mm});
            skLineSegment(sketch, "E2674", {"start": v(94.44, -8.74) * mm, "end": v(94.6, -8.69) * mm});
            skLineSegment(sketch, "E2675", {"start": v(94.6, -8.69) * mm, "end": v(94.79, -8.64) * mm});
            skLineSegment(sketch, "E2676", {"start": v(94.79, -8.64) * mm, "end": v(94.96, -8.59) * mm});
            skLineSegment(sketch, "E2677", {"start": v(94.96, -8.59) * mm, "end": v(95.14, -8.53) * mm});
            skLineSegment(sketch, "E2678", {"start": v(95.14, -8.53) * mm, "end": v(95.32, -8.48) * mm});
            skLineSegment(sketch, "E2679", {"start": v(95.32, -8.48) * mm, "end": v(95.5, -8.42) * mm});
            skLineSegment(sketch, "E2680", {"start": v(95.5, -8.42) * mm, "end": v(95.7, -8.36) * mm});
            skLineSegment(sketch, "E2681", {"start": v(95.7, -8.36) * mm, "end": v(95.88, -8.3) * mm});
            skLineSegment(sketch, "E2682", {"start": v(95.88, -8.3) * mm, "end": v(96.07, -8.24) * mm});
            skLineSegment(sketch, "E2683", {"start": v(96.07, -8.24) * mm, "end": v(96.26, -8.17) * mm});
            skLineSegment(sketch, "E2684", {"start": v(96.26, -8.17) * mm, "end": v(96.46, -8.1) * mm});
            skLineSegment(sketch, "E2685", {"start": v(96.46, -8.1) * mm, "end": v(96.65, -8.04) * mm});
            skLineSegment(sketch, "E2686", {"start": v(96.65, -8.04) * mm, "end": v(96.82, -7.97) * mm});
            skLineSegment(sketch, "E2687", {"start": v(96.82, -7.97) * mm, "end": v(96.97, -5.82) * mm});
            skLineSegment(sketch, "E2688", {"start": v(96.97, -5.82) * mm, "end": v(96.82, -5.72) * mm});
            skLineSegment(sketch, "E2689", {"start": v(96.82, -5.72) * mm, "end": v(96.63, -5.63) * mm});
            skLineSegment(sketch, "E2690", {"start": v(96.63, -5.63) * mm, "end": v(96.45, -5.54) * mm});
            skLineSegment(sketch, "E2691", {"start": v(96.45, -5.54) * mm, "end": v(96.27, -5.45) * mm});
            skLineSegment(sketch, "E2692", {"start": v(96.27, -5.45) * mm, "end": v(96.1, -5.36) * mm});
            skLineSegment(sketch, "E2693", {"start": v(96.1, -5.36) * mm, "end": v(95.91, -5.27) * mm});
            skLineSegment(sketch, "E2694", {"start": v(95.91, -5.27) * mm, "end": v(95.74, -5.19) * mm});
            skLineSegment(sketch, "E2695", {"start": v(95.74, -5.19) * mm, "end": v(95.56, -5.1) * mm});
            skLineSegment(sketch, "E2696", {"start": v(95.56, -5.1) * mm, "end": v(95.4, -5.02) * mm});
            skLineSegment(sketch, "E2697", {"start": v(95.4, -5.02) * mm, "end": v(95.22, -4.94) * mm});
            skLineSegment(sketch, "E2698", {"start": v(95.22, -4.94) * mm, "end": v(95.05, -4.87) * mm});
            skLineSegment(sketch, "E2699", {"start": v(95.05, -4.87) * mm, "end": v(94.89, -4.8) * mm});
            skLineSegment(sketch, "E2700", {"start": v(94.89, -4.8) * mm, "end": v(94.72, -4.72) * mm});
            skLineSegment(sketch, "E2701", {"start": v(94.72, -4.72) * mm, "end": v(94.56, -4.65) * mm});
            skLineSegment(sketch, "E2702", {"start": v(94.56, -4.65) * mm, "end": v(94.4, -4.58) * mm});
            skLineSegment(sketch, "E2703", {"start": v(94.4, -4.58) * mm, "end": v(94.24, -4.51) * mm});
            skLineSegment(sketch, "E2704", {"start": v(94.24, -4.51) * mm, "end": v(94.08, -4.45) * mm});
            skLineSegment(sketch, "E2705", {"start": v(94.08, -4.45) * mm, "end": v(93.93, -4.38) * mm});
            skLineSegment(sketch, "E2706", {"start": v(93.93, -4.38) * mm, "end": v(93.77, -4.32) * mm});
            skLineSegment(sketch, "E2707", {"start": v(93.77, -4.32) * mm, "end": v(93.62, -4.26) * mm});
            skLineSegment(sketch, "E2708", {"start": v(93.62, -4.26) * mm, "end": v(93.47, -4.2) * mm});
            skLineSegment(sketch, "E2709", {"start": v(93.47, -4.2) * mm, "end": v(93.33, -4.14) * mm});
            skLineSegment(sketch, "E2710", {"start": v(93.33, -4.14) * mm, "end": v(93.18, -4.09) * mm});
            skLineSegment(sketch, "E2711", {"start": v(93.18, -4.09) * mm, "end": v(93.04, -4.03) * mm});
            skLineSegment(sketch, "E2712", {"start": v(93.04, -4.03) * mm, "end": v(92.9, -3.98) * mm});
            skLineSegment(sketch, "E2713", {"start": v(92.9, -3.98) * mm, "end": v(92.76, -3.93) * mm});
            skLineSegment(sketch, "E2714", {"start": v(92.76, -3.93) * mm, "end": v(92.62, -3.88) * mm});
            skLineSegment(sketch, "E2715", {"start": v(92.62, -3.88) * mm, "end": v(92.49, -3.84) * mm});
            skLineSegment(sketch, "E2716", {"start": v(92.49, -3.84) * mm, "end": v(92.35, -3.79) * mm});
            skLineSegment(sketch, "E2717", {"start": v(92.35, -3.79) * mm, "end": v(92.22, -3.75) * mm});
            skLineSegment(sketch, "E2718", {"start": v(92.22, -3.75) * mm, "end": v(92.1, -3.7) * mm});
            skLineSegment(sketch, "E2719", {"start": v(92.1, -3.7) * mm, "end": v(91.97, -3.66) * mm});
            skLineSegment(sketch, "E2720", {"start": v(91.97, -3.66) * mm, "end": v(91.84, -3.62) * mm});
            skLineSegment(sketch, "E2721", {"start": v(91.84, -3.62) * mm, "end": v(91.72, -3.58) * mm});
            skLineSegment(sketch, "E2722", {"start": v(91.72, -3.58) * mm, "end": v(91.6, -3.54) * mm});
            skLineSegment(sketch, "E2723", {"start": v(91.6, -3.54) * mm, "end": v(91.48, -3.5) * mm});
            skLineSegment(sketch, "E2724", {"start": v(91.48, -3.5) * mm, "end": v(91.37, -3.47) * mm});
            skLineSegment(sketch, "E2725", {"start": v(91.37, -3.47) * mm, "end": v(91.25, -3.44) * mm});
            skLineSegment(sketch, "E2726", {"start": v(91.25, -3.44) * mm, "end": v(91.14, -3.4) * mm});
            skLineSegment(sketch, "E2727", {"start": v(91.14, -3.4) * mm, "end": v(90.95, -2.97) * mm});
            skLineSegment(sketch, "E2728", {"start": v(90.95, -2.97) * mm, "end": v(91, -1.29) * mm});
            skLineSegment(sketch, "E2729", {"start": v(91, -1.29) * mm, "end": v(91.2, -0.86) * mm});
            skLineSegment(sketch, "E2730", {"start": v(91.2, -0.86) * mm, "end": v(91.31, -0.84) * mm});
            skLineSegment(sketch, "E2731", {"start": v(91.31, -0.84) * mm, "end": v(91.43, -0.8) * mm});
            skLineSegment(sketch, "E2732", {"start": v(91.43, -0.8) * mm, "end": v(91.55, -0.78) * mm});
            skLineSegment(sketch, "E2733", {"start": v(91.55, -0.78) * mm, "end": v(91.67, -0.75) * mm});
            skLineSegment(sketch, "E2734", {"start": v(91.67, -0.75) * mm, "end": v(91.79, -0.72) * mm});
            skLineSegment(sketch, "E2735", {"start": v(91.79, -0.72) * mm, "end": v(91.91, -0.68) * mm});
            skLineSegment(sketch, "E2736", {"start": v(91.91, -0.68) * mm, "end": v(92.04, -0.65) * mm});
            skLineSegment(sketch, "E2737", {"start": v(92.04, -0.65) * mm, "end": v(92.17, -0.61) * mm});
            skLineSegment(sketch, "E2738", {"start": v(92.17, -0.61) * mm, "end": v(92.3, -0.58) * mm});
            skLineSegment(sketch, "E2739", {"start": v(92.3, -0.58) * mm, "end": v(92.43, -0.54) * mm});
            skLineSegment(sketch, "E2740", {"start": v(92.43, -0.54) * mm, "end": v(92.56, -0.5) * mm});
            skLineSegment(sketch, "E2741", {"start": v(92.56, -0.5) * mm, "end": v(92.7, -0.46) * mm});
            skLineSegment(sketch, "E2742", {"start": v(92.7, -0.46) * mm, "end": v(92.84, -0.42) * mm});
            skLineSegment(sketch, "E2743", {"start": v(92.84, -0.42) * mm, "end": v(92.98, -0.37) * mm});
            skLineSegment(sketch, "E2744", {"start": v(92.98, -0.37) * mm, "end": v(93.12, -0.33) * mm});
            skLineSegment(sketch, "E2745", {"start": v(93.12, -0.33) * mm, "end": v(93.27, -0.28) * mm});
            skLineSegment(sketch, "E2746", {"start": v(93.27, -0.28) * mm, "end": v(93.42, -0.23) * mm});
            skLineSegment(sketch, "E2747", {"start": v(93.42, -0.23) * mm, "end": v(93.57, -0.18) * mm});
            skLineSegment(sketch, "E2748", {"start": v(93.57, -0.18) * mm, "end": v(93.72, -0.13) * mm});
            skLineSegment(sketch, "E2749", {"start": v(93.72, -0.13) * mm, "end": v(93.87, -0.08) * mm});
            skLineSegment(sketch, "E2750", {"start": v(93.87, -0.08) * mm, "end": v(94.03, -0.02) * mm});
            skLineSegment(sketch, "E2751", {"start": v(94.03, -0.02) * mm, "end": v(94.19, 0.04) * mm});
            skLineSegment(sketch, "E2752", {"start": v(94.19, 0.04) * mm, "end": v(94.35, 0.1) * mm});
            skLineSegment(sketch, "E2753", {"start": v(94.35, 0.1) * mm, "end": v(94.5, 0.15) * mm});
            skLineSegment(sketch, "E2754", {"start": v(94.5, 0.15) * mm, "end": v(94.67, 0.22) * mm});
            skLineSegment(sketch, "E2755", {"start": v(94.67, 0.22) * mm, "end": v(94.84, 0.28) * mm});
            skLineSegment(sketch, "E2756", {"start": v(94.84, 0.28) * mm, "end": v(95, 0.34) * mm});
            skLineSegment(sketch, "E2757", {"start": v(95, 0.34) * mm, "end": v(95.18, 0.41) * mm});
            skLineSegment(sketch, "E2758", {"start": v(95.18, 0.41) * mm, "end": v(95.35, 0.48) * mm});
            skLineSegment(sketch, "E2759", {"start": v(95.35, 0.48) * mm, "end": v(95.52, 0.55) * mm});
            skLineSegment(sketch, "E2760", {"start": v(95.52, 0.55) * mm, "end": v(95.7, 0.62) * mm});
            skLineSegment(sketch, "E2761", {"start": v(95.7, 0.62) * mm, "end": v(95.88, 0.7) * mm});
            skLineSegment(sketch, "E2762", {"start": v(95.88, 0.7) * mm, "end": v(96.06, 0.77) * mm});
            skLineSegment(sketch, "E2763", {"start": v(96.06, 0.77) * mm, "end": v(96.24, 0.85) * mm});
            skLineSegment(sketch, "E2764", {"start": v(96.24, 0.85) * mm, "end": v(96.42, 0.93) * mm});
            skLineSegment(sketch, "E2765", {"start": v(96.42, 0.93) * mm, "end": v(96.6, 1.01) * mm});
            skLineSegment(sketch, "E2766", {"start": v(96.6, 1.01) * mm, "end": v(96.8, 1.1) * mm});
            skLineSegment(sketch, "E2767", {"start": v(96.8, 1.1) * mm, "end": v(96.98, 1.19) * mm});
            skLineSegment(sketch, "E2768", {"start": v(96.98, 1.19) * mm, "end": v(97.13, 1.27) * mm});
            skLineSegment(sketch, "E2769", {"start": v(97.13, 1.27) * mm, "end": v(97.08, 3.42) * mm});
            skLineSegment(sketch, "E2770", {"start": v(97.08, 3.42) * mm, "end": v(96.92, 3.5) * mm});
            skLineSegment(sketch, "E2771", {"start": v(96.92, 3.5) * mm, "end": v(96.73, 3.58) * mm});
            skLineSegment(sketch, "E2772", {"start": v(96.73, 3.58) * mm, "end": v(96.54, 3.66) * mm});
            skLineSegment(sketch, "E2773", {"start": v(96.54, 3.66) * mm, "end": v(96.35, 3.73) * mm});
            skLineSegment(sketch, "E2774", {"start": v(96.35, 3.73) * mm, "end": v(96.17, 3.8) * mm});
            skLineSegment(sketch, "E2775", {"start": v(96.17, 3.8) * mm, "end": v(95.98, 3.87) * mm});
            skLineSegment(sketch, "E2776", {"start": v(95.98, 3.87) * mm, "end": v(95.8, 3.94) * mm});
            skLineSegment(sketch, "E2777", {"start": v(95.8, 3.94) * mm, "end": v(95.62, 4) * mm});
            skLineSegment(sketch, "E2778", {"start": v(95.62, 4) * mm, "end": v(95.44, 4.07) * mm});
            skLineSegment(sketch, "E2779", {"start": v(95.44, 4.07) * mm, "end": v(95.26, 4.13) * mm});
            skLineSegment(sketch, "E2780", {"start": v(95.26, 4.13) * mm, "end": v(95.09, 4.2) * mm});
            skLineSegment(sketch, "E2781", {"start": v(95.09, 4.2) * mm, "end": v(94.91, 4.25) * mm});
            skLineSegment(sketch, "E2782", {"start": v(94.91, 4.25) * mm, "end": v(94.74, 4.3) * mm});
            skLineSegment(sketch, "E2783", {"start": v(94.74, 4.3) * mm, "end": v(94.57, 4.36) * mm});
            skLineSegment(sketch, "E2784", {"start": v(94.57, 4.36) * mm, "end": v(94.4, 4.41) * mm});
            skLineSegment(sketch, "E2785", {"start": v(94.4, 4.41) * mm, "end": v(94.24, 4.47) * mm});
            skLineSegment(sketch, "E2786", {"start": v(94.24, 4.47) * mm, "end": v(94.08, 4.52) * mm});
            skLineSegment(sketch, "E2787", {"start": v(94.08, 4.52) * mm, "end": v(93.92, 4.57) * mm});
            skLineSegment(sketch, "E2788", {"start": v(93.92, 4.57) * mm, "end": v(93.76, 4.61) * mm});
            skLineSegment(sketch, "E2789", {"start": v(93.76, 4.61) * mm, "end": v(93.6, 4.66) * mm});
            skLineSegment(sketch, "E2790", {"start": v(93.6, 4.66) * mm, "end": v(93.45, 4.7) * mm});
            skLineSegment(sketch, "E2791", {"start": v(93.45, 4.7) * mm, "end": v(93.3, 4.75) * mm});
            skLineSegment(sketch, "E2792", {"start": v(93.3, 4.75) * mm, "end": v(93.15, 4.79) * mm});
            skLineSegment(sketch, "E2793", {"start": v(93.15, 4.79) * mm, "end": v(93, 4.83) * mm});
            skLineSegment(sketch, "E2794", {"start": v(93, 4.83) * mm, "end": v(92.85, 4.87) * mm});
            skLineSegment(sketch, "E2795", {"start": v(92.85, 4.87) * mm, "end": v(92.71, 4.9) * mm});
            skLineSegment(sketch, "E2796", {"start": v(92.71, 4.9) * mm, "end": v(92.57, 4.94) * mm});
            skLineSegment(sketch, "E2797", {"start": v(92.57, 4.94) * mm, "end": v(92.43, 4.97) * mm});
            skLineSegment(sketch, "E2798", {"start": v(92.43, 4.97) * mm, "end": v(92.3, 5) * mm});
            skLineSegment(sketch, "E2799", {"start": v(92.3, 5) * mm, "end": v(92.16, 5.04) * mm});
            skLineSegment(sketch, "E2800", {"start": v(92.16, 5.04) * mm, "end": v(92.03, 5.07) * mm});
            skLineSegment(sketch, "E2801", {"start": v(92.03, 5.07) * mm, "end": v(91.9, 5.1) * mm});
            skLineSegment(sketch, "E2802", {"start": v(91.9, 5.1) * mm, "end": v(91.77, 5.13) * mm});
            skLineSegment(sketch, "E2803", {"start": v(91.77, 5.13) * mm, "end": v(91.65, 5.15) * mm});
            skLineSegment(sketch, "E2804", {"start": v(91.65, 5.15) * mm, "end": v(91.52, 5.18) * mm});
            skLineSegment(sketch, "E2805", {"start": v(91.52, 5.18) * mm, "end": v(91.4, 5.2) * mm});
            skLineSegment(sketch, "E2806", {"start": v(91.4, 5.2) * mm, "end": v(91.28, 5.23) * mm});
            skLineSegment(sketch, "E2807", {"start": v(91.28, 5.23) * mm, "end": v(91.17, 5.25) * mm});
            skLineSegment(sketch, "E2808", {"start": v(91.17, 5.25) * mm, "end": v(91.05, 5.27) * mm});
            skLineSegment(sketch, "E2809", {"start": v(91.05, 5.27) * mm, "end": v(90.82, 5.68) * mm});
            skLineSegment(sketch, "E2810", {"start": v(90.82, 5.68) * mm, "end": v(90.7, 7.37) * mm});
            skLineSegment(sketch, "E2811", {"start": v(90.7, 7.37) * mm, "end": v(90.87, 7.81) * mm});
            skLineSegment(sketch, "E2812", {"start": v(90.87, 7.81) * mm, "end": v(90.98, 7.85) * mm});
            skLineSegment(sketch, "E2813", {"start": v(90.98, 7.85) * mm, "end": v(91.1, 7.89) * mm});
            skLineSegment(sketch, "E2814", {"start": v(91.1, 7.89) * mm, "end": v(91.2, 7.93) * mm});
            skLineSegment(sketch, "E2815", {"start": v(91.2, 7.93) * mm, "end": v(91.32, 7.97) * mm});
            skLineSegment(sketch, "E2816", {"start": v(91.32, 7.97) * mm, "end": v(91.44, 8.01) * mm});
            skLineSegment(sketch, "E2817", {"start": v(91.44, 8.01) * mm, "end": v(91.56, 8.06) * mm});
            skLineSegment(sketch, "E2818", {"start": v(91.56, 8.06) * mm, "end": v(91.68, 8.1) * mm});
            skLineSegment(sketch, "E2819", {"start": v(91.68, 8.1) * mm, "end": v(91.8, 8.15) * mm});
            skLineSegment(sketch, "E2820", {"start": v(91.8, 8.15) * mm, "end": v(91.93, 8.2) * mm});
            skLineSegment(sketch, "E2821", {"start": v(91.93, 8.2) * mm, "end": v(92.06, 8.25) * mm});
            skLineSegment(sketch, "E2822", {"start": v(92.06, 8.25) * mm, "end": v(92.2, 8.3) * mm});
            skLineSegment(sketch, "E2823", {"start": v(92.2, 8.3) * mm, "end": v(92.32, 8.36) * mm});
            skLineSegment(sketch, "E2824", {"start": v(92.32, 8.36) * mm, "end": v(92.46, 8.41) * mm});
            skLineSegment(sketch, "E2825", {"start": v(92.46, 8.41) * mm, "end": v(92.6, 8.47) * mm});
            skLineSegment(sketch, "E2826", {"start": v(92.6, 8.47) * mm, "end": v(92.73, 8.53) * mm});
            skLineSegment(sketch, "E2827", {"start": v(92.73, 8.53) * mm, "end": v(92.87, 8.59) * mm});
            skLineSegment(sketch, "E2828", {"start": v(92.87, 8.59) * mm, "end": v(93.02, 8.65) * mm});
            skLineSegment(sketch, "E2829", {"start": v(93.02, 8.65) * mm, "end": v(93.16, 8.71) * mm});
            skLineSegment(sketch, "E2830", {"start": v(93.16, 8.71) * mm, "end": v(93.3, 8.78) * mm});
            skLineSegment(sketch, "E2831", {"start": v(93.3, 8.78) * mm, "end": v(93.46, 8.85) * mm});
            skLineSegment(sketch, "E2832", {"start": v(93.46, 8.85) * mm, "end": v(93.6, 8.92) * mm});
            skLineSegment(sketch, "E2833", {"start": v(93.6, 8.92) * mm, "end": v(93.76, 8.99) * mm});
            skLineSegment(sketch, "E2834", {"start": v(93.76, 8.99) * mm, "end": v(93.91, 9.06) * mm});
            skLineSegment(sketch, "E2835", {"start": v(93.91, 9.06) * mm, "end": v(94.07, 9.14) * mm});
            skLineSegment(sketch, "E2836", {"start": v(94.07, 9.14) * mm, "end": v(94.22, 9.21) * mm});
            skLineSegment(sketch, "E2837", {"start": v(94.22, 9.21) * mm, "end": v(94.38, 9.3) * mm});
            skLineSegment(sketch, "E2838", {"start": v(94.38, 9.3) * mm, "end": v(94.54, 9.37) * mm});
            skLineSegment(sketch, "E2839", {"start": v(94.54, 9.37) * mm, "end": v(94.7, 9.46) * mm});
            skLineSegment(sketch, "E2840", {"start": v(94.7, 9.46) * mm, "end": v(94.87, 9.54) * mm});
            skLineSegment(sketch, "E2841", {"start": v(94.87, 9.54) * mm, "end": v(95.04, 9.63) * mm});
            skLineSegment(sketch, "E2842", {"start": v(95.04, 9.63) * mm, "end": v(95.2, 9.72) * mm});
            skLineSegment(sketch, "E2843", {"start": v(95.2, 9.72) * mm, "end": v(95.38, 9.8) * mm});
            skLineSegment(sketch, "E2844", {"start": v(95.38, 9.8) * mm, "end": v(95.55, 9.9) * mm});
            skLineSegment(sketch, "E2845", {"start": v(95.55, 9.9) * mm, "end": v(95.72, 10) * mm});
            skLineSegment(sketch, "E2846", {"start": v(95.72, 10) * mm, "end": v(95.9, 10.1) * mm});
            skLineSegment(sketch, "E2847", {"start": v(95.9, 10.1) * mm, "end": v(96.07, 10.2) * mm});
            skLineSegment(sketch, "E2848", {"start": v(96.07, 10.2) * mm, "end": v(96.25, 10.3) * mm});
            skLineSegment(sketch, "E2849", {"start": v(96.25, 10.3) * mm, "end": v(96.43, 10.4) * mm});
            skLineSegment(sketch, "E2850", {"start": v(96.43, 10.4) * mm, "end": v(96.57, 10.5) * mm});
            skLineSegment(sketch, "E2851", {"start": v(96.57, 10.5) * mm, "end": v(96.32, 12.64) * mm});
            skLineSegment(sketch, "E2852", {"start": v(96.32, 12.64) * mm, "end": v(96.15, 12.7) * mm});
            skLineSegment(sketch, "E2853", {"start": v(96.15, 12.7) * mm, "end": v(95.95, 12.76) * mm});
            skLineSegment(sketch, "E2854", {"start": v(95.95, 12.76) * mm, "end": v(95.76, 12.82) * mm});
            skLineSegment(sketch, "E2855", {"start": v(95.76, 12.82) * mm, "end": v(95.56, 12.87) * mm});
            skLineSegment(sketch, "E2856", {"start": v(95.56, 12.87) * mm, "end": v(95.37, 12.92) * mm});
            skLineSegment(sketch, "E2857", {"start": v(95.37, 12.92) * mm, "end": v(95.18, 12.98) * mm});
            skLineSegment(sketch, "E2858", {"start": v(95.18, 12.98) * mm, "end": v(94.99, 13.03) * mm});
            skLineSegment(sketch, "E2859", {"start": v(94.99, 13.03) * mm, "end": v(94.8, 13.07) * mm});
            skLineSegment(sketch, "E2860", {"start": v(94.8, 13.07) * mm, "end": v(94.62, 13.12) * mm});
            skLineSegment(sketch, "E2861", {"start": v(94.62, 13.12) * mm, "end": v(94.44, 13.17) * mm});
            skLineSegment(sketch, "E2862", {"start": v(94.44, 13.17) * mm, "end": v(94.26, 13.2) * mm});
            skLineSegment(sketch, "E2863", {"start": v(94.26, 13.2) * mm, "end": v(94.08, 13.25) * mm});
            skLineSegment(sketch, "E2864", {"start": v(94.08, 13.25) * mm, "end": v(93.9, 13.3) * mm});
            skLineSegment(sketch, "E2865", {"start": v(93.9, 13.3) * mm, "end": v(93.73, 13.33) * mm});
            skLineSegment(sketch, "E2866", {"start": v(93.73, 13.33) * mm, "end": v(93.56, 13.37) * mm});
            skLineSegment(sketch, "E2867", {"start": v(93.56, 13.37) * mm, "end": v(93.39, 13.4) * mm});
            skLineSegment(sketch, "E2868", {"start": v(93.39, 13.4) * mm, "end": v(93.22, 13.44) * mm});
            skLineSegment(sketch, "E2869", {"start": v(93.22, 13.44) * mm, "end": v(93.06, 13.47) * mm});
            skLineSegment(sketch, "E2870", {"start": v(93.06, 13.47) * mm, "end": v(92.9, 13.5) * mm});
            skLineSegment(sketch, "E2871", {"start": v(92.9, 13.5) * mm, "end": v(92.74, 13.54) * mm});
            skLineSegment(sketch, "E2872", {"start": v(92.74, 13.54) * mm, "end": v(92.58, 13.57) * mm});
            skLineSegment(sketch, "E2873", {"start": v(92.58, 13.57) * mm, "end": v(92.42, 13.6) * mm});
            skLineSegment(sketch, "E2874", {"start": v(92.42, 13.6) * mm, "end": v(92.27, 13.62) * mm});
            skLineSegment(sketch, "E2875", {"start": v(92.27, 13.62) * mm, "end": v(92.12, 13.65) * mm});
            skLineSegment(sketch, "E2876", {"start": v(92.12, 13.65) * mm, "end": v(91.97, 13.67) * mm});
            skLineSegment(sketch, "E2877", {"start": v(91.97, 13.67) * mm, "end": v(91.83, 13.7) * mm});
            skLineSegment(sketch, "E2878", {"start": v(91.83, 13.7) * mm, "end": v(91.68, 13.72) * mm});
            skLineSegment(sketch, "E2879", {"start": v(91.68, 13.72) * mm, "end": v(91.54, 13.74) * mm});
            skLineSegment(sketch, "E2880", {"start": v(91.54, 13.74) * mm, "end": v(91.4, 13.76) * mm});
            skLineSegment(sketch, "E2881", {"start": v(91.4, 13.76) * mm, "end": v(91.26, 13.78) * mm});
            skLineSegment(sketch, "E2882", {"start": v(91.26, 13.78) * mm, "end": v(91.13, 13.8) * mm});
            skLineSegment(sketch, "E2883", {"start": v(91.13, 13.8) * mm, "end": v(91, 13.81) * mm});
            skLineSegment(sketch, "E2884", {"start": v(91, 13.81) * mm, "end": v(90.87, 13.83) * mm});
            skLineSegment(sketch, "E2885", {"start": v(90.87, 13.83) * mm, "end": v(90.74, 13.84) * mm});
            skLineSegment(sketch, "E2886", {"start": v(90.74, 13.84) * mm, "end": v(90.62, 13.85) * mm});
            skLineSegment(sketch, "E2887", {"start": v(90.62, 13.85) * mm, "end": v(90.5, 13.87) * mm});
            skLineSegment(sketch, "E2888", {"start": v(90.5, 13.87) * mm, "end": v(90.37, 13.88) * mm});
            skLineSegment(sketch, "E2889", {"start": v(90.37, 13.88) * mm, "end": v(90.26, 13.9) * mm});
            skLineSegment(sketch, "E2890", {"start": v(90.26, 13.9) * mm, "end": v(90.14, 13.9) * mm});
            skLineSegment(sketch, "E2891", {"start": v(90.14, 13.9) * mm, "end": v(89.87, 14.3) * mm});
            skLineSegment(sketch, "E2892", {"start": v(89.87, 14.3) * mm, "end": v(89.6, 15.96) * mm});
            skLineSegment(sketch, "E2893", {"start": v(89.6, 15.96) * mm, "end": v(89.72, 16.41) * mm});
            skLineSegment(sketch, "E2894", {"start": v(89.72, 16.41) * mm, "end": v(89.82, 16.46) * mm});
            skLineSegment(sketch, "E2895", {"start": v(89.82, 16.46) * mm, "end": v(89.93, 16.51) * mm});
            skLineSegment(sketch, "E2896", {"start": v(89.93, 16.51) * mm, "end": v(90.04, 16.56) * mm});
            skLineSegment(sketch, "E2897", {"start": v(90.04, 16.56) * mm, "end": v(90.15, 16.61) * mm});
            skLineSegment(sketch, "E2898", {"start": v(90.15, 16.61) * mm, "end": v(90.26, 16.67) * mm});
            skLineSegment(sketch, "E2899", {"start": v(90.26, 16.67) * mm, "end": v(90.38, 16.72) * mm});
            skLineSegment(sketch, "E2900", {"start": v(90.38, 16.72) * mm, "end": v(90.5, 16.78) * mm});
            skLineSegment(sketch, "E2901", {"start": v(90.5, 16.78) * mm, "end": v(90.62, 16.84) * mm});
            skLineSegment(sketch, "E2902", {"start": v(90.62, 16.84) * mm, "end": v(90.74, 16.9) * mm});
            skLineSegment(sketch, "E2903", {"start": v(90.74, 16.9) * mm, "end": v(90.86, 16.96) * mm});
            skLineSegment(sketch, "E2904", {"start": v(90.86, 16.96) * mm, "end": v(90.99, 17.03) * mm});
            skLineSegment(sketch, "E2905", {"start": v(90.99, 17.03) * mm, "end": v(91.11, 17.1) * mm});
            skLineSegment(sketch, "E2906", {"start": v(91.11, 17.1) * mm, "end": v(91.24, 17.16) * mm});
            skLineSegment(sketch, "E2907", {"start": v(91.24, 17.16) * mm, "end": v(91.37, 17.23) * mm});
            skLineSegment(sketch, "E2908", {"start": v(91.37, 17.23) * mm, "end": v(91.5, 17.3) * mm});
            skLineSegment(sketch, "E2909", {"start": v(91.5, 17.3) * mm, "end": v(91.64, 17.38) * mm});
            skLineSegment(sketch, "E2910", {"start": v(91.64, 17.38) * mm, "end": v(91.77, 17.45) * mm});
            skLineSegment(sketch, "E2911", {"start": v(91.77, 17.45) * mm, "end": v(91.91, 17.53) * mm});
            skLineSegment(sketch, "E2912", {"start": v(91.91, 17.53) * mm, "end": v(92.05, 17.6) * mm});
            skLineSegment(sketch, "E2913", {"start": v(92.05, 17.6) * mm, "end": v(92.2, 17.7) * mm});
            skLineSegment(sketch, "E2914", {"start": v(92.2, 17.7) * mm, "end": v(92.33, 17.77) * mm});
            skLineSegment(sketch, "E2915", {"start": v(92.33, 17.77) * mm, "end": v(92.48, 17.86) * mm});
            skLineSegment(sketch, "E2916", {"start": v(92.48, 17.86) * mm, "end": v(92.62, 17.95) * mm});
            skLineSegment(sketch, "E2917", {"start": v(92.62, 17.95) * mm, "end": v(92.77, 18.04) * mm});
            skLineSegment(sketch, "E2918", {"start": v(92.77, 18.04) * mm, "end": v(92.92, 18.13) * mm});
            skLineSegment(sketch, "E2919", {"start": v(92.92, 18.13) * mm, "end": v(93.07, 18.22) * mm});
            skLineSegment(sketch, "E2920", {"start": v(93.07, 18.22) * mm, "end": v(93.22, 18.32) * mm});
            skLineSegment(sketch, "E2921", {"start": v(93.22, 18.32) * mm, "end": v(93.38, 18.42) * mm});
            skLineSegment(sketch, "E2922", {"start": v(93.38, 18.42) * mm, "end": v(93.53, 18.52) * mm});
            skLineSegment(sketch, "E2923", {"start": v(93.53, 18.52) * mm, "end": v(93.7, 18.62) * mm});
            skLineSegment(sketch, "E2924", {"start": v(93.7, 18.62) * mm, "end": v(93.85, 18.72) * mm});
            skLineSegment(sketch, "E2925", {"start": v(93.85, 18.72) * mm, "end": v(94.01, 18.83) * mm});
            skLineSegment(sketch, "E2926", {"start": v(94.01, 18.83) * mm, "end": v(94.17, 18.94) * mm});
            skLineSegment(sketch, "E2927", {"start": v(94.17, 18.94) * mm, "end": v(94.34, 19.05) * mm});
            skLineSegment(sketch, "E2928", {"start": v(94.34, 19.05) * mm, "end": v(94.5, 19.16) * mm});
            skLineSegment(sketch, "E2929", {"start": v(94.5, 19.16) * mm, "end": v(94.67, 19.28) * mm});
            skLineSegment(sketch, "E2930", {"start": v(94.67, 19.28) * mm, "end": v(94.83, 19.4) * mm});
            skLineSegment(sketch, "E2931", {"start": v(94.83, 19.4) * mm, "end": v(95, 19.52) * mm});
            skLineSegment(sketch, "E2932", {"start": v(95, 19.52) * mm, "end": v(95.14, 19.63) * mm});
            skLineSegment(sketch, "E2933", {"start": v(95.14, 19.63) * mm, "end": v(94.68, 21.74) * mm});
            skLineSegment(sketch, "E2934", {"start": v(94.68, 21.74) * mm, "end": v(94.5, 21.78) * mm});
            skLineSegment(sketch, "E2935", {"start": v(94.5, 21.78) * mm, "end": v(94.3, 21.82) * mm});
            skLineSegment(sketch, "E2936", {"start": v(94.3, 21.82) * mm, "end": v(94.1, 21.86) * mm});
            skLineSegment(sketch, "E2937", {"start": v(94.1, 21.86) * mm, "end": v(93.9, 21.9) * mm});
            skLineSegment(sketch, "E2938", {"start": v(93.9, 21.9) * mm, "end": v(93.7, 21.93) * mm});
            skLineSegment(sketch, "E2939", {"start": v(93.7, 21.93) * mm, "end": v(93.51, 21.96) * mm});
            skLineSegment(sketch, "E2940", {"start": v(93.51, 21.96) * mm, "end": v(93.32, 22) * mm});
            skLineSegment(sketch, "E2941", {"start": v(93.32, 22) * mm, "end": v(93.13, 22.03) * mm});
            skLineSegment(sketch, "E2942", {"start": v(93.13, 22.03) * mm, "end": v(92.94, 22.06) * mm});
            skLineSegment(sketch, "E2943", {"start": v(92.94, 22.06) * mm, "end": v(92.76, 22.08) * mm});
            skLineSegment(sketch, "E2944", {"start": v(92.76, 22.08) * mm, "end": v(92.57, 22.1) * mm});
            skLineSegment(sketch, "E2945", {"start": v(92.57, 22.1) * mm, "end": v(92.4, 22.13) * mm});
            skLineSegment(sketch, "E2946", {"start": v(92.4, 22.13) * mm, "end": v(92.21, 22.16) * mm});
            skLineSegment(sketch, "E2947", {"start": v(92.21, 22.16) * mm, "end": v(92.04, 22.18) * mm});
            skLineSegment(sketch, "E2948", {"start": v(92.04, 22.18) * mm, "end": v(91.86, 22.2) * mm});
            skLineSegment(sketch, "E2949", {"start": v(91.86, 22.2) * mm, "end": v(91.7, 22.22) * mm});
            skLineSegment(sketch, "E2950", {"start": v(91.7, 22.22) * mm, "end": v(91.52, 22.24) * mm});
            skLineSegment(sketch, "E2951", {"start": v(91.52, 22.24) * mm, "end": v(91.36, 22.26) * mm});
            skLineSegment(sketch, "E2952", {"start": v(91.36, 22.26) * mm, "end": v(91.2, 22.27) * mm});
            skLineSegment(sketch, "E2953", {"start": v(91.2, 22.27) * mm, "end": v(91.03, 22.29) * mm});
            skLineSegment(sketch, "E2954", {"start": v(91.03, 22.29) * mm, "end": v(90.87, 22.3) * mm});
            skLineSegment(sketch, "E2955", {"start": v(90.87, 22.3) * mm, "end": v(90.71, 22.32) * mm});
            skLineSegment(sketch, "E2956", {"start": v(90.71, 22.32) * mm, "end": v(90.56, 22.33) * mm});
            skLineSegment(sketch, "E2957", {"start": v(90.56, 22.33) * mm, "end": v(90.4, 22.34) * mm});
            skLineSegment(sketch, "E2958", {"start": v(90.4, 22.34) * mm, "end": v(90.26, 22.35) * mm});
            skLineSegment(sketch, "E2959", {"start": v(90.26, 22.35) * mm, "end": v(90.1, 22.36) * mm});
            skLineSegment(sketch, "E2960", {"start": v(90.1, 22.36) * mm, "end": v(89.96, 22.37) * mm});
            skLineSegment(sketch, "E2961", {"start": v(89.96, 22.37) * mm, "end": v(89.82, 22.38) * mm});
            skLineSegment(sketch, "E2962", {"start": v(89.82, 22.38) * mm, "end": v(89.68, 22.38) * mm});
            skLineSegment(sketch, "E2963", {"start": v(89.68, 22.38) * mm, "end": v(89.54, 22.39) * mm});
            skLineSegment(sketch, "E2964", {"start": v(89.54, 22.39) * mm, "end": v(89.4, 22.4) * mm});
            skLineSegment(sketch, "E2965", {"start": v(89.4, 22.4) * mm, "end": v(89.27, 22.4) * mm});
            skLineSegment(sketch, "E2966", {"start": v(89.27, 22.4) * mm, "end": v(89.14, 22.4) * mm});
            skLineSegment(sketch, "E2967", {"start": v(89.14, 22.4) * mm, "end": v(89.01, 22.4) * mm});
            skLineSegment(sketch, "E2968", {"start": v(89.01, 22.4) * mm, "end": v(88.89, 22.4) * mm});
            skLineSegment(sketch, "E2969", {"start": v(88.89, 22.4) * mm, "end": v(88.77, 22.4) * mm});
            skLineSegment(sketch, "E2970", {"start": v(88.77, 22.4) * mm, "end": v(88.64, 22.4) * mm});
            skLineSegment(sketch, "E2971", {"start": v(88.64, 22.4) * mm, "end": v(88.53, 22.4) * mm});
            skLineSegment(sketch, "E2972", {"start": v(88.53, 22.4) * mm, "end": v(88.41, 22.4) * mm});
            skLineSegment(sketch, "E2973", {"start": v(88.41, 22.4) * mm, "end": v(88.1, 22.77) * mm});
            skLineSegment(sketch, "E2974", {"start": v(88.1, 22.77) * mm, "end": v(87.67, 24.4) * mm});
            skLineSegment(sketch, "E2975", {"start": v(87.67, 24.4) * mm, "end": v(87.75, 24.87) * mm});
            skLineSegment(sketch, "E2976", {"start": v(87.75, 24.87) * mm, "end": v(87.85, 24.93) * mm});
            skLineSegment(sketch, "E2977", {"start": v(87.85, 24.93) * mm, "end": v(87.95, 24.98) * mm});
            skLineSegment(sketch, "E2978", {"start": v(87.95, 24.98) * mm, "end": v(88.06, 25.05) * mm});
            skLineSegment(sketch, "E2979", {"start": v(88.06, 25.05) * mm, "end": v(88.16, 25.1) * mm});
            skLineSegment(sketch, "E2980", {"start": v(88.16, 25.1) * mm, "end": v(88.27, 25.17) * mm});
            skLineSegment(sketch, "E2981", {"start": v(88.27, 25.17) * mm, "end": v(88.38, 25.24) * mm});
            skLineSegment(sketch, "E2982", {"start": v(88.38, 25.24) * mm, "end": v(88.5, 25.3) * mm});
            skLineSegment(sketch, "E2983", {"start": v(88.5, 25.3) * mm, "end": v(88.6, 25.38) * mm});
            skLineSegment(sketch, "E2984", {"start": v(88.6, 25.38) * mm, "end": v(88.72, 25.45) * mm});
            skLineSegment(sketch, "E2985", {"start": v(88.72, 25.45) * mm, "end": v(88.84, 25.52) * mm});
            skLineSegment(sketch, "E2986", {"start": v(88.84, 25.52) * mm, "end": v(88.95, 25.6) * mm});
            skLineSegment(sketch, "E2987", {"start": v(88.95, 25.6) * mm, "end": v(89.07, 25.68) * mm});
            skLineSegment(sketch, "E2988", {"start": v(89.07, 25.68) * mm, "end": v(89.2, 25.76) * mm});
            skLineSegment(sketch, "E2989", {"start": v(89.2, 25.76) * mm, "end": v(89.32, 25.84) * mm});
            skLineSegment(sketch, "E2990", {"start": v(89.32, 25.84) * mm, "end": v(89.44, 25.92) * mm});
            skLineSegment(sketch, "E2991", {"start": v(89.44, 25.92) * mm, "end": v(89.57, 26) * mm});
            skLineSegment(sketch, "E2992", {"start": v(89.57, 26) * mm, "end": v(89.7, 26.1) * mm});
            skLineSegment(sketch, "E2993", {"start": v(89.7, 26.1) * mm, "end": v(89.83, 26.19) * mm});
            skLineSegment(sketch, "E2994", {"start": v(89.83, 26.19) * mm, "end": v(89.96, 26.28) * mm});
            skLineSegment(sketch, "E2995", {"start": v(89.96, 26.28) * mm, "end": v(90.1, 26.37) * mm});
            skLineSegment(sketch, "E2996", {"start": v(90.1, 26.37) * mm, "end": v(90.23, 26.47) * mm});
            skLineSegment(sketch, "E2997", {"start": v(90.23, 26.47) * mm, "end": v(90.36, 26.57) * mm});
            skLineSegment(sketch, "E2998", {"start": v(90.36, 26.57) * mm, "end": v(90.5, 26.67) * mm});
            skLineSegment(sketch, "E2999", {"start": v(90.5, 26.67) * mm, "end": v(90.64, 26.77) * mm});
            skLineSegment(sketch, "E3000", {"start": v(90.64, 26.77) * mm, "end": v(90.78, 26.88) * mm});
            skLineSegment(sketch, "E3001", {"start": v(90.78, 26.88) * mm, "end": v(90.92, 26.99) * mm});
            skLineSegment(sketch, "E3002", {"start": v(90.92, 26.99) * mm, "end": v(91.06, 27.1) * mm});
            skLineSegment(sketch, "E3003", {"start": v(91.06, 27.1) * mm, "end": v(91.2, 27.2) * mm});
            skLineSegment(sketch, "E3004", {"start": v(91.2, 27.2) * mm, "end": v(91.35, 27.32) * mm});
            skLineSegment(sketch, "E3005", {"start": v(91.35, 27.32) * mm, "end": v(91.5, 27.44) * mm});
            skLineSegment(sketch, "E3006", {"start": v(91.5, 27.44) * mm, "end": v(91.65, 27.56) * mm});
            skLineSegment(sketch, "E3007", {"start": v(91.65, 27.56) * mm, "end": v(91.8, 27.68) * mm});
            skLineSegment(sketch, "E3008", {"start": v(91.8, 27.68) * mm, "end": v(91.95, 27.8) * mm});
            skLineSegment(sketch, "E3009", {"start": v(91.95, 27.8) * mm, "end": v(92.1, 27.93) * mm});
            skLineSegment(sketch, "E3010", {"start": v(92.1, 27.93) * mm, "end": v(92.25, 28.06) * mm});
            skLineSegment(sketch, "E3011", {"start": v(92.25, 28.06) * mm, "end": v(92.4, 28.2) * mm});
            skLineSegment(sketch, "E3012", {"start": v(92.4, 28.2) * mm, "end": v(92.56, 28.32) * mm});
            skLineSegment(sketch, "E3013", {"start": v(92.56, 28.32) * mm, "end": v(92.72, 28.46) * mm});
            skLineSegment(sketch, "E3014", {"start": v(92.72, 28.46) * mm, "end": v(92.84, 28.59) * mm});
            skLineSegment(sketch, "E3015", {"start": v(92.84, 28.59) * mm, "end": v(92.19, 30.64) * mm});
            skLineSegment(sketch, "E3016", {"start": v(92.19, 30.64) * mm, "end": v(92.01, 30.67) * mm});
            skLineSegment(sketch, "E3017", {"start": v(92.01, 30.67) * mm, "end": v(91.8, 30.69) * mm});
            skLineSegment(sketch, "E3018", {"start": v(91.8, 30.69) * mm, "end": v(91.6, 30.7) * mm});
            skLineSegment(sketch, "E3019", {"start": v(91.6, 30.7) * mm, "end": v(91.4, 30.72) * mm});
            skLineSegment(sketch, "E3020", {"start": v(91.4, 30.72) * mm, "end": v(91.2, 30.74) * mm});
            skLineSegment(sketch, "E3021", {"start": v(91.2, 30.74) * mm, "end": v(91, 30.75) * mm});
            skLineSegment(sketch, "E3022", {"start": v(91, 30.75) * mm, "end": v(90.8, 30.77) * mm});
            skLineSegment(sketch, "E3023", {"start": v(90.8, 30.77) * mm, "end": v(90.62, 30.78) * mm});
            skLineSegment(sketch, "E3024", {"start": v(90.62, 30.78) * mm, "end": v(90.43, 30.8) * mm});
            skLineSegment(sketch, "E3025", {"start": v(90.43, 30.8) * mm, "end": v(90.24, 30.8) * mm});
            skLineSegment(sketch, "E3026", {"start": v(90.24, 30.8) * mm, "end": v(90.05, 30.8) * mm});
            skLineSegment(sketch, "E3027", {"start": v(90.05, 30.8) * mm, "end": v(89.87, 30.82) * mm});
            skLineSegment(sketch, "E3028", {"start": v(89.87, 30.82) * mm, "end": v(89.7, 30.82) * mm});
            skLineSegment(sketch, "E3029", {"start": v(89.7, 30.82) * mm, "end": v(89.51, 30.83) * mm});
            skLineSegment(sketch, "E3030", {"start": v(89.51, 30.83) * mm, "end": v(89.34, 30.83) * mm});
            skLineSegment(sketch, "E3031", {"start": v(89.34, 30.83) * mm, "end": v(89.17, 30.84) * mm});
            skLineSegment(sketch, "E3032", {"start": v(89.17, 30.84) * mm, "end": v(89, 30.84) * mm});
            skLineSegment(sketch, "E3033", {"start": v(89, 30.84) * mm, "end": v(88.83, 30.84) * mm});
            skLineSegment(sketch, "E3034", {"start": v(88.83, 30.84) * mm, "end": v(88.66, 30.84) * mm});
            skLineSegment(sketch, "E3035", {"start": v(88.66, 30.84) * mm, "end": v(88.5, 30.84) * mm});
            skLineSegment(sketch, "E3036", {"start": v(88.5, 30.84) * mm, "end": v(88.34, 30.84) * mm});
            skLineSegment(sketch, "E3037", {"start": v(88.34, 30.84) * mm, "end": v(88.18, 30.84) * mm});
            skLineSegment(sketch, "E3038", {"start": v(88.18, 30.84) * mm, "end": v(88.03, 30.84) * mm});
            skLineSegment(sketch, "E3039", {"start": v(88.03, 30.84) * mm, "end": v(87.87, 30.83) * mm});
            skLineSegment(sketch, "E3040", {"start": v(87.87, 30.83) * mm, "end": v(87.72, 30.83) * mm});
            skLineSegment(sketch, "E3041", {"start": v(87.72, 30.83) * mm, "end": v(87.57, 30.82) * mm});
            skLineSegment(sketch, "E3042", {"start": v(87.57, 30.82) * mm, "end": v(87.43, 30.82) * mm});
            skLineSegment(sketch, "E3043", {"start": v(87.43, 30.82) * mm, "end": v(87.29, 30.81) * mm});
            skLineSegment(sketch, "E3044", {"start": v(87.29, 30.81) * mm, "end": v(87.15, 30.8) * mm});
            skLineSegment(sketch, "E3045", {"start": v(87.15, 30.8) * mm, "end": v(87, 30.8) * mm});
            skLineSegment(sketch, "E3046", {"start": v(87, 30.8) * mm, "end": v(86.87, 30.8) * mm});
            skLineSegment(sketch, "E3047", {"start": v(86.87, 30.8) * mm, "end": v(86.74, 30.78) * mm});
            skLineSegment(sketch, "E3048", {"start": v(86.74, 30.78) * mm, "end": v(86.6, 30.77) * mm});
            skLineSegment(sketch, "E3049", {"start": v(86.6, 30.77) * mm, "end": v(86.48, 30.76) * mm});
            skLineSegment(sketch, "E3050", {"start": v(86.48, 30.76) * mm, "end": v(86.36, 30.75) * mm});
            skLineSegment(sketch, "E3051", {"start": v(86.36, 30.75) * mm, "end": v(86.23, 30.74) * mm});
            skLineSegment(sketch, "E3052", {"start": v(86.23, 30.74) * mm, "end": v(86.11, 30.73) * mm});
            skLineSegment(sketch, "E3053", {"start": v(86.11, 30.73) * mm, "end": v(86, 30.72) * mm});
            skLineSegment(sketch, "E3054", {"start": v(86, 30.72) * mm, "end": v(85.88, 30.7) * mm});
            skLineSegment(sketch, "E3055", {"start": v(85.88, 30.7) * mm, "end": v(85.54, 31.04) * mm});
            skLineSegment(sketch, "E3056", {"start": v(85.54, 31.04) * mm, "end": v(84.95, 32.62) * mm});
            skLineSegment(sketch, "E3057", {"start": v(84.95, 32.62) * mm, "end": v(84.99, 33.1) * mm});
            skLineSegment(sketch, "E3058", {"start": v(84.99, 33.1) * mm, "end": v(85.08, 33.16) * mm});
            skLineSegment(sketch, "E3059", {"start": v(85.08, 33.16) * mm, "end": v(85.18, 33.23) * mm});
            skLineSegment(sketch, "E3060", {"start": v(85.18, 33.23) * mm, "end": v(85.28, 33.3) * mm});
            skLineSegment(sketch, "E3061", {"start": v(85.28, 33.3) * mm, "end": v(85.38, 33.37) * mm});
            skLineSegment(sketch, "E3062", {"start": v(85.38, 33.37) * mm, "end": v(85.48, 33.45) * mm});
            skLineSegment(sketch, "E3063", {"start": v(85.48, 33.45) * mm, "end": v(85.58, 33.53) * mm});
            skLineSegment(sketch, "E3064", {"start": v(85.58, 33.53) * mm, "end": v(85.69, 33.6) * mm});
            skLineSegment(sketch, "E3065", {"start": v(85.69, 33.6) * mm, "end": v(85.8, 33.68) * mm});
            skLineSegment(sketch, "E3066", {"start": v(85.8, 33.68) * mm, "end": v(85.9, 33.77) * mm});
            skLineSegment(sketch, "E3067", {"start": v(85.9, 33.77) * mm, "end": v(86, 33.85) * mm});
            skLineSegment(sketch, "E3068", {"start": v(86, 33.85) * mm, "end": v(86.12, 33.94) * mm});
            skLineSegment(sketch, "E3069", {"start": v(86.12, 33.94) * mm, "end": v(86.23, 34.03) * mm});
            skLineSegment(sketch, "E3070", {"start": v(86.23, 34.03) * mm, "end": v(86.34, 34.12) * mm});
            skLineSegment(sketch, "E3071", {"start": v(86.34, 34.12) * mm, "end": v(86.46, 34.21) * mm});
            skLineSegment(sketch, "E3072", {"start": v(86.46, 34.21) * mm, "end": v(86.58, 34.3) * mm});
            skLineSegment(sketch, "E3073", {"start": v(86.58, 34.3) * mm, "end": v(86.7, 34.4) * mm});
            skLineSegment(sketch, "E3074", {"start": v(86.7, 34.4) * mm, "end": v(86.81, 34.5) * mm});
            skLineSegment(sketch, "E3075", {"start": v(86.81, 34.5) * mm, "end": v(86.93, 34.6) * mm});
            skLineSegment(sketch, "E3076", {"start": v(86.93, 34.6) * mm, "end": v(87.05, 34.71) * mm});
            skLineSegment(sketch, "E3077", {"start": v(87.05, 34.71) * mm, "end": v(87.18, 34.82) * mm});
            skLineSegment(sketch, "E3078", {"start": v(87.18, 34.82) * mm, "end": v(87.3, 34.93) * mm});
            skLineSegment(sketch, "E3079", {"start": v(87.3, 34.93) * mm, "end": v(87.43, 35.04) * mm});
            skLineSegment(sketch, "E3080", {"start": v(87.43, 35.04) * mm, "end": v(87.55, 35.15) * mm});
            skLineSegment(sketch, "E3081", {"start": v(87.55, 35.15) * mm, "end": v(87.68, 35.27) * mm});
            skLineSegment(sketch, "E3082", {"start": v(87.68, 35.27) * mm, "end": v(87.81, 35.39) * mm});
            skLineSegment(sketch, "E3083", {"start": v(87.81, 35.39) * mm, "end": v(87.94, 35.5) * mm});
            skLineSegment(sketch, "E3084", {"start": v(87.94, 35.5) * mm, "end": v(88.07, 35.63) * mm});
            skLineSegment(sketch, "E3085", {"start": v(88.07, 35.63) * mm, "end": v(88.2, 35.76) * mm});
            skLineSegment(sketch, "E3086", {"start": v(88.2, 35.76) * mm, "end": v(88.34, 35.88) * mm});
            skLineSegment(sketch, "E3087", {"start": v(88.34, 35.88) * mm, "end": v(88.48, 36.01) * mm});
            skLineSegment(sketch, "E3088", {"start": v(88.48, 36.01) * mm, "end": v(88.61, 36.15) * mm});
            skLineSegment(sketch, "E3089", {"start": v(88.61, 36.15) * mm, "end": v(88.75, 36.28) * mm});
            skLineSegment(sketch, "E3090", {"start": v(88.75, 36.28) * mm, "end": v(88.89, 36.42) * mm});
            skLineSegment(sketch, "E3091", {"start": v(88.89, 36.42) * mm, "end": v(89.03, 36.56) * mm});
            skLineSegment(sketch, "E3092", {"start": v(89.03, 36.56) * mm, "end": v(89.17, 36.7) * mm});
            skLineSegment(sketch, "E3093", {"start": v(89.17, 36.7) * mm, "end": v(89.3, 36.85) * mm});
            skLineSegment(sketch, "E3094", {"start": v(89.3, 36.85) * mm, "end": v(89.45, 37) * mm});
            skLineSegment(sketch, "E3095", {"start": v(89.45, 37) * mm, "end": v(89.6, 37.14) * mm});
            skLineSegment(sketch, "E3096", {"start": v(89.6, 37.14) * mm, "end": v(89.7, 37.28) * mm});
            skLineSegment(sketch, "E3097", {"start": v(89.7, 37.28) * mm, "end": v(88.86, 39.26) * mm});
            skLineSegment(sketch, "E3098", {"start": v(88.86, 39.26) * mm, "end": v(88.68, 39.28) * mm});
            skLineSegment(sketch, "E3099", {"start": v(88.68, 39.28) * mm, "end": v(88.47, 39.28) * mm});
            skLineSegment(sketch, "E3100", {"start": v(88.47, 39.28) * mm, "end": v(88.27, 39.28) * mm});
            skLineSegment(sketch, "E3101", {"start": v(88.27, 39.28) * mm, "end": v(88.06, 39.27) * mm});
            skLineSegment(sketch, "E3102", {"start": v(88.06, 39.27) * mm, "end": v(87.86, 39.27) * mm});
            skLineSegment(sketch, "E3103", {"start": v(87.86, 39.27) * mm, "end": v(87.67, 39.27) * mm});
            skLineSegment(sketch, "E3104", {"start": v(87.67, 39.27) * mm, "end": v(87.47, 39.26) * mm});
            skLineSegment(sketch, "E3105", {"start": v(87.47, 39.26) * mm, "end": v(87.28, 39.25) * mm});
            skLineSegment(sketch, "E3106", {"start": v(87.28, 39.25) * mm, "end": v(87.09, 39.25) * mm});
            skLineSegment(sketch, "E3107", {"start": v(87.09, 39.25) * mm, "end": v(86.9, 39.24) * mm});
            skLineSegment(sketch, "E3108", {"start": v(86.9, 39.24) * mm, "end": v(86.72, 39.23) * mm});
            skLineSegment(sketch, "E3109", {"start": v(86.72, 39.23) * mm, "end": v(86.53, 39.22) * mm});
            skLineSegment(sketch, "E3110", {"start": v(86.53, 39.22) * mm, "end": v(86.35, 39.2) * mm});
            skLineSegment(sketch, "E3111", {"start": v(86.35, 39.2) * mm, "end": v(86.18, 39.2) * mm});
            skLineSegment(sketch, "E3112", {"start": v(86.18, 39.2) * mm, "end": v(86, 39.19) * mm});
            skLineSegment(sketch, "E3113", {"start": v(86, 39.19) * mm, "end": v(85.83, 39.17) * mm});
            skLineSegment(sketch, "E3114", {"start": v(85.83, 39.17) * mm, "end": v(85.66, 39.16) * mm});
            skLineSegment(sketch, "E3115", {"start": v(85.66, 39.16) * mm, "end": v(85.5, 39.15) * mm});
            skLineSegment(sketch, "E3116", {"start": v(85.5, 39.15) * mm, "end": v(85.33, 39.13) * mm});
            skLineSegment(sketch, "E3117", {"start": v(85.33, 39.13) * mm, "end": v(85.17, 39.11) * mm});
            skLineSegment(sketch, "E3118", {"start": v(85.17, 39.11) * mm, "end": v(85, 39.1) * mm});
            skLineSegment(sketch, "E3119", {"start": v(85, 39.1) * mm, "end": v(84.85, 39.08) * mm});
            skLineSegment(sketch, "E3120", {"start": v(84.85, 39.08) * mm, "end": v(84.7, 39.06) * mm});
            skLineSegment(sketch, "E3121", {"start": v(84.7, 39.06) * mm, "end": v(84.54, 39.05) * mm});
            skLineSegment(sketch, "E3122", {"start": v(84.54, 39.05) * mm, "end": v(84.4, 39.03) * mm});
            skLineSegment(sketch, "E3123", {"start": v(84.4, 39.03) * mm, "end": v(84.25, 39) * mm});
            skLineSegment(sketch, "E3124", {"start": v(84.25, 39) * mm, "end": v(84.1, 39) * mm});
            skLineSegment(sketch, "E3125", {"start": v(84.1, 39) * mm, "end": v(83.96, 38.97) * mm});
            skLineSegment(sketch, "E3126", {"start": v(83.96, 38.97) * mm, "end": v(83.82, 38.95) * mm});
            skLineSegment(sketch, "E3127", {"start": v(83.82, 38.95) * mm, "end": v(83.69, 38.93) * mm});
            skLineSegment(sketch, "E3128", {"start": v(83.69, 38.93) * mm, "end": v(83.55, 38.9) * mm});
            skLineSegment(sketch, "E3129", {"start": v(83.55, 38.9) * mm, "end": v(83.42, 38.89) * mm});
            skLineSegment(sketch, "E3130", {"start": v(83.42, 38.89) * mm, "end": v(83.3, 38.87) * mm});
            skLineSegment(sketch, "E3131", {"start": v(83.3, 38.87) * mm, "end": v(83.17, 38.84) * mm});
            skLineSegment(sketch, "E3132", {"start": v(83.17, 38.84) * mm, "end": v(83.04, 38.82) * mm});
            skLineSegment(sketch, "E3133", {"start": v(83.04, 38.82) * mm, "end": v(82.92, 38.8) * mm});
            skLineSegment(sketch, "E3134", {"start": v(82.92, 38.8) * mm, "end": v(82.8, 38.78) * mm});
            skLineSegment(sketch, "E3135", {"start": v(82.8, 38.78) * mm, "end": v(82.69, 38.76) * mm});
            skLineSegment(sketch, "E3136", {"start": v(82.69, 38.76) * mm, "end": v(82.57, 38.73) * mm});
            skLineSegment(sketch, "E3137", {"start": v(82.57, 38.73) * mm, "end": v(82.2, 39.03) * mm});
            skLineSegment(sketch, "E3138", {"start": v(82.2, 39.03) * mm, "end": v(81.47, 40.55) * mm});
            skLineSegment(sketch, "E3139", {"start": v(81.47, 40.55) * mm, "end": v(81.46, 41.03) * mm});
            skLineSegment(sketch, "E3140", {"start": v(81.46, 41.03) * mm, "end": v(81.55, 41.1) * mm});
            skLineSegment(sketch, "E3141", {"start": v(81.55, 41.1) * mm, "end": v(81.64, 41.18) * mm});
            skLineSegment(sketch, "E3142", {"start": v(81.64, 41.18) * mm, "end": v(81.73, 41.26) * mm});
            skLineSegment(sketch, "E3143", {"start": v(81.73, 41.26) * mm, "end": v(81.82, 41.34) * mm});
            skLineSegment(sketch, "E3144", {"start": v(81.82, 41.34) * mm, "end": v(81.91, 41.42) * mm});
            skLineSegment(sketch, "E3145", {"start": v(81.91, 41.42) * mm, "end": v(82, 41.5) * mm});
            skLineSegment(sketch, "E3146", {"start": v(82, 41.5) * mm, "end": v(82.1, 41.6) * mm});
            skLineSegment(sketch, "E3147", {"start": v(82.1, 41.6) * mm, "end": v(82.2, 41.69) * mm});
            skLineSegment(sketch, "E3148", {"start": v(82.2, 41.69) * mm, "end": v(82.3, 41.78) * mm});
            skLineSegment(sketch, "E3149", {"start": v(82.3, 41.78) * mm, "end": v(82.4, 41.87) * mm});
            skLineSegment(sketch, "E3150", {"start": v(82.4, 41.87) * mm, "end": v(82.5, 41.97) * mm});
            skLineSegment(sketch, "E3151", {"start": v(82.5, 41.97) * mm, "end": v(82.6, 42.07) * mm});
            skLineSegment(sketch, "E3152", {"start": v(82.6, 42.07) * mm, "end": v(82.7, 42.17) * mm});
            skLineSegment(sketch, "E3153", {"start": v(82.7, 42.17) * mm, "end": v(82.82, 42.28) * mm});
            skLineSegment(sketch, "E3154", {"start": v(82.82, 42.28) * mm, "end": v(82.92, 42.38) * mm});
            skLineSegment(sketch, "E3155", {"start": v(82.92, 42.38) * mm, "end": v(83.03, 42.5) * mm});
            skLineSegment(sketch, "E3156", {"start": v(83.03, 42.5) * mm, "end": v(83.14, 42.6) * mm});
            skLineSegment(sketch, "E3157", {"start": v(83.14, 42.6) * mm, "end": v(83.25, 42.71) * mm});
            skLineSegment(sketch, "E3158", {"start": v(83.25, 42.71) * mm, "end": v(83.36, 42.83) * mm});
            skLineSegment(sketch, "E3159", {"start": v(83.36, 42.83) * mm, "end": v(83.47, 42.95) * mm});
            skLineSegment(sketch, "E3160", {"start": v(83.47, 42.95) * mm, "end": v(83.59, 43.07) * mm});
            skLineSegment(sketch, "E3161", {"start": v(83.59, 43.07) * mm, "end": v(83.7, 43.2) * mm});
            skLineSegment(sketch, "E3162", {"start": v(83.7, 43.2) * mm, "end": v(83.82, 43.32) * mm});
            skLineSegment(sketch, "E3163", {"start": v(83.82, 43.32) * mm, "end": v(83.93, 43.44) * mm});
            skLineSegment(sketch, "E3164", {"start": v(83.93, 43.44) * mm, "end": v(84.05, 43.57) * mm});
            skLineSegment(sketch, "E3165", {"start": v(84.05, 43.57) * mm, "end": v(84.17, 43.7) * mm});
            skLineSegment(sketch, "E3166", {"start": v(84.17, 43.7) * mm, "end": v(84.29, 43.84) * mm});
            skLineSegment(sketch, "E3167", {"start": v(84.29, 43.84) * mm, "end": v(84.4, 43.98) * mm});
            skLineSegment(sketch, "E3168", {"start": v(84.4, 43.98) * mm, "end": v(84.53, 44.12) * mm});
            skLineSegment(sketch, "E3169", {"start": v(84.53, 44.12) * mm, "end": v(84.65, 44.26) * mm});
            skLineSegment(sketch, "E3170", {"start": v(84.65, 44.26) * mm, "end": v(84.77, 44.4) * mm});
            skLineSegment(sketch, "E3171", {"start": v(84.77, 44.4) * mm, "end": v(84.9, 44.55) * mm});
            skLineSegment(sketch, "E3172", {"start": v(84.9, 44.55) * mm, "end": v(85.02, 44.7) * mm});
            skLineSegment(sketch, "E3173", {"start": v(85.02, 44.7) * mm, "end": v(85.15, 44.86) * mm});
            skLineSegment(sketch, "E3174", {"start": v(85.15, 44.86) * mm, "end": v(85.27, 45.01) * mm});
            skLineSegment(sketch, "E3175", {"start": v(85.27, 45.01) * mm, "end": v(85.4, 45.17) * mm});
            skLineSegment(sketch, "E3176", {"start": v(85.4, 45.17) * mm, "end": v(85.53, 45.33) * mm});
            skLineSegment(sketch, "E3177", {"start": v(85.53, 45.33) * mm, "end": v(85.66, 45.5) * mm});
            skLineSegment(sketch, "E3178", {"start": v(85.66, 45.5) * mm, "end": v(85.75, 45.64) * mm});
            skLineSegment(sketch, "E3179", {"start": v(85.75, 45.64) * mm, "end": v(84.72, 47.53) * mm});
            skLineSegment(sketch, "E3180", {"start": v(84.72, 47.53) * mm, "end": v(84.54, 47.53) * mm});
            skLineSegment(sketch, "E3181", {"start": v(84.54, 47.53) * mm, "end": v(84.34, 47.5) * mm});
            skLineSegment(sketch, "E3182", {"start": v(84.34, 47.5) * mm, "end": v(84.13, 47.49) * mm});
            skLineSegment(sketch, "E3183", {"start": v(84.13, 47.49) * mm, "end": v(83.93, 47.47) * mm});
            skLineSegment(sketch, "E3184", {"start": v(83.93, 47.47) * mm, "end": v(83.73, 47.44) * mm});
            skLineSegment(sketch, "E3185", {"start": v(83.73, 47.44) * mm, "end": v(83.54, 47.42) * mm});
            skLineSegment(sketch, "E3186", {"start": v(83.54, 47.42) * mm, "end": v(83.34, 47.4) * mm});
            skLineSegment(sketch, "E3187", {"start": v(83.34, 47.4) * mm, "end": v(83.15, 47.37) * mm});
            skLineSegment(sketch, "E3188", {"start": v(83.15, 47.37) * mm, "end": v(82.96, 47.35) * mm});
            skLineSegment(sketch, "E3189", {"start": v(82.96, 47.35) * mm, "end": v(82.78, 47.32) * mm});
            skLineSegment(sketch, "E3190", {"start": v(82.78, 47.32) * mm, "end": v(82.6, 47.3) * mm});
            skLineSegment(sketch, "E3191", {"start": v(82.6, 47.3) * mm, "end": v(82.41, 47.27) * mm});
            skLineSegment(sketch, "E3192", {"start": v(82.41, 47.27) * mm, "end": v(82.24, 47.24) * mm});
            skLineSegment(sketch, "E3193", {"start": v(82.24, 47.24) * mm, "end": v(82.06, 47.21) * mm});
            skLineSegment(sketch, "E3194", {"start": v(82.06, 47.21) * mm, "end": v(81.89, 47.18) * mm});
            skLineSegment(sketch, "E3195", {"start": v(81.89, 47.18) * mm, "end": v(81.72, 47.15) * mm});
            skLineSegment(sketch, "E3196", {"start": v(81.72, 47.15) * mm, "end": v(81.55, 47.12) * mm});
            skLineSegment(sketch, "E3197", {"start": v(81.55, 47.12) * mm, "end": v(81.39, 47.1) * mm});
            skLineSegment(sketch, "E3198", {"start": v(81.39, 47.1) * mm, "end": v(81.22, 47.06) * mm});
            skLineSegment(sketch, "E3199", {"start": v(81.22, 47.06) * mm, "end": v(81.06, 47.03) * mm});
            skLineSegment(sketch, "E3200", {"start": v(81.06, 47.03) * mm, "end": v(80.9, 47) * mm});
            skLineSegment(sketch, "E3201", {"start": v(80.9, 47) * mm, "end": v(80.75, 46.97) * mm});
            skLineSegment(sketch, "E3202", {"start": v(80.75, 46.97) * mm, "end": v(80.6, 46.94) * mm});
            skLineSegment(sketch, "E3203", {"start": v(80.6, 46.94) * mm, "end": v(80.45, 46.9) * mm});
            skLineSegment(sketch, "E3204", {"start": v(80.45, 46.9) * mm, "end": v(80.3, 46.87) * mm});
            skLineSegment(sketch, "E3205", {"start": v(80.3, 46.87) * mm, "end": v(80.16, 46.84) * mm});
            skLineSegment(sketch, "E3206", {"start": v(80.16, 46.84) * mm, "end": v(80.02, 46.8) * mm});
            skLineSegment(sketch, "E3207", {"start": v(80.02, 46.8) * mm, "end": v(79.88, 46.77) * mm});
            skLineSegment(sketch, "E3208", {"start": v(79.88, 46.77) * mm, "end": v(79.74, 46.74) * mm});
            skLineSegment(sketch, "E3209", {"start": v(79.74, 46.74) * mm, "end": v(79.6, 46.7) * mm});
            skLineSegment(sketch, "E3210", {"start": v(79.6, 46.7) * mm, "end": v(79.48, 46.68) * mm});
            skLineSegment(sketch, "E3211", {"start": v(79.48, 46.68) * mm, "end": v(79.35, 46.64) * mm});
            skLineSegment(sketch, "E3212", {"start": v(79.35, 46.64) * mm, "end": v(79.22, 46.6) * mm});
            skLineSegment(sketch, "E3213", {"start": v(79.22, 46.6) * mm, "end": v(79.1, 46.57) * mm});
            skLineSegment(sketch, "E3214", {"start": v(79.1, 46.57) * mm, "end": v(78.98, 46.54) * mm});
            skLineSegment(sketch, "E3215", {"start": v(78.98, 46.54) * mm, "end": v(78.86, 46.5) * mm});
            skLineSegment(sketch, "E3216", {"start": v(78.86, 46.5) * mm, "end": v(78.74, 46.47) * mm});
            skLineSegment(sketch, "E3217", {"start": v(78.74, 46.47) * mm, "end": v(78.63, 46.44) * mm});
            skLineSegment(sketch, "E3218", {"start": v(78.63, 46.44) * mm, "end": v(78.52, 46.4) * mm});
            skLineSegment(sketch, "E3219", {"start": v(78.52, 46.4) * mm, "end": v(78.12, 46.67) * mm});
            skLineSegment(sketch, "E3220", {"start": v(78.12, 46.67) * mm, "end": v(77.24, 48.11) * mm});
            skLineSegment(sketch, "E3221", {"start": v(77.24, 48.11) * mm, "end": v(77.19, 48.58) * mm});
            skLineSegment(sketch, "E3222", {"start": v(77.19, 48.58) * mm, "end": v(77.27, 48.67) * mm});
            skLineSegment(sketch, "E3223", {"start": v(77.27, 48.67) * mm, "end": v(77.35, 48.75) * mm});
            skLineSegment(sketch, "E3224", {"start": v(77.35, 48.75) * mm, "end": v(77.43, 48.84) * mm});
            skLineSegment(sketch, "E3225", {"start": v(77.43, 48.84) * mm, "end": v(77.52, 48.93) * mm});
            skLineSegment(sketch, "E3226", {"start": v(77.52, 48.93) * mm, "end": v(77.6, 49.02) * mm});
            skLineSegment(sketch, "E3227", {"start": v(77.6, 49.02) * mm, "end": v(77.7, 49.12) * mm});
            skLineSegment(sketch, "E3228", {"start": v(77.7, 49.12) * mm, "end": v(77.78, 49.21) * mm});
            skLineSegment(sketch, "E3229", {"start": v(77.78, 49.21) * mm, "end": v(77.87, 49.31) * mm});
            skLineSegment(sketch, "E3230", {"start": v(77.87, 49.31) * mm, "end": v(77.96, 49.41) * mm});
            skLineSegment(sketch, "E3231", {"start": v(77.96, 49.41) * mm, "end": v(78.05, 49.52) * mm});
            skLineSegment(sketch, "E3232", {"start": v(78.05, 49.52) * mm, "end": v(78.14, 49.62) * mm});
            skLineSegment(sketch, "E3233", {"start": v(78.14, 49.62) * mm, "end": v(78.23, 49.73) * mm});
            skLineSegment(sketch, "E3234", {"start": v(78.23, 49.73) * mm, "end": v(78.33, 49.84) * mm});
            skLineSegment(sketch, "E3235", {"start": v(78.33, 49.84) * mm, "end": v(78.42, 49.96) * mm});
            skLineSegment(sketch, "E3236", {"start": v(78.42, 49.96) * mm, "end": v(78.52, 50.07) * mm});
            skLineSegment(sketch, "E3237", {"start": v(78.52, 50.07) * mm, "end": v(78.61, 50.2) * mm});
            skLineSegment(sketch, "E3238", {"start": v(78.61, 50.2) * mm, "end": v(78.71, 50.31) * mm});
            skLineSegment(sketch, "E3239", {"start": v(78.71, 50.31) * mm, "end": v(78.81, 50.43) * mm});
            skLineSegment(sketch, "E3240", {"start": v(78.81, 50.43) * mm, "end": v(78.91, 50.56) * mm});
            skLineSegment(sketch, "E3241", {"start": v(78.91, 50.56) * mm, "end": v(79.01, 50.69) * mm});
            skLineSegment(sketch, "E3242", {"start": v(79.01, 50.69) * mm, "end": v(79.11, 50.82) * mm});
            skLineSegment(sketch, "E3243", {"start": v(79.11, 50.82) * mm, "end": v(79.22, 50.95) * mm});
            skLineSegment(sketch, "E3244", {"start": v(79.22, 50.95) * mm, "end": v(79.32, 51.09) * mm});
            skLineSegment(sketch, "E3245", {"start": v(79.32, 51.09) * mm, "end": v(79.42, 51.23) * mm});
            skLineSegment(sketch, "E3246", {"start": v(79.42, 51.23) * mm, "end": v(79.53, 51.37) * mm});
            skLineSegment(sketch, "E3247", {"start": v(79.53, 51.37) * mm, "end": v(79.63, 51.5) * mm});
            skLineSegment(sketch, "E3248", {"start": v(79.63, 51.5) * mm, "end": v(79.74, 51.65) * mm});
            skLineSegment(sketch, "E3249", {"start": v(79.74, 51.65) * mm, "end": v(79.85, 51.8) * mm});
            skLineSegment(sketch, "E3250", {"start": v(79.85, 51.8) * mm, "end": v(79.95, 51.95) * mm});
            skLineSegment(sketch, "E3251", {"start": v(79.95, 51.95) * mm, "end": v(80.06, 52.1) * mm});
            skLineSegment(sketch, "E3252", {"start": v(80.06, 52.1) * mm, "end": v(80.17, 52.26) * mm});
            skLineSegment(sketch, "E3253", {"start": v(80.17, 52.26) * mm, "end": v(80.28, 52.42) * mm});
            skLineSegment(sketch, "E3254", {"start": v(80.28, 52.42) * mm, "end": v(80.39, 52.58) * mm});
            skLineSegment(sketch, "E3255", {"start": v(80.39, 52.58) * mm, "end": v(80.5, 52.75) * mm});
            skLineSegment(sketch, "E3256", {"start": v(80.5, 52.75) * mm, "end": v(80.6, 52.91) * mm});
            skLineSegment(sketch, "E3257", {"start": v(80.6, 52.91) * mm, "end": v(80.72, 53.08) * mm});
            skLineSegment(sketch, "E3258", {"start": v(80.72, 53.08) * mm, "end": v(80.83, 53.25) * mm});
            skLineSegment(sketch, "E3259", {"start": v(80.83, 53.25) * mm, "end": v(80.94, 53.43) * mm});
            skLineSegment(sketch, "E3260", {"start": v(80.94, 53.43) * mm, "end": v(81.03, 53.59) * mm});
            skLineSegment(sketch, "E3261", {"start": v(81.03, 53.59) * mm, "end": v(79.82, 55.37) * mm});
            skLineSegment(sketch, "E3262", {"start": v(79.82, 55.37) * mm, "end": v(79.64, 55.35) * mm});
            skLineSegment(sketch, "E3263", {"start": v(79.64, 55.35) * mm, "end": v(79.44, 55.31) * mm});
            skLineSegment(sketch, "E3264", {"start": v(79.44, 55.31) * mm, "end": v(79.24, 55.27) * mm});
            skLineSegment(sketch, "E3265", {"start": v(79.24, 55.27) * mm, "end": v(79.04, 55.23) * mm});
            skLineSegment(sketch, "E3266", {"start": v(79.04, 55.23) * mm, "end": v(78.84, 55.19) * mm});
            skLineSegment(sketch, "E3267", {"start": v(78.84, 55.19) * mm, "end": v(78.65, 55.15) * mm});
            skLineSegment(sketch, "E3268", {"start": v(78.65, 55.15) * mm, "end": v(78.46, 55.1) * mm});
            skLineSegment(sketch, "E3269", {"start": v(78.46, 55.1) * mm, "end": v(78.27, 55.06) * mm});
            skLineSegment(sketch, "E3270", {"start": v(78.27, 55.06) * mm, "end": v(78.09, 55.02) * mm});
            skLineSegment(sketch, "E3271", {"start": v(78.09, 55.02) * mm, "end": v(77.9, 54.98) * mm});
            skLineSegment(sketch, "E3272", {"start": v(77.9, 54.98) * mm, "end": v(77.73, 54.93) * mm});
            skLineSegment(sketch, "E3273", {"start": v(77.73, 54.93) * mm, "end": v(77.55, 54.89) * mm});
            skLineSegment(sketch, "E3274", {"start": v(77.55, 54.89) * mm, "end": v(77.37, 54.84) * mm});
            skLineSegment(sketch, "E3275", {"start": v(77.37, 54.84) * mm, "end": v(77.2, 54.8) * mm});
            skLineSegment(sketch, "E3276", {"start": v(77.2, 54.8) * mm, "end": v(77.03, 54.75) * mm});
            skLineSegment(sketch, "E3277", {"start": v(77.03, 54.75) * mm, "end": v(76.87, 54.7) * mm});
            skLineSegment(sketch, "E3278", {"start": v(76.87, 54.7) * mm, "end": v(76.7, 54.66) * mm});
            skLineSegment(sketch, "E3279", {"start": v(76.7, 54.66) * mm, "end": v(76.54, 54.62) * mm});
            skLineSegment(sketch, "E3280", {"start": v(76.54, 54.62) * mm, "end": v(76.38, 54.57) * mm});
            skLineSegment(sketch, "E3281", {"start": v(76.38, 54.57) * mm, "end": v(76.23, 54.53) * mm});
            skLineSegment(sketch, "E3282", {"start": v(76.23, 54.53) * mm, "end": v(76.07, 54.48) * mm});
            skLineSegment(sketch, "E3283", {"start": v(76.07, 54.48) * mm, "end": v(75.92, 54.43) * mm});
            skLineSegment(sketch, "E3284", {"start": v(75.92, 54.43) * mm, "end": v(75.77, 54.39) * mm});
            skLineSegment(sketch, "E3285", {"start": v(75.77, 54.39) * mm, "end": v(75.63, 54.34) * mm});
            skLineSegment(sketch, "E3286", {"start": v(75.63, 54.34) * mm, "end": v(75.48, 54.3) * mm});
            skLineSegment(sketch, "E3287", {"start": v(75.48, 54.3) * mm, "end": v(75.34, 54.25) * mm});
            skLineSegment(sketch, "E3288", {"start": v(75.34, 54.25) * mm, "end": v(75.2, 54.2) * mm});
            skLineSegment(sketch, "E3289", {"start": v(75.2, 54.2) * mm, "end": v(75.07, 54.16) * mm});
            skLineSegment(sketch, "E3290", {"start": v(75.07, 54.16) * mm, "end": v(74.94, 54.1) * mm});
            skLineSegment(sketch, "E3291", {"start": v(74.94, 54.1) * mm, "end": v(74.8, 54.06) * mm});
            skLineSegment(sketch, "E3292", {"start": v(74.8, 54.06) * mm, "end": v(74.68, 54.02) * mm});
            skLineSegment(sketch, "E3293", {"start": v(74.68, 54.02) * mm, "end": v(74.55, 53.97) * mm});
            skLineSegment(sketch, "E3294", {"start": v(74.55, 53.97) * mm, "end": v(74.43, 53.93) * mm});
            skLineSegment(sketch, "E3295", {"start": v(74.43, 53.93) * mm, "end": v(74.31, 53.88) * mm});
            skLineSegment(sketch, "E3296", {"start": v(74.31, 53.88) * mm, "end": v(74.2, 53.84) * mm});
            skLineSegment(sketch, "E3297", {"start": v(74.2, 53.84) * mm, "end": v(74.08, 53.8) * mm});
            skLineSegment(sketch, "E3298", {"start": v(74.08, 53.8) * mm, "end": v(73.97, 53.75) * mm});
            skLineSegment(sketch, "E3299", {"start": v(73.97, 53.75) * mm, "end": v(73.86, 53.7) * mm});
            skLineSegment(sketch, "E3300", {"start": v(73.86, 53.7) * mm, "end": v(73.75, 53.66) * mm});
            skLineSegment(sketch, "E3301", {"start": v(73.75, 53.66) * mm, "end": v(73.33, 53.88) * mm});
            skLineSegment(sketch, "E3302", {"start": v(73.33, 53.88) * mm, "end": v(72.32, 55.24) * mm});
            skLineSegment(sketch, "E3303", {"start": v(72.32, 55.24) * mm, "end": v(72.22, 55.7) * mm});
            skLineSegment(sketch, "E3304", {"start": v(72.22, 55.7) * mm, "end": v(72.3, 55.8) * mm});
            skLineSegment(sketch, "E3305", {"start": v(72.3, 55.8) * mm, "end": v(72.37, 55.88) * mm});
            skLineSegment(sketch, "E3306", {"start": v(72.37, 55.88) * mm, "end": v(72.44, 55.98) * mm});
            skLineSegment(sketch, "E3307", {"start": v(72.44, 55.98) * mm, "end": v(72.52, 56.08) * mm});
            skLineSegment(sketch, "E3308", {"start": v(72.52, 56.08) * mm, "end": v(72.6, 56.18) * mm});
            skLineSegment(sketch, "E3309", {"start": v(72.6, 56.18) * mm, "end": v(72.67, 56.28) * mm});
            skLineSegment(sketch, "E3310", {"start": v(72.67, 56.28) * mm, "end": v(72.75, 56.38) * mm});
            skLineSegment(sketch, "E3311", {"start": v(72.75, 56.38) * mm, "end": v(72.83, 56.5) * mm});
            skLineSegment(sketch, "E3312", {"start": v(72.83, 56.5) * mm, "end": v(72.9, 56.6) * mm});
            skLineSegment(sketch, "E3313", {"start": v(72.9, 56.6) * mm, "end": v(72.99, 56.71) * mm});
            skLineSegment(sketch, "E3314", {"start": v(72.99, 56.71) * mm, "end": v(73.07, 56.83) * mm});
            skLineSegment(sketch, "E3315", {"start": v(73.07, 56.83) * mm, "end": v(73.15, 56.94) * mm});
            skLineSegment(sketch, "E3316", {"start": v(73.15, 56.94) * mm, "end": v(73.23, 57.06) * mm});
            skLineSegment(sketch, "E3317", {"start": v(73.23, 57.06) * mm, "end": v(73.32, 57.19) * mm});
            skLineSegment(sketch, "E3318", {"start": v(73.32, 57.19) * mm, "end": v(73.4, 57.3) * mm});
            skLineSegment(sketch, "E3319", {"start": v(73.4, 57.3) * mm, "end": v(73.49, 57.44) * mm});
            skLineSegment(sketch, "E3320", {"start": v(73.49, 57.44) * mm, "end": v(73.57, 57.57) * mm});
            skLineSegment(sketch, "E3321", {"start": v(73.57, 57.57) * mm, "end": v(73.66, 57.7) * mm});
            skLineSegment(sketch, "E3322", {"start": v(73.66, 57.7) * mm, "end": v(73.75, 57.83) * mm});
            skLineSegment(sketch, "E3323", {"start": v(73.75, 57.83) * mm, "end": v(73.84, 57.97) * mm});
            skLineSegment(sketch, "E3324", {"start": v(73.84, 57.97) * mm, "end": v(73.92, 58.1) * mm});
            skLineSegment(sketch, "E3325", {"start": v(73.92, 58.1) * mm, "end": v(74.01, 58.25) * mm});
            skLineSegment(sketch, "E3326", {"start": v(74.01, 58.25) * mm, "end": v(74.1, 58.4) * mm});
            skLineSegment(sketch, "E3327", {"start": v(74.1, 58.4) * mm, "end": v(74.2, 58.54) * mm});
            skLineSegment(sketch, "E3328", {"start": v(74.2, 58.54) * mm, "end": v(74.28, 58.7) * mm});
            skLineSegment(sketch, "E3329", {"start": v(74.28, 58.7) * mm, "end": v(74.38, 58.85) * mm});
            skLineSegment(sketch, "E3330", {"start": v(74.38, 58.85) * mm, "end": v(74.47, 59) * mm});
            skLineSegment(sketch, "E3331", {"start": v(74.47, 59) * mm, "end": v(74.56, 59.16) * mm});
            skLineSegment(sketch, "E3332", {"start": v(74.56, 59.16) * mm, "end": v(74.65, 59.32) * mm});
            skLineSegment(sketch, "E3333", {"start": v(74.65, 59.32) * mm, "end": v(74.75, 59.48) * mm});
            skLineSegment(sketch, "E3334", {"start": v(74.75, 59.48) * mm, "end": v(74.84, 59.65) * mm});
            skLineSegment(sketch, "E3335", {"start": v(74.84, 59.65) * mm, "end": v(74.93, 59.82) * mm});
            skLineSegment(sketch, "E3336", {"start": v(74.93, 59.82) * mm, "end": v(75.03, 59.99) * mm});
            skLineSegment(sketch, "E3337", {"start": v(75.03, 59.99) * mm, "end": v(75.12, 60.16) * mm});
            skLineSegment(sketch, "E3338", {"start": v(75.12, 60.16) * mm, "end": v(75.21, 60.34) * mm});
            skLineSegment(sketch, "E3339", {"start": v(75.21, 60.34) * mm, "end": v(75.3, 60.52) * mm});
            skLineSegment(sketch, "E3340", {"start": v(75.3, 60.52) * mm, "end": v(75.4, 60.7) * mm});
            skLineSegment(sketch, "E3341", {"start": v(75.4, 60.7) * mm, "end": v(75.5, 60.88) * mm});
            skLineSegment(sketch, "E3342", {"start": v(75.5, 60.88) * mm, "end": v(75.57, 61.05) * mm});
            skLineSegment(sketch, "E3343", {"start": v(75.57, 61.05) * mm, "end": v(74.2, 62.7) * mm});
            skLineSegment(sketch, "E3344", {"start": v(74.2, 62.7) * mm, "end": v(74.02, 62.67) * mm});
            skLineSegment(sketch, "E3345", {"start": v(74.02, 62.67) * mm, "end": v(73.82, 62.61) * mm});
            skLineSegment(sketch, "E3346", {"start": v(73.82, 62.61) * mm, "end": v(73.63, 62.55) * mm});
            skLineSegment(sketch, "E3347", {"start": v(73.63, 62.55) * mm, "end": v(73.43, 62.5) * mm});
            skLineSegment(sketch, "E3348", {"start": v(73.43, 62.5) * mm, "end": v(73.24, 62.43) * mm});
            skLineSegment(sketch, "E3349", {"start": v(73.24, 62.43) * mm, "end": v(73.05, 62.37) * mm});
            skLineSegment(sketch, "E3350", {"start": v(73.05, 62.37) * mm, "end": v(72.87, 62.31) * mm});
            skLineSegment(sketch, "E3351", {"start": v(72.87, 62.31) * mm, "end": v(72.68, 62.25) * mm});
            skLineSegment(sketch, "E3352", {"start": v(72.68, 62.25) * mm, "end": v(72.5, 62.2) * mm});
            skLineSegment(sketch, "E3353", {"start": v(72.5, 62.2) * mm, "end": v(72.33, 62.13) * mm});
            skLineSegment(sketch, "E3354", {"start": v(72.33, 62.13) * mm, "end": v(72.15, 62.07) * mm});
            skLineSegment(sketch, "E3355", {"start": v(72.15, 62.07) * mm, "end": v(71.98, 62.01) * mm});
            skLineSegment(sketch, "E3356", {"start": v(71.98, 62.01) * mm, "end": v(71.81, 61.95) * mm});
            skLineSegment(sketch, "E3357", {"start": v(71.81, 61.95) * mm, "end": v(71.64, 61.89) * mm});
            skLineSegment(sketch, "E3358", {"start": v(71.64, 61.89) * mm, "end": v(71.48, 61.83) * mm});
            skLineSegment(sketch, "E3359", {"start": v(71.48, 61.83) * mm, "end": v(71.32, 61.77) * mm});
            skLineSegment(sketch, "E3360", {"start": v(71.32, 61.77) * mm, "end": v(71.16, 61.7) * mm});
            skLineSegment(sketch, "E3361", {"start": v(71.16, 61.7) * mm, "end": v(71, 61.65) * mm});
            skLineSegment(sketch, "E3362", {"start": v(71, 61.65) * mm, "end": v(70.85, 61.59) * mm});
            skLineSegment(sketch, "E3363", {"start": v(70.85, 61.59) * mm, "end": v(70.7, 61.52) * mm});
            skLineSegment(sketch, "E3364", {"start": v(70.7, 61.52) * mm, "end": v(70.55, 61.46) * mm});
            skLineSegment(sketch, "E3365", {"start": v(70.55, 61.46) * mm, "end": v(70.4, 61.4) * mm});
            skLineSegment(sketch, "E3366", {"start": v(70.4, 61.4) * mm, "end": v(70.26, 61.34) * mm});
            skLineSegment(sketch, "E3367", {"start": v(70.26, 61.34) * mm, "end": v(70.12, 61.28) * mm});
            skLineSegment(sketch, "E3368", {"start": v(70.12, 61.28) * mm, "end": v(69.98, 61.22) * mm});
            skLineSegment(sketch, "E3369", {"start": v(69.98, 61.22) * mm, "end": v(69.85, 61.16) * mm});
            skLineSegment(sketch, "E3370", {"start": v(69.85, 61.16) * mm, "end": v(69.71, 61.1) * mm});
            skLineSegment(sketch, "E3371", {"start": v(69.71, 61.1) * mm, "end": v(69.58, 61.05) * mm});
            skLineSegment(sketch, "E3372", {"start": v(69.58, 61.05) * mm, "end": v(69.45, 60.99) * mm});
            skLineSegment(sketch, "E3373", {"start": v(69.45, 60.99) * mm, "end": v(69.33, 60.93) * mm});
            skLineSegment(sketch, "E3374", {"start": v(69.33, 60.93) * mm, "end": v(69.2, 60.87) * mm});
            skLineSegment(sketch, "E3375", {"start": v(69.2, 60.87) * mm, "end": v(69.09, 60.82) * mm});
            skLineSegment(sketch, "E3376", {"start": v(69.09, 60.82) * mm, "end": v(68.97, 60.76) * mm});
            skLineSegment(sketch, "E3377", {"start": v(68.97, 60.76) * mm, "end": v(68.85, 60.7) * mm});
            skLineSegment(sketch, "E3378", {"start": v(68.85, 60.7) * mm, "end": v(68.74, 60.65) * mm});
            skLineSegment(sketch, "E3379", {"start": v(68.74, 60.65) * mm, "end": v(68.63, 60.6) * mm});
            skLineSegment(sketch, "E3380", {"start": v(68.63, 60.6) * mm, "end": v(68.52, 60.54) * mm});
            skLineSegment(sketch, "E3381", {"start": v(68.52, 60.54) * mm, "end": v(68.42, 60.48) * mm});
            skLineSegment(sketch, "E3382", {"start": v(68.42, 60.48) * mm, "end": v(68.32, 60.43) * mm});
            skLineSegment(sketch, "E3383", {"start": v(68.32, 60.43) * mm, "end": v(67.88, 60.61) * mm});
            skLineSegment(sketch, "E3384", {"start": v(67.88, 60.61) * mm, "end": v(66.74, 61.86) * mm});
            skLineSegment(sketch, "E3385", {"start": v(66.74, 61.86) * mm, "end": v(66.6, 62.31) * mm});
            skLineSegment(sketch, "E3386", {"start": v(66.6, 62.31) * mm, "end": v(66.66, 62.41) * mm});
            skLineSegment(sketch, "E3387", {"start": v(66.66, 62.41) * mm, "end": v(66.73, 62.5) * mm});
            skLineSegment(sketch, "E3388", {"start": v(66.73, 62.5) * mm, "end": v(66.8, 62.61) * mm});
            skLineSegment(sketch, "E3389", {"start": v(66.8, 62.61) * mm, "end": v(66.86, 62.72) * mm});
            skLineSegment(sketch, "E3390", {"start": v(66.86, 62.72) * mm, "end": v(66.92, 62.82) * mm});
            skLineSegment(sketch, "E3391", {"start": v(66.92, 62.82) * mm, "end": v(67, 62.93) * mm});
            skLineSegment(sketch, "E3392", {"start": v(67, 62.93) * mm, "end": v(67.06, 63.04) * mm});
            skLineSegment(sketch, "E3393", {"start": v(67.06, 63.04) * mm, "end": v(67.13, 63.16) * mm});
            skLineSegment(sketch, "E3394", {"start": v(67.13, 63.16) * mm, "end": v(67.2, 63.27) * mm});
            skLineSegment(sketch, "E3395", {"start": v(67.2, 63.27) * mm, "end": v(67.27, 63.4) * mm});
            skLineSegment(sketch, "E3396", {"start": v(67.27, 63.4) * mm, "end": v(67.34, 63.52) * mm});
            skLineSegment(sketch, "E3397", {"start": v(67.34, 63.52) * mm, "end": v(67.4, 63.64) * mm});
            skLineSegment(sketch, "E3398", {"start": v(67.4, 63.64) * mm, "end": v(67.48, 63.77) * mm});
            skLineSegment(sketch, "E3399", {"start": v(67.48, 63.77) * mm, "end": v(67.55, 63.9) * mm});
            skLineSegment(sketch, "E3400", {"start": v(67.55, 63.9) * mm, "end": v(67.62, 64.03) * mm});
            skLineSegment(sketch, "E3401", {"start": v(67.62, 64.03) * mm, "end": v(67.7, 64.16) * mm});
            skLineSegment(sketch, "E3402", {"start": v(67.7, 64.16) * mm, "end": v(67.77, 64.3) * mm});
            skLineSegment(sketch, "E3403", {"start": v(67.77, 64.3) * mm, "end": v(67.84, 64.44) * mm});
            skLineSegment(sketch, "E3404", {"start": v(67.84, 64.44) * mm, "end": v(67.92, 64.58) * mm});
            skLineSegment(sketch, "E3405", {"start": v(67.92, 64.58) * mm, "end": v(68, 64.73) * mm});
            skLineSegment(sketch, "E3406", {"start": v(68, 64.73) * mm, "end": v(68.07, 64.87) * mm});
            skLineSegment(sketch, "E3407", {"start": v(68.07, 64.87) * mm, "end": v(68.14, 65.02) * mm});
            skLineSegment(sketch, "E3408", {"start": v(68.14, 65.02) * mm, "end": v(68.22, 65.18) * mm});
            skLineSegment(sketch, "E3409", {"start": v(68.22, 65.18) * mm, "end": v(68.3, 65.33) * mm});
            skLineSegment(sketch, "E3410", {"start": v(68.3, 65.33) * mm, "end": v(68.37, 65.49) * mm});
            skLineSegment(sketch, "E3411", {"start": v(68.37, 65.49) * mm, "end": v(68.45, 65.65) * mm});
            skLineSegment(sketch, "E3412", {"start": v(68.45, 65.65) * mm, "end": v(68.52, 65.81) * mm});
            skLineSegment(sketch, "E3413", {"start": v(68.52, 65.81) * mm, "end": v(68.6, 65.98) * mm});
            skLineSegment(sketch, "E3414", {"start": v(68.6, 65.98) * mm, "end": v(68.68, 66.15) * mm});
            skLineSegment(sketch, "E3415", {"start": v(68.68, 66.15) * mm, "end": v(68.75, 66.32) * mm});
            skLineSegment(sketch, "E3416", {"start": v(68.75, 66.32) * mm, "end": v(68.83, 66.5) * mm});
            skLineSegment(sketch, "E3417", {"start": v(68.83, 66.5) * mm, "end": v(68.9, 66.67) * mm});
            skLineSegment(sketch, "E3418", {"start": v(68.9, 66.67) * mm, "end": v(68.98, 66.85) * mm});
            skLineSegment(sketch, "E3419", {"start": v(68.98, 66.85) * mm, "end": v(69.06, 67.03) * mm});
            skLineSegment(sketch, "E3420", {"start": v(69.06, 67.03) * mm, "end": v(69.14, 67.21) * mm});
            skLineSegment(sketch, "E3421", {"start": v(69.14, 67.21) * mm, "end": v(69.22, 67.4) * mm});
            skLineSegment(sketch, "E3422", {"start": v(69.22, 67.4) * mm, "end": v(69.3, 67.59) * mm});
            skLineSegment(sketch, "E3423", {"start": v(69.3, 67.59) * mm, "end": v(69.37, 67.78) * mm});
            skLineSegment(sketch, "E3424", {"start": v(69.37, 67.78) * mm, "end": v(69.42, 67.95) * mm});
            skLineSegment(sketch, "E3425", {"start": v(69.42, 67.95) * mm, "end": v(67.9, 69.47) * mm});
            skLineSegment(sketch, "E3426", {"start": v(67.9, 69.47) * mm, "end": v(67.73, 69.42) * mm});
            skLineSegment(sketch, "E3427", {"start": v(67.73, 69.42) * mm, "end": v(67.54, 69.34) * mm});
            skLineSegment(sketch, "E3428", {"start": v(67.54, 69.34) * mm, "end": v(67.35, 69.27) * mm});
            skLineSegment(sketch, "E3429", {"start": v(67.35, 69.27) * mm, "end": v(67.16, 69.19) * mm});
            skLineSegment(sketch, "E3430", {"start": v(67.16, 69.19) * mm, "end": v(66.98, 69.11) * mm});
            skLineSegment(sketch, "E3431", {"start": v(66.98, 69.11) * mm, "end": v(66.8, 69.04) * mm});
            skLineSegment(sketch, "E3432", {"start": v(66.8, 69.04) * mm, "end": v(66.61, 68.96) * mm});
            skLineSegment(sketch, "E3433", {"start": v(66.61, 68.96) * mm, "end": v(66.44, 68.88) * mm});
            skLineSegment(sketch, "E3434", {"start": v(66.44, 68.88) * mm, "end": v(66.26, 68.8) * mm});
            skLineSegment(sketch, "E3435", {"start": v(66.26, 68.8) * mm, "end": v(66.1, 68.73) * mm});
            skLineSegment(sketch, "E3436", {"start": v(66.1, 68.73) * mm, "end": v(65.93, 68.65) * mm});
            skLineSegment(sketch, "E3437", {"start": v(65.93, 68.65) * mm, "end": v(65.76, 68.57) * mm});
            skLineSegment(sketch, "E3438", {"start": v(65.76, 68.57) * mm, "end": v(65.6, 68.5) * mm});
            skLineSegment(sketch, "E3439", {"start": v(65.6, 68.5) * mm, "end": v(65.44, 68.42) * mm});
            skLineSegment(sketch, "E3440", {"start": v(65.44, 68.42) * mm, "end": v(65.28, 68.34) * mm});
            skLineSegment(sketch, "E3441", {"start": v(65.28, 68.34) * mm, "end": v(65.12, 68.27) * mm});
            skLineSegment(sketch, "E3442", {"start": v(65.12, 68.27) * mm, "end": v(64.97, 68.2) * mm});
            skLineSegment(sketch, "E3443", {"start": v(64.97, 68.2) * mm, "end": v(64.82, 68.12) * mm});
            skLineSegment(sketch, "E3444", {"start": v(64.82, 68.12) * mm, "end": v(64.67, 68.04) * mm});
            skLineSegment(sketch, "E3445", {"start": v(64.67, 68.04) * mm, "end": v(64.53, 67.97) * mm});
            skLineSegment(sketch, "E3446", {"start": v(64.53, 67.97) * mm, "end": v(64.39, 67.9) * mm});
            skLineSegment(sketch, "E3447", {"start": v(64.39, 67.9) * mm, "end": v(64.25, 67.82) * mm});
            skLineSegment(sketch, "E3448", {"start": v(64.25, 67.82) * mm, "end": v(64.11, 67.74) * mm});
            skLineSegment(sketch, "E3449", {"start": v(64.11, 67.74) * mm, "end": v(63.98, 67.67) * mm});
            skLineSegment(sketch, "E3450", {"start": v(63.98, 67.67) * mm, "end": v(63.84, 67.6) * mm});
            skLineSegment(sketch, "E3451", {"start": v(63.84, 67.6) * mm, "end": v(63.71, 67.53) * mm});
            skLineSegment(sketch, "E3452", {"start": v(63.71, 67.53) * mm, "end": v(63.59, 67.46) * mm});
            skLineSegment(sketch, "E3453", {"start": v(63.59, 67.46) * mm, "end": v(63.46, 67.38) * mm});
            skLineSegment(sketch, "E3454", {"start": v(63.46, 67.38) * mm, "end": v(63.34, 67.31) * mm});
            skLineSegment(sketch, "E3455", {"start": v(63.34, 67.31) * mm, "end": v(63.22, 67.24) * mm});
            skLineSegment(sketch, "E3456", {"start": v(63.22, 67.24) * mm, "end": v(63.1, 67.18) * mm});
            skLineSegment(sketch, "E3457", {"start": v(63.1, 67.18) * mm, "end": v(63, 67.1) * mm});
            skLineSegment(sketch, "E3458", {"start": v(63, 67.1) * mm, "end": v(62.88, 67.04) * mm});
            skLineSegment(sketch, "E3459", {"start": v(62.88, 67.04) * mm, "end": v(62.77, 66.97) * mm});
            skLineSegment(sketch, "E3460", {"start": v(62.77, 66.97) * mm, "end": v(62.66, 66.9) * mm});
            skLineSegment(sketch, "E3461", {"start": v(62.66, 66.9) * mm, "end": v(62.56, 66.84) * mm});
            skLineSegment(sketch, "E3462", {"start": v(62.56, 66.84) * mm, "end": v(62.46, 66.78) * mm});
            skLineSegment(sketch, "E3463", {"start": v(62.46, 66.78) * mm, "end": v(62.36, 66.71) * mm});
            skLineSegment(sketch, "E3464", {"start": v(62.36, 66.71) * mm, "end": v(62.26, 66.65) * mm});
            skLineSegment(sketch, "E3465", {"start": v(62.26, 66.65) * mm, "end": v(61.8, 66.79) * mm});
            skLineSegment(sketch, "E3466", {"start": v(61.8, 66.79) * mm, "end": v(60.56, 67.92) * mm});
            skLineSegment(sketch, "E3467", {"start": v(60.56, 67.92) * mm, "end": v(60.38, 68.36) * mm});
            skLineSegment(sketch, "E3468", {"start": v(60.38, 68.36) * mm, "end": v(60.43, 68.46) * mm});
            skLineSegment(sketch, "E3469", {"start": v(60.43, 68.46) * mm, "end": v(60.48, 68.57) * mm});
            skLineSegment(sketch, "E3470", {"start": v(60.48, 68.57) * mm, "end": v(60.54, 68.68) * mm});
            skLineSegment(sketch, "E3471", {"start": v(60.54, 68.68) * mm, "end": v(60.6, 68.79) * mm});
            skLineSegment(sketch, "E3472", {"start": v(60.6, 68.79) * mm, "end": v(60.65, 68.9) * mm});
            skLineSegment(sketch, "E3473", {"start": v(60.65, 68.9) * mm, "end": v(60.7, 69.01) * mm});
            skLineSegment(sketch, "E3474", {"start": v(60.7, 69.01) * mm, "end": v(60.76, 69.13) * mm});
            skLineSegment(sketch, "E3475", {"start": v(60.76, 69.13) * mm, "end": v(60.82, 69.25) * mm});
            skLineSegment(sketch, "E3476", {"start": v(60.82, 69.25) * mm, "end": v(60.88, 69.38) * mm});
            skLineSegment(sketch, "E3477", {"start": v(60.88, 69.38) * mm, "end": v(60.94, 69.5) * mm});
            skLineSegment(sketch, "E3478", {"start": v(60.94, 69.5) * mm, "end": v(61, 69.63) * mm});
            skLineSegment(sketch, "E3479", {"start": v(61, 69.63) * mm, "end": v(61.05, 69.76) * mm});
            skLineSegment(sketch, "E3480", {"start": v(61.05, 69.76) * mm, "end": v(61.11, 69.9) * mm});
            skLineSegment(sketch, "E3481", {"start": v(61.11, 69.9) * mm, "end": v(61.17, 70.03) * mm});
            skLineSegment(sketch, "E3482", {"start": v(61.17, 70.03) * mm, "end": v(61.23, 70.17) * mm});
            skLineSegment(sketch, "E3483", {"start": v(61.23, 70.17) * mm, "end": v(61.29, 70.3) * mm});
            skLineSegment(sketch, "E3484", {"start": v(61.29, 70.3) * mm, "end": v(61.35, 70.45) * mm});
            skLineSegment(sketch, "E3485", {"start": v(61.35, 70.45) * mm, "end": v(61.41, 70.6) * mm});
            skLineSegment(sketch, "E3486", {"start": v(61.41, 70.6) * mm, "end": v(61.47, 70.74) * mm});
            skLineSegment(sketch, "E3487", {"start": v(61.47, 70.74) * mm, "end": v(61.53, 70.9) * mm});
            skLineSegment(sketch, "E3488", {"start": v(61.53, 70.9) * mm, "end": v(61.6, 71.05) * mm});
            skLineSegment(sketch, "E3489", {"start": v(61.6, 71.05) * mm, "end": v(61.65, 71.2) * mm});
            skLineSegment(sketch, "E3490", {"start": v(61.65, 71.2) * mm, "end": v(61.71, 71.36) * mm});
            skLineSegment(sketch, "E3491", {"start": v(61.71, 71.36) * mm, "end": v(61.77, 71.53) * mm});
            skLineSegment(sketch, "E3492", {"start": v(61.77, 71.53) * mm, "end": v(61.83, 71.7) * mm});
            skLineSegment(sketch, "E3493", {"start": v(61.83, 71.7) * mm, "end": v(61.9, 71.86) * mm});
            skLineSegment(sketch, "E3494", {"start": v(61.9, 71.86) * mm, "end": v(61.96, 72.03) * mm});
            skLineSegment(sketch, "E3495", {"start": v(61.96, 72.03) * mm, "end": v(62.02, 72.2) * mm});
            skLineSegment(sketch, "E3496", {"start": v(62.02, 72.2) * mm, "end": v(62.08, 72.37) * mm});
            skLineSegment(sketch, "E3497", {"start": v(62.08, 72.37) * mm, "end": v(62.14, 72.55) * mm});
            skLineSegment(sketch, "E3498", {"start": v(62.14, 72.55) * mm, "end": v(62.2, 72.73) * mm});
            skLineSegment(sketch, "E3499", {"start": v(62.2, 72.73) * mm, "end": v(62.26, 72.92) * mm});
            skLineSegment(sketch, "E3500", {"start": v(62.26, 72.92) * mm, "end": v(62.32, 73.1) * mm});
            skLineSegment(sketch, "E3501", {"start": v(62.32, 73.1) * mm, "end": v(62.38, 73.29) * mm});
            skLineSegment(sketch, "E3502", {"start": v(62.38, 73.29) * mm, "end": v(62.44, 73.48) * mm});
            skLineSegment(sketch, "E3503", {"start": v(62.44, 73.48) * mm, "end": v(62.5, 73.67) * mm});
            skLineSegment(sketch, "E3504", {"start": v(62.5, 73.67) * mm, "end": v(62.55, 73.87) * mm});
            skLineSegment(sketch, "E3505", {"start": v(62.55, 73.87) * mm, "end": v(62.61, 74.07) * mm});
            skLineSegment(sketch, "E3506", {"start": v(62.61, 74.07) * mm, "end": v(62.65, 74.24) * mm});
            skLineSegment(sketch, "E3507", {"start": v(62.65, 74.24) * mm, "end": v(60.99, 75.61) * mm});
            skLineSegment(sketch, "E3508", {"start": v(60.99, 75.61) * mm, "end": v(60.82, 75.55) * mm});
            skLineSegment(sketch, "E3509", {"start": v(60.82, 75.55) * mm, "end": v(60.64, 75.45) * mm});
            skLineSegment(sketch, "E3510", {"start": v(60.64, 75.45) * mm, "end": v(60.46, 75.36) * mm});
            skLineSegment(sketch, "E3511", {"start": v(60.46, 75.36) * mm, "end": v(60.28, 75.26) * mm});
            skLineSegment(sketch, "E3512", {"start": v(60.28, 75.26) * mm, "end": v(60.1, 75.17) * mm});
            skLineSegment(sketch, "E3513", {"start": v(60.1, 75.17) * mm, "end": v(59.93, 75.07) * mm});
            skLineSegment(sketch, "E3514", {"start": v(59.93, 75.07) * mm, "end": v(59.76, 74.98) * mm});
            skLineSegment(sketch, "E3515", {"start": v(59.76, 74.98) * mm, "end": v(59.59, 74.88) * mm});
            skLineSegment(sketch, "E3516", {"start": v(59.59, 74.88) * mm, "end": v(59.42, 74.8) * mm});
            skLineSegment(sketch, "E3517", {"start": v(59.42, 74.8) * mm, "end": v(59.26, 74.7) * mm});
            skLineSegment(sketch, "E3518", {"start": v(59.26, 74.7) * mm, "end": v(59.1, 74.6) * mm});
            skLineSegment(sketch, "E3519", {"start": v(59.1, 74.6) * mm, "end": v(58.94, 74.51) * mm});
            skLineSegment(sketch, "E3520", {"start": v(58.94, 74.51) * mm, "end": v(58.79, 74.42) * mm});
            skLineSegment(sketch, "E3521", {"start": v(58.79, 74.42) * mm, "end": v(58.64, 74.33) * mm});
            skLineSegment(sketch, "E3522", {"start": v(58.64, 74.33) * mm, "end": v(58.49, 74.24) * mm});
            skLineSegment(sketch, "E3523", {"start": v(58.49, 74.24) * mm, "end": v(58.34, 74.15) * mm});
            skLineSegment(sketch, "E3524", {"start": v(58.34, 74.15) * mm, "end": v(58.2, 74.06) * mm});
            skLineSegment(sketch, "E3525", {"start": v(58.2, 74.06) * mm, "end": v(58.05, 73.97) * mm});
            skLineSegment(sketch, "E3526", {"start": v(58.05, 73.97) * mm, "end": v(57.91, 73.88) * mm});
            skLineSegment(sketch, "E3527", {"start": v(57.91, 73.88) * mm, "end": v(57.78, 73.8) * mm});
            skLineSegment(sketch, "E3528", {"start": v(57.78, 73.8) * mm, "end": v(57.64, 73.7) * mm});
            skLineSegment(sketch, "E3529", {"start": v(57.64, 73.7) * mm, "end": v(57.5, 73.62) * mm});
            skLineSegment(sketch, "E3530", {"start": v(57.5, 73.62) * mm, "end": v(57.38, 73.53) * mm});
            skLineSegment(sketch, "E3531", {"start": v(57.38, 73.53) * mm, "end": v(57.25, 73.45) * mm});
            skLineSegment(sketch, "E3532", {"start": v(57.25, 73.45) * mm, "end": v(57.13, 73.36) * mm});
            skLineSegment(sketch, "E3533", {"start": v(57.13, 73.36) * mm, "end": v(57, 73.28) * mm});
            skLineSegment(sketch, "E3534", {"start": v(57, 73.28) * mm, "end": v(56.89, 73.2) * mm});
            skLineSegment(sketch, "E3535", {"start": v(56.89, 73.2) * mm, "end": v(56.77, 73.11) * mm});
            skLineSegment(sketch, "E3536", {"start": v(56.77, 73.11) * mm, "end": v(56.66, 73.03) * mm});
            skLineSegment(sketch, "E3537", {"start": v(56.66, 73.03) * mm, "end": v(56.54, 72.95) * mm});
            skLineSegment(sketch, "E3538", {"start": v(56.54, 72.95) * mm, "end": v(56.44, 72.87) * mm});
            skLineSegment(sketch, "E3539", {"start": v(56.44, 72.87) * mm, "end": v(56.33, 72.8) * mm});
            skLineSegment(sketch, "E3540", {"start": v(56.33, 72.8) * mm, "end": v(56.22, 72.71) * mm});
            skLineSegment(sketch, "E3541", {"start": v(56.22, 72.71) * mm, "end": v(56.12, 72.64) * mm});
            skLineSegment(sketch, "E3542", {"start": v(56.12, 72.64) * mm, "end": v(56.02, 72.56) * mm});
            skLineSegment(sketch, "E3543", {"start": v(56.02, 72.56) * mm, "end": v(55.92, 72.48) * mm});
            skLineSegment(sketch, "E3544", {"start": v(55.92, 72.48) * mm, "end": v(55.83, 72.41) * mm});
            skLineSegment(sketch, "E3545", {"start": v(55.83, 72.41) * mm, "end": v(55.74, 72.34) * mm});
            skLineSegment(sketch, "E3546", {"start": v(55.74, 72.34) * mm, "end": v(55.64, 72.26) * mm});
            skLineSegment(sketch, "E3547", {"start": v(55.64, 72.26) * mm, "end": v(55.18, 72.36) * mm});
            skLineSegment(sketch, "E3548", {"start": v(55.18, 72.36) * mm, "end": v(53.83, 73.37) * mm});
            skLineSegment(sketch, "E3549", {"start": v(53.83, 73.37) * mm, "end": v(53.6, 73.8) * mm});
            skLineSegment(sketch, "E3550", {"start": v(53.6, 73.8) * mm, "end": v(53.65, 73.9) * mm});
            skLineSegment(sketch, "E3551", {"start": v(53.65, 73.9) * mm, "end": v(53.7, 74) * mm});
            skLineSegment(sketch, "E3552", {"start": v(53.7, 74) * mm, "end": v(53.74, 74.12) * mm});
            skLineSegment(sketch, "E3553", {"start": v(53.74, 74.12) * mm, "end": v(53.78, 74.24) * mm});
            skLineSegment(sketch, "E3554", {"start": v(53.78, 74.24) * mm, "end": v(53.83, 74.35) * mm});
            skLineSegment(sketch, "E3555", {"start": v(53.83, 74.35) * mm, "end": v(53.87, 74.47) * mm});
            skLineSegment(sketch, "E3556", {"start": v(53.87, 74.47) * mm, "end": v(53.92, 74.6) * mm});
            skLineSegment(sketch, "E3557", {"start": v(53.92, 74.6) * mm, "end": v(53.96, 74.72) * mm});
            skLineSegment(sketch, "E3558", {"start": v(53.96, 74.72) * mm, "end": v(54, 74.85) * mm});
            skLineSegment(sketch, "E3559", {"start": v(54, 74.85) * mm, "end": v(54.05, 74.98) * mm});
            skLineSegment(sketch, "E3560", {"start": v(54.05, 74.98) * mm, "end": v(54.1, 75.11) * mm});
            skLineSegment(sketch, "E3561", {"start": v(54.1, 75.11) * mm, "end": v(54.14, 75.25) * mm});
            skLineSegment(sketch, "E3562", {"start": v(54.14, 75.25) * mm, "end": v(54.2, 75.38) * mm});
            skLineSegment(sketch, "E3563", {"start": v(54.2, 75.38) * mm, "end": v(54.24, 75.52) * mm});
            skLineSegment(sketch, "E3564", {"start": v(54.24, 75.52) * mm, "end": v(54.28, 75.67) * mm});
            skLineSegment(sketch, "E3565", {"start": v(54.28, 75.67) * mm, "end": v(54.33, 75.81) * mm});
            skLineSegment(sketch, "E3566", {"start": v(54.33, 75.81) * mm, "end": v(54.38, 75.96) * mm});
            skLineSegment(sketch, "E3567", {"start": v(54.38, 75.96) * mm, "end": v(54.42, 76.11) * mm});
            skLineSegment(sketch, "E3568", {"start": v(54.42, 76.11) * mm, "end": v(54.47, 76.27) * mm});
            skLineSegment(sketch, "E3569", {"start": v(54.47, 76.27) * mm, "end": v(54.51, 76.42) * mm});
            skLineSegment(sketch, "E3570", {"start": v(54.51, 76.42) * mm, "end": v(54.56, 76.58) * mm});
            skLineSegment(sketch, "E3571", {"start": v(54.56, 76.58) * mm, "end": v(54.6, 76.74) * mm});
            skLineSegment(sketch, "E3572", {"start": v(54.6, 76.74) * mm, "end": v(54.65, 76.9) * mm});
            skLineSegment(sketch, "E3573", {"start": v(54.65, 76.9) * mm, "end": v(54.7, 77.07) * mm});
            skLineSegment(sketch, "E3574", {"start": v(54.7, 77.07) * mm, "end": v(54.74, 77.24) * mm});
            skLineSegment(sketch, "E3575", {"start": v(54.74, 77.24) * mm, "end": v(54.78, 77.42) * mm});
            skLineSegment(sketch, "E3576", {"start": v(54.78, 77.42) * mm, "end": v(54.83, 77.6) * mm});
            skLineSegment(sketch, "E3577", {"start": v(54.83, 77.6) * mm, "end": v(54.87, 77.77) * mm});
            skLineSegment(sketch, "E3578", {"start": v(54.87, 77.77) * mm, "end": v(54.92, 77.95) * mm});
            skLineSegment(sketch, "E3579", {"start": v(54.92, 77.95) * mm, "end": v(54.96, 78.13) * mm});
            skLineSegment(sketch, "E3580", {"start": v(54.96, 78.13) * mm, "end": v(55, 78.32) * mm});
            skLineSegment(sketch, "E3581", {"start": v(55, 78.32) * mm, "end": v(55.04, 78.5) * mm});
            skLineSegment(sketch, "E3582", {"start": v(55.04, 78.5) * mm, "end": v(55.09, 78.7) * mm});
            skLineSegment(sketch, "E3583", {"start": v(55.09, 78.7) * mm, "end": v(55.13, 78.89) * mm});
            skLineSegment(sketch, "E3584", {"start": v(55.13, 78.89) * mm, "end": v(55.17, 79.08) * mm});
            skLineSegment(sketch, "E3585", {"start": v(55.17, 79.08) * mm, "end": v(55.2, 79.28) * mm});
            skLineSegment(sketch, "E3586", {"start": v(55.2, 79.28) * mm, "end": v(55.25, 79.48) * mm});
            skLineSegment(sketch, "E3587", {"start": v(55.25, 79.48) * mm, "end": v(55.29, 79.69) * mm});
            skLineSegment(sketch, "E3588", {"start": v(55.29, 79.69) * mm, "end": v(55.3, 79.86) * mm});
            skLineSegment(sketch, "E3589", {"start": v(55.3, 79.86) * mm, "end": v(53.52, 81.07) * mm});
            skLineSegment(sketch, "E3590", {"start": v(53.52, 81.07) * mm, "end": v(53.37, 80.99) * mm});
            skLineSegment(sketch, "E3591", {"start": v(53.37, 80.99) * mm, "end": v(53.2, 80.87) * mm});
            skLineSegment(sketch, "E3592", {"start": v(53.2, 80.87) * mm, "end": v(53.02, 80.76) * mm});
            skLineSegment(sketch, "E3593", {"start": v(53.02, 80.76) * mm, "end": v(52.85, 80.65) * mm});
            skLineSegment(sketch, "E3594", {"start": v(52.85, 80.65) * mm, "end": v(52.69, 80.54) * mm});
            skLineSegment(sketch, "E3595", {"start": v(52.69, 80.54) * mm, "end": v(52.52, 80.43) * mm});
            skLineSegment(sketch, "E3596", {"start": v(52.52, 80.43) * mm, "end": v(52.36, 80.32) * mm});
            skLineSegment(sketch, "E3597", {"start": v(52.36, 80.32) * mm, "end": v(52.2, 80.2) * mm});
            skLineSegment(sketch, "E3598", {"start": v(52.2, 80.2) * mm, "end": v(52.05, 80.1) * mm});
            skLineSegment(sketch, "E3599", {"start": v(52.05, 80.1) * mm, "end": v(51.9, 80) * mm});
            skLineSegment(sketch, "E3600", {"start": v(51.9, 80) * mm, "end": v(51.74, 79.88) * mm});
            skLineSegment(sketch, "E3601", {"start": v(51.74, 79.88) * mm, "end": v(51.6, 79.78) * mm});
            skLineSegment(sketch, "E3602", {"start": v(51.6, 79.78) * mm, "end": v(51.45, 79.67) * mm});
            skLineSegment(sketch, "E3603", {"start": v(51.45, 79.67) * mm, "end": v(51.3, 79.57) * mm});
            skLineSegment(sketch, "E3604", {"start": v(51.3, 79.57) * mm, "end": v(51.16, 79.46) * mm});
            skLineSegment(sketch, "E3605", {"start": v(51.16, 79.46) * mm, "end": v(51.03, 79.36) * mm});
            skLineSegment(sketch, "E3606", {"start": v(51.03, 79.36) * mm, "end": v(50.9, 79.25) * mm});
            skLineSegment(sketch, "E3607", {"start": v(50.9, 79.25) * mm, "end": v(50.76, 79.15) * mm});
            skLineSegment(sketch, "E3608", {"start": v(50.76, 79.15) * mm, "end": v(50.63, 79.05) * mm});
            skLineSegment(sketch, "E3609", {"start": v(50.63, 79.05) * mm, "end": v(50.5, 78.95) * mm});
            skLineSegment(sketch, "E3610", {"start": v(50.5, 78.95) * mm, "end": v(50.37, 78.85) * mm});
            skLineSegment(sketch, "E3611", {"start": v(50.37, 78.85) * mm, "end": v(50.25, 78.75) * mm});
            skLineSegment(sketch, "E3612", {"start": v(50.25, 78.75) * mm, "end": v(50.13, 78.65) * mm});
            skLineSegment(sketch, "E3613", {"start": v(50.13, 78.65) * mm, "end": v(50.01, 78.56) * mm});
            skLineSegment(sketch, "E3614", {"start": v(50.01, 78.56) * mm, "end": v(49.9, 78.46) * mm});
            skLineSegment(sketch, "E3615", {"start": v(49.9, 78.46) * mm, "end": v(49.78, 78.36) * mm});
            skLineSegment(sketch, "E3616", {"start": v(49.78, 78.36) * mm, "end": v(49.67, 78.27) * mm});
            skLineSegment(sketch, "E3617", {"start": v(49.67, 78.27) * mm, "end": v(49.56, 78.18) * mm});
            skLineSegment(sketch, "E3618", {"start": v(49.56, 78.18) * mm, "end": v(49.46, 78.09) * mm});
            skLineSegment(sketch, "E3619", {"start": v(49.46, 78.09) * mm, "end": v(49.35, 78) * mm});
            skLineSegment(sketch, "E3620", {"start": v(49.35, 78) * mm, "end": v(49.25, 77.9) * mm});
            skLineSegment(sketch, "E3621", {"start": v(49.25, 77.9) * mm, "end": v(49.15, 77.82) * mm});
            skLineSegment(sketch, "E3622", {"start": v(49.15, 77.82) * mm, "end": v(49.06, 77.73) * mm});
            skLineSegment(sketch, "E3623", {"start": v(49.06, 77.73) * mm, "end": v(48.96, 77.64) * mm});
            skLineSegment(sketch, "E3624", {"start": v(48.96, 77.64) * mm, "end": v(48.87, 77.56) * mm});
            skLineSegment(sketch, "E3625", {"start": v(48.87, 77.56) * mm, "end": v(48.78, 77.47) * mm});
            skLineSegment(sketch, "E3626", {"start": v(48.78, 77.47) * mm, "end": v(48.7, 77.39) * mm});
            skLineSegment(sketch, "E3627", {"start": v(48.7, 77.39) * mm, "end": v(48.6, 77.3) * mm});
            skLineSegment(sketch, "E3628", {"start": v(48.6, 77.3) * mm, "end": v(48.52, 77.23) * mm});
            skLineSegment(sketch, "E3629", {"start": v(48.52, 77.23) * mm, "end": v(48.05, 77.28) * mm});
            skLineSegment(sketch, "E3630", {"start": v(48.05, 77.28) * mm, "end": v(46.61, 78.16) * mm});
            skLineSegment(sketch, "E3631", {"start": v(46.61, 78.16) * mm, "end": v(46.35, 78.55) * mm});
            skLineSegment(sketch, "E3632", {"start": v(46.35, 78.55) * mm, "end": v(46.38, 78.66) * mm});
            skLineSegment(sketch, "E3633", {"start": v(46.38, 78.66) * mm, "end": v(46.41, 78.78) * mm});
            skLineSegment(sketch, "E3634", {"start": v(46.41, 78.78) * mm, "end": v(46.45, 78.9) * mm});
            skLineSegment(sketch, "E3635", {"start": v(46.45, 78.9) * mm, "end": v(46.48, 79.01) * mm});
            skLineSegment(sketch, "E3636", {"start": v(46.48, 79.01) * mm, "end": v(46.51, 79.13) * mm});
            skLineSegment(sketch, "E3637", {"start": v(46.51, 79.13) * mm, "end": v(46.55, 79.26) * mm});
            skLineSegment(sketch, "E3638", {"start": v(46.55, 79.26) * mm, "end": v(46.58, 79.38) * mm});
            skLineSegment(sketch, "E3639", {"start": v(46.58, 79.38) * mm, "end": v(46.61, 79.51) * mm});
            skLineSegment(sketch, "E3640", {"start": v(46.61, 79.51) * mm, "end": v(46.65, 79.64) * mm});
            skLineSegment(sketch, "E3641", {"start": v(46.65, 79.64) * mm, "end": v(46.68, 79.78) * mm});
            skLineSegment(sketch, "E3642", {"start": v(46.68, 79.78) * mm, "end": v(46.71, 79.91) * mm});
            skLineSegment(sketch, "E3643", {"start": v(46.71, 79.91) * mm, "end": v(46.75, 80.05) * mm});
            skLineSegment(sketch, "E3644", {"start": v(46.75, 80.05) * mm, "end": v(46.78, 80.2) * mm});
            skLineSegment(sketch, "E3645", {"start": v(46.78, 80.2) * mm, "end": v(46.81, 80.34) * mm});
            skLineSegment(sketch, "E3646", {"start": v(46.81, 80.34) * mm, "end": v(46.84, 80.49) * mm});
            skLineSegment(sketch, "E3647", {"start": v(46.84, 80.49) * mm, "end": v(46.88, 80.63) * mm});
            skLineSegment(sketch, "E3648", {"start": v(46.88, 80.63) * mm, "end": v(46.9, 80.79) * mm});
            skLineSegment(sketch, "E3649", {"start": v(46.9, 80.79) * mm, "end": v(46.94, 80.94) * mm});
            skLineSegment(sketch, "E3650", {"start": v(46.94, 80.94) * mm, "end": v(46.97, 81.1) * mm});
            skLineSegment(sketch, "E3651", {"start": v(46.97, 81.1) * mm, "end": v(47, 81.26) * mm});
            skLineSegment(sketch, "E3652", {"start": v(47, 81.26) * mm, "end": v(47.03, 81.42) * mm});
            skLineSegment(sketch, "E3653", {"start": v(47.03, 81.42) * mm, "end": v(47.06, 81.59) * mm});
            skLineSegment(sketch, "E3654", {"start": v(47.06, 81.59) * mm, "end": v(47.1, 81.75) * mm});
            skLineSegment(sketch, "E3655", {"start": v(47.1, 81.75) * mm, "end": v(47.12, 81.92) * mm});
            skLineSegment(sketch, "E3656", {"start": v(47.12, 81.92) * mm, "end": v(47.15, 82.1) * mm});
            skLineSegment(sketch, "E3657", {"start": v(47.15, 82.1) * mm, "end": v(47.18, 82.27) * mm});
            skLineSegment(sketch, "E3658", {"start": v(47.18, 82.27) * mm, "end": v(47.2, 82.45) * mm});
            skLineSegment(sketch, "E3659", {"start": v(47.2, 82.45) * mm, "end": v(47.23, 82.63) * mm});
            skLineSegment(sketch, "E3660", {"start": v(47.23, 82.63) * mm, "end": v(47.26, 82.81) * mm});
            skLineSegment(sketch, "E3661", {"start": v(47.26, 82.81) * mm, "end": v(47.28, 83) * mm});
            skLineSegment(sketch, "E3662", {"start": v(47.28, 83) * mm, "end": v(47.3, 83.19) * mm});
            skLineSegment(sketch, "E3663", {"start": v(47.3, 83.19) * mm, "end": v(47.33, 83.38) * mm});
            skLineSegment(sketch, "E3664", {"start": v(47.33, 83.38) * mm, "end": v(47.36, 83.57) * mm});
            skLineSegment(sketch, "E3665", {"start": v(47.36, 83.57) * mm, "end": v(47.38, 83.77) * mm});
            skLineSegment(sketch, "E3666", {"start": v(47.38, 83.77) * mm, "end": v(47.4, 83.97) * mm});
            skLineSegment(sketch, "E3667", {"start": v(47.4, 83.97) * mm, "end": v(47.42, 84.17) * mm});
            skLineSegment(sketch, "E3668", {"start": v(47.42, 84.17) * mm, "end": v(47.44, 84.37) * mm});
            skLineSegment(sketch, "E3669", {"start": v(47.44, 84.37) * mm, "end": v(47.46, 84.58) * mm});
            skLineSegment(sketch, "E3670", {"start": v(47.46, 84.58) * mm, "end": v(47.46, 84.76) * mm});
            skLineSegment(sketch, "E3671", {"start": v(47.46, 84.76) * mm, "end": v(45.58, 85.79) * mm});
            skLineSegment(sketch, "E3672", {"start": v(45.58, 85.79) * mm, "end": v(45.43, 85.7) * mm});
            skLineSegment(sketch, "E3673", {"start": v(45.43, 85.7) * mm, "end": v(45.26, 85.56) * mm});
            skLineSegment(sketch, "E3674", {"start": v(45.26, 85.56) * mm, "end": v(45.1, 85.44) * mm});
            skLineSegment(sketch, "E3675", {"start": v(45.1, 85.44) * mm, "end": v(44.95, 85.3) * mm});
            skLineSegment(sketch, "E3676", {"start": v(44.95, 85.3) * mm, "end": v(44.8, 85.18) * mm});
            skLineSegment(sketch, "E3677", {"start": v(44.8, 85.18) * mm, "end": v(44.64, 85.06) * mm});
            skLineSegment(sketch, "E3678", {"start": v(44.64, 85.06) * mm, "end": v(44.49, 84.93) * mm});
            skLineSegment(sketch, "E3679", {"start": v(44.49, 84.93) * mm, "end": v(44.34, 84.8) * mm});
            skLineSegment(sketch, "E3680", {"start": v(44.34, 84.8) * mm, "end": v(44.2, 84.69) * mm});
            skLineSegment(sketch, "E3681", {"start": v(44.2, 84.69) * mm, "end": v(44.05, 84.56) * mm});
            skLineSegment(sketch, "E3682", {"start": v(44.05, 84.56) * mm, "end": v(43.91, 84.44) * mm});
            skLineSegment(sketch, "E3683", {"start": v(43.91, 84.44) * mm, "end": v(43.78, 84.32) * mm});
            skLineSegment(sketch, "E3684", {"start": v(43.78, 84.32) * mm, "end": v(43.64, 84.2) * mm});
            skLineSegment(sketch, "E3685", {"start": v(43.64, 84.2) * mm, "end": v(43.5, 84.08) * mm});
            skLineSegment(sketch, "E3686", {"start": v(43.5, 84.08) * mm, "end": v(43.38, 83.97) * mm});
            skLineSegment(sketch, "E3687", {"start": v(43.38, 83.97) * mm, "end": v(43.25, 83.85) * mm});
            skLineSegment(sketch, "E3688", {"start": v(43.25, 83.85) * mm, "end": v(43.13, 83.73) * mm});
            skLineSegment(sketch, "E3689", {"start": v(43.13, 83.73) * mm, "end": v(43, 83.62) * mm});
            skLineSegment(sketch, "E3690", {"start": v(43, 83.62) * mm, "end": v(42.88, 83.5) * mm});
            skLineSegment(sketch, "E3691", {"start": v(42.88, 83.5) * mm, "end": v(42.77, 83.4) * mm});
            skLineSegment(sketch, "E3692", {"start": v(42.77, 83.4) * mm, "end": v(42.65, 83.28) * mm});
            skLineSegment(sketch, "E3693", {"start": v(42.65, 83.28) * mm, "end": v(42.54, 83.17) * mm});
            skLineSegment(sketch, "E3694", {"start": v(42.54, 83.17) * mm, "end": v(42.43, 83.06) * mm});
            skLineSegment(sketch, "E3695", {"start": v(42.43, 83.06) * mm, "end": v(42.32, 82.95) * mm});
            skLineSegment(sketch, "E3696", {"start": v(42.32, 82.95) * mm, "end": v(42.21, 82.85) * mm});
            skLineSegment(sketch, "E3697", {"start": v(42.21, 82.85) * mm, "end": v(42.1, 82.74) * mm});
            skLineSegment(sketch, "E3698", {"start": v(42.1, 82.74) * mm, "end": v(42, 82.64) * mm});
            skLineSegment(sketch, "E3699", {"start": v(42, 82.64) * mm, "end": v(41.9, 82.53) * mm});
            skLineSegment(sketch, "E3700", {"start": v(41.9, 82.53) * mm, "end": v(41.81, 82.43) * mm});
            skLineSegment(sketch, "E3701", {"start": v(41.81, 82.43) * mm, "end": v(41.72, 82.33) * mm});
            skLineSegment(sketch, "E3702", {"start": v(41.72, 82.33) * mm, "end": v(41.62, 82.23) * mm});
            skLineSegment(sketch, "E3703", {"start": v(41.62, 82.23) * mm, "end": v(41.53, 82.14) * mm});
            skLineSegment(sketch, "E3704", {"start": v(41.53, 82.14) * mm, "end": v(41.45, 82.04) * mm});
            skLineSegment(sketch, "E3705", {"start": v(41.45, 82.04) * mm, "end": v(41.36, 81.94) * mm});
            skLineSegment(sketch, "E3706", {"start": v(41.36, 81.94) * mm, "end": v(41.28, 81.85) * mm});
            skLineSegment(sketch, "E3707", {"start": v(41.28, 81.85) * mm, "end": v(41.2, 81.76) * mm});
            skLineSegment(sketch, "E3708", {"start": v(41.2, 81.76) * mm, "end": v(41.12, 81.67) * mm});
            skLineSegment(sketch, "E3709", {"start": v(41.12, 81.67) * mm, "end": v(41.04, 81.58) * mm});
            skLineSegment(sketch, "E3710", {"start": v(41.04, 81.58) * mm, "end": v(40.96, 81.49) * mm});
            skLineSegment(sketch, "E3711", {"start": v(40.96, 81.49) * mm, "end": v(40.49, 81.5) * mm});
            skLineSegment(sketch, "E3712", {"start": v(40.49, 81.5) * mm, "end": v(38.97, 82.23) * mm});
            skLineSegment(sketch, "E3713", {"start": v(38.97, 82.23) * mm, "end": v(38.67, 82.6) * mm});
            skLineSegment(sketch, "E3714", {"start": v(38.67, 82.6) * mm, "end": v(38.7, 82.72) * mm});
            skLineSegment(sketch, "E3715", {"start": v(38.7, 82.72) * mm, "end": v(38.72, 82.83) * mm});
            skLineSegment(sketch, "E3716", {"start": v(38.72, 82.83) * mm, "end": v(38.74, 82.95) * mm});
            skLineSegment(sketch, "E3717", {"start": v(38.74, 82.95) * mm, "end": v(38.76, 83.07) * mm});
            skLineSegment(sketch, "E3718", {"start": v(38.76, 83.07) * mm, "end": v(38.78, 83.2) * mm});
            skLineSegment(sketch, "E3719", {"start": v(38.78, 83.2) * mm, "end": v(38.8, 83.32) * mm});
            skLineSegment(sketch, "E3720", {"start": v(38.8, 83.32) * mm, "end": v(38.82, 83.45) * mm});
            skLineSegment(sketch, "E3721", {"start": v(38.82, 83.45) * mm, "end": v(38.85, 83.58) * mm});
            skLineSegment(sketch, "E3722", {"start": v(38.85, 83.58) * mm, "end": v(38.87, 83.72) * mm});
            skLineSegment(sketch, "E3723", {"start": v(38.87, 83.72) * mm, "end": v(38.89, 83.85) * mm});
            skLineSegment(sketch, "E3724", {"start": v(38.89, 83.85) * mm, "end": v(38.9, 84) * mm});
            skLineSegment(sketch, "E3725", {"start": v(38.9, 84) * mm, "end": v(38.93, 84.13) * mm});
            skLineSegment(sketch, "E3726", {"start": v(38.93, 84.13) * mm, "end": v(38.95, 84.28) * mm});
            skLineSegment(sketch, "E3727", {"start": v(38.95, 84.28) * mm, "end": v(38.96, 84.42) * mm});
            skLineSegment(sketch, "E3728", {"start": v(38.96, 84.42) * mm, "end": v(38.98, 84.57) * mm});
            skLineSegment(sketch, "E3729", {"start": v(38.98, 84.57) * mm, "end": v(39, 84.73) * mm});
            skLineSegment(sketch, "E3730", {"start": v(39, 84.73) * mm, "end": v(39.02, 84.88) * mm});
            skLineSegment(sketch, "E3731", {"start": v(39.02, 84.88) * mm, "end": v(39.03, 85.04) * mm});
            skLineSegment(sketch, "E3732", {"start": v(39.03, 85.04) * mm, "end": v(39.05, 85.2) * mm});
            skLineSegment(sketch, "E3733", {"start": v(39.05, 85.2) * mm, "end": v(39.07, 85.36) * mm});
            skLineSegment(sketch, "E3734", {"start": v(39.07, 85.36) * mm, "end": v(39.08, 85.52) * mm});
            skLineSegment(sketch, "E3735", {"start": v(39.08, 85.52) * mm, "end": v(39.1, 85.7) * mm});
            skLineSegment(sketch, "E3736", {"start": v(39.1, 85.7) * mm, "end": v(39.1, 85.86) * mm});
            skLineSegment(sketch, "E3737", {"start": v(39.1, 85.86) * mm, "end": v(39.12, 86.03) * mm});
            skLineSegment(sketch, "E3738", {"start": v(39.12, 86.03) * mm, "end": v(39.13, 86.2) * mm});
            skLineSegment(sketch, "E3739", {"start": v(39.13, 86.2) * mm, "end": v(39.14, 86.38) * mm});
            skLineSegment(sketch, "E3740", {"start": v(39.14, 86.38) * mm, "end": v(39.15, 86.56) * mm});
            skLineSegment(sketch, "E3741", {"start": v(39.15, 86.56) * mm, "end": v(39.16, 86.75) * mm});
            skLineSegment(sketch, "E3742", {"start": v(39.16, 86.75) * mm, "end": v(39.17, 86.93) * mm});
            skLineSegment(sketch, "E3743", {"start": v(39.17, 86.93) * mm, "end": v(39.18, 87.12) * mm});
            skLineSegment(sketch, "E3744", {"start": v(39.18, 87.12) * mm, "end": v(39.19, 87.3) * mm});
            skLineSegment(sketch, "E3745", {"start": v(39.19, 87.3) * mm, "end": v(39.2, 87.5) * mm});
            skLineSegment(sketch, "E3746", {"start": v(39.2, 87.5) * mm, "end": v(39.2, 87.7) * mm});
            skLineSegment(sketch, "E3747", {"start": v(39.2, 87.7) * mm, "end": v(39.2, 87.9) * mm});
            skLineSegment(sketch, "E3748", {"start": v(39.2, 87.9) * mm, "end": v(39.2, 88.1) * mm});
            skLineSegment(sketch, "E3749", {"start": v(39.2, 88.1) * mm, "end": v(39.2, 88.3) * mm});
            skLineSegment(sketch, "E3750", {"start": v(39.2, 88.3) * mm, "end": v(39.2, 88.5) * mm});
            skLineSegment(sketch, "E3751", {"start": v(39.2, 88.5) * mm, "end": v(39.2, 88.7) * mm});
            skLineSegment(sketch, "E3752", {"start": v(39.2, 88.7) * mm, "end": v(39.2, 88.89) * mm});
            skLineSegment(sketch, "E3753", {"start": v(39.2, 88.89) * mm, "end": v(37.21, 89.73) * mm});
            skLineSegment(sketch, "E3754", {"start": v(37.21, 89.73) * mm, "end": v(37.08, 89.62) * mm});
            skLineSegment(sketch, "E3755", {"start": v(37.08, 89.62) * mm, "end": v(36.93, 89.48) * mm});
            skLineSegment(sketch, "E3756", {"start": v(36.93, 89.48) * mm, "end": v(36.78, 89.34) * mm});
            skLineSegment(sketch, "E3757", {"start": v(36.78, 89.34) * mm, "end": v(36.63, 89.2) * mm});
            skLineSegment(sketch, "E3758", {"start": v(36.63, 89.2) * mm, "end": v(36.5, 89.05) * mm});
            skLineSegment(sketch, "E3759", {"start": v(36.5, 89.05) * mm, "end": v(36.35, 88.91) * mm});
            skLineSegment(sketch, "E3760", {"start": v(36.35, 88.91) * mm, "end": v(36.21, 88.78) * mm});
            skLineSegment(sketch, "E3761", {"start": v(36.21, 88.78) * mm, "end": v(36.08, 88.64) * mm});
            skLineSegment(sketch, "E3762", {"start": v(36.08, 88.64) * mm, "end": v(35.95, 88.5) * mm});
            skLineSegment(sketch, "E3763", {"start": v(35.95, 88.5) * mm, "end": v(35.82, 88.37) * mm});
            skLineSegment(sketch, "E3764", {"start": v(35.82, 88.37) * mm, "end": v(35.69, 88.23) * mm});
            skLineSegment(sketch, "E3765", {"start": v(35.69, 88.23) * mm, "end": v(35.56, 88.1) * mm});
            skLineSegment(sketch, "E3766", {"start": v(35.56, 88.1) * mm, "end": v(35.44, 87.97) * mm});
            skLineSegment(sketch, "E3767", {"start": v(35.44, 87.97) * mm, "end": v(35.32, 87.84) * mm});
            skLineSegment(sketch, "E3768", {"start": v(35.32, 87.84) * mm, "end": v(35.2, 87.7) * mm});
            skLineSegment(sketch, "E3769", {"start": v(35.2, 87.7) * mm, "end": v(35.09, 87.58) * mm});
            skLineSegment(sketch, "E3770", {"start": v(35.09, 87.58) * mm, "end": v(34.97, 87.45) * mm});
            skLineSegment(sketch, "E3771", {"start": v(34.97, 87.45) * mm, "end": v(34.86, 87.33) * mm});
            skLineSegment(sketch, "E3772", {"start": v(34.86, 87.33) * mm, "end": v(34.75, 87.2) * mm});
            skLineSegment(sketch, "E3773", {"start": v(34.75, 87.2) * mm, "end": v(34.65, 87.08) * mm});
            skLineSegment(sketch, "E3774", {"start": v(34.65, 87.08) * mm, "end": v(34.54, 86.96) * mm});
            skLineSegment(sketch, "E3775", {"start": v(34.54, 86.96) * mm, "end": v(34.44, 86.84) * mm});
            skLineSegment(sketch, "E3776", {"start": v(34.44, 86.84) * mm, "end": v(34.34, 86.72) * mm});
            skLineSegment(sketch, "E3777", {"start": v(34.34, 86.72) * mm, "end": v(34.24, 86.6) * mm});
            skLineSegment(sketch, "E3778", {"start": v(34.24, 86.6) * mm, "end": v(34.15, 86.48) * mm});
            skLineSegment(sketch, "E3779", {"start": v(34.15, 86.48) * mm, "end": v(34.05, 86.37) * mm});
            skLineSegment(sketch, "E3780", {"start": v(34.05, 86.37) * mm, "end": v(33.96, 86.26) * mm});
            skLineSegment(sketch, "E3781", {"start": v(33.96, 86.26) * mm, "end": v(33.87, 86.14) * mm});
            skLineSegment(sketch, "E3782", {"start": v(33.87, 86.14) * mm, "end": v(33.79, 86.03) * mm});
            skLineSegment(sketch, "E3783", {"start": v(33.79, 86.03) * mm, "end": v(33.7, 85.93) * mm});
            skLineSegment(sketch, "E3784", {"start": v(33.7, 85.93) * mm, "end": v(33.62, 85.82) * mm});
            skLineSegment(sketch, "E3785", {"start": v(33.62, 85.82) * mm, "end": v(33.54, 85.71) * mm});
            skLineSegment(sketch, "E3786", {"start": v(33.54, 85.71) * mm, "end": v(33.46, 85.6) * mm});
            skLineSegment(sketch, "E3787", {"start": v(33.46, 85.6) * mm, "end": v(33.38, 85.5) * mm});
            skLineSegment(sketch, "E3788", {"start": v(33.38, 85.5) * mm, "end": v(33.3, 85.4) * mm});
            skLineSegment(sketch, "E3789", {"start": v(33.3, 85.4) * mm, "end": v(33.24, 85.3) * mm});
            skLineSegment(sketch, "E3790", {"start": v(33.24, 85.3) * mm, "end": v(33.17, 85.2) * mm});
            skLineSegment(sketch, "E3791", {"start": v(33.17, 85.2) * mm, "end": v(33.1, 85.1) * mm});
            skLineSegment(sketch, "E3792", {"start": v(33.1, 85.1) * mm, "end": v(33.03, 85.01) * mm});
            skLineSegment(sketch, "E3793", {"start": v(33.03, 85.01) * mm, "end": v(32.56, 84.98) * mm});
            skLineSegment(sketch, "E3794", {"start": v(32.56, 84.98) * mm, "end": v(30.98, 85.57) * mm});
            skLineSegment(sketch, "E3795", {"start": v(30.98, 85.57) * mm, "end": v(30.64, 85.9) * mm});
            skLineSegment(sketch, "E3796", {"start": v(30.64, 85.9) * mm, "end": v(30.66, 86.02) * mm});
            skLineSegment(sketch, "E3797", {"start": v(30.66, 86.02) * mm, "end": v(30.67, 86.14) * mm});
            skLineSegment(sketch, "E3798", {"start": v(30.67, 86.14) * mm, "end": v(30.68, 86.26) * mm});
            skLineSegment(sketch, "E3799", {"start": v(30.68, 86.26) * mm, "end": v(30.69, 86.38) * mm});
            skLineSegment(sketch, "E3800", {"start": v(30.69, 86.38) * mm, "end": v(30.7, 86.5) * mm});
            skLineSegment(sketch, "E3801", {"start": v(30.7, 86.5) * mm, "end": v(30.7, 86.63) * mm});
            skLineSegment(sketch, "E3802", {"start": v(30.7, 86.63) * mm, "end": v(30.72, 86.76) * mm});
            skLineSegment(sketch, "E3803", {"start": v(30.72, 86.76) * mm, "end": v(30.72, 86.9) * mm});
            skLineSegment(sketch, "E3804", {"start": v(30.72, 86.9) * mm, "end": v(30.73, 87.03) * mm});
            skLineSegment(sketch, "E3805", {"start": v(30.73, 87.03) * mm, "end": v(30.74, 87.17) * mm});
            skLineSegment(sketch, "E3806", {"start": v(30.74, 87.17) * mm, "end": v(30.75, 87.3) * mm});
            skLineSegment(sketch, "E3807", {"start": v(30.75, 87.3) * mm, "end": v(30.75, 87.45) * mm});
            skLineSegment(sketch, "E3808", {"start": v(30.75, 87.45) * mm, "end": v(30.76, 87.6) * mm});
            skLineSegment(sketch, "E3809", {"start": v(30.76, 87.6) * mm, "end": v(30.76, 87.75) * mm});
            skLineSegment(sketch, "E3810", {"start": v(30.76, 87.75) * mm, "end": v(30.77, 87.9) * mm});
            skLineSegment(sketch, "E3811", {"start": v(30.77, 87.9) * mm, "end": v(30.77, 88.05) * mm});
            skLineSegment(sketch, "E3812", {"start": v(30.77, 88.05) * mm, "end": v(30.77, 88.2) * mm});
            skLineSegment(sketch, "E3813", {"start": v(30.77, 88.2) * mm, "end": v(30.77, 88.36) * mm});
            skLineSegment(sketch, "E3814", {"start": v(30.77, 88.36) * mm, "end": v(30.77, 88.52) * mm});
            skLineSegment(sketch, "E3815", {"start": v(30.77, 88.52) * mm, "end": v(30.77, 88.69) * mm});
            skLineSegment(sketch, "E3816", {"start": v(30.77, 88.69) * mm, "end": v(30.77, 88.85) * mm});
            skLineSegment(sketch, "E3817", {"start": v(30.77, 88.85) * mm, "end": v(30.77, 89.02) * mm});
            skLineSegment(sketch, "E3818", {"start": v(30.77, 89.02) * mm, "end": v(30.77, 89.19) * mm});
            skLineSegment(sketch, "E3819", {"start": v(30.77, 89.19) * mm, "end": v(30.77, 89.36) * mm});
            skLineSegment(sketch, "E3820", {"start": v(30.77, 89.36) * mm, "end": v(30.76, 89.54) * mm});
            skLineSegment(sketch, "E3821", {"start": v(30.76, 89.54) * mm, "end": v(30.75, 89.71) * mm});
            skLineSegment(sketch, "E3822", {"start": v(30.75, 89.71) * mm, "end": v(30.75, 89.9) * mm});
            skLineSegment(sketch, "E3823", {"start": v(30.75, 89.9) * mm, "end": v(30.74, 90.08) * mm});
            skLineSegment(sketch, "E3824", {"start": v(30.74, 90.08) * mm, "end": v(30.73, 90.26) * mm});
            skLineSegment(sketch, "E3825", {"start": v(30.73, 90.26) * mm, "end": v(30.72, 90.45) * mm});
            skLineSegment(sketch, "E3826", {"start": v(30.72, 90.45) * mm, "end": v(30.71, 90.64) * mm});
            skLineSegment(sketch, "E3827", {"start": v(30.71, 90.64) * mm, "end": v(30.7, 90.83) * mm});
            skLineSegment(sketch, "E3828", {"start": v(30.7, 90.83) * mm, "end": v(30.68, 91.03) * mm});
            skLineSegment(sketch, "E3829", {"start": v(30.68, 91.03) * mm, "end": v(30.67, 91.22) * mm});
            skLineSegment(sketch, "E3830", {"start": v(30.67, 91.22) * mm, "end": v(30.65, 91.42) * mm});
            skLineSegment(sketch, "E3831", {"start": v(30.65, 91.42) * mm, "end": v(30.64, 91.62) * mm});
            skLineSegment(sketch, "E3832", {"start": v(30.64, 91.62) * mm, "end": v(30.62, 91.83) * mm});
            skLineSegment(sketch, "E3833", {"start": v(30.62, 91.83) * mm, "end": v(30.6, 92.03) * mm});
            skLineSegment(sketch, "E3834", {"start": v(30.6, 92.03) * mm, "end": v(30.57, 92.2) * mm});
            skLineSegment(sketch, "E3835", {"start": v(30.57, 92.2) * mm, "end": v(28.52, 92.86) * mm});
            skLineSegment(sketch, "E3836", {"start": v(28.52, 92.86) * mm, "end": v(28.39, 92.74) * mm});
            skLineSegment(sketch, "E3837", {"start": v(28.39, 92.74) * mm, "end": v(28.25, 92.58) * mm});
            skLineSegment(sketch, "E3838", {"start": v(28.25, 92.58) * mm, "end": v(28.12, 92.43) * mm});
            skLineSegment(sketch, "E3839", {"start": v(28.12, 92.43) * mm, "end": v(27.99, 92.27) * mm});
            skLineSegment(sketch, "E3840", {"start": v(27.99, 92.27) * mm, "end": v(27.86, 92.12) * mm});
            skLineSegment(sketch, "E3841", {"start": v(27.86, 92.12) * mm, "end": v(27.73, 91.97) * mm});
            skLineSegment(sketch, "E3842", {"start": v(27.73, 91.97) * mm, "end": v(27.61, 91.82) * mm});
            skLineSegment(sketch, "E3843", {"start": v(27.61, 91.82) * mm, "end": v(27.49, 91.67) * mm});
            skLineSegment(sketch, "E3844", {"start": v(27.49, 91.67) * mm, "end": v(27.37, 91.52) * mm});
            skLineSegment(sketch, "E3845", {"start": v(27.37, 91.52) * mm, "end": v(27.25, 91.37) * mm});
            skLineSegment(sketch, "E3846", {"start": v(27.25, 91.37) * mm, "end": v(27.14, 91.23) * mm});
            skLineSegment(sketch, "E3847", {"start": v(27.14, 91.23) * mm, "end": v(27.03, 91.08) * mm});
            skLineSegment(sketch, "E3848", {"start": v(27.03, 91.08) * mm, "end": v(26.92, 90.94) * mm});
            skLineSegment(sketch, "E3849", {"start": v(26.92, 90.94) * mm, "end": v(26.81, 90.8) * mm});
            skLineSegment(sketch, "E3850", {"start": v(26.81, 90.8) * mm, "end": v(26.7, 90.66) * mm});
            skLineSegment(sketch, "E3851", {"start": v(26.7, 90.66) * mm, "end": v(26.6, 90.52) * mm});
            skLineSegment(sketch, "E3852", {"start": v(26.6, 90.52) * mm, "end": v(26.5, 90.38) * mm});
            skLineSegment(sketch, "E3853", {"start": v(26.5, 90.38) * mm, "end": v(26.4, 90.25) * mm});
            skLineSegment(sketch, "E3854", {"start": v(26.4, 90.25) * mm, "end": v(26.3, 90.11) * mm});
            skLineSegment(sketch, "E3855", {"start": v(26.3, 90.11) * mm, "end": v(26.21, 89.98) * mm});
            skLineSegment(sketch, "E3856", {"start": v(26.21, 89.98) * mm, "end": v(26.12, 89.85) * mm});
            skLineSegment(sketch, "E3857", {"start": v(26.12, 89.85) * mm, "end": v(26.03, 89.72) * mm});
            skLineSegment(sketch, "E3858", {"start": v(26.03, 89.72) * mm, "end": v(25.94, 89.6) * mm});
            skLineSegment(sketch, "E3859", {"start": v(25.94, 89.6) * mm, "end": v(25.86, 89.46) * mm});
            skLineSegment(sketch, "E3860", {"start": v(25.86, 89.46) * mm, "end": v(25.77, 89.34) * mm});
            skLineSegment(sketch, "E3861", {"start": v(25.77, 89.34) * mm, "end": v(25.69, 89.22) * mm});
            skLineSegment(sketch, "E3862", {"start": v(25.69, 89.22) * mm, "end": v(25.6, 89.1) * mm});
            skLineSegment(sketch, "E3863", {"start": v(25.6, 89.1) * mm, "end": v(25.53, 88.97) * mm});
            skLineSegment(sketch, "E3864", {"start": v(25.53, 88.97) * mm, "end": v(25.46, 88.86) * mm});
            skLineSegment(sketch, "E3865", {"start": v(25.46, 88.86) * mm, "end": v(25.38, 88.74) * mm});
            skLineSegment(sketch, "E3866", {"start": v(25.38, 88.74) * mm, "end": v(25.3, 88.62) * mm});
            skLineSegment(sketch, "E3867", {"start": v(25.3, 88.62) * mm, "end": v(25.24, 88.51) * mm});
            skLineSegment(sketch, "E3868", {"start": v(25.24, 88.51) * mm, "end": v(25.17, 88.4) * mm});
            skLineSegment(sketch, "E3869", {"start": v(25.17, 88.4) * mm, "end": v(25.1, 88.3) * mm});
            skLineSegment(sketch, "E3870", {"start": v(25.1, 88.3) * mm, "end": v(25.04, 88.18) * mm});
            skLineSegment(sketch, "E3871", {"start": v(25.04, 88.18) * mm, "end": v(24.98, 88.08) * mm});
            skLineSegment(sketch, "E3872", {"start": v(24.98, 88.08) * mm, "end": v(24.92, 87.97) * mm});
            skLineSegment(sketch, "E3873", {"start": v(24.92, 87.97) * mm, "end": v(24.86, 87.87) * mm});
            skLineSegment(sketch, "E3874", {"start": v(24.86, 87.87) * mm, "end": v(24.8, 87.77) * mm});
            skLineSegment(sketch, "E3875", {"start": v(24.8, 87.77) * mm, "end": v(24.33, 87.69) * mm});
            skLineSegment(sketch, "E3876", {"start": v(24.33, 87.69) * mm, "end": v(22.7, 88.12) * mm});
            skLineSegment(sketch, "E3877", {"start": v(22.7, 88.12) * mm, "end": v(22.34, 88.43) * mm});
            skLineSegment(sketch, "E3878", {"start": v(22.34, 88.43) * mm, "end": v(22.34, 88.54) * mm});
            skLineSegment(sketch, "E3879", {"start": v(22.34, 88.54) * mm, "end": v(22.34, 88.66) * mm});
            skLineSegment(sketch, "E3880", {"start": v(22.34, 88.66) * mm, "end": v(22.34, 88.78) * mm});
            skLineSegment(sketch, "E3881", {"start": v(22.34, 88.78) * mm, "end": v(22.34, 88.9) * mm});
            skLineSegment(sketch, "E3882", {"start": v(22.34, 88.9) * mm, "end": v(22.34, 89.03) * mm});
            skLineSegment(sketch, "E3883", {"start": v(22.34, 89.03) * mm, "end": v(22.33, 89.16) * mm});
            skLineSegment(sketch, "E3884", {"start": v(22.33, 89.16) * mm, "end": v(22.33, 89.3) * mm});
            skLineSegment(sketch, "E3885", {"start": v(22.33, 89.3) * mm, "end": v(22.33, 89.42) * mm});
            skLineSegment(sketch, "E3886", {"start": v(22.33, 89.42) * mm, "end": v(22.32, 89.56) * mm});
            skLineSegment(sketch, "E3887", {"start": v(22.32, 89.56) * mm, "end": v(22.31, 89.7) * mm});
            skLineSegment(sketch, "E3888", {"start": v(22.31, 89.7) * mm, "end": v(22.3, 89.84) * mm});
            skLineSegment(sketch, "E3889", {"start": v(22.3, 89.84) * mm, "end": v(22.3, 89.98) * mm});
            skLineSegment(sketch, "E3890", {"start": v(22.3, 89.98) * mm, "end": v(22.3, 90.12) * mm});
            skLineSegment(sketch, "E3891", {"start": v(22.3, 90.12) * mm, "end": v(22.28, 90.27) * mm});
            skLineSegment(sketch, "E3892", {"start": v(22.28, 90.27) * mm, "end": v(22.27, 90.42) * mm});
            skLineSegment(sketch, "E3893", {"start": v(22.27, 90.42) * mm, "end": v(22.26, 90.58) * mm});
            skLineSegment(sketch, "E3894", {"start": v(22.26, 90.58) * mm, "end": v(22.25, 90.73) * mm});
            skLineSegment(sketch, "E3895", {"start": v(22.25, 90.73) * mm, "end": v(22.23, 90.89) * mm});
            skLineSegment(sketch, "E3896", {"start": v(22.23, 90.89) * mm, "end": v(22.22, 91.05) * mm});
            skLineSegment(sketch, "E3897", {"start": v(22.22, 91.05) * mm, "end": v(22.2, 91.2) * mm});
            skLineSegment(sketch, "E3898", {"start": v(22.2, 91.2) * mm, "end": v(22.19, 91.37) * mm});
            skLineSegment(sketch, "E3899", {"start": v(22.19, 91.37) * mm, "end": v(22.17, 91.54) * mm});
            skLineSegment(sketch, "E3900", {"start": v(22.17, 91.54) * mm, "end": v(22.15, 91.7) * mm});
            skLineSegment(sketch, "E3901", {"start": v(22.15, 91.7) * mm, "end": v(22.13, 91.88) * mm});
            skLineSegment(sketch, "E3902", {"start": v(22.13, 91.88) * mm, "end": v(22.11, 92.06) * mm});
            skLineSegment(sketch, "E3903", {"start": v(22.11, 92.06) * mm, "end": v(22.09, 92.23) * mm});
            skLineSegment(sketch, "E3904", {"start": v(22.09, 92.23) * mm, "end": v(22.06, 92.41) * mm});
            skLineSegment(sketch, "E3905", {"start": v(22.06, 92.41) * mm, "end": v(22.04, 92.6) * mm});
            skLineSegment(sketch, "E3906", {"start": v(22.04, 92.6) * mm, "end": v(22.01, 92.77) * mm});
            skLineSegment(sketch, "E3907", {"start": v(22.01, 92.77) * mm, "end": v(21.98, 92.96) * mm});
            skLineSegment(sketch, "E3908", {"start": v(21.98, 92.96) * mm, "end": v(21.96, 93.15) * mm});
            skLineSegment(sketch, "E3909", {"start": v(21.96, 93.15) * mm, "end": v(21.93, 93.34) * mm});
            skLineSegment(sketch, "E3910", {"start": v(21.93, 93.34) * mm, "end": v(21.9, 93.53) * mm});
            skLineSegment(sketch, "E3911", {"start": v(21.9, 93.53) * mm, "end": v(21.86, 93.72) * mm});
            skLineSegment(sketch, "E3912", {"start": v(21.86, 93.72) * mm, "end": v(21.83, 93.92) * mm});
            skLineSegment(sketch, "E3913", {"start": v(21.83, 93.92) * mm, "end": v(21.79, 94.12) * mm});
            skLineSegment(sketch, "E3914", {"start": v(21.79, 94.12) * mm, "end": v(21.75, 94.32) * mm});
            skLineSegment(sketch, "E3915", {"start": v(21.75, 94.32) * mm, "end": v(21.71, 94.53) * mm});
            skLineSegment(sketch, "E3916", {"start": v(21.71, 94.53) * mm, "end": v(21.66, 94.7) * mm});
            skLineSegment(sketch, "E3917", {"start": v(21.66, 94.7) * mm, "end": v(19.56, 95.15) * mm});
            skLineSegment(sketch, "E3918", {"start": v(19.56, 95.15) * mm, "end": v(19.45, 95.02) * mm});
            skLineSegment(sketch, "E3919", {"start": v(19.45, 95.02) * mm, "end": v(19.32, 94.85) * mm});
            skLineSegment(sketch, "E3920", {"start": v(19.32, 94.85) * mm, "end": v(19.2, 94.68) * mm});
            skLineSegment(sketch, "E3921", {"start": v(19.2, 94.68) * mm, "end": v(19.1, 94.52) * mm});
            skLineSegment(sketch, "E3922", {"start": v(19.1, 94.52) * mm, "end": v(18.98, 94.35) * mm});
            skLineSegment(sketch, "E3923", {"start": v(18.98, 94.35) * mm, "end": v(18.87, 94.19) * mm});
            skLineSegment(sketch, "E3924", {"start": v(18.87, 94.19) * mm, "end": v(18.76, 94.03) * mm});
            skLineSegment(sketch, "E3925", {"start": v(18.76, 94.03) * mm, "end": v(18.65, 93.87) * mm});
            skLineSegment(sketch, "E3926", {"start": v(18.65, 93.87) * mm, "end": v(18.55, 93.7) * mm});
            skLineSegment(sketch, "E3927", {"start": v(18.55, 93.7) * mm, "end": v(18.45, 93.55) * mm});
            skLineSegment(sketch, "E3928", {"start": v(18.45, 93.55) * mm, "end": v(18.35, 93.4) * mm});
            skLineSegment(sketch, "E3929", {"start": v(18.35, 93.4) * mm, "end": v(18.25, 93.24) * mm});
            skLineSegment(sketch, "E3930", {"start": v(18.25, 93.24) * mm, "end": v(18.15, 93.09) * mm});
            skLineSegment(sketch, "E3931", {"start": v(18.15, 93.09) * mm, "end": v(18.06, 92.94) * mm});
            skLineSegment(sketch, "E3932", {"start": v(18.06, 92.94) * mm, "end": v(17.97, 92.79) * mm});
            skLineSegment(sketch, "E3933", {"start": v(17.97, 92.79) * mm, "end": v(17.88, 92.64) * mm});
            skLineSegment(sketch, "E3934", {"start": v(17.88, 92.64) * mm, "end": v(17.79, 92.5) * mm});
            skLineSegment(sketch, "E3935", {"start": v(17.79, 92.5) * mm, "end": v(17.7, 92.35) * mm});
            skLineSegment(sketch, "E3936", {"start": v(17.7, 92.35) * mm, "end": v(17.62, 92.2) * mm});
            skLineSegment(sketch, "E3937", {"start": v(17.62, 92.2) * mm, "end": v(17.54, 92.06) * mm});
            skLineSegment(sketch, "E3938", {"start": v(17.54, 92.06) * mm, "end": v(17.46, 91.92) * mm});
            skLineSegment(sketch, "E3939", {"start": v(17.46, 91.92) * mm, "end": v(17.38, 91.79) * mm});
            skLineSegment(sketch, "E3940", {"start": v(17.38, 91.79) * mm, "end": v(17.3, 91.65) * mm});
            skLineSegment(sketch, "E3941", {"start": v(17.3, 91.65) * mm, "end": v(17.23, 91.52) * mm});
            skLineSegment(sketch, "E3942", {"start": v(17.23, 91.52) * mm, "end": v(17.16, 91.38) * mm});
            skLineSegment(sketch, "E3943", {"start": v(17.16, 91.38) * mm, "end": v(17.1, 91.25) * mm});
            skLineSegment(sketch, "E3944", {"start": v(17.1, 91.25) * mm, "end": v(17.02, 91.13) * mm});
            skLineSegment(sketch, "E3945", {"start": v(17.02, 91.13) * mm, "end": v(16.96, 91) * mm});
            skLineSegment(sketch, "E3946", {"start": v(16.96, 91) * mm, "end": v(16.9, 90.87) * mm});
            skLineSegment(sketch, "E3947", {"start": v(16.9, 90.87) * mm, "end": v(16.83, 90.75) * mm});
            skLineSegment(sketch, "E3948", {"start": v(16.83, 90.75) * mm, "end": v(16.77, 90.63) * mm});
            skLineSegment(sketch, "E3949", {"start": v(16.77, 90.63) * mm, "end": v(16.71, 90.5) * mm});
            skLineSegment(sketch, "E3950", {"start": v(16.71, 90.5) * mm, "end": v(16.65, 90.4) * mm});
            skLineSegment(sketch, "E3951", {"start": v(16.65, 90.4) * mm, "end": v(16.6, 90.28) * mm});
            skLineSegment(sketch, "E3952", {"start": v(16.6, 90.28) * mm, "end": v(16.55, 90.16) * mm});
            skLineSegment(sketch, "E3953", {"start": v(16.55, 90.16) * mm, "end": v(16.5, 90.05) * mm});
            skLineSegment(sketch, "E3954", {"start": v(16.5, 90.05) * mm, "end": v(16.44, 89.94) * mm});
            skLineSegment(sketch, "E3955", {"start": v(16.44, 89.94) * mm, "end": v(16.4, 89.84) * mm});
            skLineSegment(sketch, "E3956", {"start": v(16.4, 89.84) * mm, "end": v(16.35, 89.73) * mm});
            skLineSegment(sketch, "E3957", {"start": v(16.35, 89.73) * mm, "end": v(15.89, 89.6) * mm});
            skLineSegment(sketch, "E3958", {"start": v(15.89, 89.6) * mm, "end": v(14.22, 89.88) * mm});
            skLineSegment(sketch, "E3959", {"start": v(14.22, 89.88) * mm, "end": v(13.83, 90.15) * mm});
            skLineSegment(sketch, "E3960", {"start": v(13.83, 90.15) * mm, "end": v(13.82, 90.27) * mm});
            skLineSegment(sketch, "E3961", {"start": v(13.82, 90.27) * mm, "end": v(13.81, 90.38) * mm});
            skLineSegment(sketch, "E3962", {"start": v(13.81, 90.38) * mm, "end": v(13.8, 90.5) * mm});
            skLineSegment(sketch, "E3963", {"start": v(13.8, 90.5) * mm, "end": v(13.79, 90.63) * mm});
            skLineSegment(sketch, "E3964", {"start": v(13.79, 90.63) * mm, "end": v(13.77, 90.75) * mm});
            skLineSegment(sketch, "E3965", {"start": v(13.77, 90.75) * mm, "end": v(13.76, 90.88) * mm});
            skLineSegment(sketch, "E3966", {"start": v(13.76, 90.88) * mm, "end": v(13.74, 91) * mm});
            skLineSegment(sketch, "E3967", {"start": v(13.74, 91) * mm, "end": v(13.72, 91.14) * mm});
            skLineSegment(sketch, "E3968", {"start": v(13.72, 91.14) * mm, "end": v(13.7, 91.27) * mm});
            skLineSegment(sketch, "E3969", {"start": v(13.7, 91.27) * mm, "end": v(13.69, 91.41) * mm});
            skLineSegment(sketch, "E3970", {"start": v(13.69, 91.41) * mm, "end": v(13.67, 91.55) * mm});
            skLineSegment(sketch, "E3971", {"start": v(13.67, 91.55) * mm, "end": v(13.65, 91.7) * mm});
            skLineSegment(sketch, "E3972", {"start": v(13.65, 91.7) * mm, "end": v(13.62, 91.84) * mm});
            skLineSegment(sketch, "E3973", {"start": v(13.62, 91.84) * mm, "end": v(13.6, 91.98) * mm});
            skLineSegment(sketch, "E3974", {"start": v(13.6, 91.98) * mm, "end": v(13.58, 92.13) * mm});
            skLineSegment(sketch, "E3975", {"start": v(13.58, 92.13) * mm, "end": v(13.55, 92.28) * mm});
            skLineSegment(sketch, "E3976", {"start": v(13.55, 92.28) * mm, "end": v(13.52, 92.43) * mm});
            skLineSegment(sketch, "E3977", {"start": v(13.52, 92.43) * mm, "end": v(13.5, 92.59) * mm});
            skLineSegment(sketch, "E3978", {"start": v(13.5, 92.59) * mm, "end": v(13.47, 92.75) * mm});
            skLineSegment(sketch, "E3979", {"start": v(13.47, 92.75) * mm, "end": v(13.43, 92.9) * mm});
            skLineSegment(sketch, "E3980", {"start": v(13.43, 92.9) * mm, "end": v(13.4, 93.07) * mm});
            skLineSegment(sketch, "E3981", {"start": v(13.4, 93.07) * mm, "end": v(13.37, 93.23) * mm});
            skLineSegment(sketch, "E3982", {"start": v(13.37, 93.23) * mm, "end": v(13.33, 93.4) * mm});
            skLineSegment(sketch, "E3983", {"start": v(13.33, 93.4) * mm, "end": v(13.3, 93.57) * mm});
            skLineSegment(sketch, "E3984", {"start": v(13.3, 93.57) * mm, "end": v(13.26, 93.74) * mm});
            skLineSegment(sketch, "E3985", {"start": v(13.26, 93.74) * mm, "end": v(13.22, 93.91) * mm});
            skLineSegment(sketch, "E3986", {"start": v(13.22, 93.91) * mm, "end": v(13.18, 94.09) * mm});
            skLineSegment(sketch, "E3987", {"start": v(13.18, 94.09) * mm, "end": v(13.14, 94.27) * mm});
            skLineSegment(sketch, "E3988", {"start": v(13.14, 94.27) * mm, "end": v(13.1, 94.45) * mm});
            skLineSegment(sketch, "E3989", {"start": v(13.1, 94.45) * mm, "end": v(13.05, 94.63) * mm});
            skLineSegment(sketch, "E3990", {"start": v(13.05, 94.63) * mm, "end": v(13, 94.81) * mm});
            skLineSegment(sketch, "E3991", {"start": v(13, 94.81) * mm, "end": v(12.95, 95) * mm});
            skLineSegment(sketch, "E3992", {"start": v(12.95, 95) * mm, "end": v(12.9, 95.19) * mm});
            skLineSegment(sketch, "E3993", {"start": v(12.9, 95.19) * mm, "end": v(12.85, 95.38) * mm});
            skLineSegment(sketch, "E3994", {"start": v(12.85, 95.38) * mm, "end": v(12.8, 95.57) * mm});
            skLineSegment(sketch, "E3995", {"start": v(12.8, 95.57) * mm, "end": v(12.74, 95.77) * mm});
            skLineSegment(sketch, "E3996", {"start": v(12.74, 95.77) * mm, "end": v(12.69, 95.96) * mm});
            skLineSegment(sketch, "E3997", {"start": v(12.69, 95.96) * mm, "end": v(12.63, 96.16) * mm});
            skLineSegment(sketch, "E3998", {"start": v(12.63, 96.16) * mm, "end": v(12.56, 96.33) * mm});
            skLineSegment(sketch, "E3999", {"start": v(12.56, 96.33) * mm, "end": v(10.43, 96.58) * mm});
            skLineSegment(sketch, "E4000", {"start": v(10.43, 96.58) * mm, "end": v(10.33, 96.44) * mm});
            skLineSegment(sketch, "E4001", {"start": v(10.33, 96.44) * mm, "end": v(10.22, 96.26) * mm});
            skLineSegment(sketch, "E4002", {"start": v(10.22, 96.26) * mm, "end": v(10.12, 96.08) * mm});
            skLineSegment(sketch, "E4003", {"start": v(10.12, 96.08) * mm, "end": v(10.02, 95.9) * mm});
            skLineSegment(sketch, "E4004", {"start": v(10.02, 95.9) * mm, "end": v(9.92, 95.73) * mm});
            skLineSegment(sketch, "E4005", {"start": v(9.92, 95.73) * mm, "end": v(9.83, 95.55) * mm});
            skLineSegment(sketch, "E4006", {"start": v(9.83, 95.55) * mm, "end": v(9.74, 95.38) * mm});
            skLineSegment(sketch, "E4007", {"start": v(9.74, 95.38) * mm, "end": v(9.64, 95.21) * mm});
            skLineSegment(sketch, "E4008", {"start": v(9.64, 95.21) * mm, "end": v(9.56, 95.04) * mm});
            skLineSegment(sketch, "E4009", {"start": v(9.56, 95.04) * mm, "end": v(9.47, 94.88) * mm});
            skLineSegment(sketch, "E4010", {"start": v(9.47, 94.88) * mm, "end": v(9.38, 94.71) * mm});
            skLineSegment(sketch, "E4011", {"start": v(9.38, 94.71) * mm, "end": v(9.3, 94.55) * mm});
            skLineSegment(sketch, "E4012", {"start": v(9.3, 94.55) * mm, "end": v(9.22, 94.4) * mm});
            skLineSegment(sketch, "E4013", {"start": v(9.22, 94.4) * mm, "end": v(9.14, 94.23) * mm});
            skLineSegment(sketch, "E4014", {"start": v(9.14, 94.23) * mm, "end": v(9.07, 94.07) * mm});
            skLineSegment(sketch, "E4015", {"start": v(9.07, 94.07) * mm, "end": v(9, 93.92) * mm});
            skLineSegment(sketch, "E4016", {"start": v(9, 93.92) * mm, "end": v(8.92, 93.76) * mm});
            skLineSegment(sketch, "E4017", {"start": v(8.92, 93.76) * mm, "end": v(8.85, 93.61) * mm});
            skLineSegment(sketch, "E4018", {"start": v(8.85, 93.61) * mm, "end": v(8.78, 93.46) * mm});
            skLineSegment(sketch, "E4019", {"start": v(8.78, 93.46) * mm, "end": v(8.7, 93.31) * mm});
            skLineSegment(sketch, "E4020", {"start": v(8.7, 93.31) * mm, "end": v(8.64, 93.17) * mm});
            skLineSegment(sketch, "E4021", {"start": v(8.64, 93.17) * mm, "end": v(8.58, 93.02) * mm});
            skLineSegment(sketch, "E4022", {"start": v(8.58, 93.02) * mm, "end": v(8.52, 92.88) * mm});
            skLineSegment(sketch, "E4023", {"start": v(8.52, 92.88) * mm, "end": v(8.46, 92.74) * mm});
            skLineSegment(sketch, "E4024", {"start": v(8.46, 92.74) * mm, "end": v(8.4, 92.6) * mm});
            skLineSegment(sketch, "E4025", {"start": v(8.4, 92.6) * mm, "end": v(8.34, 92.47) * mm});
            skLineSegment(sketch, "E4026", {"start": v(8.34, 92.47) * mm, "end": v(8.29, 92.33) * mm});
            skLineSegment(sketch, "E4027", {"start": v(8.29, 92.33) * mm, "end": v(8.23, 92.2) * mm});
            skLineSegment(sketch, "E4028", {"start": v(8.23, 92.2) * mm, "end": v(8.18, 92.07) * mm});
            skLineSegment(sketch, "E4029", {"start": v(8.18, 92.07) * mm, "end": v(8.13, 91.94) * mm});
            skLineSegment(sketch, "E4030", {"start": v(8.13, 91.94) * mm, "end": v(8.08, 91.81) * mm});
            skLineSegment(sketch, "E4031", {"start": v(8.08, 91.81) * mm, "end": v(8.03, 91.69) * mm});
            skLineSegment(sketch, "E4032", {"start": v(8.03, 91.69) * mm, "end": v(7.99, 91.57) * mm});
            skLineSegment(sketch, "E4033", {"start": v(7.99, 91.57) * mm, "end": v(7.94, 91.45) * mm});
            skLineSegment(sketch, "E4034", {"start": v(7.94, 91.45) * mm, "end": v(7.9, 91.33) * mm});
            skLineSegment(sketch, "E4035", {"start": v(7.9, 91.33) * mm, "end": v(7.86, 91.21) * mm});
            skLineSegment(sketch, "E4036", {"start": v(7.86, 91.21) * mm, "end": v(7.82, 91.1) * mm});
            skLineSegment(sketch, "E4037", {"start": v(7.82, 91.1) * mm, "end": v(7.78, 90.99) * mm});
            skLineSegment(sketch, "E4038", {"start": v(7.78, 90.99) * mm, "end": v(7.74, 90.88) * mm});
            skLineSegment(sketch, "E4039", {"start": v(7.74, 90.88) * mm, "end": v(7.3, 90.7) * mm});
            skLineSegment(sketch, "E4040", {"start": v(7.3, 90.7) * mm, "end": v(5.62, 90.83) * mm});
            skLineSegment(sketch, "E4041", {"start": v(5.62, 90.83) * mm, "end": v(5.2, 91.06) * mm});
            skLineSegment(sketch, "E4042", {"start": v(5.2, 91.06) * mm, "end": v(5.18, 91.17) * mm});
            skLineSegment(sketch, "E4043", {"start": v(5.18, 91.17) * mm, "end": v(5.16, 91.29) * mm});
            skLineSegment(sketch, "E4044", {"start": v(5.16, 91.29) * mm, "end": v(5.13, 91.4) * mm});
            skLineSegment(sketch, "E4045", {"start": v(5.13, 91.4) * mm, "end": v(5.1, 91.53) * mm});
            skLineSegment(sketch, "E4046", {"start": v(5.1, 91.53) * mm, "end": v(5.08, 91.65) * mm});
            skLineSegment(sketch, "E4047", {"start": v(5.08, 91.65) * mm, "end": v(5.06, 91.77) * mm});
            skLineSegment(sketch, "E4048", {"start": v(5.06, 91.77) * mm, "end": v(5.03, 91.9) * mm});
            skLineSegment(sketch, "E4049", {"start": v(5.03, 91.9) * mm, "end": v(5, 92.03) * mm});
            skLineSegment(sketch, "E4050", {"start": v(5, 92.03) * mm, "end": v(4.97, 92.16) * mm});
            skLineSegment(sketch, "E4051", {"start": v(4.97, 92.16) * mm, "end": v(4.94, 92.3) * mm});
            skLineSegment(sketch, "E4052", {"start": v(4.94, 92.3) * mm, "end": v(4.9, 92.44) * mm});
            skLineSegment(sketch, "E4053", {"start": v(4.9, 92.44) * mm, "end": v(4.87, 92.57) * mm});
            skLineSegment(sketch, "E4054", {"start": v(4.87, 92.57) * mm, "end": v(4.83, 92.71) * mm});
            skLineSegment(sketch, "E4055", {"start": v(4.83, 92.71) * mm, "end": v(4.8, 92.86) * mm});
            skLineSegment(sketch, "E4056", {"start": v(4.8, 92.86) * mm, "end": v(4.76, 93) * mm});
            skLineSegment(sketch, "E4057", {"start": v(4.76, 93) * mm, "end": v(4.72, 93.15) * mm});
            skLineSegment(sketch, "E4058", {"start": v(4.72, 93.15) * mm, "end": v(4.68, 93.3) * mm});
            skLineSegment(sketch, "E4059", {"start": v(4.68, 93.3) * mm, "end": v(4.63, 93.45) * mm});
            skLineSegment(sketch, "E4060", {"start": v(4.63, 93.45) * mm, "end": v(4.59, 93.6) * mm});
            skLineSegment(sketch, "E4061", {"start": v(4.59, 93.6) * mm, "end": v(4.54, 93.76) * mm});
            skLineSegment(sketch, "E4062", {"start": v(4.54, 93.76) * mm, "end": v(4.5, 93.92) * mm});
            skLineSegment(sketch, "E4063", {"start": v(4.5, 93.92) * mm, "end": v(4.45, 94.08) * mm});
            skLineSegment(sketch, "E4064", {"start": v(4.45, 94.08) * mm, "end": v(4.4, 94.24) * mm});
            skLineSegment(sketch, "E4065", {"start": v(4.4, 94.24) * mm, "end": v(4.34, 94.4) * mm});
            skLineSegment(sketch, "E4066", {"start": v(4.34, 94.4) * mm, "end": v(4.29, 94.58) * mm});
            skLineSegment(sketch, "E4067", {"start": v(4.29, 94.58) * mm, "end": v(4.23, 94.74) * mm});
            skLineSegment(sketch, "E4068", {"start": v(4.23, 94.74) * mm, "end": v(4.18, 94.92) * mm});
            skLineSegment(sketch, "E4069", {"start": v(4.18, 94.92) * mm, "end": v(4.12, 95.09) * mm});
            skLineSegment(sketch, "E4070", {"start": v(4.12, 95.09) * mm, "end": v(4.06, 95.26) * mm});
            skLineSegment(sketch, "E4071", {"start": v(4.06, 95.26) * mm, "end": v(4, 95.44) * mm});
            skLineSegment(sketch, "E4072", {"start": v(4, 95.44) * mm, "end": v(3.93, 95.62) * mm});
            skLineSegment(sketch, "E4073", {"start": v(3.93, 95.62) * mm, "end": v(3.86, 95.8) * mm});
            skLineSegment(sketch, "E4074", {"start": v(3.86, 95.8) * mm, "end": v(3.8, 95.98) * mm});
            skLineSegment(sketch, "E4075", {"start": v(3.8, 95.98) * mm, "end": v(3.73, 96.17) * mm});
            skLineSegment(sketch, "E4076", {"start": v(3.73, 96.17) * mm, "end": v(3.66, 96.36) * mm});
            skLineSegment(sketch, "E4077", {"start": v(3.66, 96.36) * mm, "end": v(3.58, 96.54) * mm});
            skLineSegment(sketch, "E4078", {"start": v(3.58, 96.54) * mm, "end": v(3.5, 96.73) * mm});
            skLineSegment(sketch, "E4079", {"start": v(3.5, 96.73) * mm, "end": v(3.43, 96.93) * mm});
            skLineSegment(sketch, "E4080", {"start": v(3.43, 96.93) * mm, "end": v(3.35, 97.09) * mm});
            skLineSegment(sketch, "E4081", {"start": v(3.35, 97.09) * mm, "end": v(1.2, 97.14) * mm});
            skLineSegment(sketch, "E4082", {"start": v(1.2, 97.14) * mm, "end": v(1.11, 96.98) * mm});
            skLineSegment(sketch, "E4083", {"start": v(1.11, 96.98) * mm, "end": v(1.03, 96.8) * mm});
            skLineSegment(sketch, "E4084", {"start": v(1.03, 96.8) * mm, "end": v(0.94, 96.6) * mm});
            skLineSegment(sketch, "E4085", {"start": v(0.94, 96.6) * mm, "end": v(0.86, 96.42) * mm});
            skLineSegment(sketch, "E4086", {"start": v(0.86, 96.42) * mm, "end": v(0.78, 96.24) * mm});
            skLineSegment(sketch, "E4087", {"start": v(0.78, 96.24) * mm, "end": v(0.7, 96.06) * mm});
            skLineSegment(sketch, "E4088", {"start": v(0.7, 96.06) * mm, "end": v(0.62, 95.88) * mm});
            skLineSegment(sketch, "E4089", {"start": v(0.62, 95.88) * mm, "end": v(0.55, 95.7) * mm});
            skLineSegment(sketch, "E4090", {"start": v(0.55, 95.7) * mm, "end": v(0.48, 95.52) * mm});
            skLineSegment(sketch, "E4091", {"start": v(0.48, 95.52) * mm, "end": v(0.4, 95.35) * mm});
            skLineSegment(sketch, "E4092", {"start": v(0.4, 95.35) * mm, "end": v(0.34, 95.18) * mm});
            skLineSegment(sketch, "E4093", {"start": v(0.34, 95.18) * mm, "end": v(0.27, 95) * mm});
            skLineSegment(sketch, "E4094", {"start": v(0.27, 95) * mm, "end": v(0.2, 94.84) * mm});
            skLineSegment(sketch, "E4095", {"start": v(0.2, 94.84) * mm, "end": v(0.14, 94.67) * mm});
            skLineSegment(sketch, "E4096", {"start": v(0.14, 94.67) * mm, "end": v(0.08, 94.5) * mm});
            skLineSegment(sketch, "E4097", {"start": v(0.08, 94.5) * mm, "end": v(0.02, 94.35) * mm});
            skLineSegment(sketch, "E4098", {"start": v(0.02, 94.35) * mm, "end": v(-0.04, 94.19) * mm});
            skLineSegment(sketch, "E4099", {"start": v(-0.04, 94.19) * mm, "end": v(-0.1, 94.03) * mm});
            skLineSegment(sketch, "E4100", {"start": v(-0.1, 94.03) * mm, "end": v(-0.15, 93.87) * mm});
            skLineSegment(sketch, "E4101", {"start": v(-0.15, 93.87) * mm, "end": v(-0.2, 93.72) * mm});
            skLineSegment(sketch, "E4102", {"start": v(-0.2, 93.72) * mm, "end": v(-0.25, 93.57) * mm});
            skLineSegment(sketch, "E4103", {"start": v(-0.25, 93.57) * mm, "end": v(-0.3, 93.42) * mm});
            skLineSegment(sketch, "E4104", {"start": v(-0.3, 93.42) * mm, "end": v(-0.35, 93.27) * mm});
            skLineSegment(sketch, "E4105", {"start": v(-0.35, 93.27) * mm, "end": v(-0.4, 93.12) * mm});
            skLineSegment(sketch, "E4106", {"start": v(-0.4, 93.12) * mm, "end": v(-0.44, 92.98) * mm});
            skLineSegment(sketch, "E4107", {"start": v(-0.44, 92.98) * mm, "end": v(-0.49, 92.84) * mm});
            skLineSegment(sketch, "E4108", {"start": v(-0.49, 92.84) * mm, "end": v(-0.53, 92.7) * mm});
            skLineSegment(sketch, "E4109", {"start": v(-0.53, 92.7) * mm, "end": v(-0.57, 92.56) * mm});
            skLineSegment(sketch, "E4110", {"start": v(-0.57, 92.56) * mm, "end": v(-0.6, 92.43) * mm});
            skLineSegment(sketch, "E4111", {"start": v(-0.6, 92.43) * mm, "end": v(-0.65, 92.3) * mm});
            skLineSegment(sketch, "E4112", {"start": v(-0.65, 92.3) * mm, "end": v(-0.68, 92.17) * mm});
            skLineSegment(sketch, "E4113", {"start": v(-0.68, 92.17) * mm, "end": v(-0.72, 92.04) * mm});
            skLineSegment(sketch, "E4114", {"start": v(-0.72, 92.04) * mm, "end": v(-0.75, 91.91) * mm});
            skLineSegment(sketch, "E4115", {"start": v(-0.75, 91.91) * mm, "end": v(-0.79, 91.79) * mm});
            skLineSegment(sketch, "E4116", {"start": v(-0.79, 91.79) * mm, "end": v(-0.82, 91.67) * mm});
            skLineSegment(sketch, "E4117", {"start": v(-0.82, 91.67) * mm, "end": v(-0.85, 91.55) * mm});
            skLineSegment(sketch, "E4118", {"start": v(-0.85, 91.55) * mm, "end": v(-0.88, 91.43) * mm});
            skLineSegment(sketch, "E4119", {"start": v(-0.88, 91.43) * mm, "end": v(-0.9, 91.31) * mm});
            skLineSegment(sketch, "E4120", {"start": v(-0.9, 91.31) * mm, "end": v(-0.93, 91.2) * mm});
            skLineSegment(sketch, "E4121", {"start": v(-0.93, 91.2) * mm, "end": v(-1.36, 90.99) * mm});
            skLineSegment(sketch, "E4122", {"start": v(-1.36, 90.99) * mm, "end": v(-3.04, 90.95) * mm});
            skLineSegment(sketch, "E4123", {"start": v(-3.04, 90.95) * mm, "end": v(-3.48, 91.14) * mm});
            skLineSegment(sketch, "E4124", {"start": v(-3.48, 91.14) * mm, "end": v(-3.51, 91.25) * mm});
            skLineSegment(sketch, "E4125", {"start": v(-3.51, 91.25) * mm, "end": v(-3.54, 91.36) * mm});
            skLineSegment(sketch, "E4126", {"start": v(-3.54, 91.36) * mm, "end": v(-3.58, 91.48) * mm});
            skLineSegment(sketch, "E4127", {"start": v(-3.58, 91.48) * mm, "end": v(-3.61, 91.6) * mm});
            skLineSegment(sketch, "E4128", {"start": v(-3.61, 91.6) * mm, "end": v(-3.65, 91.72) * mm});
            skLineSegment(sketch, "E4129", {"start": v(-3.65, 91.72) * mm, "end": v(-3.7, 91.84) * mm});
            skLineSegment(sketch, "E4130", {"start": v(-3.7, 91.84) * mm, "end": v(-3.73, 91.96) * mm});
            skLineSegment(sketch, "E4131", {"start": v(-3.73, 91.96) * mm, "end": v(-3.77, 92.1) * mm});
            skLineSegment(sketch, "E4132", {"start": v(-3.77, 92.1) * mm, "end": v(-3.82, 92.22) * mm});
            skLineSegment(sketch, "E4133", {"start": v(-3.82, 92.22) * mm, "end": v(-3.86, 92.35) * mm});
            skLineSegment(sketch, "E4134", {"start": v(-3.86, 92.35) * mm, "end": v(-3.9, 92.48) * mm});
            skLineSegment(sketch, "E4135", {"start": v(-3.9, 92.48) * mm, "end": v(-3.95, 92.62) * mm});
            skLineSegment(sketch, "E4136", {"start": v(-3.95, 92.62) * mm, "end": v(-4, 92.75) * mm});
            skLineSegment(sketch, "E4137", {"start": v(-4, 92.75) * mm, "end": v(-4.05, 92.9) * mm});
            skLineSegment(sketch, "E4138", {"start": v(-4.05, 92.9) * mm, "end": v(-4.1, 93.03) * mm});
            skLineSegment(sketch, "E4139", {"start": v(-4.1, 93.03) * mm, "end": v(-4.16, 93.18) * mm});
            skLineSegment(sketch, "E4140", {"start": v(-4.16, 93.18) * mm, "end": v(-4.21, 93.32) * mm});
            skLineSegment(sketch, "E4141", {"start": v(-4.21, 93.32) * mm, "end": v(-4.27, 93.47) * mm});
            skLineSegment(sketch, "E4142", {"start": v(-4.27, 93.47) * mm, "end": v(-4.33, 93.62) * mm});
            skLineSegment(sketch, "E4143", {"start": v(-4.33, 93.62) * mm, "end": v(-4.4, 93.77) * mm});
            skLineSegment(sketch, "E4144", {"start": v(-4.4, 93.77) * mm, "end": v(-4.45, 93.92) * mm});
            skLineSegment(sketch, "E4145", {"start": v(-4.45, 93.92) * mm, "end": v(-4.52, 94.08) * mm});
            skLineSegment(sketch, "E4146", {"start": v(-4.52, 94.08) * mm, "end": v(-4.58, 94.24) * mm});
            skLineSegment(sketch, "E4147", {"start": v(-4.58, 94.24) * mm, "end": v(-4.65, 94.4) * mm});
            skLineSegment(sketch, "E4148", {"start": v(-4.65, 94.4) * mm, "end": v(-4.72, 94.56) * mm});
            skLineSegment(sketch, "E4149", {"start": v(-4.72, 94.56) * mm, "end": v(-4.8, 94.72) * mm});
            skLineSegment(sketch, "E4150", {"start": v(-4.8, 94.72) * mm, "end": v(-4.86, 94.88) * mm});
            skLineSegment(sketch, "E4151", {"start": v(-4.86, 94.88) * mm, "end": v(-4.94, 95.05) * mm});
            skLineSegment(sketch, "E4152", {"start": v(-4.94, 95.05) * mm, "end": v(-5.02, 95.22) * mm});
            skLineSegment(sketch, "E4153", {"start": v(-5.02, 95.22) * mm, "end": v(-5.1, 95.39) * mm});
            skLineSegment(sketch, "E4154", {"start": v(-5.1, 95.39) * mm, "end": v(-5.18, 95.56) * mm});
            skLineSegment(sketch, "E4155", {"start": v(-5.18, 95.56) * mm, "end": v(-5.26, 95.73) * mm});
            skLineSegment(sketch, "E4156", {"start": v(-5.26, 95.73) * mm, "end": v(-5.34, 95.9) * mm});
            skLineSegment(sketch, "E4157", {"start": v(-5.34, 95.9) * mm, "end": v(-5.43, 96.09) * mm});
            skLineSegment(sketch, "E4158", {"start": v(-5.43, 96.09) * mm, "end": v(-5.52, 96.27) * mm});
            skLineSegment(sketch, "E4159", {"start": v(-5.52, 96.27) * mm, "end": v(-5.61, 96.45) * mm});
            skLineSegment(sketch, "E4160", {"start": v(-5.61, 96.45) * mm, "end": v(-5.7, 96.63) * mm});
            skLineSegment(sketch, "E4161", {"start": v(-5.7, 96.63) * mm, "end": v(-5.8, 96.81) * mm});
            skLineSegment(sketch, "E4162", {"start": v(-5.8, 96.81) * mm, "end": v(-5.9, 96.96) * mm});
            skLineSegment(sketch, "E4163", {"start": v(-5.9, 96.96) * mm, "end": v(-8.04, 96.8) * mm});
            skLineSegment(sketch, "E4164", {"start": v(-8.04, 96.8) * mm, "end": v(-8.11, 96.65) * mm});
            skLineSegment(sketch, "E4165", {"start": v(-8.11, 96.65) * mm, "end": v(-8.18, 96.45) * mm});
            skLineSegment(sketch, "E4166", {"start": v(-8.18, 96.45) * mm, "end": v(-8.25, 96.26) * mm});
            skLineSegment(sketch, "E4167", {"start": v(-8.25, 96.26) * mm, "end": v(-8.3, 96.07) * mm});
            skLineSegment(sketch, "E4168", {"start": v(-8.3, 96.07) * mm, "end": v(-8.37, 95.88) * mm});
            skLineSegment(sketch, "E4169", {"start": v(-8.37, 95.88) * mm, "end": v(-8.43, 95.69) * mm});
            skLineSegment(sketch, "E4170", {"start": v(-8.43, 95.69) * mm, "end": v(-8.5, 95.5) * mm});
            skLineSegment(sketch, "E4171", {"start": v(-8.5, 95.5) * mm, "end": v(-8.55, 95.32) * mm});
            skLineSegment(sketch, "E4172", {"start": v(-8.55, 95.32) * mm, "end": v(-8.6, 95.14) * mm});
            skLineSegment(sketch, "E4173", {"start": v(-8.6, 95.14) * mm, "end": v(-8.66, 94.96) * mm});
            skLineSegment(sketch, "E4174", {"start": v(-8.66, 94.96) * mm, "end": v(-8.7, 94.78) * mm});
            skLineSegment(sketch, "E4175", {"start": v(-8.7, 94.78) * mm, "end": v(-8.76, 94.6) * mm});
            skLineSegment(sketch, "E4176", {"start": v(-8.76, 94.6) * mm, "end": v(-8.8, 94.43) * mm});
            skLineSegment(sketch, "E4177", {"start": v(-8.8, 94.43) * mm, "end": v(-8.86, 94.26) * mm});
            skLineSegment(sketch, "E4178", {"start": v(-8.86, 94.26) * mm, "end": v(-8.9, 94.09) * mm});
            skLineSegment(sketch, "E4179", {"start": v(-8.9, 94.09) * mm, "end": v(-8.95, 93.92) * mm});
            skLineSegment(sketch, "E4180", {"start": v(-8.95, 93.92) * mm, "end": v(-8.99, 93.76) * mm});
            skLineSegment(sketch, "E4181", {"start": v(-8.99, 93.76) * mm, "end": v(-9.03, 93.6) * mm});
            skLineSegment(sketch, "E4182", {"start": v(-9.03, 93.6) * mm, "end": v(-9.07, 93.43) * mm});
            skLineSegment(sketch, "E4183", {"start": v(-9.07, 93.43) * mm, "end": v(-9.1, 93.28) * mm});
            skLineSegment(sketch, "E4184", {"start": v(-9.1, 93.28) * mm, "end": v(-9.14, 93.12) * mm});
            skLineSegment(sketch, "E4185", {"start": v(-9.14, 93.12) * mm, "end": v(-9.18, 92.97) * mm});
            skLineSegment(sketch, "E4186", {"start": v(-9.18, 92.97) * mm, "end": v(-9.21, 92.81) * mm});
            skLineSegment(sketch, "E4187", {"start": v(-9.21, 92.81) * mm, "end": v(-9.25, 92.66) * mm});
            skLineSegment(sketch, "E4188", {"start": v(-9.25, 92.66) * mm, "end": v(-9.28, 92.52) * mm});
            skLineSegment(sketch, "E4189", {"start": v(-9.28, 92.52) * mm, "end": v(-9.3, 92.37) * mm});
            skLineSegment(sketch, "E4190", {"start": v(-9.3, 92.37) * mm, "end": v(-9.34, 92.23) * mm});
            skLineSegment(sketch, "E4191", {"start": v(-9.34, 92.23) * mm, "end": v(-9.37, 92.1) * mm});
            skLineSegment(sketch, "E4192", {"start": v(-9.37, 92.1) * mm, "end": v(-9.4, 91.95) * mm});
            skLineSegment(sketch, "E4193", {"start": v(-9.4, 91.95) * mm, "end": v(-9.42, 91.82) * mm});
            skLineSegment(sketch, "E4194", {"start": v(-9.42, 91.82) * mm, "end": v(-9.44, 91.68) * mm});
            skLineSegment(sketch, "E4195", {"start": v(-9.44, 91.68) * mm, "end": v(-9.46, 91.55) * mm});
            skLineSegment(sketch, "E4196", {"start": v(-9.46, 91.55) * mm, "end": v(-9.49, 91.42) * mm});
            skLineSegment(sketch, "E4197", {"start": v(-9.49, 91.42) * mm, "end": v(-9.5, 91.3) * mm});
            skLineSegment(sketch, "E4198", {"start": v(-9.5, 91.3) * mm, "end": v(-9.53, 91.17) * mm});
            skLineSegment(sketch, "E4199", {"start": v(-9.53, 91.17) * mm, "end": v(-9.55, 91.05) * mm});
            skLineSegment(sketch, "E4200", {"start": v(-9.55, 91.05) * mm, "end": v(-9.56, 90.93) * mm});
            skLineSegment(sketch, "E4201", {"start": v(-9.56, 90.93) * mm, "end": v(-9.58, 90.81) * mm});
            skLineSegment(sketch, "E4202", {"start": v(-9.58, 90.81) * mm, "end": v(-9.6, 90.7) * mm});
            skLineSegment(sketch, "E4203", {"start": v(-9.6, 90.7) * mm, "end": v(-10, 90.45) * mm});
            skLineSegment(sketch, "E4204", {"start": v(-10, 90.45) * mm, "end": v(-11.68, 90.25) * mm});
            skLineSegment(sketch, "E4205", {"start": v(-11.68, 90.25) * mm, "end": v(-12.13, 90.4) * mm});
            skLineSegment(sketch, "E4206", {"start": v(-12.13, 90.4) * mm, "end": v(-12.17, 90.5) * mm});
            skLineSegment(sketch, "E4207", {"start": v(-12.17, 90.5) * mm, "end": v(-12.21, 90.61) * mm});
            skLineSegment(sketch, "E4208", {"start": v(-12.21, 90.61) * mm, "end": v(-12.26, 90.73) * mm});
            skLineSegment(sketch, "E4209", {"start": v(-12.26, 90.73) * mm, "end": v(-12.3, 90.84) * mm});
            skLineSegment(sketch, "E4210", {"start": v(-12.3, 90.84) * mm, "end": v(-12.35, 90.96) * mm});
            skLineSegment(sketch, "E4211", {"start": v(-12.35, 90.96) * mm, "end": v(-12.4, 91.07) * mm});
            skLineSegment(sketch, "E4212", {"start": v(-12.4, 91.07) * mm, "end": v(-12.46, 91.2) * mm});
            skLineSegment(sketch, "E4213", {"start": v(-12.46, 91.2) * mm, "end": v(-12.5, 91.32) * mm});
            skLineSegment(sketch, "E4214", {"start": v(-12.5, 91.32) * mm, "end": v(-12.56, 91.44) * mm});
            skLineSegment(sketch, "E4215", {"start": v(-12.56, 91.44) * mm, "end": v(-12.62, 91.56) * mm});
            skLineSegment(sketch, "E4216", {"start": v(-12.62, 91.56) * mm, "end": v(-12.68, 91.7) * mm});
            skLineSegment(sketch, "E4217", {"start": v(-12.68, 91.7) * mm, "end": v(-12.74, 91.82) * mm});
            skLineSegment(sketch, "E4218", {"start": v(-12.74, 91.82) * mm, "end": v(-12.8, 91.95) * mm});
            skLineSegment(sketch, "E4219", {"start": v(-12.8, 91.95) * mm, "end": v(-12.86, 92.09) * mm});
            skLineSegment(sketch, "E4220", {"start": v(-12.86, 92.09) * mm, "end": v(-12.93, 92.22) * mm});
            skLineSegment(sketch, "E4221", {"start": v(-12.93, 92.22) * mm, "end": v(-13, 92.36) * mm});
            skLineSegment(sketch, "E4222", {"start": v(-13, 92.36) * mm, "end": v(-13.07, 92.5) * mm});
            skLineSegment(sketch, "E4223", {"start": v(-13.07, 92.5) * mm, "end": v(-13.14, 92.64) * mm});
            skLineSegment(sketch, "E4224", {"start": v(-13.14, 92.64) * mm, "end": v(-13.21, 92.78) * mm});
            skLineSegment(sketch, "E4225", {"start": v(-13.21, 92.78) * mm, "end": v(-13.28, 92.93) * mm});
            skLineSegment(sketch, "E4226", {"start": v(-13.28, 92.93) * mm, "end": v(-13.36, 93.07) * mm});
            skLineSegment(sketch, "E4227", {"start": v(-13.36, 93.07) * mm, "end": v(-13.44, 93.22) * mm});
            skLineSegment(sketch, "E4228", {"start": v(-13.44, 93.22) * mm, "end": v(-13.52, 93.37) * mm});
            skLineSegment(sketch, "E4229", {"start": v(-13.52, 93.37) * mm, "end": v(-13.6, 93.53) * mm});
            skLineSegment(sketch, "E4230", {"start": v(-13.6, 93.53) * mm, "end": v(-13.69, 93.68) * mm});
            skLineSegment(sketch, "E4231", {"start": v(-13.69, 93.68) * mm, "end": v(-13.77, 93.83) * mm});
            skLineSegment(sketch, "E4232", {"start": v(-13.77, 93.83) * mm, "end": v(-13.86, 94) * mm});
            skLineSegment(sketch, "E4233", {"start": v(-13.86, 94) * mm, "end": v(-13.95, 94.15) * mm});
            skLineSegment(sketch, "E4234", {"start": v(-13.95, 94.15) * mm, "end": v(-14.04, 94.3) * mm});
            skLineSegment(sketch, "E4235", {"start": v(-14.04, 94.3) * mm, "end": v(-14.14, 94.47) * mm});
            skLineSegment(sketch, "E4236", {"start": v(-14.14, 94.47) * mm, "end": v(-14.24, 94.64) * mm});
            skLineSegment(sketch, "E4237", {"start": v(-14.24, 94.64) * mm, "end": v(-14.34, 94.8) * mm});
            skLineSegment(sketch, "E4238", {"start": v(-14.34, 94.8) * mm, "end": v(-14.44, 94.97) * mm});
            skLineSegment(sketch, "E4239", {"start": v(-14.44, 94.97) * mm, "end": v(-14.54, 95.14) * mm});
            skLineSegment(sketch, "E4240", {"start": v(-14.54, 95.14) * mm, "end": v(-14.65, 95.3) * mm});
            skLineSegment(sketch, "E4241", {"start": v(-14.65, 95.3) * mm, "end": v(-14.75, 95.48) * mm});
            skLineSegment(sketch, "E4242", {"start": v(-14.75, 95.48) * mm, "end": v(-14.86, 95.65) * mm});
            skLineSegment(sketch, "E4243", {"start": v(-14.86, 95.65) * mm, "end": v(-14.97, 95.82) * mm});
            skLineSegment(sketch, "E4244", {"start": v(-14.97, 95.82) * mm, "end": v(-15.08, 95.96) * mm});
            skLineSegment(sketch, "E4245", {"start": v(-15.08, 95.96) * mm, "end": v(-17.2, 95.6) * mm});
            skLineSegment(sketch, "E4246", {"start": v(-17.2, 95.6) * mm, "end": v(-17.26, 95.44) * mm});
            skLineSegment(sketch, "E4247", {"start": v(-17.26, 95.44) * mm, "end": v(-17.31, 95.24) * mm});
            skLineSegment(sketch, "E4248", {"start": v(-17.31, 95.24) * mm, "end": v(-17.36, 95.04) * mm});
            skLineSegment(sketch, "E4249", {"start": v(-17.36, 95.04) * mm, "end": v(-17.4, 94.84) * mm});
            skLineSegment(sketch, "E4250", {"start": v(-17.4, 94.84) * mm, "end": v(-17.45, 94.65) * mm});
            skLineSegment(sketch, "E4251", {"start": v(-17.45, 94.65) * mm, "end": v(-17.5, 94.45) * mm});
            skLineSegment(sketch, "E4252", {"start": v(-17.5, 94.45) * mm, "end": v(-17.53, 94.26) * mm});
            skLineSegment(sketch, "E4253", {"start": v(-17.53, 94.26) * mm, "end": v(-17.57, 94.07) * mm});
            skLineSegment(sketch, "E4254", {"start": v(-17.57, 94.07) * mm, "end": v(-17.6, 93.89) * mm});
            skLineSegment(sketch, "E4255", {"start": v(-17.6, 93.89) * mm, "end": v(-17.64, 93.7) * mm});
            skLineSegment(sketch, "E4256", {"start": v(-17.64, 93.7) * mm, "end": v(-17.68, 93.52) * mm});
            skLineSegment(sketch, "E4257", {"start": v(-17.68, 93.52) * mm, "end": v(-17.71, 93.34) * mm});
            skLineSegment(sketch, "E4258", {"start": v(-17.71, 93.34) * mm, "end": v(-17.75, 93.16) * mm});
            skLineSegment(sketch, "E4259", {"start": v(-17.75, 93.16) * mm, "end": v(-17.78, 92.99) * mm});
            skLineSegment(sketch, "E4260", {"start": v(-17.78, 92.99) * mm, "end": v(-17.8, 92.82) * mm});
            skLineSegment(sketch, "E4261", {"start": v(-17.8, 92.82) * mm, "end": v(-17.83, 92.65) * mm});
            skLineSegment(sketch, "E4262", {"start": v(-17.83, 92.65) * mm, "end": v(-17.86, 92.48) * mm});
            skLineSegment(sketch, "E4263", {"start": v(-17.86, 92.48) * mm, "end": v(-17.89, 92.31) * mm});
            skLineSegment(sketch, "E4264", {"start": v(-17.89, 92.31) * mm, "end": v(-17.91, 92.15) * mm});
            skLineSegment(sketch, "E4265", {"start": v(-17.91, 92.15) * mm, "end": v(-17.93, 91.99) * mm});
            skLineSegment(sketch, "E4266", {"start": v(-17.93, 91.99) * mm, "end": v(-17.96, 91.83) * mm});
            skLineSegment(sketch, "E4267", {"start": v(-17.96, 91.83) * mm, "end": v(-17.98, 91.67) * mm});
            skLineSegment(sketch, "E4268", {"start": v(-17.98, 91.67) * mm, "end": v(-18, 91.52) * mm});
            skLineSegment(sketch, "E4269", {"start": v(-18, 91.52) * mm, "end": v(-18.01, 91.37) * mm});
            skLineSegment(sketch, "E4270", {"start": v(-18.01, 91.37) * mm, "end": v(-18.03, 91.22) * mm});
            skLineSegment(sketch, "E4271", {"start": v(-18.03, 91.22) * mm, "end": v(-18.05, 91.07) * mm});
            skLineSegment(sketch, "E4272", {"start": v(-18.05, 91.07) * mm, "end": v(-18.06, 90.93) * mm});
            skLineSegment(sketch, "E4273", {"start": v(-18.06, 90.93) * mm, "end": v(-18.08, 90.78) * mm});
            skLineSegment(sketch, "E4274", {"start": v(-18.08, 90.78) * mm, "end": v(-18.1, 90.64) * mm});
            skLineSegment(sketch, "E4275", {"start": v(-18.1, 90.64) * mm, "end": v(-18.1, 90.5) * mm});
            skLineSegment(sketch, "E4276", {"start": v(-18.1, 90.5) * mm, "end": v(-18.11, 90.37) * mm});
            skLineSegment(sketch, "E4277", {"start": v(-18.11, 90.37) * mm, "end": v(-18.12, 90.24) * mm});
            skLineSegment(sketch, "E4278", {"start": v(-18.12, 90.24) * mm, "end": v(-18.13, 90.1) * mm});
            skLineSegment(sketch, "E4279", {"start": v(-18.13, 90.1) * mm, "end": v(-18.14, 89.98) * mm});
            skLineSegment(sketch, "E4280", {"start": v(-18.14, 89.98) * mm, "end": v(-18.15, 89.85) * mm});
            skLineSegment(sketch, "E4281", {"start": v(-18.15, 89.85) * mm, "end": v(-18.16, 89.73) * mm});
            skLineSegment(sketch, "E4282", {"start": v(-18.16, 89.73) * mm, "end": v(-18.16, 89.61) * mm});
            skLineSegment(sketch, "E4283", {"start": v(-18.16, 89.61) * mm, "end": v(-18.17, 89.5) * mm});
            skLineSegment(sketch, "E4284", {"start": v(-18.17, 89.5) * mm, "end": v(-18.17, 89.38) * mm});
            skLineSegment(sketch, "E4285", {"start": v(-18.17, 89.38) * mm, "end": v(-18.55, 89.09) * mm});
            skLineSegment(sketch, "E4286", {"start": v(-18.55, 89.09) * mm, "end": v(-20.2, 88.73) * mm});
            skLineSegment(sketch, "E4287", {"start": v(-20.2, 88.73) * mm, "end": v(-20.66, 88.83) * mm});
            skLineSegment(sketch, "E4288", {"start": v(-20.66, 88.83) * mm, "end": v(-20.72, 88.94) * mm});
            skLineSegment(sketch, "E4289", {"start": v(-20.72, 88.94) * mm, "end": v(-20.77, 89.04) * mm});
            skLineSegment(sketch, "E4290", {"start": v(-20.77, 89.04) * mm, "end": v(-20.83, 89.15) * mm});
            skLineSegment(sketch, "E4291", {"start": v(-20.83, 89.15) * mm, "end": v(-20.88, 89.26) * mm});
            skLineSegment(sketch, "E4292", {"start": v(-20.88, 89.26) * mm, "end": v(-20.94, 89.37) * mm});
            skLineSegment(sketch, "E4293", {"start": v(-20.94, 89.37) * mm, "end": v(-21, 89.48) * mm});
            skLineSegment(sketch, "E4294", {"start": v(-21, 89.48) * mm, "end": v(-21.07, 89.6) * mm});
            skLineSegment(sketch, "E4295", {"start": v(-21.07, 89.6) * mm, "end": v(-21.13, 89.71) * mm});
            skLineSegment(sketch, "E4296", {"start": v(-21.13, 89.71) * mm, "end": v(-21.2, 89.83) * mm});
            skLineSegment(sketch, "E4297", {"start": v(-21.2, 89.83) * mm, "end": v(-21.27, 89.95) * mm});
            skLineSegment(sketch, "E4298", {"start": v(-21.27, 89.95) * mm, "end": v(-21.34, 90.07) * mm});
            skLineSegment(sketch, "E4299", {"start": v(-21.34, 90.07) * mm, "end": v(-21.4, 90.2) * mm});
            skLineSegment(sketch, "E4300", {"start": v(-21.4, 90.2) * mm, "end": v(-21.48, 90.32) * mm});
            skLineSegment(sketch, "E4301", {"start": v(-21.48, 90.32) * mm, "end": v(-21.56, 90.45) * mm});
            skLineSegment(sketch, "E4302", {"start": v(-21.56, 90.45) * mm, "end": v(-21.64, 90.58) * mm});
            skLineSegment(sketch, "E4303", {"start": v(-21.64, 90.58) * mm, "end": v(-21.72, 90.7) * mm});
            skLineSegment(sketch, "E4304", {"start": v(-21.72, 90.7) * mm, "end": v(-21.8, 90.84) * mm});
            skLineSegment(sketch, "E4305", {"start": v(-21.8, 90.84) * mm, "end": v(-21.88, 90.97) * mm});
            skLineSegment(sketch, "E4306", {"start": v(-21.88, 90.97) * mm, "end": v(-21.97, 91.1) * mm});
            skLineSegment(sketch, "E4307", {"start": v(-21.97, 91.1) * mm, "end": v(-22.06, 91.24) * mm});
            skLineSegment(sketch, "E4308", {"start": v(-22.06, 91.24) * mm, "end": v(-22.15, 91.38) * mm});
            skLineSegment(sketch, "E4309", {"start": v(-22.15, 91.38) * mm, "end": v(-22.24, 91.52) * mm});
            skLineSegment(sketch, "E4310", {"start": v(-22.24, 91.52) * mm, "end": v(-22.33, 91.67) * mm});
            skLineSegment(sketch, "E4311", {"start": v(-22.33, 91.67) * mm, "end": v(-22.43, 91.8) * mm});
            skLineSegment(sketch, "E4312", {"start": v(-22.43, 91.8) * mm, "end": v(-22.53, 91.95) * mm});
            skLineSegment(sketch, "E4313", {"start": v(-22.53, 91.95) * mm, "end": v(-22.63, 92.1) * mm});
            skLineSegment(sketch, "E4314", {"start": v(-22.63, 92.1) * mm, "end": v(-22.73, 92.25) * mm});
            skLineSegment(sketch, "E4315", {"start": v(-22.73, 92.25) * mm, "end": v(-22.84, 92.4) * mm});
            skLineSegment(sketch, "E4316", {"start": v(-22.84, 92.4) * mm, "end": v(-22.95, 92.55) * mm});
            skLineSegment(sketch, "E4317", {"start": v(-22.95, 92.55) * mm, "end": v(-23.06, 92.7) * mm});
            skLineSegment(sketch, "E4318", {"start": v(-23.06, 92.7) * mm, "end": v(-23.17, 92.85) * mm});
            skLineSegment(sketch, "E4319", {"start": v(-23.17, 92.85) * mm, "end": v(-23.28, 93) * mm});
            skLineSegment(sketch, "E4320", {"start": v(-23.28, 93) * mm, "end": v(-23.4, 93.17) * mm});
            skLineSegment(sketch, "E4321", {"start": v(-23.4, 93.17) * mm, "end": v(-23.52, 93.32) * mm});
            skLineSegment(sketch, "E4322", {"start": v(-23.52, 93.32) * mm, "end": v(-23.64, 93.48) * mm});
            skLineSegment(sketch, "E4323", {"start": v(-23.64, 93.48) * mm, "end": v(-23.76, 93.64) * mm});
            skLineSegment(sketch, "E4324", {"start": v(-23.76, 93.64) * mm, "end": v(-23.89, 93.8) * mm});
            skLineSegment(sketch, "E4325", {"start": v(-23.89, 93.8) * mm, "end": v(-24.02, 93.97) * mm});
            skLineSegment(sketch, "E4326", {"start": v(-24.02, 93.97) * mm, "end": v(-24.14, 94.1) * mm});
            skLineSegment(sketch, "E4327", {"start": v(-24.14, 94.1) * mm, "end": v(-26.22, 93.54) * mm});
            skLineSegment(sketch, "E4328", {"start": v(-26.22, 93.54) * mm, "end": v(-26.26, 93.37) * mm});
            skLineSegment(sketch, "E4329", {"start": v(-26.26, 93.37) * mm, "end": v(-26.29, 93.16) * mm});
            skLineSegment(sketch, "E4330", {"start": v(-26.29, 93.16) * mm, "end": v(-26.31, 92.96) * mm});
            skLineSegment(sketch, "E4331", {"start": v(-26.31, 92.96) * mm, "end": v(-26.34, 92.76) * mm});
            skLineSegment(sketch, "E4332", {"start": v(-26.34, 92.76) * mm, "end": v(-26.37, 92.56) * mm});
            skLineSegment(sketch, "E4333", {"start": v(-26.37, 92.56) * mm, "end": v(-26.39, 92.36) * mm});
            skLineSegment(sketch, "E4334", {"start": v(-26.39, 92.36) * mm, "end": v(-26.41, 92.17) * mm});
            skLineSegment(sketch, "E4335", {"start": v(-26.41, 92.17) * mm, "end": v(-26.43, 91.98) * mm});
            skLineSegment(sketch, "E4336", {"start": v(-26.43, 91.98) * mm, "end": v(-26.45, 91.79) * mm});
            skLineSegment(sketch, "E4337", {"start": v(-26.45, 91.79) * mm, "end": v(-26.47, 91.6) * mm});
            skLineSegment(sketch, "E4338", {"start": v(-26.47, 91.6) * mm, "end": v(-26.49, 91.42) * mm});
            skLineSegment(sketch, "E4339", {"start": v(-26.49, 91.42) * mm, "end": v(-26.5, 91.24) * mm});
            skLineSegment(sketch, "E4340", {"start": v(-26.5, 91.24) * mm, "end": v(-26.52, 91.06) * mm});
            skLineSegment(sketch, "E4341", {"start": v(-26.52, 91.06) * mm, "end": v(-26.53, 90.88) * mm});
            skLineSegment(sketch, "E4342", {"start": v(-26.53, 90.88) * mm, "end": v(-26.55, 90.7) * mm});
            skLineSegment(sketch, "E4343", {"start": v(-26.55, 90.7) * mm, "end": v(-26.56, 90.53) * mm});
            skLineSegment(sketch, "E4344", {"start": v(-26.56, 90.53) * mm, "end": v(-26.57, 90.36) * mm});
            skLineSegment(sketch, "E4345", {"start": v(-26.57, 90.36) * mm, "end": v(-26.58, 90.2) * mm});
            skLineSegment(sketch, "E4346", {"start": v(-26.58, 90.2) * mm, "end": v(-26.59, 90.03) * mm});
            skLineSegment(sketch, "E4347", {"start": v(-26.59, 90.03) * mm, "end": v(-26.6, 89.87) * mm});
            skLineSegment(sketch, "E4348", {"start": v(-26.6, 89.87) * mm, "end": v(-26.6, 89.7) * mm});
            skLineSegment(sketch, "E4349", {"start": v(-26.6, 89.7) * mm, "end": v(-26.6, 89.55) * mm});
            skLineSegment(sketch, "E4350", {"start": v(-26.6, 89.55) * mm, "end": v(-26.61, 89.4) * mm});
            skLineSegment(sketch, "E4351", {"start": v(-26.61, 89.4) * mm, "end": v(-26.62, 89.24) * mm});
            skLineSegment(sketch, "E4352", {"start": v(-26.62, 89.24) * mm, "end": v(-26.62, 89.09) * mm});
            skLineSegment(sketch, "E4353", {"start": v(-26.62, 89.09) * mm, "end": v(-26.62, 88.94) * mm});
            skLineSegment(sketch, "E4354", {"start": v(-26.62, 88.94) * mm, "end": v(-26.62, 88.8) * mm});
            skLineSegment(sketch, "E4355", {"start": v(-26.62, 88.8) * mm, "end": v(-26.62, 88.65) * mm});
            skLineSegment(sketch, "E4356", {"start": v(-26.62, 88.65) * mm, "end": v(-26.62, 88.51) * mm});
            skLineSegment(sketch, "E4357", {"start": v(-26.62, 88.51) * mm, "end": v(-26.62, 88.37) * mm});
            skLineSegment(sketch, "E4358", {"start": v(-26.62, 88.37) * mm, "end": v(-26.62, 88.24) * mm});
            skLineSegment(sketch, "E4359", {"start": v(-26.62, 88.24) * mm, "end": v(-26.62, 88.1) * mm});
            skLineSegment(sketch, "E4360", {"start": v(-26.62, 88.1) * mm, "end": v(-26.62, 87.98) * mm});
            skLineSegment(sketch, "E4361", {"start": v(-26.62, 87.98) * mm, "end": v(-26.61, 87.85) * mm});
            skLineSegment(sketch, "E4362", {"start": v(-26.61, 87.85) * mm, "end": v(-26.6, 87.72) * mm});
            skLineSegment(sketch, "E4363", {"start": v(-26.6, 87.72) * mm, "end": v(-26.6, 87.6) * mm});
            skLineSegment(sketch, "E4364", {"start": v(-26.6, 87.6) * mm, "end": v(-26.6, 87.48) * mm});
            skLineSegment(sketch, "E4365", {"start": v(-26.6, 87.48) * mm, "end": v(-26.6, 87.36) * mm});
            skLineSegment(sketch, "E4366", {"start": v(-26.6, 87.36) * mm, "end": v(-26.59, 87.24) * mm});
            skLineSegment(sketch, "E4367", {"start": v(-26.59, 87.24) * mm, "end": v(-26.94, 86.92) * mm});
            skLineSegment(sketch, "E4368", {"start": v(-26.94, 86.92) * mm, "end": v(-28.54, 86.4) * mm});
            skLineSegment(sketch, "E4369", {"start": v(-28.54, 86.4) * mm, "end": v(-29.02, 86.47) * mm});
            skLineSegment(sketch, "E4370", {"start": v(-29.02, 86.47) * mm, "end": v(-29.08, 86.57) * mm});
            skLineSegment(sketch, "E4371", {"start": v(-29.08, 86.57) * mm, "end": v(-29.14, 86.66) * mm});
            skLineSegment(sketch, "E4372", {"start": v(-29.14, 86.66) * mm, "end": v(-29.2, 86.77) * mm});
            skLineSegment(sketch, "E4373", {"start": v(-29.2, 86.77) * mm, "end": v(-29.27, 86.87) * mm});
            skLineSegment(sketch, "E4374", {"start": v(-29.27, 86.87) * mm, "end": v(-29.34, 86.97) * mm});
            skLineSegment(sketch, "E4375", {"start": v(-29.34, 86.97) * mm, "end": v(-29.42, 87.08) * mm});
            skLineSegment(sketch, "E4376", {"start": v(-29.42, 87.08) * mm, "end": v(-29.49, 87.19) * mm});
            skLineSegment(sketch, "E4377", {"start": v(-29.49, 87.19) * mm, "end": v(-29.56, 87.3) * mm});
            skLineSegment(sketch, "E4378", {"start": v(-29.56, 87.3) * mm, "end": v(-29.64, 87.4) * mm});
            skLineSegment(sketch, "E4379", {"start": v(-29.64, 87.4) * mm, "end": v(-29.72, 87.52) * mm});
            skLineSegment(sketch, "E4380", {"start": v(-29.72, 87.52) * mm, "end": v(-29.8, 87.64) * mm});
            skLineSegment(sketch, "E4381", {"start": v(-29.8, 87.64) * mm, "end": v(-29.89, 87.75) * mm});
            skLineSegment(sketch, "E4382", {"start": v(-29.89, 87.75) * mm, "end": v(-29.97, 87.87) * mm});
            skLineSegment(sketch, "E4383", {"start": v(-29.97, 87.87) * mm, "end": v(-30.06, 87.99) * mm});
            skLineSegment(sketch, "E4384", {"start": v(-30.06, 87.99) * mm, "end": v(-30.15, 88.1) * mm});
            skLineSegment(sketch, "E4385", {"start": v(-30.15, 88.1) * mm, "end": v(-30.24, 88.23) * mm});
            skLineSegment(sketch, "E4386", {"start": v(-30.24, 88.23) * mm, "end": v(-30.34, 88.36) * mm});
            skLineSegment(sketch, "E4387", {"start": v(-30.34, 88.36) * mm, "end": v(-30.43, 88.48) * mm});
            skLineSegment(sketch, "E4388", {"start": v(-30.43, 88.48) * mm, "end": v(-30.53, 88.6) * mm});
            skLineSegment(sketch, "E4389", {"start": v(-30.53, 88.6) * mm, "end": v(-30.63, 88.73) * mm});
            skLineSegment(sketch, "E4390", {"start": v(-30.63, 88.73) * mm, "end": v(-30.73, 88.86) * mm});
            skLineSegment(sketch, "E4391", {"start": v(-30.73, 88.86) * mm, "end": v(-30.84, 89) * mm});
            skLineSegment(sketch, "E4392", {"start": v(-30.84, 89) * mm, "end": v(-30.95, 89.13) * mm});
            skLineSegment(sketch, "E4393", {"start": v(-30.95, 89.13) * mm, "end": v(-31.06, 89.26) * mm});
            skLineSegment(sketch, "E4394", {"start": v(-31.06, 89.26) * mm, "end": v(-31.17, 89.4) * mm});
            skLineSegment(sketch, "E4395", {"start": v(-31.17, 89.4) * mm, "end": v(-31.28, 89.53) * mm});
            skLineSegment(sketch, "E4396", {"start": v(-31.28, 89.53) * mm, "end": v(-31.4, 89.67) * mm});
            skLineSegment(sketch, "E4397", {"start": v(-31.4, 89.67) * mm, "end": v(-31.52, 89.8) * mm});
            skLineSegment(sketch, "E4398", {"start": v(-31.52, 89.8) * mm, "end": v(-31.64, 89.95) * mm});
            skLineSegment(sketch, "E4399", {"start": v(-31.64, 89.95) * mm, "end": v(-31.76, 90.09) * mm});
            skLineSegment(sketch, "E4400", {"start": v(-31.76, 90.09) * mm, "end": v(-31.89, 90.23) * mm});
            skLineSegment(sketch, "E4401", {"start": v(-31.89, 90.23) * mm, "end": v(-32.02, 90.37) * mm});
            skLineSegment(sketch, "E4402", {"start": v(-32.02, 90.37) * mm, "end": v(-32.15, 90.52) * mm});
            skLineSegment(sketch, "E4403", {"start": v(-32.15, 90.52) * mm, "end": v(-32.28, 90.66) * mm});
            skLineSegment(sketch, "E4404", {"start": v(-32.28, 90.66) * mm, "end": v(-32.42, 90.81) * mm});
            skLineSegment(sketch, "E4405", {"start": v(-32.42, 90.81) * mm, "end": v(-32.56, 90.96) * mm});
            skLineSegment(sketch, "E4406", {"start": v(-32.56, 90.96) * mm, "end": v(-32.7, 91.1) * mm});
            skLineSegment(sketch, "E4407", {"start": v(-32.7, 91.1) * mm, "end": v(-32.84, 91.26) * mm});
            skLineSegment(sketch, "E4408", {"start": v(-32.84, 91.26) * mm, "end": v(-32.97, 91.38) * mm});
            skLineSegment(sketch, "E4409", {"start": v(-32.97, 91.38) * mm, "end": v(-34.99, 90.62) * mm});
            skLineSegment(sketch, "E4410", {"start": v(-34.99, 90.62) * mm, "end": v(-35.01, 90.45) * mm});
            skLineSegment(sketch, "E4411", {"start": v(-35.01, 90.45) * mm, "end": v(-35.02, 90.24) * mm});
            skLineSegment(sketch, "E4412", {"start": v(-35.02, 90.24) * mm, "end": v(-35.03, 90.04) * mm});
            skLineSegment(sketch, "E4413", {"start": v(-35.03, 90.04) * mm, "end": v(-35.04, 89.83) * mm});
            skLineSegment(sketch, "E4414", {"start": v(-35.04, 89.83) * mm, "end": v(-35.04, 89.63) * mm});
            skLineSegment(sketch, "E4415", {"start": v(-35.04, 89.63) * mm, "end": v(-35.05, 89.44) * mm});
            skLineSegment(sketch, "E4416", {"start": v(-35.05, 89.44) * mm, "end": v(-35.05, 89.24) * mm});
            skLineSegment(sketch, "E4417", {"start": v(-35.05, 89.24) * mm, "end": v(-35.06, 89.05) * mm});
            skLineSegment(sketch, "E4418", {"start": v(-35.06, 89.05) * mm, "end": v(-35.06, 88.86) * mm});
            skLineSegment(sketch, "E4419", {"start": v(-35.06, 88.86) * mm, "end": v(-35.06, 88.67) * mm});
            skLineSegment(sketch, "E4420", {"start": v(-35.06, 88.67) * mm, "end": v(-35.06, 88.49) * mm});
            skLineSegment(sketch, "E4421", {"start": v(-35.06, 88.49) * mm, "end": v(-35.06, 88.3) * mm});
            skLineSegment(sketch, "E4422", {"start": v(-35.06, 88.3) * mm, "end": v(-35.06, 88.12) * mm});
            skLineSegment(sketch, "E4423", {"start": v(-35.06, 88.12) * mm, "end": v(-35.05, 87.94) * mm});
            skLineSegment(sketch, "E4424", {"start": v(-35.05, 87.94) * mm, "end": v(-35.05, 87.77) * mm});
            skLineSegment(sketch, "E4425", {"start": v(-35.05, 87.77) * mm, "end": v(-35.04, 87.6) * mm});
            skLineSegment(sketch, "E4426", {"start": v(-35.04, 87.6) * mm, "end": v(-35.04, 87.43) * mm});
            skLineSegment(sketch, "E4427", {"start": v(-35.04, 87.43) * mm, "end": v(-35.03, 87.26) * mm});
            skLineSegment(sketch, "E4428", {"start": v(-35.03, 87.26) * mm, "end": v(-35.03, 87.1) * mm});
            skLineSegment(sketch, "E4429", {"start": v(-35.03, 87.1) * mm, "end": v(-35.02, 86.93) * mm});
            skLineSegment(sketch, "E4430", {"start": v(-35.02, 86.93) * mm, "end": v(-35, 86.77) * mm});
            skLineSegment(sketch, "E4431", {"start": v(-35, 86.77) * mm, "end": v(-35, 86.61) * mm});
            skLineSegment(sketch, "E4432", {"start": v(-35, 86.61) * mm, "end": v(-35, 86.46) * mm});
            skLineSegment(sketch, "E4433", {"start": v(-35, 86.46) * mm, "end": v(-34.98, 86.3) * mm});
            skLineSegment(sketch, "E4434", {"start": v(-34.98, 86.3) * mm, "end": v(-34.97, 86.16) * mm});
            skLineSegment(sketch, "E4435", {"start": v(-34.97, 86.16) * mm, "end": v(-34.96, 86) * mm});
            skLineSegment(sketch, "E4436", {"start": v(-34.96, 86) * mm, "end": v(-34.94, 85.86) * mm});
            skLineSegment(sketch, "E4437", {"start": v(-34.94, 85.86) * mm, "end": v(-34.93, 85.72) * mm});
            skLineSegment(sketch, "E4438", {"start": v(-34.93, 85.72) * mm, "end": v(-34.92, 85.58) * mm});
            skLineSegment(sketch, "E4439", {"start": v(-34.92, 85.58) * mm, "end": v(-34.9, 85.44) * mm});
            skLineSegment(sketch, "E4440", {"start": v(-34.9, 85.44) * mm, "end": v(-34.89, 85.3) * mm});
            skLineSegment(sketch, "E4441", {"start": v(-34.89, 85.3) * mm, "end": v(-34.87, 85.18) * mm});
            skLineSegment(sketch, "E4442", {"start": v(-34.87, 85.18) * mm, "end": v(-34.86, 85.05) * mm});
            skLineSegment(sketch, "E4443", {"start": v(-34.86, 85.05) * mm, "end": v(-34.84, 84.92) * mm});
            skLineSegment(sketch, "E4444", {"start": v(-34.84, 84.92) * mm, "end": v(-34.83, 84.8) * mm});
            skLineSegment(sketch, "E4445", {"start": v(-34.83, 84.8) * mm, "end": v(-34.81, 84.67) * mm});
            skLineSegment(sketch, "E4446", {"start": v(-34.81, 84.67) * mm, "end": v(-34.8, 84.55) * mm});
            skLineSegment(sketch, "E4447", {"start": v(-34.8, 84.55) * mm, "end": v(-34.78, 84.44) * mm});
            skLineSegment(sketch, "E4448", {"start": v(-34.78, 84.44) * mm, "end": v(-34.76, 84.32) * mm});
            skLineSegment(sketch, "E4449", {"start": v(-34.76, 84.32) * mm, "end": v(-35.08, 83.97) * mm});
            skLineSegment(sketch, "E4450", {"start": v(-35.08, 83.97) * mm, "end": v(-36.63, 83.3) * mm});
            skLineSegment(sketch, "E4451", {"start": v(-36.63, 83.3) * mm, "end": v(-37.1, 83.32) * mm});
            skLineSegment(sketch, "E4452", {"start": v(-37.1, 83.32) * mm, "end": v(-37.17, 83.4) * mm});
            skLineSegment(sketch, "E4453", {"start": v(-37.17, 83.4) * mm, "end": v(-37.25, 83.5) * mm});
            skLineSegment(sketch, "E4454", {"start": v(-37.25, 83.5) * mm, "end": v(-37.32, 83.6) * mm});
            skLineSegment(sketch, "E4455", {"start": v(-37.32, 83.6) * mm, "end": v(-37.4, 83.7) * mm});
            skLineSegment(sketch, "E4456", {"start": v(-37.4, 83.7) * mm, "end": v(-37.48, 83.8) * mm});
            skLineSegment(sketch, "E4457", {"start": v(-37.48, 83.8) * mm, "end": v(-37.56, 83.89) * mm});
            skLineSegment(sketch, "E4458", {"start": v(-37.56, 83.89) * mm, "end": v(-37.64, 83.99) * mm});
            skLineSegment(sketch, "E4459", {"start": v(-37.64, 83.99) * mm, "end": v(-37.73, 84.1) * mm});
            skLineSegment(sketch, "E4460", {"start": v(-37.73, 84.1) * mm, "end": v(-37.82, 84.2) * mm});
            skLineSegment(sketch, "E4461", {"start": v(-37.82, 84.2) * mm, "end": v(-37.9, 84.3) * mm});
            skLineSegment(sketch, "E4462", {"start": v(-37.9, 84.3) * mm, "end": v(-38, 84.4) * mm});
            skLineSegment(sketch, "E4463", {"start": v(-38, 84.4) * mm, "end": v(-38.1, 84.51) * mm});
            skLineSegment(sketch, "E4464", {"start": v(-38.1, 84.51) * mm, "end": v(-38.19, 84.62) * mm});
            skLineSegment(sketch, "E4465", {"start": v(-38.19, 84.62) * mm, "end": v(-38.29, 84.73) * mm});
            skLineSegment(sketch, "E4466", {"start": v(-38.29, 84.73) * mm, "end": v(-38.39, 84.84) * mm});
            skLineSegment(sketch, "E4467", {"start": v(-38.39, 84.84) * mm, "end": v(-38.5, 84.96) * mm});
            skLineSegment(sketch, "E4468", {"start": v(-38.5, 84.96) * mm, "end": v(-38.6, 85.07) * mm});
            skLineSegment(sketch, "E4469", {"start": v(-38.6, 85.07) * mm, "end": v(-38.7, 85.19) * mm});
            skLineSegment(sketch, "E4470", {"start": v(-38.7, 85.19) * mm, "end": v(-38.82, 85.3) * mm});
            skLineSegment(sketch, "E4471", {"start": v(-38.82, 85.3) * mm, "end": v(-38.93, 85.42) * mm});
            skLineSegment(sketch, "E4472", {"start": v(-38.93, 85.42) * mm, "end": v(-39.04, 85.54) * mm});
            skLineSegment(sketch, "E4473", {"start": v(-39.04, 85.54) * mm, "end": v(-39.16, 85.66) * mm});
            skLineSegment(sketch, "E4474", {"start": v(-39.16, 85.66) * mm, "end": v(-39.28, 85.78) * mm});
            skLineSegment(sketch, "E4475", {"start": v(-39.28, 85.78) * mm, "end": v(-39.4, 85.9) * mm});
            skLineSegment(sketch, "E4476", {"start": v(-39.4, 85.9) * mm, "end": v(-39.52, 86.03) * mm});
            skLineSegment(sketch, "E4477", {"start": v(-39.52, 86.03) * mm, "end": v(-39.65, 86.15) * mm});
            skLineSegment(sketch, "E4478", {"start": v(-39.65, 86.15) * mm, "end": v(-39.78, 86.28) * mm});
            skLineSegment(sketch, "E4479", {"start": v(-39.78, 86.28) * mm, "end": v(-39.91, 86.4) * mm});
            skLineSegment(sketch, "E4480", {"start": v(-39.91, 86.4) * mm, "end": v(-40.05, 86.53) * mm});
            skLineSegment(sketch, "E4481", {"start": v(-40.05, 86.53) * mm, "end": v(-40.18, 86.66) * mm});
            skLineSegment(sketch, "E4482", {"start": v(-40.18, 86.66) * mm, "end": v(-40.32, 86.8) * mm});
            skLineSegment(sketch, "E4483", {"start": v(-40.32, 86.8) * mm, "end": v(-40.46, 86.92) * mm});
            skLineSegment(sketch, "E4484", {"start": v(-40.46, 86.92) * mm, "end": v(-40.6, 87.05) * mm});
            skLineSegment(sketch, "E4485", {"start": v(-40.6, 87.05) * mm, "end": v(-40.75, 87.19) * mm});
            skLineSegment(sketch, "E4486", {"start": v(-40.75, 87.19) * mm, "end": v(-40.9, 87.32) * mm});
            skLineSegment(sketch, "E4487", {"start": v(-40.9, 87.32) * mm, "end": v(-41.05, 87.45) * mm});
            skLineSegment(sketch, "E4488", {"start": v(-41.05, 87.45) * mm, "end": v(-41.2, 87.59) * mm});
            skLineSegment(sketch, "E4489", {"start": v(-41.2, 87.59) * mm, "end": v(-41.37, 87.72) * mm});
            skLineSegment(sketch, "E4490", {"start": v(-41.37, 87.72) * mm, "end": v(-41.5, 87.83) * mm});
            skLineSegment(sketch, "E4491", {"start": v(-41.5, 87.83) * mm, "end": v(-43.44, 86.89) * mm});
            skLineSegment(sketch, "E4492", {"start": v(-43.44, 86.89) * mm, "end": v(-43.45, 86.7) * mm});
            skLineSegment(sketch, "E4493", {"start": v(-43.45, 86.7) * mm, "end": v(-43.44, 86.5) * mm});
            skLineSegment(sketch, "E4494", {"start": v(-43.44, 86.5) * mm, "end": v(-43.43, 86.3) * mm});
            skLineSegment(sketch, "E4495", {"start": v(-43.43, 86.3) * mm, "end": v(-43.42, 86.1) * mm});
            skLineSegment(sketch, "E4496", {"start": v(-43.42, 86.1) * mm, "end": v(-43.4, 85.9) * mm});
            skLineSegment(sketch, "E4497", {"start": v(-43.4, 85.9) * mm, "end": v(-43.4, 85.7) * mm});
            skLineSegment(sketch, "E4498", {"start": v(-43.4, 85.7) * mm, "end": v(-43.38, 85.5) * mm});
            skLineSegment(sketch, "E4499", {"start": v(-43.38, 85.5) * mm, "end": v(-43.36, 85.31) * mm});
            skLineSegment(sketch, "E4500", {"start": v(-43.36, 85.31) * mm, "end": v(-43.35, 85.12) * mm});
            skLineSegment(sketch, "E4501", {"start": v(-43.35, 85.12) * mm, "end": v(-43.33, 84.94) * mm});
            skLineSegment(sketch, "E4502", {"start": v(-43.33, 84.94) * mm, "end": v(-43.31, 84.75) * mm});
            skLineSegment(sketch, "E4503", {"start": v(-43.31, 84.75) * mm, "end": v(-43.3, 84.57) * mm});
            skLineSegment(sketch, "E4504", {"start": v(-43.3, 84.57) * mm, "end": v(-43.27, 84.4) * mm});
            skLineSegment(sketch, "E4505", {"start": v(-43.27, 84.4) * mm, "end": v(-43.25, 84.21) * mm});
            skLineSegment(sketch, "E4506", {"start": v(-43.25, 84.21) * mm, "end": v(-43.23, 84.04) * mm});
            skLineSegment(sketch, "E4507", {"start": v(-43.23, 84.04) * mm, "end": v(-43.21, 83.87) * mm});
            skLineSegment(sketch, "E4508", {"start": v(-43.21, 83.87) * mm, "end": v(-43.2, 83.7) * mm});
            skLineSegment(sketch, "E4509", {"start": v(-43.2, 83.7) * mm, "end": v(-43.17, 83.53) * mm});
            skLineSegment(sketch, "E4510", {"start": v(-43.17, 83.53) * mm, "end": v(-43.15, 83.37) * mm});
            skLineSegment(sketch, "E4511", {"start": v(-43.15, 83.37) * mm, "end": v(-43.12, 83.2) * mm});
            skLineSegment(sketch, "E4512", {"start": v(-43.12, 83.2) * mm, "end": v(-43.1, 83.05) * mm});
            skLineSegment(sketch, "E4513", {"start": v(-43.1, 83.05) * mm, "end": v(-43.07, 82.9) * mm});
            skLineSegment(sketch, "E4514", {"start": v(-43.07, 82.9) * mm, "end": v(-43.05, 82.74) * mm});
            skLineSegment(sketch, "E4515", {"start": v(-43.05, 82.74) * mm, "end": v(-43.03, 82.6) * mm});
            skLineSegment(sketch, "E4516", {"start": v(-43.03, 82.6) * mm, "end": v(-43, 82.44) * mm});
            skLineSegment(sketch, "E4517", {"start": v(-43, 82.44) * mm, "end": v(-42.97, 82.3) * mm});
            skLineSegment(sketch, "E4518", {"start": v(-42.97, 82.3) * mm, "end": v(-42.95, 82.15) * mm});
            skLineSegment(sketch, "E4519", {"start": v(-42.95, 82.15) * mm, "end": v(-42.92, 82.01) * mm});
            skLineSegment(sketch, "E4520", {"start": v(-42.92, 82.01) * mm, "end": v(-42.9, 81.87) * mm});
            skLineSegment(sketch, "E4521", {"start": v(-42.9, 81.87) * mm, "end": v(-42.87, 81.74) * mm});
            skLineSegment(sketch, "E4522", {"start": v(-42.87, 81.74) * mm, "end": v(-42.84, 81.6) * mm});
            skLineSegment(sketch, "E4523", {"start": v(-42.84, 81.6) * mm, "end": v(-42.81, 81.48) * mm});
            skLineSegment(sketch, "E4524", {"start": v(-42.81, 81.48) * mm, "end": v(-42.79, 81.35) * mm});
            skLineSegment(sketch, "E4525", {"start": v(-42.79, 81.35) * mm, "end": v(-42.76, 81.22) * mm});
            skLineSegment(sketch, "E4526", {"start": v(-42.76, 81.22) * mm, "end": v(-42.73, 81.1) * mm});
            skLineSegment(sketch, "E4527", {"start": v(-42.73, 81.1) * mm, "end": v(-42.7, 80.98) * mm});
            skLineSegment(sketch, "E4528", {"start": v(-42.7, 80.98) * mm, "end": v(-42.67, 80.86) * mm});
            skLineSegment(sketch, "E4529", {"start": v(-42.67, 80.86) * mm, "end": v(-42.65, 80.75) * mm});
            skLineSegment(sketch, "E4530", {"start": v(-42.65, 80.75) * mm, "end": v(-42.62, 80.64) * mm});
            skLineSegment(sketch, "E4531", {"start": v(-42.62, 80.64) * mm, "end": v(-42.9, 80.25) * mm});
            skLineSegment(sketch, "E4532", {"start": v(-42.9, 80.25) * mm, "end": v(-44.38, 79.44) * mm});
            skLineSegment(sketch, "E4533", {"start": v(-44.38, 79.44) * mm, "end": v(-44.85, 79.41) * mm});
            skLineSegment(sketch, "E4534", {"start": v(-44.85, 79.41) * mm, "end": v(-44.93, 79.5) * mm});
            skLineSegment(sketch, "E4535", {"start": v(-44.93, 79.5) * mm, "end": v(-45.02, 79.58) * mm});
            skLineSegment(sketch, "E4536", {"start": v(-45.02, 79.58) * mm, "end": v(-45.1, 79.67) * mm});
            skLineSegment(sketch, "E4537", {"start": v(-45.1, 79.67) * mm, "end": v(-45.19, 79.76) * mm});
            skLineSegment(sketch, "E4538", {"start": v(-45.19, 79.76) * mm, "end": v(-45.27, 79.85) * mm});
            skLineSegment(sketch, "E4539", {"start": v(-45.27, 79.85) * mm, "end": v(-45.36, 79.94) * mm});
            skLineSegment(sketch, "E4540", {"start": v(-45.36, 79.94) * mm, "end": v(-45.46, 80.03) * mm});
            skLineSegment(sketch, "E4541", {"start": v(-45.46, 80.03) * mm, "end": v(-45.55, 80.12) * mm});
            skLineSegment(sketch, "E4542", {"start": v(-45.55, 80.12) * mm, "end": v(-45.65, 80.22) * mm});
            skLineSegment(sketch, "E4543", {"start": v(-45.65, 80.22) * mm, "end": v(-45.75, 80.32) * mm});
            skLineSegment(sketch, "E4544", {"start": v(-45.75, 80.32) * mm, "end": v(-45.85, 80.41) * mm});
            skLineSegment(sketch, "E4545", {"start": v(-45.85, 80.41) * mm, "end": v(-45.95, 80.51) * mm});
            skLineSegment(sketch, "E4546", {"start": v(-45.95, 80.51) * mm, "end": v(-46.06, 80.6) * mm});
            skLineSegment(sketch, "E4547", {"start": v(-46.06, 80.6) * mm, "end": v(-46.17, 80.7) * mm});
            skLineSegment(sketch, "E4548", {"start": v(-46.17, 80.7) * mm, "end": v(-46.28, 80.81) * mm});
            skLineSegment(sketch, "E4549", {"start": v(-46.28, 80.81) * mm, "end": v(-46.4, 80.91) * mm});
            skLineSegment(sketch, "E4550", {"start": v(-46.4, 80.91) * mm, "end": v(-46.5, 81.02) * mm});
            skLineSegment(sketch, "E4551", {"start": v(-46.5, 81.02) * mm, "end": v(-46.63, 81.12) * mm});
            skLineSegment(sketch, "E4552", {"start": v(-46.63, 81.12) * mm, "end": v(-46.75, 81.23) * mm});
            skLineSegment(sketch, "E4553", {"start": v(-46.75, 81.23) * mm, "end": v(-46.87, 81.33) * mm});
            skLineSegment(sketch, "E4554", {"start": v(-46.87, 81.33) * mm, "end": v(-47, 81.44) * mm});
            skLineSegment(sketch, "E4555", {"start": v(-47, 81.44) * mm, "end": v(-47.12, 81.55) * mm});
            skLineSegment(sketch, "E4556", {"start": v(-47.12, 81.55) * mm, "end": v(-47.26, 81.66) * mm});
            skLineSegment(sketch, "E4557", {"start": v(-47.26, 81.66) * mm, "end": v(-47.39, 81.77) * mm});
            skLineSegment(sketch, "E4558", {"start": v(-47.39, 81.77) * mm, "end": v(-47.52, 81.88) * mm});
            skLineSegment(sketch, "E4559", {"start": v(-47.52, 81.88) * mm, "end": v(-47.66, 82) * mm});
            skLineSegment(sketch, "E4560", {"start": v(-47.66, 82) * mm, "end": v(-47.8, 82.1) * mm});
            skLineSegment(sketch, "E4561", {"start": v(-47.8, 82.1) * mm, "end": v(-47.94, 82.22) * mm});
            skLineSegment(sketch, "E4562", {"start": v(-47.94, 82.22) * mm, "end": v(-48.1, 82.33) * mm});
            skLineSegment(sketch, "E4563", {"start": v(-48.1, 82.33) * mm, "end": v(-48.24, 82.45) * mm});
            skLineSegment(sketch, "E4564", {"start": v(-48.24, 82.45) * mm, "end": v(-48.39, 82.57) * mm});
            skLineSegment(sketch, "E4565", {"start": v(-48.39, 82.57) * mm, "end": v(-48.54, 82.68) * mm});
            skLineSegment(sketch, "E4566", {"start": v(-48.54, 82.68) * mm, "end": v(-48.7, 82.8) * mm});
            skLineSegment(sketch, "E4567", {"start": v(-48.7, 82.8) * mm, "end": v(-48.86, 82.92) * mm});
            skLineSegment(sketch, "E4568", {"start": v(-48.86, 82.92) * mm, "end": v(-49.02, 83.04) * mm});
            skLineSegment(sketch, "E4569", {"start": v(-49.02, 83.04) * mm, "end": v(-49.18, 83.15) * mm});
            skLineSegment(sketch, "E4570", {"start": v(-49.18, 83.15) * mm, "end": v(-49.35, 83.27) * mm});
            skLineSegment(sketch, "E4571", {"start": v(-49.35, 83.27) * mm, "end": v(-49.52, 83.4) * mm});
            skLineSegment(sketch, "E4572", {"start": v(-49.52, 83.4) * mm, "end": v(-49.67, 83.48) * mm});
            skLineSegment(sketch, "E4573", {"start": v(-49.67, 83.48) * mm, "end": v(-51.5, 82.36) * mm});
            skLineSegment(sketch, "E4574", {"start": v(-51.5, 82.36) * mm, "end": v(-51.5, 82.19) * mm});
            skLineSegment(sketch, "E4575", {"start": v(-51.5, 82.19) * mm, "end": v(-51.47, 81.98) * mm});
            skLineSegment(sketch, "E4576", {"start": v(-51.47, 81.98) * mm, "end": v(-51.44, 81.78) * mm});
            skLineSegment(sketch, "E4577", {"start": v(-51.44, 81.78) * mm, "end": v(-51.4, 81.58) * mm});
            skLineSegment(sketch, "E4578", {"start": v(-51.4, 81.58) * mm, "end": v(-51.37, 81.38) * mm});
            skLineSegment(sketch, "E4579", {"start": v(-51.37, 81.38) * mm, "end": v(-51.34, 81.19) * mm});
            skLineSegment(sketch, "E4580", {"start": v(-51.34, 81.19) * mm, "end": v(-51.3, 81) * mm});
            skLineSegment(sketch, "E4581", {"start": v(-51.3, 81) * mm, "end": v(-51.28, 80.8) * mm});
            skLineSegment(sketch, "E4582", {"start": v(-51.28, 80.8) * mm, "end": v(-51.24, 80.62) * mm});
            skLineSegment(sketch, "E4583", {"start": v(-51.24, 80.62) * mm, "end": v(-51.2, 80.43) * mm});
            skLineSegment(sketch, "E4584", {"start": v(-51.2, 80.43) * mm, "end": v(-51.17, 80.25) * mm});
            skLineSegment(sketch, "E4585", {"start": v(-51.17, 80.25) * mm, "end": v(-51.14, 80.07) * mm});
            skLineSegment(sketch, "E4586", {"start": v(-51.14, 80.07) * mm, "end": v(-51.1, 79.9) * mm});
            skLineSegment(sketch, "E4587", {"start": v(-51.1, 79.9) * mm, "end": v(-51.06, 79.72) * mm});
            skLineSegment(sketch, "E4588", {"start": v(-51.06, 79.72) * mm, "end": v(-51.03, 79.55) * mm});
            skLineSegment(sketch, "E4589", {"start": v(-51.03, 79.55) * mm, "end": v(-50.99, 79.38) * mm});
            skLineSegment(sketch, "E4590", {"start": v(-50.99, 79.38) * mm, "end": v(-50.95, 79.22) * mm});
            skLineSegment(sketch, "E4591", {"start": v(-50.95, 79.22) * mm, "end": v(-50.91, 79.05) * mm});
            skLineSegment(sketch, "E4592", {"start": v(-50.91, 79.05) * mm, "end": v(-50.88, 78.9) * mm});
            skLineSegment(sketch, "E4593", {"start": v(-50.88, 78.9) * mm, "end": v(-50.84, 78.73) * mm});
            skLineSegment(sketch, "E4594", {"start": v(-50.84, 78.73) * mm, "end": v(-50.8, 78.58) * mm});
            skLineSegment(sketch, "E4595", {"start": v(-50.8, 78.58) * mm, "end": v(-50.76, 78.42) * mm});
            skLineSegment(sketch, "E4596", {"start": v(-50.76, 78.42) * mm, "end": v(-50.72, 78.27) * mm});
            skLineSegment(sketch, "E4597", {"start": v(-50.72, 78.27) * mm, "end": v(-50.68, 78.13) * mm});
            skLineSegment(sketch, "E4598", {"start": v(-50.68, 78.13) * mm, "end": v(-50.64, 77.98) * mm});
            skLineSegment(sketch, "E4599", {"start": v(-50.64, 77.98) * mm, "end": v(-50.6, 77.84) * mm});
            skLineSegment(sketch, "E4600", {"start": v(-50.6, 77.84) * mm, "end": v(-50.56, 77.7) * mm});
            skLineSegment(sketch, "E4601", {"start": v(-50.56, 77.7) * mm, "end": v(-50.52, 77.56) * mm});
            skLineSegment(sketch, "E4602", {"start": v(-50.52, 77.56) * mm, "end": v(-50.48, 77.43) * mm});
            skLineSegment(sketch, "E4603", {"start": v(-50.48, 77.43) * mm, "end": v(-50.44, 77.3) * mm});
            skLineSegment(sketch, "E4604", {"start": v(-50.44, 77.3) * mm, "end": v(-50.4, 77.16) * mm});
            skLineSegment(sketch, "E4605", {"start": v(-50.4, 77.16) * mm, "end": v(-50.36, 77.04) * mm});
            skLineSegment(sketch, "E4606", {"start": v(-50.36, 77.04) * mm, "end": v(-50.32, 76.91) * mm});
            skLineSegment(sketch, "E4607", {"start": v(-50.32, 76.91) * mm, "end": v(-50.29, 76.8) * mm});
            skLineSegment(sketch, "E4608", {"start": v(-50.29, 76.8) * mm, "end": v(-50.25, 76.67) * mm});
            skLineSegment(sketch, "E4609", {"start": v(-50.25, 76.67) * mm, "end": v(-50.2, 76.56) * mm});
            skLineSegment(sketch, "E4610", {"start": v(-50.2, 76.56) * mm, "end": v(-50.17, 76.44) * mm});
            skLineSegment(sketch, "E4611", {"start": v(-50.17, 76.44) * mm, "end": v(-50.13, 76.33) * mm});
            skLineSegment(sketch, "E4612", {"start": v(-50.13, 76.33) * mm, "end": v(-50.1, 76.22) * mm});
            skLineSegment(sketch, "E4613", {"start": v(-50.1, 76.22) * mm, "end": v(-50.33, 75.81) * mm});
            skLineSegment(sketch, "E4614", {"start": v(-50.33, 75.81) * mm, "end": v(-51.73, 74.87) * mm});
            skLineSegment(sketch, "E4615", {"start": v(-51.73, 74.87) * mm, "end": v(-52.2, 74.8) * mm});
            skLineSegment(sketch, "E4616", {"start": v(-52.2, 74.8) * mm, "end": v(-52.29, 74.87) * mm});
            skLineSegment(sketch, "E4617", {"start": v(-52.29, 74.87) * mm, "end": v(-52.38, 74.94) * mm});
            skLineSegment(sketch, "E4618", {"start": v(-52.38, 74.94) * mm, "end": v(-52.47, 75.02) * mm});
            skLineSegment(sketch, "E4619", {"start": v(-52.47, 75.02) * mm, "end": v(-52.56, 75.1) * mm});
            skLineSegment(sketch, "E4620", {"start": v(-52.56, 75.1) * mm, "end": v(-52.66, 75.18) * mm});
            skLineSegment(sketch, "E4621", {"start": v(-52.66, 75.18) * mm, "end": v(-52.76, 75.27) * mm});
            skLineSegment(sketch, "E4622", {"start": v(-52.76, 75.27) * mm, "end": v(-52.86, 75.35) * mm});
            skLineSegment(sketch, "E4623", {"start": v(-52.86, 75.35) * mm, "end": v(-52.96, 75.43) * mm});
            skLineSegment(sketch, "E4624", {"start": v(-52.96, 75.43) * mm, "end": v(-53.07, 75.52) * mm});
            skLineSegment(sketch, "E4625", {"start": v(-53.07, 75.52) * mm, "end": v(-53.18, 75.6) * mm});
            skLineSegment(sketch, "E4626", {"start": v(-53.18, 75.6) * mm, "end": v(-53.29, 75.69) * mm});
            skLineSegment(sketch, "E4627", {"start": v(-53.29, 75.69) * mm, "end": v(-53.4, 75.78) * mm});
            skLineSegment(sketch, "E4628", {"start": v(-53.4, 75.78) * mm, "end": v(-53.51, 75.87) * mm});
            skLineSegment(sketch, "E4629", {"start": v(-53.51, 75.87) * mm, "end": v(-53.63, 75.96) * mm});
            skLineSegment(sketch, "E4630", {"start": v(-53.63, 75.96) * mm, "end": v(-53.75, 76.05) * mm});
            skLineSegment(sketch, "E4631", {"start": v(-53.75, 76.05) * mm, "end": v(-53.87, 76.14) * mm});
            skLineSegment(sketch, "E4632", {"start": v(-53.87, 76.14) * mm, "end": v(-54, 76.23) * mm});
            skLineSegment(sketch, "E4633", {"start": v(-54, 76.23) * mm, "end": v(-54.13, 76.32) * mm});
            skLineSegment(sketch, "E4634", {"start": v(-54.13, 76.32) * mm, "end": v(-54.26, 76.42) * mm});
            skLineSegment(sketch, "E4635", {"start": v(-54.26, 76.42) * mm, "end": v(-54.4, 76.51) * mm});
            skLineSegment(sketch, "E4636", {"start": v(-54.4, 76.51) * mm, "end": v(-54.53, 76.6) * mm});
            skLineSegment(sketch, "E4637", {"start": v(-54.53, 76.6) * mm, "end": v(-54.66, 76.7) * mm});
            skLineSegment(sketch, "E4638", {"start": v(-54.66, 76.7) * mm, "end": v(-54.8, 76.8) * mm});
            skLineSegment(sketch, "E4639", {"start": v(-54.8, 76.8) * mm, "end": v(-54.95, 76.9) * mm});
            skLineSegment(sketch, "E4640", {"start": v(-54.95, 76.9) * mm, "end": v(-55.1, 77) * mm});
            skLineSegment(sketch, "E4641", {"start": v(-55.1, 77) * mm, "end": v(-55.24, 77.1) * mm});
            skLineSegment(sketch, "E4642", {"start": v(-55.24, 77.1) * mm, "end": v(-55.4, 77.2) * mm});
            skLineSegment(sketch, "E4643", {"start": v(-55.4, 77.2) * mm, "end": v(-55.54, 77.3) * mm});
            skLineSegment(sketch, "E4644", {"start": v(-55.54, 77.3) * mm, "end": v(-55.7, 77.4) * mm});
            skLineSegment(sketch, "E4645", {"start": v(-55.7, 77.4) * mm, "end": v(-55.86, 77.5) * mm});
            skLineSegment(sketch, "E4646", {"start": v(-55.86, 77.5) * mm, "end": v(-56.02, 77.6) * mm});
            skLineSegment(sketch, "E4647", {"start": v(-56.02, 77.6) * mm, "end": v(-56.18, 77.7) * mm});
            skLineSegment(sketch, "E4648", {"start": v(-56.18, 77.7) * mm, "end": v(-56.35, 77.8) * mm});
            skLineSegment(sketch, "E4649", {"start": v(-56.35, 77.8) * mm, "end": v(-56.52, 77.9) * mm});
            skLineSegment(sketch, "E4650", {"start": v(-56.52, 77.9) * mm, "end": v(-56.69, 78) * mm});
            skLineSegment(sketch, "E4651", {"start": v(-56.69, 78) * mm, "end": v(-56.86, 78.1) * mm});
            skLineSegment(sketch, "E4652", {"start": v(-56.86, 78.1) * mm, "end": v(-57.04, 78.2) * mm});
            skLineSegment(sketch, "E4653", {"start": v(-57.04, 78.2) * mm, "end": v(-57.22, 78.31) * mm});
            skLineSegment(sketch, "E4654", {"start": v(-57.22, 78.31) * mm, "end": v(-57.38, 78.38) * mm});
            skLineSegment(sketch, "E4655", {"start": v(-57.38, 78.38) * mm, "end": v(-59.1, 77.1) * mm});
            skLineSegment(sketch, "E4656", {"start": v(-59.1, 77.1) * mm, "end": v(-59.08, 76.92) * mm});
            skLineSegment(sketch, "E4657", {"start": v(-59.08, 76.92) * mm, "end": v(-59.03, 76.72) * mm});
            skLineSegment(sketch, "E4658", {"start": v(-59.03, 76.72) * mm, "end": v(-58.98, 76.52) * mm});
            skLineSegment(sketch, "E4659", {"start": v(-58.98, 76.52) * mm, "end": v(-58.93, 76.32) * mm});
            skLineSegment(sketch, "E4660", {"start": v(-58.93, 76.32) * mm, "end": v(-58.88, 76.13) * mm});
            skLineSegment(sketch, "E4661", {"start": v(-58.88, 76.13) * mm, "end": v(-58.83, 75.94) * mm});
            skLineSegment(sketch, "E4662", {"start": v(-58.83, 75.94) * mm, "end": v(-58.78, 75.75) * mm});
            skLineSegment(sketch, "E4663", {"start": v(-58.78, 75.75) * mm, "end": v(-58.72, 75.56) * mm});
            skLineSegment(sketch, "E4664", {"start": v(-58.72, 75.56) * mm, "end": v(-58.67, 75.38) * mm});
            skLineSegment(sketch, "E4665", {"start": v(-58.67, 75.38) * mm, "end": v(-58.62, 75.2) * mm});
            skLineSegment(sketch, "E4666", {"start": v(-58.62, 75.2) * mm, "end": v(-58.57, 75.02) * mm});
            skLineSegment(sketch, "E4667", {"start": v(-58.57, 75.02) * mm, "end": v(-58.52, 74.85) * mm});
            skLineSegment(sketch, "E4668", {"start": v(-58.52, 74.85) * mm, "end": v(-58.46, 74.68) * mm});
            skLineSegment(sketch, "E4669", {"start": v(-58.46, 74.68) * mm, "end": v(-58.41, 74.5) * mm});
            skLineSegment(sketch, "E4670", {"start": v(-58.41, 74.5) * mm, "end": v(-58.36, 74.34) * mm});
            skLineSegment(sketch, "E4671", {"start": v(-58.36, 74.34) * mm, "end": v(-58.3, 74.18) * mm});
            skLineSegment(sketch, "E4672", {"start": v(-58.3, 74.18) * mm, "end": v(-58.25, 74.01) * mm});
            skLineSegment(sketch, "E4673", {"start": v(-58.25, 74.01) * mm, "end": v(-58.2, 73.85) * mm});
            skLineSegment(sketch, "E4674", {"start": v(-58.2, 73.85) * mm, "end": v(-58.14, 73.7) * mm});
            skLineSegment(sketch, "E4675", {"start": v(-58.14, 73.7) * mm, "end": v(-58.1, 73.54) * mm});
            skLineSegment(sketch, "E4676", {"start": v(-58.1, 73.54) * mm, "end": v(-58.04, 73.4) * mm});
            skLineSegment(sketch, "E4677", {"start": v(-58.04, 73.4) * mm, "end": v(-57.98, 73.24) * mm});
            skLineSegment(sketch, "E4678", {"start": v(-57.98, 73.24) * mm, "end": v(-57.93, 73.1) * mm});
            skLineSegment(sketch, "E4679", {"start": v(-57.93, 73.1) * mm, "end": v(-57.88, 72.96) * mm});
            skLineSegment(sketch, "E4680", {"start": v(-57.88, 72.96) * mm, "end": v(-57.82, 72.81) * mm});
            skLineSegment(sketch, "E4681", {"start": v(-57.82, 72.81) * mm, "end": v(-57.77, 72.68) * mm});
            skLineSegment(sketch, "E4682", {"start": v(-57.77, 72.68) * mm, "end": v(-57.72, 72.54) * mm});
            skLineSegment(sketch, "E4683", {"start": v(-57.72, 72.54) * mm, "end": v(-57.67, 72.4) * mm});
            skLineSegment(sketch, "E4684", {"start": v(-57.67, 72.4) * mm, "end": v(-57.61, 72.28) * mm});
            skLineSegment(sketch, "E4685", {"start": v(-57.61, 72.28) * mm, "end": v(-57.56, 72.15) * mm});
            skLineSegment(sketch, "E4686", {"start": v(-57.56, 72.15) * mm, "end": v(-57.51, 72.02) * mm});
            skLineSegment(sketch, "E4687", {"start": v(-57.51, 72.02) * mm, "end": v(-57.46, 71.9) * mm});
            skLineSegment(sketch, "E4688", {"start": v(-57.46, 71.9) * mm, "end": v(-57.4, 71.78) * mm});
            skLineSegment(sketch, "E4689", {"start": v(-57.4, 71.78) * mm, "end": v(-57.36, 71.66) * mm});
            skLineSegment(sketch, "E4690", {"start": v(-57.36, 71.66) * mm, "end": v(-57.3, 71.55) * mm});
            skLineSegment(sketch, "E4691", {"start": v(-57.3, 71.55) * mm, "end": v(-57.26, 71.44) * mm});
            skLineSegment(sketch, "E4692", {"start": v(-57.26, 71.44) * mm, "end": v(-57.2, 71.33) * mm});
            skLineSegment(sketch, "E4693", {"start": v(-57.2, 71.33) * mm, "end": v(-57.16, 71.22) * mm});
            skLineSegment(sketch, "E4694", {"start": v(-57.16, 71.22) * mm, "end": v(-57.1, 71.11) * mm});
            skLineSegment(sketch, "E4695", {"start": v(-57.1, 71.11) * mm, "end": v(-57.31, 70.68) * mm});
            skLineSegment(sketch, "E4696", {"start": v(-57.31, 70.68) * mm, "end": v(-58.61, 69.6) * mm});
            skLineSegment(sketch, "E4697", {"start": v(-58.61, 69.6) * mm, "end": v(-59.07, 69.5) * mm});
            skLineSegment(sketch, "E4698", {"start": v(-59.07, 69.5) * mm, "end": v(-59.17, 69.56) * mm});
            skLineSegment(sketch, "E4699", {"start": v(-59.17, 69.56) * mm, "end": v(-59.26, 69.63) * mm});
            skLineSegment(sketch, "E4700", {"start": v(-59.26, 69.63) * mm, "end": v(-59.36, 69.7) * mm});
            skLineSegment(sketch, "E4701", {"start": v(-59.36, 69.7) * mm, "end": v(-59.46, 69.77) * mm});
            skLineSegment(sketch, "E4702", {"start": v(-59.46, 69.77) * mm, "end": v(-59.57, 69.84) * mm});
            skLineSegment(sketch, "E4703", {"start": v(-59.57, 69.84) * mm, "end": v(-59.67, 69.9) * mm});
            skLineSegment(sketch, "E4704", {"start": v(-59.67, 69.9) * mm, "end": v(-59.78, 69.98) * mm});
            skLineSegment(sketch, "E4705", {"start": v(-59.78, 69.98) * mm, "end": v(-59.9, 70.06) * mm});
            skLineSegment(sketch, "E4706", {"start": v(-59.9, 70.06) * mm, "end": v(-60, 70.13) * mm});
            skLineSegment(sketch, "E4707", {"start": v(-60, 70.13) * mm, "end": v(-60.12, 70.2) * mm});
            skLineSegment(sketch, "E4708", {"start": v(-60.12, 70.2) * mm, "end": v(-60.24, 70.28) * mm});
            skLineSegment(sketch, "E4709", {"start": v(-60.24, 70.28) * mm, "end": v(-60.36, 70.36) * mm});
            skLineSegment(sketch, "E4710", {"start": v(-60.36, 70.36) * mm, "end": v(-60.48, 70.44) * mm});
            skLineSegment(sketch, "E4711", {"start": v(-60.48, 70.44) * mm, "end": v(-60.6, 70.51) * mm});
            skLineSegment(sketch, "E4712", {"start": v(-60.6, 70.51) * mm, "end": v(-60.74, 70.6) * mm});
            skLineSegment(sketch, "E4713", {"start": v(-60.74, 70.6) * mm, "end": v(-60.87, 70.67) * mm});
            skLineSegment(sketch, "E4714", {"start": v(-60.87, 70.67) * mm, "end": v(-61, 70.75) * mm});
            skLineSegment(sketch, "E4715", {"start": v(-61, 70.75) * mm, "end": v(-61.14, 70.83) * mm});
            skLineSegment(sketch, "E4716", {"start": v(-61.14, 70.83) * mm, "end": v(-61.28, 70.91) * mm});
            skLineSegment(sketch, "E4717", {"start": v(-61.28, 70.91) * mm, "end": v(-61.42, 71) * mm});
            skLineSegment(sketch, "E4718", {"start": v(-61.42, 71) * mm, "end": v(-61.56, 71.08) * mm});
            skLineSegment(sketch, "E4719", {"start": v(-61.56, 71.08) * mm, "end": v(-61.7, 71.16) * mm});
            skLineSegment(sketch, "E4720", {"start": v(-61.7, 71.16) * mm, "end": v(-61.86, 71.24) * mm});
            skLineSegment(sketch, "E4721", {"start": v(-61.86, 71.24) * mm, "end": v(-62, 71.32) * mm});
            skLineSegment(sketch, "E4722", {"start": v(-62, 71.32) * mm, "end": v(-62.16, 71.4) * mm});
            skLineSegment(sketch, "E4723", {"start": v(-62.16, 71.4) * mm, "end": v(-62.32, 71.5) * mm});
            skLineSegment(sketch, "E4724", {"start": v(-62.32, 71.5) * mm, "end": v(-62.48, 71.58) * mm});
            skLineSegment(sketch, "E4725", {"start": v(-62.48, 71.58) * mm, "end": v(-62.64, 71.66) * mm});
            skLineSegment(sketch, "E4726", {"start": v(-62.64, 71.66) * mm, "end": v(-62.8, 71.75) * mm});
            skLineSegment(sketch, "E4727", {"start": v(-62.8, 71.75) * mm, "end": v(-62.97, 71.83) * mm});
            skLineSegment(sketch, "E4728", {"start": v(-62.97, 71.83) * mm, "end": v(-63.14, 71.92) * mm});
            skLineSegment(sketch, "E4729", {"start": v(-63.14, 71.92) * mm, "end": v(-63.31, 72) * mm});
            skLineSegment(sketch, "E4730", {"start": v(-63.31, 72) * mm, "end": v(-63.49, 72.09) * mm});
            skLineSegment(sketch, "E4731", {"start": v(-63.49, 72.09) * mm, "end": v(-63.67, 72.17) * mm});
            skLineSegment(sketch, "E4732", {"start": v(-63.67, 72.17) * mm, "end": v(-63.85, 72.26) * mm});
            skLineSegment(sketch, "E4733", {"start": v(-63.85, 72.26) * mm, "end": v(-64.03, 72.34) * mm});
            skLineSegment(sketch, "E4734", {"start": v(-64.03, 72.34) * mm, "end": v(-64.22, 72.43) * mm});
            skLineSegment(sketch, "E4735", {"start": v(-64.22, 72.43) * mm, "end": v(-64.4, 72.52) * mm});
            skLineSegment(sketch, "E4736", {"start": v(-64.4, 72.52) * mm, "end": v(-64.57, 72.58) * mm});
            skLineSegment(sketch, "E4737", {"start": v(-64.57, 72.58) * mm, "end": v(-66.16, 71.13) * mm});
            skLineSegment(sketch, "E4738", {"start": v(-66.16, 71.13) * mm, "end": v(-66.12, 70.96) * mm});
            skLineSegment(sketch, "E4739", {"start": v(-66.12, 70.96) * mm, "end": v(-66.05, 70.76) * mm});
            skLineSegment(sketch, "E4740", {"start": v(-66.05, 70.76) * mm, "end": v(-65.98, 70.57) * mm});
            skLineSegment(sketch, "E4741", {"start": v(-65.98, 70.57) * mm, "end": v(-65.92, 70.38) * mm});
            skLineSegment(sketch, "E4742", {"start": v(-65.92, 70.38) * mm, "end": v(-65.85, 70.19) * mm});
            skLineSegment(sketch, "E4743", {"start": v(-65.85, 70.19) * mm, "end": v(-65.78, 70) * mm});
            skLineSegment(sketch, "E4744", {"start": v(-65.78, 70) * mm, "end": v(-65.71, 69.82) * mm});
            skLineSegment(sketch, "E4745", {"start": v(-65.71, 69.82) * mm, "end": v(-65.64, 69.64) * mm});
            skLineSegment(sketch, "E4746", {"start": v(-65.64, 69.64) * mm, "end": v(-65.57, 69.46) * mm});
            skLineSegment(sketch, "E4747", {"start": v(-65.57, 69.46) * mm, "end": v(-65.5, 69.29) * mm});
            skLineSegment(sketch, "E4748", {"start": v(-65.5, 69.29) * mm, "end": v(-65.43, 69.12) * mm});
            skLineSegment(sketch, "E4749", {"start": v(-65.43, 69.12) * mm, "end": v(-65.37, 68.95) * mm});
            skLineSegment(sketch, "E4750", {"start": v(-65.37, 68.95) * mm, "end": v(-65.3, 68.78) * mm});
            skLineSegment(sketch, "E4751", {"start": v(-65.3, 68.78) * mm, "end": v(-65.23, 68.62) * mm});
            skLineSegment(sketch, "E4752", {"start": v(-65.23, 68.62) * mm, "end": v(-65.16, 68.46) * mm});
            skLineSegment(sketch, "E4753", {"start": v(-65.16, 68.46) * mm, "end": v(-65.1, 68.3) * mm});
            skLineSegment(sketch, "E4754", {"start": v(-65.1, 68.3) * mm, "end": v(-65.02, 68.14) * mm});
            skLineSegment(sketch, "E4755", {"start": v(-65.02, 68.14) * mm, "end": v(-64.95, 67.99) * mm});
            skLineSegment(sketch, "E4756", {"start": v(-64.95, 67.99) * mm, "end": v(-64.89, 67.84) * mm});
            skLineSegment(sketch, "E4757", {"start": v(-64.89, 67.84) * mm, "end": v(-64.82, 67.69) * mm});
            skLineSegment(sketch, "E4758", {"start": v(-64.82, 67.69) * mm, "end": v(-64.75, 67.54) * mm});
            skLineSegment(sketch, "E4759", {"start": v(-64.75, 67.54) * mm, "end": v(-64.68, 67.4) * mm});
            skLineSegment(sketch, "E4760", {"start": v(-64.68, 67.4) * mm, "end": v(-64.62, 67.26) * mm});
            skLineSegment(sketch, "E4761", {"start": v(-64.62, 67.26) * mm, "end": v(-64.55, 67.12) * mm});
            skLineSegment(sketch, "E4762", {"start": v(-64.55, 67.12) * mm, "end": v(-64.48, 66.99) * mm});
            skLineSegment(sketch, "E4763", {"start": v(-64.48, 66.99) * mm, "end": v(-64.42, 66.86) * mm});
            skLineSegment(sketch, "E4764", {"start": v(-64.42, 66.86) * mm, "end": v(-64.35, 66.73) * mm});
            skLineSegment(sketch, "E4765", {"start": v(-64.35, 66.73) * mm, "end": v(-64.29, 66.6) * mm});
            skLineSegment(sketch, "E4766", {"start": v(-64.29, 66.6) * mm, "end": v(-64.22, 66.47) * mm});
            skLineSegment(sketch, "E4767", {"start": v(-64.22, 66.47) * mm, "end": v(-64.16, 66.35) * mm});
            skLineSegment(sketch, "E4768", {"start": v(-64.16, 66.35) * mm, "end": v(-64.1, 66.23) * mm});
            skLineSegment(sketch, "E4769", {"start": v(-64.1, 66.23) * mm, "end": v(-64.03, 66.11) * mm});
            skLineSegment(sketch, "E4770", {"start": v(-64.03, 66.11) * mm, "end": v(-63.97, 66) * mm});
            skLineSegment(sketch, "E4771", {"start": v(-63.97, 66) * mm, "end": v(-63.9, 65.89) * mm});
            skLineSegment(sketch, "E4772", {"start": v(-63.9, 65.89) * mm, "end": v(-63.85, 65.78) * mm});
            skLineSegment(sketch, "E4773", {"start": v(-63.85, 65.78) * mm, "end": v(-63.79, 65.67) * mm});
            skLineSegment(sketch, "E4774", {"start": v(-63.79, 65.67) * mm, "end": v(-63.73, 65.57) * mm});
            skLineSegment(sketch, "E4775", {"start": v(-63.73, 65.57) * mm, "end": v(-63.67, 65.46) * mm});
            skLineSegment(sketch, "E4776", {"start": v(-63.67, 65.46) * mm, "end": v(-63.61, 65.36) * mm});
            skLineSegment(sketch, "E4777", {"start": v(-63.61, 65.36) * mm, "end": v(-63.77, 64.92) * mm});
            skLineSegment(sketch, "E4778", {"start": v(-63.77, 64.92) * mm, "end": v(-64.97, 63.72) * mm});
            skLineSegment(sketch, "E4779", {"start": v(-64.97, 63.72) * mm, "end": v(-65.41, 63.56) * mm});
            skLineSegment(sketch, "E4780", {"start": v(-65.41, 63.56) * mm, "end": v(-65.51, 63.62) * mm});
            skLineSegment(sketch, "E4781", {"start": v(-65.51, 63.62) * mm, "end": v(-65.61, 63.68) * mm});
            skLineSegment(sketch, "E4782", {"start": v(-65.61, 63.68) * mm, "end": v(-65.72, 63.74) * mm});
            skLineSegment(sketch, "E4783", {"start": v(-65.72, 63.74) * mm, "end": v(-65.83, 63.8) * mm});
            skLineSegment(sketch, "E4784", {"start": v(-65.83, 63.8) * mm, "end": v(-65.94, 63.86) * mm});
            skLineSegment(sketch, "E4785", {"start": v(-65.94, 63.86) * mm, "end": v(-66.05, 63.92) * mm});
            skLineSegment(sketch, "E4786", {"start": v(-66.05, 63.92) * mm, "end": v(-66.16, 63.98) * mm});
            skLineSegment(sketch, "E4787", {"start": v(-66.16, 63.98) * mm, "end": v(-66.28, 64.05) * mm});
            skLineSegment(sketch, "E4788", {"start": v(-66.28, 64.05) * mm, "end": v(-66.4, 64.1) * mm});
            skLineSegment(sketch, "E4789", {"start": v(-66.4, 64.1) * mm, "end": v(-66.52, 64.17) * mm});
            skLineSegment(sketch, "E4790", {"start": v(-66.52, 64.17) * mm, "end": v(-66.65, 64.24) * mm});
            skLineSegment(sketch, "E4791", {"start": v(-66.65, 64.24) * mm, "end": v(-66.77, 64.3) * mm});
            skLineSegment(sketch, "E4792", {"start": v(-66.77, 64.3) * mm, "end": v(-66.9, 64.37) * mm});
            skLineSegment(sketch, "E4793", {"start": v(-66.9, 64.37) * mm, "end": v(-67.04, 64.43) * mm});
            skLineSegment(sketch, "E4794", {"start": v(-67.04, 64.43) * mm, "end": v(-67.17, 64.5) * mm});
            skLineSegment(sketch, "E4795", {"start": v(-67.17, 64.5) * mm, "end": v(-67.31, 64.57) * mm});
            skLineSegment(sketch, "E4796", {"start": v(-67.31, 64.57) * mm, "end": v(-67.45, 64.63) * mm});
            skLineSegment(sketch, "E4797", {"start": v(-67.45, 64.63) * mm, "end": v(-67.6, 64.7) * mm});
            skLineSegment(sketch, "E4798", {"start": v(-67.6, 64.7) * mm, "end": v(-67.74, 64.77) * mm});
            skLineSegment(sketch, "E4799", {"start": v(-67.74, 64.77) * mm, "end": v(-67.89, 64.83) * mm});
            skLineSegment(sketch, "E4800", {"start": v(-67.89, 64.83) * mm, "end": v(-68.04, 64.9) * mm});
            skLineSegment(sketch, "E4801", {"start": v(-68.04, 64.9) * mm, "end": v(-68.2, 64.97) * mm});
            skLineSegment(sketch, "E4802", {"start": v(-68.2, 64.97) * mm, "end": v(-68.35, 65.04) * mm});
            skLineSegment(sketch, "E4803", {"start": v(-68.35, 65.04) * mm, "end": v(-68.5, 65.1) * mm});
            skLineSegment(sketch, "E4804", {"start": v(-68.5, 65.1) * mm, "end": v(-68.67, 65.18) * mm});
            skLineSegment(sketch, "E4805", {"start": v(-68.67, 65.18) * mm, "end": v(-68.83, 65.24) * mm});
            skLineSegment(sketch, "E4806", {"start": v(-68.83, 65.24) * mm, "end": v(-69, 65.31) * mm});
            skLineSegment(sketch, "E4807", {"start": v(-69, 65.31) * mm, "end": v(-69.17, 65.38) * mm});
            skLineSegment(sketch, "E4808", {"start": v(-69.17, 65.38) * mm, "end": v(-69.34, 65.45) * mm});
            skLineSegment(sketch, "E4809", {"start": v(-69.34, 65.45) * mm, "end": v(-69.51, 65.52) * mm});
            skLineSegment(sketch, "E4810", {"start": v(-69.51, 65.52) * mm, "end": v(-69.7, 65.59) * mm});
            skLineSegment(sketch, "E4811", {"start": v(-69.7, 65.59) * mm, "end": v(-69.87, 65.66) * mm});
            skLineSegment(sketch, "E4812", {"start": v(-69.87, 65.66) * mm, "end": v(-70.05, 65.73) * mm});
            skLineSegment(sketch, "E4813", {"start": v(-70.05, 65.73) * mm, "end": v(-70.24, 65.8) * mm});
            skLineSegment(sketch, "E4814", {"start": v(-70.24, 65.8) * mm, "end": v(-70.43, 65.86) * mm});
            skLineSegment(sketch, "E4815", {"start": v(-70.43, 65.86) * mm, "end": v(-70.62, 65.93) * mm});
            skLineSegment(sketch, "E4816", {"start": v(-70.62, 65.93) * mm, "end": v(-70.81, 66) * mm});
            skLineSegment(sketch, "E4817", {"start": v(-70.81, 66) * mm, "end": v(-71, 66.07) * mm});
            skLineSegment(sketch, "E4818", {"start": v(-71, 66.07) * mm, "end": v(-71.18, 66.1) * mm});
            skLineSegment(sketch, "E4819", {"start": v(-71.18, 66.1) * mm, "end": v(-72.62, 64.52) * mm});
            skLineSegment(sketch, "E4820", {"start": v(-72.62, 64.52) * mm, "end": v(-72.57, 64.35) * mm});
            skLineSegment(sketch, "E4821", {"start": v(-72.57, 64.35) * mm, "end": v(-72.48, 64.16) * mm});
            skLineSegment(sketch, "E4822", {"start": v(-72.48, 64.16) * mm, "end": v(-72.4, 63.97) * mm});
            skLineSegment(sketch, "E4823", {"start": v(-72.4, 63.97) * mm, "end": v(-72.3, 63.8) * mm});
            skLineSegment(sketch, "E4824", {"start": v(-72.3, 63.8) * mm, "end": v(-72.22, 63.61) * mm});
            skLineSegment(sketch, "E4825", {"start": v(-72.22, 63.61) * mm, "end": v(-72.14, 63.43) * mm});
            skLineSegment(sketch, "E4826", {"start": v(-72.14, 63.43) * mm, "end": v(-72.05, 63.26) * mm});
            skLineSegment(sketch, "E4827", {"start": v(-72.05, 63.26) * mm, "end": v(-71.96, 63.09) * mm});
            skLineSegment(sketch, "E4828", {"start": v(-71.96, 63.09) * mm, "end": v(-71.88, 62.92) * mm});
            skLineSegment(sketch, "E4829", {"start": v(-71.88, 62.92) * mm, "end": v(-71.8, 62.75) * mm});
            skLineSegment(sketch, "E4830", {"start": v(-71.8, 62.75) * mm, "end": v(-71.7, 62.58) * mm});
            skLineSegment(sketch, "E4831", {"start": v(-71.7, 62.58) * mm, "end": v(-71.62, 62.42) * mm});
            skLineSegment(sketch, "E4832", {"start": v(-71.62, 62.42) * mm, "end": v(-71.54, 62.26) * mm});
            skLineSegment(sketch, "E4833", {"start": v(-71.54, 62.26) * mm, "end": v(-71.46, 62.1) * mm});
            skLineSegment(sketch, "E4834", {"start": v(-71.46, 62.1) * mm, "end": v(-71.37, 61.95) * mm});
            skLineSegment(sketch, "E4835", {"start": v(-71.37, 61.95) * mm, "end": v(-71.29, 61.8) * mm});
            skLineSegment(sketch, "E4836", {"start": v(-71.29, 61.8) * mm, "end": v(-71.2, 61.65) * mm});
            skLineSegment(sketch, "E4837", {"start": v(-71.2, 61.65) * mm, "end": v(-71.12, 61.5) * mm});
            skLineSegment(sketch, "E4838", {"start": v(-71.12, 61.5) * mm, "end": v(-71.04, 61.36) * mm});
            skLineSegment(sketch, "E4839", {"start": v(-71.04, 61.36) * mm, "end": v(-70.96, 61.22) * mm});
            skLineSegment(sketch, "E4840", {"start": v(-70.96, 61.22) * mm, "end": v(-70.88, 61.08) * mm});
            skLineSegment(sketch, "E4841", {"start": v(-70.88, 61.08) * mm, "end": v(-70.8, 60.95) * mm});
            skLineSegment(sketch, "E4842", {"start": v(-70.8, 60.95) * mm, "end": v(-70.72, 60.81) * mm});
            skLineSegment(sketch, "E4843", {"start": v(-70.72, 60.81) * mm, "end": v(-70.64, 60.68) * mm});
            skLineSegment(sketch, "E4844", {"start": v(-70.64, 60.68) * mm, "end": v(-70.56, 60.56) * mm});
            skLineSegment(sketch, "E4845", {"start": v(-70.56, 60.56) * mm, "end": v(-70.48, 60.43) * mm});
            skLineSegment(sketch, "E4846", {"start": v(-70.48, 60.43) * mm, "end": v(-70.4, 60.3) * mm});
            skLineSegment(sketch, "E4847", {"start": v(-70.4, 60.3) * mm, "end": v(-70.33, 60.19) * mm});
            skLineSegment(sketch, "E4848", {"start": v(-70.33, 60.19) * mm, "end": v(-70.25, 60.07) * mm});
            skLineSegment(sketch, "E4849", {"start": v(-70.25, 60.07) * mm, "end": v(-70.18, 59.95) * mm});
            skLineSegment(sketch, "E4850", {"start": v(-70.18, 59.95) * mm, "end": v(-70.1, 59.84) * mm});
            skLineSegment(sketch, "E4851", {"start": v(-70.1, 59.84) * mm, "end": v(-70.03, 59.73) * mm});
            skLineSegment(sketch, "E4852", {"start": v(-70.03, 59.73) * mm, "end": v(-69.96, 59.62) * mm});
            skLineSegment(sketch, "E4853", {"start": v(-69.96, 59.62) * mm, "end": v(-69.88, 59.51) * mm});
            skLineSegment(sketch, "E4854", {"start": v(-69.88, 59.51) * mm, "end": v(-69.81, 59.41) * mm});
            skLineSegment(sketch, "E4855", {"start": v(-69.81, 59.41) * mm, "end": v(-69.74, 59.3) * mm});
            skLineSegment(sketch, "E4856", {"start": v(-69.74, 59.3) * mm, "end": v(-69.67, 59.21) * mm});
            skLineSegment(sketch, "E4857", {"start": v(-69.67, 59.21) * mm, "end": v(-69.6, 59.11) * mm});
            skLineSegment(sketch, "E4858", {"start": v(-69.6, 59.11) * mm, "end": v(-69.54, 59.02) * mm});
            skLineSegment(sketch, "E4859", {"start": v(-69.54, 59.02) * mm, "end": v(-69.65, 58.56) * mm});
            skLineSegment(sketch, "E4860", {"start": v(-69.65, 58.56) * mm, "end": v(-70.73, 57.26) * mm});
            skLineSegment(sketch, "E4861", {"start": v(-70.73, 57.26) * mm, "end": v(-71.16, 57.05) * mm});
            skLineSegment(sketch, "E4862", {"start": v(-71.16, 57.05) * mm, "end": v(-71.26, 57.1) * mm});
            skLineSegment(sketch, "E4863", {"start": v(-71.26, 57.1) * mm, "end": v(-71.37, 57.15) * mm});
            skLineSegment(sketch, "E4864", {"start": v(-71.37, 57.15) * mm, "end": v(-71.48, 57.2) * mm});
            skLineSegment(sketch, "E4865", {"start": v(-71.48, 57.2) * mm, "end": v(-71.6, 57.25) * mm});
            skLineSegment(sketch, "E4866", {"start": v(-71.6, 57.25) * mm, "end": v(-71.7, 57.3) * mm});
            skLineSegment(sketch, "E4867", {"start": v(-71.7, 57.3) * mm, "end": v(-71.83, 57.35) * mm});
            skLineSegment(sketch, "E4868", {"start": v(-71.83, 57.35) * mm, "end": v(-71.95, 57.4) * mm});
            skLineSegment(sketch, "E4869", {"start": v(-71.95, 57.4) * mm, "end": v(-72.07, 57.46) * mm});
            skLineSegment(sketch, "E4870", {"start": v(-72.07, 57.46) * mm, "end": v(-72.2, 57.5) * mm});
            skLineSegment(sketch, "E4871", {"start": v(-72.2, 57.5) * mm, "end": v(-72.32, 57.56) * mm});
            skLineSegment(sketch, "E4872", {"start": v(-72.32, 57.56) * mm, "end": v(-72.45, 57.61) * mm});
            skLineSegment(sketch, "E4873", {"start": v(-72.45, 57.61) * mm, "end": v(-72.58, 57.66) * mm});
            skLineSegment(sketch, "E4874", {"start": v(-72.58, 57.66) * mm, "end": v(-72.72, 57.72) * mm});
            skLineSegment(sketch, "E4875", {"start": v(-72.72, 57.72) * mm, "end": v(-72.86, 57.77) * mm});
            skLineSegment(sketch, "E4876", {"start": v(-72.86, 57.77) * mm, "end": v(-73, 57.82) * mm});
            skLineSegment(sketch, "E4877", {"start": v(-73, 57.82) * mm, "end": v(-73.14, 57.88) * mm});
            skLineSegment(sketch, "E4878", {"start": v(-73.14, 57.88) * mm, "end": v(-73.29, 57.93) * mm});
            skLineSegment(sketch, "E4879", {"start": v(-73.29, 57.93) * mm, "end": v(-73.44, 57.98) * mm});
            skLineSegment(sketch, "E4880", {"start": v(-73.44, 57.98) * mm, "end": v(-73.59, 58.03) * mm});
            skLineSegment(sketch, "E4881", {"start": v(-73.59, 58.03) * mm, "end": v(-73.74, 58.09) * mm});
            skLineSegment(sketch, "E4882", {"start": v(-73.74, 58.09) * mm, "end": v(-73.9, 58.14) * mm});
            skLineSegment(sketch, "E4883", {"start": v(-73.9, 58.14) * mm, "end": v(-74.06, 58.2) * mm});
            skLineSegment(sketch, "E4884", {"start": v(-74.06, 58.2) * mm, "end": v(-74.22, 58.25) * mm});
            skLineSegment(sketch, "E4885", {"start": v(-74.22, 58.25) * mm, "end": v(-74.38, 58.3) * mm});
            skLineSegment(sketch, "E4886", {"start": v(-74.38, 58.3) * mm, "end": v(-74.55, 58.35) * mm});
            skLineSegment(sketch, "E4887", {"start": v(-74.55, 58.35) * mm, "end": v(-74.72, 58.4) * mm});
            skLineSegment(sketch, "E4888", {"start": v(-74.72, 58.4) * mm, "end": v(-74.9, 58.46) * mm});
            skLineSegment(sketch, "E4889", {"start": v(-74.9, 58.46) * mm, "end": v(-75.07, 58.51) * mm});
            skLineSegment(sketch, "E4890", {"start": v(-75.07, 58.51) * mm, "end": v(-75.25, 58.56) * mm});
            skLineSegment(sketch, "E4891", {"start": v(-75.25, 58.56) * mm, "end": v(-75.43, 58.61) * mm});
            skLineSegment(sketch, "E4892", {"start": v(-75.43, 58.61) * mm, "end": v(-75.6, 58.67) * mm});
            skLineSegment(sketch, "E4893", {"start": v(-75.6, 58.67) * mm, "end": v(-75.8, 58.72) * mm});
            skLineSegment(sketch, "E4894", {"start": v(-75.8, 58.72) * mm, "end": v(-75.98, 58.77) * mm});
            skLineSegment(sketch, "E4895", {"start": v(-75.98, 58.77) * mm, "end": v(-76.17, 58.82) * mm});
            skLineSegment(sketch, "E4896", {"start": v(-76.17, 58.82) * mm, "end": v(-76.37, 58.87) * mm});
            skLineSegment(sketch, "E4897", {"start": v(-76.37, 58.87) * mm, "end": v(-76.56, 58.92) * mm});
            skLineSegment(sketch, "E4898", {"start": v(-76.56, 58.92) * mm, "end": v(-76.76, 58.97) * mm});
            skLineSegment(sketch, "E4899", {"start": v(-76.76, 58.97) * mm, "end": v(-76.96, 59.02) * mm});
            skLineSegment(sketch, "E4900", {"start": v(-76.96, 59.02) * mm, "end": v(-77.14, 59.04) * mm});
            skLineSegment(sketch, "E4901", {"start": v(-77.14, 59.04) * mm, "end": v(-78.43, 57.32) * mm});
            skLineSegment(sketch, "E4902", {"start": v(-78.43, 57.32) * mm, "end": v(-78.35, 57.16) * mm});
            skLineSegment(sketch, "E4903", {"start": v(-78.35, 57.16) * mm, "end": v(-78.25, 56.98) * mm});
            skLineSegment(sketch, "E4904", {"start": v(-78.25, 56.98) * mm, "end": v(-78.15, 56.8) * mm});
            skLineSegment(sketch, "E4905", {"start": v(-78.15, 56.8) * mm, "end": v(-78.04, 56.63) * mm});
            skLineSegment(sketch, "E4906", {"start": v(-78.04, 56.63) * mm, "end": v(-77.94, 56.46) * mm});
            skLineSegment(sketch, "E4907", {"start": v(-77.94, 56.46) * mm, "end": v(-77.84, 56.29) * mm});
            skLineSegment(sketch, "E4908", {"start": v(-77.84, 56.29) * mm, "end": v(-77.74, 56.12) * mm});
            skLineSegment(sketch, "E4909", {"start": v(-77.74, 56.12) * mm, "end": v(-77.63, 55.96) * mm});
            skLineSegment(sketch, "E4910", {"start": v(-77.63, 55.96) * mm, "end": v(-77.53, 55.8) * mm});
            skLineSegment(sketch, "E4911", {"start": v(-77.53, 55.8) * mm, "end": v(-77.43, 55.64) * mm});
            skLineSegment(sketch, "E4912", {"start": v(-77.43, 55.64) * mm, "end": v(-77.33, 55.48) * mm});
            skLineSegment(sketch, "E4913", {"start": v(-77.33, 55.48) * mm, "end": v(-77.23, 55.33) * mm});
            skLineSegment(sketch, "E4914", {"start": v(-77.23, 55.33) * mm, "end": v(-77.13, 55.18) * mm});
            skLineSegment(sketch, "E4915", {"start": v(-77.13, 55.18) * mm, "end": v(-77.04, 55.03) * mm});
            skLineSegment(sketch, "E4916", {"start": v(-77.04, 55.03) * mm, "end": v(-76.94, 54.89) * mm});
            skLineSegment(sketch, "E4917", {"start": v(-76.94, 54.89) * mm, "end": v(-76.84, 54.74) * mm});
            skLineSegment(sketch, "E4918", {"start": v(-76.84, 54.74) * mm, "end": v(-76.74, 54.6) * mm});
            skLineSegment(sketch, "E4919", {"start": v(-76.74, 54.6) * mm, "end": v(-76.65, 54.47) * mm});
            skLineSegment(sketch, "E4920", {"start": v(-76.65, 54.47) * mm, "end": v(-76.55, 54.33) * mm});
            skLineSegment(sketch, "E4921", {"start": v(-76.55, 54.33) * mm, "end": v(-76.46, 54.2) * mm});
            skLineSegment(sketch, "E4922", {"start": v(-76.46, 54.2) * mm, "end": v(-76.36, 54.07) * mm});
            skLineSegment(sketch, "E4923", {"start": v(-76.36, 54.07) * mm, "end": v(-76.27, 53.94) * mm});
            skLineSegment(sketch, "E4924", {"start": v(-76.27, 53.94) * mm, "end": v(-76.18, 53.82) * mm});
            skLineSegment(sketch, "E4925", {"start": v(-76.18, 53.82) * mm, "end": v(-76.09, 53.7) * mm});
            skLineSegment(sketch, "E4926", {"start": v(-76.09, 53.7) * mm, "end": v(-76, 53.57) * mm});
            skLineSegment(sketch, "E4927", {"start": v(-76, 53.57) * mm, "end": v(-75.9, 53.46) * mm});
            skLineSegment(sketch, "E4928", {"start": v(-75.9, 53.46) * mm, "end": v(-75.82, 53.34) * mm});
            skLineSegment(sketch, "E4929", {"start": v(-75.82, 53.34) * mm, "end": v(-75.73, 53.23) * mm});
            skLineSegment(sketch, "E4930", {"start": v(-75.73, 53.23) * mm, "end": v(-75.64, 53.12) * mm});
            skLineSegment(sketch, "E4931", {"start": v(-75.64, 53.12) * mm, "end": v(-75.56, 53) * mm});
            skLineSegment(sketch, "E4932", {"start": v(-75.56, 53) * mm, "end": v(-75.47, 52.9) * mm});
            skLineSegment(sketch, "E4933", {"start": v(-75.47, 52.9) * mm, "end": v(-75.39, 52.8) * mm});
            skLineSegment(sketch, "E4934", {"start": v(-75.39, 52.8) * mm, "end": v(-75.3, 52.7) * mm});
            skLineSegment(sketch, "E4935", {"start": v(-75.3, 52.7) * mm, "end": v(-75.22, 52.6) * mm});
            skLineSegment(sketch, "E4936", {"start": v(-75.22, 52.6) * mm, "end": v(-75.14, 52.5) * mm});
            skLineSegment(sketch, "E4937", {"start": v(-75.14, 52.5) * mm, "end": v(-75.06, 52.41) * mm});
            skLineSegment(sketch, "E4938", {"start": v(-75.06, 52.41) * mm, "end": v(-74.98, 52.32) * mm});
            skLineSegment(sketch, "E4939", {"start": v(-74.98, 52.32) * mm, "end": v(-74.9, 52.23) * mm});
            skLineSegment(sketch, "E4940", {"start": v(-74.9, 52.23) * mm, "end": v(-74.83, 52.14) * mm});
            skLineSegment(sketch, "E4941", {"start": v(-74.83, 52.14) * mm, "end": v(-74.9, 51.67) * mm});
            skLineSegment(sketch, "E4942", {"start": v(-74.9, 51.67) * mm, "end": v(-75.85, 50.28) * mm});
            skLineSegment(sketch, "E4943", {"start": v(-75.85, 50.28) * mm, "end": v(-76.26, 50.03) * mm});
            skLineSegment(sketch, "E4944", {"start": v(-76.26, 50.03) * mm, "end": v(-76.37, 50.07) * mm});
            skLineSegment(sketch, "E4945", {"start": v(-76.37, 50.07) * mm, "end": v(-76.48, 50.1) * mm});
            skLineSegment(sketch, "E4946", {"start": v(-76.48, 50.1) * mm, "end": v(-76.6, 50.15) * mm});
            skLineSegment(sketch, "E4947", {"start": v(-76.6, 50.15) * mm, "end": v(-76.71, 50.19) * mm});
            skLineSegment(sketch, "E4948", {"start": v(-76.71, 50.19) * mm, "end": v(-76.83, 50.23) * mm});
            skLineSegment(sketch, "E4949", {"start": v(-76.83, 50.23) * mm, "end": v(-76.95, 50.27) * mm});
            skLineSegment(sketch, "E4950", {"start": v(-76.95, 50.27) * mm, "end": v(-77.08, 50.3) * mm});
            skLineSegment(sketch, "E4951", {"start": v(-77.08, 50.3) * mm, "end": v(-77.2, 50.34) * mm});
            skLineSegment(sketch, "E4952", {"start": v(-77.2, 50.34) * mm, "end": v(-77.33, 50.38) * mm});
            skLineSegment(sketch, "E4953", {"start": v(-77.33, 50.38) * mm, "end": v(-77.47, 50.42) * mm});
            skLineSegment(sketch, "E4954", {"start": v(-77.47, 50.42) * mm, "end": v(-77.6, 50.46) * mm});
            skLineSegment(sketch, "E4955", {"start": v(-77.6, 50.46) * mm, "end": v(-77.74, 50.5) * mm});
            skLineSegment(sketch, "E4956", {"start": v(-77.74, 50.5) * mm, "end": v(-77.88, 50.54) * mm});
            skLineSegment(sketch, "E4957", {"start": v(-77.88, 50.54) * mm, "end": v(-78.02, 50.58) * mm});
            skLineSegment(sketch, "E4958", {"start": v(-78.02, 50.58) * mm, "end": v(-78.17, 50.62) * mm});
            skLineSegment(sketch, "E4959", {"start": v(-78.17, 50.62) * mm, "end": v(-78.31, 50.66) * mm});
            skLineSegment(sketch, "E4960", {"start": v(-78.31, 50.66) * mm, "end": v(-78.46, 50.7) * mm});
            skLineSegment(sketch, "E4961", {"start": v(-78.46, 50.7) * mm, "end": v(-78.62, 50.74) * mm});
            skLineSegment(sketch, "E4962", {"start": v(-78.62, 50.74) * mm, "end": v(-78.77, 50.78) * mm});
            skLineSegment(sketch, "E4963", {"start": v(-78.77, 50.78) * mm, "end": v(-78.93, 50.82) * mm});
            skLineSegment(sketch, "E4964", {"start": v(-78.93, 50.82) * mm, "end": v(-79.1, 50.85) * mm});
            skLineSegment(sketch, "E4965", {"start": v(-79.1, 50.85) * mm, "end": v(-79.25, 50.9) * mm});
            skLineSegment(sketch, "E4966", {"start": v(-79.25, 50.9) * mm, "end": v(-79.42, 50.93) * mm});
            skLineSegment(sketch, "E4967", {"start": v(-79.42, 50.93) * mm, "end": v(-79.59, 50.97) * mm});
            skLineSegment(sketch, "E4968", {"start": v(-79.59, 50.97) * mm, "end": v(-79.76, 51) * mm});
            skLineSegment(sketch, "E4969", {"start": v(-79.76, 51) * mm, "end": v(-79.93, 51.04) * mm});
            skLineSegment(sketch, "E4970", {"start": v(-79.93, 51.04) * mm, "end": v(-80.11, 51.07) * mm});
            skLineSegment(sketch, "E4971", {"start": v(-80.11, 51.07) * mm, "end": v(-80.3, 51.11) * mm});
            skLineSegment(sketch, "E4972", {"start": v(-80.3, 51.11) * mm, "end": v(-80.47, 51.15) * mm});
            skLineSegment(sketch, "E4973", {"start": v(-80.47, 51.15) * mm, "end": v(-80.66, 51.18) * mm});
            skLineSegment(sketch, "E4974", {"start": v(-80.66, 51.18) * mm, "end": v(-80.84, 51.21) * mm});
            skLineSegment(sketch, "E4975", {"start": v(-80.84, 51.21) * mm, "end": v(-81.03, 51.25) * mm});
            skLineSegment(sketch, "E4976", {"start": v(-81.03, 51.25) * mm, "end": v(-81.23, 51.28) * mm});
            skLineSegment(sketch, "E4977", {"start": v(-81.23, 51.28) * mm, "end": v(-81.42, 51.31) * mm});
            skLineSegment(sketch, "E4978", {"start": v(-81.42, 51.31) * mm, "end": v(-81.62, 51.34) * mm});
            skLineSegment(sketch, "E4979", {"start": v(-81.62, 51.34) * mm, "end": v(-81.82, 51.37) * mm});
            skLineSegment(sketch, "E4980", {"start": v(-81.82, 51.37) * mm, "end": v(-82.02, 51.4) * mm});
            skLineSegment(sketch, "E4981", {"start": v(-82.02, 51.4) * mm, "end": v(-82.23, 51.43) * mm});
            skLineSegment(sketch, "E4982", {"start": v(-82.23, 51.43) * mm, "end": v(-82.4, 51.44) * mm});
            skLineSegment(sketch, "E4983", {"start": v(-82.4, 51.44) * mm, "end": v(-83.52, 49.6) * mm});
            skLineSegment(sketch, "E4984", {"start": v(-83.52, 49.6) * mm, "end": v(-83.43, 49.45) * mm});
            skLineSegment(sketch, "E4985", {"start": v(-83.43, 49.45) * mm, "end": v(-83.31, 49.28) * mm});
            skLineSegment(sketch, "E4986", {"start": v(-83.31, 49.28) * mm, "end": v(-83.2, 49.12) * mm});
            skLineSegment(sketch, "E4987", {"start": v(-83.2, 49.12) * mm, "end": v(-83.07, 48.95) * mm});
            skLineSegment(sketch, "E4988", {"start": v(-83.07, 48.95) * mm, "end": v(-82.95, 48.8) * mm});
            skLineSegment(sketch, "E4989", {"start": v(-82.95, 48.8) * mm, "end": v(-82.84, 48.64) * mm});
            skLineSegment(sketch, "E4990", {"start": v(-82.84, 48.64) * mm, "end": v(-82.72, 48.48) * mm});
            skLineSegment(sketch, "E4991", {"start": v(-82.72, 48.48) * mm, "end": v(-82.6, 48.33) * mm});
            skLineSegment(sketch, "E4992", {"start": v(-82.6, 48.33) * mm, "end": v(-82.49, 48.18) * mm});
            skLineSegment(sketch, "E4993", {"start": v(-82.49, 48.18) * mm, "end": v(-82.37, 48.03) * mm});
            skLineSegment(sketch, "E4994", {"start": v(-82.37, 48.03) * mm, "end": v(-82.26, 47.88) * mm});
            skLineSegment(sketch, "E4995", {"start": v(-82.26, 47.88) * mm, "end": v(-82.14, 47.74) * mm});
            skLineSegment(sketch, "E4996", {"start": v(-82.14, 47.74) * mm, "end": v(-82.03, 47.6) * mm});
            skLineSegment(sketch, "E4997", {"start": v(-82.03, 47.6) * mm, "end": v(-81.92, 47.46) * mm});
            skLineSegment(sketch, "E4998", {"start": v(-81.92, 47.46) * mm, "end": v(-81.8, 47.33) * mm});
            skLineSegment(sketch, "E4999", {"start": v(-81.8, 47.33) * mm, "end": v(-81.7, 47.2) * mm});
            skLineSegment(sketch, "E5000", {"start": v(-81.7, 47.2) * mm, "end": v(-81.59, 47.06) * mm});
            skLineSegment(sketch, "E5001", {"start": v(-81.59, 47.06) * mm, "end": v(-81.48, 46.93) * mm});
            skLineSegment(sketch, "E5002", {"start": v(-81.48, 46.93) * mm, "end": v(-81.37, 46.8) * mm});
            skLineSegment(sketch, "E5003", {"start": v(-81.37, 46.8) * mm, "end": v(-81.26, 46.69) * mm});
            skLineSegment(sketch, "E5004", {"start": v(-81.26, 46.69) * mm, "end": v(-81.16, 46.57) * mm});
            skLineSegment(sketch, "E5005", {"start": v(-81.16, 46.57) * mm, "end": v(-81.05, 46.45) * mm});
            skLineSegment(sketch, "E5006", {"start": v(-81.05, 46.45) * mm, "end": v(-80.95, 46.33) * mm});
            skLineSegment(sketch, "E5007", {"start": v(-80.95, 46.33) * mm, "end": v(-80.85, 46.22) * mm});
            skLineSegment(sketch, "E5008", {"start": v(-80.85, 46.22) * mm, "end": v(-80.75, 46.1) * mm});
            skLineSegment(sketch, "E5009", {"start": v(-80.75, 46.1) * mm, "end": v(-80.64, 46) * mm});
            skLineSegment(sketch, "E5010", {"start": v(-80.64, 46) * mm, "end": v(-80.55, 45.9) * mm});
            skLineSegment(sketch, "E5011", {"start": v(-80.55, 45.9) * mm, "end": v(-80.45, 45.79) * mm});
            skLineSegment(sketch, "E5012", {"start": v(-80.45, 45.79) * mm, "end": v(-80.35, 45.69) * mm});
            skLineSegment(sketch, "E5013", {"start": v(-80.35, 45.69) * mm, "end": v(-80.25, 45.59) * mm});
            skLineSegment(sketch, "E5014", {"start": v(-80.25, 45.59) * mm, "end": v(-80.16, 45.5) * mm});
            skLineSegment(sketch, "E5015", {"start": v(-80.16, 45.5) * mm, "end": v(-80.07, 45.4) * mm});
            skLineSegment(sketch, "E5016", {"start": v(-80.07, 45.4) * mm, "end": v(-79.97, 45.3) * mm});
            skLineSegment(sketch, "E5017", {"start": v(-79.97, 45.3) * mm, "end": v(-79.88, 45.21) * mm});
            skLineSegment(sketch, "E5018", {"start": v(-79.88, 45.21) * mm, "end": v(-79.8, 45.12) * mm});
            skLineSegment(sketch, "E5019", {"start": v(-79.8, 45.12) * mm, "end": v(-79.7, 45.04) * mm});
            skLineSegment(sketch, "E5020", {"start": v(-79.7, 45.04) * mm, "end": v(-79.62, 44.96) * mm});
            skLineSegment(sketch, "E5021", {"start": v(-79.62, 44.96) * mm, "end": v(-79.53, 44.87) * mm});
            skLineSegment(sketch, "E5022", {"start": v(-79.53, 44.87) * mm, "end": v(-79.45, 44.8) * mm});
            skLineSegment(sketch, "E5023", {"start": v(-79.45, 44.8) * mm, "end": v(-79.48, 44.32) * mm});
            skLineSegment(sketch, "E5024", {"start": v(-79.48, 44.32) * mm, "end": v(-80.29, 42.84) * mm});
            skLineSegment(sketch, "E5025", {"start": v(-80.29, 42.84) * mm, "end": v(-80.67, 42.56) * mm});
            skLineSegment(sketch, "E5026", {"start": v(-80.67, 42.56) * mm, "end": v(-80.78, 42.58) * mm});
            skLineSegment(sketch, "E5027", {"start": v(-80.78, 42.58) * mm, "end": v(-80.9, 42.61) * mm});
            skLineSegment(sketch, "E5028", {"start": v(-80.9, 42.61) * mm, "end": v(-81.01, 42.64) * mm});
            skLineSegment(sketch, "E5029", {"start": v(-81.01, 42.64) * mm, "end": v(-81.13, 42.67) * mm});
            skLineSegment(sketch, "E5030", {"start": v(-81.13, 42.67) * mm, "end": v(-81.26, 42.7) * mm});
            skLineSegment(sketch, "E5031", {"start": v(-81.26, 42.7) * mm, "end": v(-81.38, 42.72) * mm});
            skLineSegment(sketch, "E5032", {"start": v(-81.38, 42.72) * mm, "end": v(-81.5, 42.75) * mm});
            skLineSegment(sketch, "E5033", {"start": v(-81.5, 42.75) * mm, "end": v(-81.64, 42.78) * mm});
            skLineSegment(sketch, "E5034", {"start": v(-81.64, 42.78) * mm, "end": v(-81.77, 42.8) * mm});
            skLineSegment(sketch, "E5035", {"start": v(-81.77, 42.8) * mm, "end": v(-81.9, 42.83) * mm});
            skLineSegment(sketch, "E5036", {"start": v(-81.9, 42.83) * mm, "end": v(-82.05, 42.86) * mm});
            skLineSegment(sketch, "E5037", {"start": v(-82.05, 42.86) * mm, "end": v(-82.19, 42.88) * mm});
            skLineSegment(sketch, "E5038", {"start": v(-82.19, 42.88) * mm, "end": v(-82.33, 42.91) * mm});
            skLineSegment(sketch, "E5039", {"start": v(-82.33, 42.91) * mm, "end": v(-82.47, 42.94) * mm});
            skLineSegment(sketch, "E5040", {"start": v(-82.47, 42.94) * mm, "end": v(-82.62, 42.96) * mm});
            skLineSegment(sketch, "E5041", {"start": v(-82.62, 42.96) * mm, "end": v(-82.77, 42.99) * mm});
            skLineSegment(sketch, "E5042", {"start": v(-82.77, 42.99) * mm, "end": v(-82.93, 43.01) * mm});
            skLineSegment(sketch, "E5043", {"start": v(-82.93, 43.01) * mm, "end": v(-83.08, 43.04) * mm});
            skLineSegment(sketch, "E5044", {"start": v(-83.08, 43.04) * mm, "end": v(-83.24, 43.06) * mm});
            skLineSegment(sketch, "E5045", {"start": v(-83.24, 43.06) * mm, "end": v(-83.4, 43.08) * mm});
            skLineSegment(sketch, "E5046", {"start": v(-83.4, 43.08) * mm, "end": v(-83.57, 43.1) * mm});
            skLineSegment(sketch, "E5047", {"start": v(-83.57, 43.1) * mm, "end": v(-83.73, 43.13) * mm});
            skLineSegment(sketch, "E5048", {"start": v(-83.73, 43.13) * mm, "end": v(-83.9, 43.15) * mm});
            skLineSegment(sketch, "E5049", {"start": v(-83.9, 43.15) * mm, "end": v(-84.07, 43.17) * mm});
            skLineSegment(sketch, "E5050", {"start": v(-84.07, 43.17) * mm, "end": v(-84.25, 43.19) * mm});
            skLineSegment(sketch, "E5051", {"start": v(-84.25, 43.19) * mm, "end": v(-84.42, 43.2) * mm});
            skLineSegment(sketch, "E5052", {"start": v(-84.42, 43.2) * mm, "end": v(-84.6, 43.23) * mm});
            skLineSegment(sketch, "E5053", {"start": v(-84.6, 43.23) * mm, "end": v(-84.79, 43.25) * mm});
            skLineSegment(sketch, "E5054", {"start": v(-84.79, 43.25) * mm, "end": v(-84.97, 43.26) * mm});
            skLineSegment(sketch, "E5055", {"start": v(-84.97, 43.26) * mm, "end": v(-85.16, 43.28) * mm});
            skLineSegment(sketch, "E5056", {"start": v(-85.16, 43.28) * mm, "end": v(-85.35, 43.3) * mm});
            skLineSegment(sketch, "E5057", {"start": v(-85.35, 43.3) * mm, "end": v(-85.54, 43.31) * mm});
            skLineSegment(sketch, "E5058", {"start": v(-85.54, 43.31) * mm, "end": v(-85.73, 43.33) * mm});
            skLineSegment(sketch, "E5059", {"start": v(-85.73, 43.33) * mm, "end": v(-85.93, 43.34) * mm});
            skLineSegment(sketch, "E5060", {"start": v(-85.93, 43.34) * mm, "end": v(-86.13, 43.35) * mm});
            skLineSegment(sketch, "E5061", {"start": v(-86.13, 43.35) * mm, "end": v(-86.33, 43.36) * mm});
            skLineSegment(sketch, "E5062", {"start": v(-86.33, 43.36) * mm, "end": v(-86.54, 43.38) * mm});
            skLineSegment(sketch, "E5063", {"start": v(-86.54, 43.38) * mm, "end": v(-86.74, 43.39) * mm});
            skLineSegment(sketch, "E5064", {"start": v(-86.74, 43.39) * mm, "end": v(-86.92, 43.38) * mm});
            skLineSegment(sketch, "E5065", {"start": v(-86.92, 43.38) * mm, "end": v(-87.86, 41.44) * mm});
            skLineSegment(sketch, "E5066", {"start": v(-87.86, 41.44) * mm, "end": v(-87.76, 41.3) * mm});
            skLineSegment(sketch, "E5067", {"start": v(-87.76, 41.3) * mm, "end": v(-87.62, 41.14) * mm});
            skLineSegment(sketch, "E5068", {"start": v(-87.62, 41.14) * mm, "end": v(-87.48, 40.99) * mm});
            skLineSegment(sketch, "E5069", {"start": v(-87.48, 40.99) * mm, "end": v(-87.35, 40.84) * mm});
            skLineSegment(sketch, "E5070", {"start": v(-87.35, 40.84) * mm, "end": v(-87.22, 40.69) * mm});
            skLineSegment(sketch, "E5071", {"start": v(-87.22, 40.69) * mm, "end": v(-87.08, 40.54) * mm});
            skLineSegment(sketch, "E5072", {"start": v(-87.08, 40.54) * mm, "end": v(-86.95, 40.4) * mm});
            skLineSegment(sketch, "E5073", {"start": v(-86.95, 40.4) * mm, "end": v(-86.82, 40.26) * mm});
            skLineSegment(sketch, "E5074", {"start": v(-86.82, 40.26) * mm, "end": v(-86.7, 40.12) * mm});
            skLineSegment(sketch, "E5075", {"start": v(-86.7, 40.12) * mm, "end": v(-86.56, 39.98) * mm});
            skLineSegment(sketch, "E5076", {"start": v(-86.56, 39.98) * mm, "end": v(-86.44, 39.85) * mm});
            skLineSegment(sketch, "E5077", {"start": v(-86.44, 39.85) * mm, "end": v(-86.3, 39.71) * mm});
            skLineSegment(sketch, "E5078", {"start": v(-86.3, 39.71) * mm, "end": v(-86.18, 39.59) * mm});
            skLineSegment(sketch, "E5079", {"start": v(-86.18, 39.59) * mm, "end": v(-86.06, 39.46) * mm});
            skLineSegment(sketch, "E5080", {"start": v(-86.06, 39.46) * mm, "end": v(-85.93, 39.34) * mm});
            skLineSegment(sketch, "E5081", {"start": v(-85.93, 39.34) * mm, "end": v(-85.81, 39.21) * mm});
            skLineSegment(sketch, "E5082", {"start": v(-85.81, 39.21) * mm, "end": v(-85.7, 39.1) * mm});
            skLineSegment(sketch, "E5083", {"start": v(-85.7, 39.1) * mm, "end": v(-85.57, 38.98) * mm});
            skLineSegment(sketch, "E5084", {"start": v(-85.57, 38.98) * mm, "end": v(-85.45, 38.86) * mm});
            skLineSegment(sketch, "E5085", {"start": v(-85.45, 38.86) * mm, "end": v(-85.33, 38.75) * mm});
            skLineSegment(sketch, "E5086", {"start": v(-85.33, 38.75) * mm, "end": v(-85.22, 38.64) * mm});
            skLineSegment(sketch, "E5087", {"start": v(-85.22, 38.64) * mm, "end": v(-85.1, 38.53) * mm});
            skLineSegment(sketch, "E5088", {"start": v(-85.1, 38.53) * mm, "end": v(-84.99, 38.43) * mm});
            skLineSegment(sketch, "E5089", {"start": v(-84.99, 38.43) * mm, "end": v(-84.87, 38.32) * mm});
            skLineSegment(sketch, "E5090", {"start": v(-84.87, 38.32) * mm, "end": v(-84.76, 38.22) * mm});
            skLineSegment(sketch, "E5091", {"start": v(-84.76, 38.22) * mm, "end": v(-84.65, 38.12) * mm});
            skLineSegment(sketch, "E5092", {"start": v(-84.65, 38.12) * mm, "end": v(-84.54, 38.03) * mm});
            skLineSegment(sketch, "E5093", {"start": v(-84.54, 38.03) * mm, "end": v(-84.44, 37.93) * mm});
            skLineSegment(sketch, "E5094", {"start": v(-84.44, 37.93) * mm, "end": v(-84.33, 37.84) * mm});
            skLineSegment(sketch, "E5095", {"start": v(-84.33, 37.84) * mm, "end": v(-84.22, 37.75) * mm});
            skLineSegment(sketch, "E5096", {"start": v(-84.22, 37.75) * mm, "end": v(-84.12, 37.66) * mm});
            skLineSegment(sketch, "E5097", {"start": v(-84.12, 37.66) * mm, "end": v(-84.02, 37.58) * mm});
            skLineSegment(sketch, "E5098", {"start": v(-84.02, 37.58) * mm, "end": v(-83.92, 37.5) * mm});
            skLineSegment(sketch, "E5099", {"start": v(-83.92, 37.5) * mm, "end": v(-83.82, 37.41) * mm});
            skLineSegment(sketch, "E5100", {"start": v(-83.82, 37.41) * mm, "end": v(-83.72, 37.34) * mm});
            skLineSegment(sketch, "E5101", {"start": v(-83.72, 37.34) * mm, "end": v(-83.63, 37.26) * mm});
            skLineSegment(sketch, "E5102", {"start": v(-83.63, 37.26) * mm, "end": v(-83.53, 37.18) * mm});
            skLineSegment(sketch, "E5103", {"start": v(-83.53, 37.18) * mm, "end": v(-83.44, 37.11) * mm});
            skLineSegment(sketch, "E5104", {"start": v(-83.44, 37.11) * mm, "end": v(-83.35, 37.04) * mm});
            skLineSegment(sketch, "E5105", {"start": v(-83.35, 37.04) * mm, "end": v(-83.33, 36.56) * mm});
            skLineSegment(sketch, "E5106", {"start": v(-83.33, 36.56) * mm, "end": v(-84, 35.01) * mm});
            skLineSegment(sketch, "E5107", {"start": v(-84, 35.01) * mm, "end": v(-84.35, 34.7) * mm});
            skLineSegment(sketch, "E5108", {"start": v(-84.35, 34.7) * mm, "end": v(-84.46, 34.71) * mm});
            skLineSegment(sketch, "E5109", {"start": v(-84.46, 34.71) * mm, "end": v(-84.58, 34.73) * mm});
            skLineSegment(sketch, "E5110", {"start": v(-84.58, 34.73) * mm, "end": v(-84.7, 34.75) * mm});
            skLineSegment(sketch, "E5111", {"start": v(-84.7, 34.75) * mm, "end": v(-84.82, 34.76) * mm});
            skLineSegment(sketch, "E5112", {"start": v(-84.82, 34.76) * mm, "end": v(-84.95, 34.78) * mm});
            skLineSegment(sketch, "E5113", {"start": v(-84.95, 34.78) * mm, "end": v(-85.07, 34.8) * mm});
            skLineSegment(sketch, "E5114", {"start": v(-85.07, 34.8) * mm, "end": v(-85.2, 34.8) * mm});
            skLineSegment(sketch, "E5115", {"start": v(-85.2, 34.8) * mm, "end": v(-85.34, 34.82) * mm});
            skLineSegment(sketch, "E5116", {"start": v(-85.34, 34.82) * mm, "end": v(-85.47, 34.84) * mm});
            skLineSegment(sketch, "E5117", {"start": v(-85.47, 34.84) * mm, "end": v(-85.6, 34.85) * mm});
            skLineSegment(sketch, "E5118", {"start": v(-85.6, 34.85) * mm, "end": v(-85.75, 34.87) * mm});
            skLineSegment(sketch, "E5119", {"start": v(-85.75, 34.87) * mm, "end": v(-85.9, 34.88) * mm});
            skLineSegment(sketch, "E5120", {"start": v(-85.9, 34.88) * mm, "end": v(-86.04, 34.9) * mm});
            skLineSegment(sketch, "E5121", {"start": v(-86.04, 34.9) * mm, "end": v(-86.18, 34.9) * mm});
            skLineSegment(sketch, "E5122", {"start": v(-86.18, 34.9) * mm, "end": v(-86.33, 34.91) * mm});
            skLineSegment(sketch, "E5123", {"start": v(-86.33, 34.91) * mm, "end": v(-86.49, 34.92) * mm});
            skLineSegment(sketch, "E5124", {"start": v(-86.49, 34.92) * mm, "end": v(-86.64, 34.93) * mm});
            skLineSegment(sketch, "E5125", {"start": v(-86.64, 34.93) * mm, "end": v(-86.8, 34.94) * mm});
            skLineSegment(sketch, "E5126", {"start": v(-86.8, 34.94) * mm, "end": v(-86.96, 34.95) * mm});
            skLineSegment(sketch, "E5127", {"start": v(-86.96, 34.95) * mm, "end": v(-87.12, 34.96) * mm});
            skLineSegment(sketch, "E5128", {"start": v(-87.12, 34.96) * mm, "end": v(-87.29, 34.97) * mm});
            skLineSegment(sketch, "E5129", {"start": v(-87.29, 34.97) * mm, "end": v(-87.45, 34.97) * mm});
            skLineSegment(sketch, "E5130", {"start": v(-87.45, 34.97) * mm, "end": v(-87.62, 34.98) * mm});
            skLineSegment(sketch, "E5131", {"start": v(-87.62, 34.98) * mm, "end": v(-87.8, 34.98) * mm});
            skLineSegment(sketch, "E5132", {"start": v(-87.8, 34.98) * mm, "end": v(-87.97, 34.99) * mm});
            skLineSegment(sketch, "E5133", {"start": v(-87.97, 34.99) * mm, "end": v(-88.15, 34.99) * mm});
            skLineSegment(sketch, "E5134", {"start": v(-88.15, 34.99) * mm, "end": v(-88.33, 35) * mm});
            skLineSegment(sketch, "E5135", {"start": v(-88.33, 35) * mm, "end": v(-88.51, 35) * mm});
            skLineSegment(sketch, "E5136", {"start": v(-88.51, 35) * mm, "end": v(-88.7, 35) * mm});
            skLineSegment(sketch, "E5137", {"start": v(-88.7, 35) * mm, "end": v(-88.88, 35) * mm});
            skLineSegment(sketch, "E5138", {"start": v(-88.88, 35) * mm, "end": v(-89.08, 34.99) * mm});
            skLineSegment(sketch, "E5139", {"start": v(-89.08, 34.99) * mm, "end": v(-89.27, 34.99) * mm});
            skLineSegment(sketch, "E5140", {"start": v(-89.27, 34.99) * mm, "end": v(-89.46, 34.98) * mm});
            skLineSegment(sketch, "E5141", {"start": v(-89.46, 34.98) * mm, "end": v(-89.66, 34.98) * mm});
            skLineSegment(sketch, "E5142", {"start": v(-89.66, 34.98) * mm, "end": v(-89.86, 34.97) * mm});
            skLineSegment(sketch, "E5143", {"start": v(-89.86, 34.97) * mm, "end": v(-90.06, 34.96) * mm});
            skLineSegment(sketch, "E5144", {"start": v(-90.06, 34.96) * mm, "end": v(-90.27, 34.95) * mm});
            skLineSegment(sketch, "E5145", {"start": v(-90.27, 34.95) * mm, "end": v(-90.47, 34.94) * mm});
            skLineSegment(sketch, "E5146", {"start": v(-90.47, 34.94) * mm, "end": v(-90.65, 34.92) * mm});
            skLineSegment(sketch, "E5147", {"start": v(-90.65, 34.92) * mm, "end": v(-91.4, 32.9) * mm});
            skLineSegment(sketch, "E5148", {"start": v(-91.4, 32.9) * mm, "end": v(-91.28, 32.77) * mm});
            skLineSegment(sketch, "E5149", {"start": v(-91.28, 32.77) * mm, "end": v(-91.13, 32.63) * mm});
            skLineSegment(sketch, "E5150", {"start": v(-91.13, 32.63) * mm, "end": v(-90.98, 32.49) * mm});
            skLineSegment(sketch, "E5151", {"start": v(-90.98, 32.49) * mm, "end": v(-90.84, 32.35) * mm});
            skLineSegment(sketch, "E5152", {"start": v(-90.84, 32.35) * mm, "end": v(-90.69, 32.21) * mm});
            skLineSegment(sketch, "E5153", {"start": v(-90.69, 32.21) * mm, "end": v(-90.54, 32.08) * mm});
            skLineSegment(sketch, "E5154", {"start": v(-90.54, 32.08) * mm, "end": v(-90.4, 31.95) * mm});
            skLineSegment(sketch, "E5155", {"start": v(-90.4, 31.95) * mm, "end": v(-90.26, 31.82) * mm});
            skLineSegment(sketch, "E5156", {"start": v(-90.26, 31.82) * mm, "end": v(-90.11, 31.7) * mm});
            skLineSegment(sketch, "E5157", {"start": v(-90.11, 31.7) * mm, "end": v(-89.97, 31.57) * mm});
            skLineSegment(sketch, "E5158", {"start": v(-89.97, 31.57) * mm, "end": v(-89.83, 31.45) * mm});
            skLineSegment(sketch, "E5159", {"start": v(-89.83, 31.45) * mm, "end": v(-89.7, 31.33) * mm});
            skLineSegment(sketch, "E5160", {"start": v(-89.7, 31.33) * mm, "end": v(-89.56, 31.21) * mm});
            skLineSegment(sketch, "E5161", {"start": v(-89.56, 31.21) * mm, "end": v(-89.42, 31.1) * mm});
            skLineSegment(sketch, "E5162", {"start": v(-89.42, 31.1) * mm, "end": v(-89.28, 30.99) * mm});
            skLineSegment(sketch, "E5163", {"start": v(-89.28, 30.99) * mm, "end": v(-89.15, 30.88) * mm});
            skLineSegment(sketch, "E5164", {"start": v(-89.15, 30.88) * mm, "end": v(-89.02, 30.77) * mm});
            skLineSegment(sketch, "E5165", {"start": v(-89.02, 30.77) * mm, "end": v(-88.89, 30.67) * mm});
            skLineSegment(sketch, "E5166", {"start": v(-88.89, 30.67) * mm, "end": v(-88.76, 30.56) * mm});
            skLineSegment(sketch, "E5167", {"start": v(-88.76, 30.56) * mm, "end": v(-88.63, 30.46) * mm});
            skLineSegment(sketch, "E5168", {"start": v(-88.63, 30.46) * mm, "end": v(-88.5, 30.36) * mm});
            skLineSegment(sketch, "E5169", {"start": v(-88.5, 30.36) * mm, "end": v(-88.38, 30.27) * mm});
            skLineSegment(sketch, "E5170", {"start": v(-88.38, 30.27) * mm, "end": v(-88.25, 30.17) * mm});
            skLineSegment(sketch, "E5171", {"start": v(-88.25, 30.17) * mm, "end": v(-88.13, 30.08) * mm});
            skLineSegment(sketch, "E5172", {"start": v(-88.13, 30.08) * mm, "end": v(-88.01, 30) * mm});
            skLineSegment(sketch, "E5173", {"start": v(-88.01, 30) * mm, "end": v(-87.9, 29.9) * mm});
            skLineSegment(sketch, "E5174", {"start": v(-87.9, 29.9) * mm, "end": v(-87.78, 29.82) * mm});
            skLineSegment(sketch, "E5175", {"start": v(-87.78, 29.82) * mm, "end": v(-87.66, 29.74) * mm});
            skLineSegment(sketch, "E5176", {"start": v(-87.66, 29.74) * mm, "end": v(-87.54, 29.65) * mm});
            skLineSegment(sketch, "E5177", {"start": v(-87.54, 29.65) * mm, "end": v(-87.43, 29.58) * mm});
            skLineSegment(sketch, "E5178", {"start": v(-87.43, 29.58) * mm, "end": v(-87.32, 29.5) * mm});
            skLineSegment(sketch, "E5179", {"start": v(-87.32, 29.5) * mm, "end": v(-87.21, 29.42) * mm});
            skLineSegment(sketch, "E5180", {"start": v(-87.21, 29.42) * mm, "end": v(-87.1, 29.35) * mm});
            skLineSegment(sketch, "E5181", {"start": v(-87.1, 29.35) * mm, "end": v(-87, 29.28) * mm});
            skLineSegment(sketch, "E5182", {"start": v(-87, 29.28) * mm, "end": v(-86.9, 29.2) * mm});
            skLineSegment(sketch, "E5183", {"start": v(-86.9, 29.2) * mm, "end": v(-86.79, 29.14) * mm});
            skLineSegment(sketch, "E5184", {"start": v(-86.79, 29.14) * mm, "end": v(-86.69, 29.07) * mm});
            skLineSegment(sketch, "E5185", {"start": v(-86.69, 29.07) * mm, "end": v(-86.59, 29.01) * mm});
            skLineSegment(sketch, "E5186", {"start": v(-86.59, 29.01) * mm, "end": v(-86.5, 28.95) * mm});
            skLineSegment(sketch, "E5187", {"start": v(-86.5, 28.95) * mm, "end": v(-86.43, 28.48) * mm});
            skLineSegment(sketch, "E5188", {"start": v(-86.43, 28.48) * mm, "end": v(-86.94, 26.87) * mm});
            skLineSegment(sketch, "E5189", {"start": v(-86.94, 26.87) * mm, "end": v(-87.27, 26.52) * mm});
            skLineSegment(sketch, "E5190", {"start": v(-87.27, 26.52) * mm, "end": v(-87.38, 26.53) * mm});
            skLineSegment(sketch, "E5191", {"start": v(-87.38, 26.53) * mm, "end": v(-87.5, 26.53) * mm});
            skLineSegment(sketch, "E5192", {"start": v(-87.5, 26.53) * mm, "end": v(-87.62, 26.54) * mm});
            skLineSegment(sketch, "E5193", {"start": v(-87.62, 26.54) * mm, "end": v(-87.74, 26.54) * mm});
            skLineSegment(sketch, "E5194", {"start": v(-87.74, 26.54) * mm, "end": v(-87.87, 26.55) * mm});
            skLineSegment(sketch, "E5195", {"start": v(-87.87, 26.55) * mm, "end": v(-88, 26.55) * mm});
            skLineSegment(sketch, "E5196", {"start": v(-88, 26.55) * mm, "end": v(-88.13, 26.55) * mm});
            skLineSegment(sketch, "E5197", {"start": v(-88.13, 26.55) * mm, "end": v(-88.26, 26.55) * mm});
            skLineSegment(sketch, "E5198", {"start": v(-88.26, 26.55) * mm, "end": v(-88.4, 26.56) * mm});
            skLineSegment(sketch, "E5199", {"start": v(-88.4, 26.56) * mm, "end": v(-88.53, 26.56) * mm});
            skLineSegment(sketch, "E5200", {"start": v(-88.53, 26.56) * mm, "end": v(-88.67, 26.56) * mm});
            skLineSegment(sketch, "E5201", {"start": v(-88.67, 26.56) * mm, "end": v(-88.82, 26.56) * mm});
            skLineSegment(sketch, "E5202", {"start": v(-88.82, 26.56) * mm, "end": v(-88.96, 26.55) * mm});
            skLineSegment(sketch, "E5203", {"start": v(-88.96, 26.55) * mm, "end": v(-89.11, 26.55) * mm});
            skLineSegment(sketch, "E5204", {"start": v(-89.11, 26.55) * mm, "end": v(-89.26, 26.55) * mm});
            skLineSegment(sketch, "E5205", {"start": v(-89.26, 26.55) * mm, "end": v(-89.41, 26.55) * mm});
            skLineSegment(sketch, "E5206", {"start": v(-89.41, 26.55) * mm, "end": v(-89.57, 26.54) * mm});
            skLineSegment(sketch, "E5207", {"start": v(-89.57, 26.54) * mm, "end": v(-89.73, 26.53) * mm});
            skLineSegment(sketch, "E5208", {"start": v(-89.73, 26.53) * mm, "end": v(-89.89, 26.53) * mm});
            skLineSegment(sketch, "E5209", {"start": v(-89.89, 26.53) * mm, "end": v(-90.05, 26.52) * mm});
            skLineSegment(sketch, "E5210", {"start": v(-90.05, 26.52) * mm, "end": v(-90.21, 26.51) * mm});
            skLineSegment(sketch, "E5211", {"start": v(-90.21, 26.51) * mm, "end": v(-90.38, 26.5) * mm});
            skLineSegment(sketch, "E5212", {"start": v(-90.38, 26.5) * mm, "end": v(-90.55, 26.5) * mm});
            skLineSegment(sketch, "E5213", {"start": v(-90.55, 26.5) * mm, "end": v(-90.72, 26.48) * mm});
            skLineSegment(sketch, "E5214", {"start": v(-90.72, 26.48) * mm, "end": v(-90.9, 26.47) * mm});
            skLineSegment(sketch, "E5215", {"start": v(-90.9, 26.47) * mm, "end": v(-91.08, 26.45) * mm});
            skLineSegment(sketch, "E5216", {"start": v(-91.08, 26.45) * mm, "end": v(-91.26, 26.44) * mm});
            skLineSegment(sketch, "E5217", {"start": v(-91.26, 26.44) * mm, "end": v(-91.44, 26.42) * mm});
            skLineSegment(sketch, "E5218", {"start": v(-91.44, 26.42) * mm, "end": v(-91.62, 26.4) * mm});
            skLineSegment(sketch, "E5219", {"start": v(-91.62, 26.4) * mm, "end": v(-91.8, 26.38) * mm});
            skLineSegment(sketch, "E5220", {"start": v(-91.8, 26.38) * mm, "end": v(-92, 26.36) * mm});
            skLineSegment(sketch, "E5221", {"start": v(-92, 26.36) * mm, "end": v(-92.19, 26.34) * mm});
            skLineSegment(sketch, "E5222", {"start": v(-92.19, 26.34) * mm, "end": v(-92.38, 26.32) * mm});
            skLineSegment(sketch, "E5223", {"start": v(-92.38, 26.32) * mm, "end": v(-92.58, 26.3) * mm});
            skLineSegment(sketch, "E5224", {"start": v(-92.58, 26.3) * mm, "end": v(-92.78, 26.27) * mm});
            skLineSegment(sketch, "E5225", {"start": v(-92.78, 26.27) * mm, "end": v(-92.98, 26.24) * mm});
            skLineSegment(sketch, "E5226", {"start": v(-92.98, 26.24) * mm, "end": v(-93.18, 26.21) * mm});
            skLineSegment(sketch, "E5227", {"start": v(-93.18, 26.21) * mm, "end": v(-93.39, 26.19) * mm});
            skLineSegment(sketch, "E5228", {"start": v(-93.39, 26.19) * mm, "end": v(-93.56, 26.14) * mm});
            skLineSegment(sketch, "E5229", {"start": v(-93.56, 26.14) * mm, "end": v(-94.11, 24.07) * mm});
            skLineSegment(sketch, "E5230", {"start": v(-94.11, 24.07) * mm, "end": v(-93.99, 23.94) * mm});
            skLineSegment(sketch, "E5231", {"start": v(-93.99, 23.94) * mm, "end": v(-93.82, 23.82) * mm});
            skLineSegment(sketch, "E5232", {"start": v(-93.82, 23.82) * mm, "end": v(-93.66, 23.7) * mm});
            skLineSegment(sketch, "E5233", {"start": v(-93.66, 23.7) * mm, "end": v(-93.5, 23.57) * mm});
            skLineSegment(sketch, "E5234", {"start": v(-93.5, 23.57) * mm, "end": v(-93.34, 23.45) * mm});
            skLineSegment(sketch, "E5235", {"start": v(-93.34, 23.45) * mm, "end": v(-93.18, 23.33) * mm});
            skLineSegment(sketch, "E5236", {"start": v(-93.18, 23.33) * mm, "end": v(-93.03, 23.21) * mm});
            skLineSegment(sketch, "E5237", {"start": v(-93.03, 23.21) * mm, "end": v(-92.87, 23.1) * mm});
            skLineSegment(sketch, "E5238", {"start": v(-92.87, 23.1) * mm, "end": v(-92.72, 22.99) * mm});
            skLineSegment(sketch, "E5239", {"start": v(-92.72, 22.99) * mm, "end": v(-92.57, 22.88) * mm});
            skLineSegment(sketch, "E5240", {"start": v(-92.57, 22.88) * mm, "end": v(-92.41, 22.77) * mm});
            skLineSegment(sketch, "E5241", {"start": v(-92.41, 22.77) * mm, "end": v(-92.27, 22.66) * mm});
            skLineSegment(sketch, "E5242", {"start": v(-92.27, 22.66) * mm, "end": v(-92.12, 22.56) * mm});
            skLineSegment(sketch, "E5243", {"start": v(-92.12, 22.56) * mm, "end": v(-91.97, 22.46) * mm});
            skLineSegment(sketch, "E5244", {"start": v(-91.97, 22.46) * mm, "end": v(-91.83, 22.36) * mm});
            skLineSegment(sketch, "E5245", {"start": v(-91.83, 22.36) * mm, "end": v(-91.68, 22.26) * mm});
            skLineSegment(sketch, "E5246", {"start": v(-91.68, 22.26) * mm, "end": v(-91.54, 22.17) * mm});
            skLineSegment(sketch, "E5247", {"start": v(-91.54, 22.17) * mm, "end": v(-91.4, 22.08) * mm});
            skLineSegment(sketch, "E5248", {"start": v(-91.4, 22.08) * mm, "end": v(-91.26, 21.99) * mm});
            skLineSegment(sketch, "E5249", {"start": v(-91.26, 21.99) * mm, "end": v(-91.12, 21.9) * mm});
            skLineSegment(sketch, "E5250", {"start": v(-91.12, 21.9) * mm, "end": v(-90.99, 21.81) * mm});
            skLineSegment(sketch, "E5251", {"start": v(-90.99, 21.81) * mm, "end": v(-90.86, 21.73) * mm});
            skLineSegment(sketch, "E5252", {"start": v(-90.86, 21.73) * mm, "end": v(-90.72, 21.65) * mm});
            skLineSegment(sketch, "E5253", {"start": v(-90.72, 21.65) * mm, "end": v(-90.6, 21.57) * mm});
            skLineSegment(sketch, "E5254", {"start": v(-90.6, 21.57) * mm, "end": v(-90.46, 21.5) * mm});
            skLineSegment(sketch, "E5255", {"start": v(-90.46, 21.5) * mm, "end": v(-90.34, 21.42) * mm});
            skLineSegment(sketch, "E5256", {"start": v(-90.34, 21.42) * mm, "end": v(-90.21, 21.34) * mm});
            skLineSegment(sketch, "E5257", {"start": v(-90.21, 21.34) * mm, "end": v(-90.09, 21.27) * mm});
            skLineSegment(sketch, "E5258", {"start": v(-90.09, 21.27) * mm, "end": v(-89.97, 21.2) * mm});
            skLineSegment(sketch, "E5259", {"start": v(-89.97, 21.2) * mm, "end": v(-89.85, 21.13) * mm});
            skLineSegment(sketch, "E5260", {"start": v(-89.85, 21.13) * mm, "end": v(-89.73, 21.06) * mm});
            skLineSegment(sketch, "E5261", {"start": v(-89.73, 21.06) * mm, "end": v(-89.61, 21) * mm});
            skLineSegment(sketch, "E5262", {"start": v(-89.61, 21) * mm, "end": v(-89.5, 20.94) * mm});
            skLineSegment(sketch, "E5263", {"start": v(-89.5, 20.94) * mm, "end": v(-89.39, 20.88) * mm});
            skLineSegment(sketch, "E5264", {"start": v(-89.39, 20.88) * mm, "end": v(-89.27, 20.82) * mm});
            skLineSegment(sketch, "E5265", {"start": v(-89.27, 20.82) * mm, "end": v(-89.17, 20.76) * mm});
            skLineSegment(sketch, "E5266", {"start": v(-89.17, 20.76) * mm, "end": v(-89.06, 20.7) * mm});
            skLineSegment(sketch, "E5267", {"start": v(-89.06, 20.7) * mm, "end": v(-88.95, 20.65) * mm});
            skLineSegment(sketch, "E5268", {"start": v(-88.95, 20.65) * mm, "end": v(-88.85, 20.6) * mm});
            skLineSegment(sketch, "E5269", {"start": v(-88.85, 20.6) * mm, "end": v(-88.74, 20.13) * mm});
            skLineSegment(sketch, "E5270", {"start": v(-88.74, 20.13) * mm, "end": v(-89.1, 18.48) * mm});
            skLineSegment(sketch, "E5271", {"start": v(-89.1, 18.48) * mm, "end": v(-89.4, 18.1) * mm});
            skLineSegment(sketch, "E5272", {"start": v(-89.4, 18.1) * mm, "end": v(-89.5, 18.1) * mm});
            skLineSegment(sketch, "E5273", {"start": v(-89.5, 18.1) * mm, "end": v(-89.62, 18.1) * mm});
            skLineSegment(sketch, "E5274", {"start": v(-89.62, 18.1) * mm, "end": v(-89.75, 18.09) * mm});
            skLineSegment(sketch, "E5275", {"start": v(-89.75, 18.09) * mm, "end": v(-89.87, 18.08) * mm});
            skLineSegment(sketch, "E5276", {"start": v(-89.87, 18.08) * mm, "end": v(-90, 18.07) * mm});
            skLineSegment(sketch, "E5277", {"start": v(-90, 18.07) * mm, "end": v(-90.12, 18.07) * mm});
            skLineSegment(sketch, "E5278", {"start": v(-90.12, 18.07) * mm, "end": v(-90.25, 18.06) * mm});
            skLineSegment(sketch, "E5279", {"start": v(-90.25, 18.06) * mm, "end": v(-90.38, 18.05) * mm});
            skLineSegment(sketch, "E5280", {"start": v(-90.38, 18.05) * mm, "end": v(-90.52, 18.03) * mm});
            skLineSegment(sketch, "E5281", {"start": v(-90.52, 18.03) * mm, "end": v(-90.66, 18.02) * mm});
            skLineSegment(sketch, "E5282", {"start": v(-90.66, 18.02) * mm, "end": v(-90.8, 18) * mm});
            skLineSegment(sketch, "E5283", {"start": v(-90.8, 18) * mm, "end": v(-90.94, 18) * mm});
            skLineSegment(sketch, "E5284", {"start": v(-90.94, 18) * mm, "end": v(-91.08, 17.98) * mm});
            skLineSegment(sketch, "E5285", {"start": v(-91.08, 17.98) * mm, "end": v(-91.23, 17.96) * mm});
            skLineSegment(sketch, "E5286", {"start": v(-91.23, 17.96) * mm, "end": v(-91.38, 17.94) * mm});
            skLineSegment(sketch, "E5287", {"start": v(-91.38, 17.94) * mm, "end": v(-91.53, 17.93) * mm});
            skLineSegment(sketch, "E5288", {"start": v(-91.53, 17.93) * mm, "end": v(-91.69, 17.9) * mm});
            skLineSegment(sketch, "E5289", {"start": v(-91.69, 17.9) * mm, "end": v(-91.84, 17.89) * mm});
            skLineSegment(sketch, "E5290", {"start": v(-91.84, 17.89) * mm, "end": v(-92, 17.86) * mm});
            skLineSegment(sketch, "E5291", {"start": v(-92, 17.86) * mm, "end": v(-92.16, 17.84) * mm});
            skLineSegment(sketch, "E5292", {"start": v(-92.16, 17.84) * mm, "end": v(-92.33, 17.82) * mm});
            skLineSegment(sketch, "E5293", {"start": v(-92.33, 17.82) * mm, "end": v(-92.5, 17.79) * mm});
            skLineSegment(sketch, "E5294", {"start": v(-92.5, 17.79) * mm, "end": v(-92.66, 17.76) * mm});
            skLineSegment(sketch, "E5295", {"start": v(-92.66, 17.76) * mm, "end": v(-92.83, 17.73) * mm});
            skLineSegment(sketch, "E5296", {"start": v(-92.83, 17.73) * mm, "end": v(-93, 17.7) * mm});
            skLineSegment(sketch, "E5297", {"start": v(-93, 17.7) * mm, "end": v(-93.18, 17.67) * mm});
            skLineSegment(sketch, "E5298", {"start": v(-93.18, 17.67) * mm, "end": v(-93.36, 17.64) * mm});
            skLineSegment(sketch, "E5299", {"start": v(-93.36, 17.64) * mm, "end": v(-93.53, 17.6) * mm});
            skLineSegment(sketch, "E5300", {"start": v(-93.53, 17.6) * mm, "end": v(-93.72, 17.57) * mm});
            skLineSegment(sketch, "E5301", {"start": v(-93.72, 17.57) * mm, "end": v(-93.9, 17.54) * mm});
            skLineSegment(sketch, "E5302", {"start": v(-93.9, 17.54) * mm, "end": v(-94.09, 17.5) * mm});
            skLineSegment(sketch, "E5303", {"start": v(-94.09, 17.5) * mm, "end": v(-94.28, 17.46) * mm});
            skLineSegment(sketch, "E5304", {"start": v(-94.28, 17.46) * mm, "end": v(-94.47, 17.42) * mm});
            skLineSegment(sketch, "E5305", {"start": v(-94.47, 17.42) * mm, "end": v(-94.66, 17.38) * mm});
            skLineSegment(sketch, "E5306", {"start": v(-94.66, 17.38) * mm, "end": v(-94.85, 17.33) * mm});
            skLineSegment(sketch, "E5307", {"start": v(-94.85, 17.33) * mm, "end": v(-95.05, 17.29) * mm});
            skLineSegment(sketch, "E5308", {"start": v(-95.05, 17.29) * mm, "end": v(-95.25, 17.24) * mm});
            skLineSegment(sketch, "E5309", {"start": v(-95.25, 17.24) * mm, "end": v(-95.45, 17.19) * mm});
            skLineSegment(sketch, "E5310", {"start": v(-95.45, 17.19) * mm, "end": v(-95.62, 17.13) * mm});
            skLineSegment(sketch, "E5311", {"start": v(-95.62, 17.13) * mm, "end": v(-95.98, 15.01) * mm});
            skLineSegment(sketch, "E5312", {"start": v(-95.98, 15.01) * mm, "end": v(-95.84, 14.9) * mm});
            skLineSegment(sketch, "E5313", {"start": v(-95.84, 14.9) * mm, "end": v(-95.66, 14.79) * mm});
            skLineSegment(sketch, "E5314", {"start": v(-95.66, 14.79) * mm, "end": v(-95.49, 14.68) * mm});
            skLineSegment(sketch, "E5315", {"start": v(-95.49, 14.68) * mm, "end": v(-95.32, 14.57) * mm});
            skLineSegment(sketch, "E5316", {"start": v(-95.32, 14.57) * mm, "end": v(-95.15, 14.47) * mm});
            skLineSegment(sketch, "E5317", {"start": v(-95.15, 14.47) * mm, "end": v(-94.98, 14.36) * mm});
            skLineSegment(sketch, "E5318", {"start": v(-94.98, 14.36) * mm, "end": v(-94.81, 14.26) * mm});
            skLineSegment(sketch, "E5319", {"start": v(-94.81, 14.26) * mm, "end": v(-94.65, 14.16) * mm});
            skLineSegment(sketch, "E5320", {"start": v(-94.65, 14.16) * mm, "end": v(-94.48, 14.07) * mm});
            skLineSegment(sketch, "E5321", {"start": v(-94.48, 14.07) * mm, "end": v(-94.32, 13.97) * mm});
            skLineSegment(sketch, "E5322", {"start": v(-94.32, 13.97) * mm, "end": v(-94.16, 13.88) * mm});
            skLineSegment(sketch, "E5323", {"start": v(-94.16, 13.88) * mm, "end": v(-94, 13.8) * mm});
            skLineSegment(sketch, "E5324", {"start": v(-94, 13.8) * mm, "end": v(-93.84, 13.7) * mm});
            skLineSegment(sketch, "E5325", {"start": v(-93.84, 13.7) * mm, "end": v(-93.69, 13.62) * mm});
            skLineSegment(sketch, "E5326", {"start": v(-93.69, 13.62) * mm, "end": v(-93.54, 13.53) * mm});
            skLineSegment(sketch, "E5327", {"start": v(-93.54, 13.53) * mm, "end": v(-93.38, 13.45) * mm});
            skLineSegment(sketch, "E5328", {"start": v(-93.38, 13.45) * mm, "end": v(-93.23, 13.37) * mm});
            skLineSegment(sketch, "E5329", {"start": v(-93.23, 13.37) * mm, "end": v(-93.09, 13.3) * mm});
            skLineSegment(sketch, "E5330", {"start": v(-93.09, 13.3) * mm, "end": v(-92.94, 13.21) * mm});
            skLineSegment(sketch, "E5331", {"start": v(-92.94, 13.21) * mm, "end": v(-92.8, 13.14) * mm});
            skLineSegment(sketch, "E5332", {"start": v(-92.8, 13.14) * mm, "end": v(-92.65, 13.07) * mm});
            skLineSegment(sketch, "E5333", {"start": v(-92.65, 13.07) * mm, "end": v(-92.5, 13) * mm});
            skLineSegment(sketch, "E5334", {"start": v(-92.5, 13) * mm, "end": v(-92.37, 12.93) * mm});
            skLineSegment(sketch, "E5335", {"start": v(-92.37, 12.93) * mm, "end": v(-92.23, 12.86) * mm});
            skLineSegment(sketch, "E5336", {"start": v(-92.23, 12.86) * mm, "end": v(-92.1, 12.8) * mm});
            skLineSegment(sketch, "E5337", {"start": v(-92.1, 12.8) * mm, "end": v(-91.96, 12.73) * mm});
            skLineSegment(sketch, "E5338", {"start": v(-91.96, 12.73) * mm, "end": v(-91.83, 12.67) * mm});
            skLineSegment(sketch, "E5339", {"start": v(-91.83, 12.67) * mm, "end": v(-91.7, 12.6) * mm});
            skLineSegment(sketch, "E5340", {"start": v(-91.7, 12.6) * mm, "end": v(-91.57, 12.55) * mm});
            skLineSegment(sketch, "E5341", {"start": v(-91.57, 12.55) * mm, "end": v(-91.45, 12.5) * mm});
            skLineSegment(sketch, "E5342", {"start": v(-91.45, 12.5) * mm, "end": v(-91.32, 12.44) * mm});
            skLineSegment(sketch, "E5343", {"start": v(-91.32, 12.44) * mm, "end": v(-91.2, 12.39) * mm});
            skLineSegment(sketch, "E5344", {"start": v(-91.2, 12.39) * mm, "end": v(-91.08, 12.33) * mm});
            skLineSegment(sketch, "E5345", {"start": v(-91.08, 12.33) * mm, "end": v(-90.96, 12.28) * mm});
            skLineSegment(sketch, "E5346", {"start": v(-90.96, 12.28) * mm, "end": v(-90.85, 12.24) * mm});
            skLineSegment(sketch, "E5347", {"start": v(-90.85, 12.24) * mm, "end": v(-90.74, 12.19) * mm});
            skLineSegment(sketch, "E5348", {"start": v(-90.74, 12.19) * mm, "end": v(-90.62, 12.14) * mm});
            skLineSegment(sketch, "E5349", {"start": v(-90.62, 12.14) * mm, "end": v(-90.51, 12.1) * mm});
            skLineSegment(sketch, "E5350", {"start": v(-90.51, 12.1) * mm, "end": v(-90.4, 12.06) * mm});
            skLineSegment(sketch, "E5351", {"start": v(-90.4, 12.06) * mm, "end": v(-90.26, 11.6) * mm});
            skLineSegment(sketch, "E5352", {"start": v(-90.26, 11.6) * mm, "end": v(-90.46, 9.93) * mm});
            skLineSegment(sketch, "E5353", {"start": v(-90.46, 9.93) * mm, "end": v(-90.7, 9.53) * mm});
            skLineSegment(sketch, "E5354", {"start": v(-90.7, 9.53) * mm, "end": v(-90.82, 9.51) * mm});
            skLineSegment(sketch, "E5355", {"start": v(-90.82, 9.51) * mm, "end": v(-90.94, 9.5) * mm});
            skLineSegment(sketch, "E5356", {"start": v(-90.94, 9.5) * mm, "end": v(-91.06, 9.48) * mm});
            skLineSegment(sketch, "E5357", {"start": v(-91.06, 9.48) * mm, "end": v(-91.18, 9.46) * mm});
            skLineSegment(sketch, "E5358", {"start": v(-91.18, 9.46) * mm, "end": v(-91.3, 9.44) * mm});
            skLineSegment(sketch, "E5359", {"start": v(-91.3, 9.44) * mm, "end": v(-91.43, 9.42) * mm});
            skLineSegment(sketch, "E5360", {"start": v(-91.43, 9.42) * mm, "end": v(-91.56, 9.4) * mm});
            skLineSegment(sketch, "E5361", {"start": v(-91.56, 9.4) * mm, "end": v(-91.7, 9.37) * mm});
            skLineSegment(sketch, "E5362", {"start": v(-91.7, 9.37) * mm, "end": v(-91.82, 9.35) * mm});
            skLineSegment(sketch, "E5363", {"start": v(-91.82, 9.35) * mm, "end": v(-91.96, 9.32) * mm});
            skLineSegment(sketch, "E5364", {"start": v(-91.96, 9.32) * mm, "end": v(-92.1, 9.3) * mm});
            skLineSegment(sketch, "E5365", {"start": v(-92.1, 9.3) * mm, "end": v(-92.24, 9.27) * mm});
            skLineSegment(sketch, "E5366", {"start": v(-92.24, 9.27) * mm, "end": v(-92.38, 9.24) * mm});
            skLineSegment(sketch, "E5367", {"start": v(-92.38, 9.24) * mm, "end": v(-92.53, 9.2) * mm});
            skLineSegment(sketch, "E5368", {"start": v(-92.53, 9.2) * mm, "end": v(-92.67, 9.18) * mm});
            skLineSegment(sketch, "E5369", {"start": v(-92.67, 9.18) * mm, "end": v(-92.82, 9.14) * mm});
            skLineSegment(sketch, "E5370", {"start": v(-92.82, 9.14) * mm, "end": v(-92.97, 9.1) * mm});
            skLineSegment(sketch, "E5371", {"start": v(-92.97, 9.1) * mm, "end": v(-93.13, 9.07) * mm});
            skLineSegment(sketch, "E5372", {"start": v(-93.13, 9.07) * mm, "end": v(-93.28, 9.04) * mm});
            skLineSegment(sketch, "E5373", {"start": v(-93.28, 9.04) * mm, "end": v(-93.44, 9) * mm});
            skLineSegment(sketch, "E5374", {"start": v(-93.44, 9) * mm, "end": v(-93.6, 8.96) * mm});
            skLineSegment(sketch, "E5375", {"start": v(-93.6, 8.96) * mm, "end": v(-93.76, 8.92) * mm});
            skLineSegment(sketch, "E5376", {"start": v(-93.76, 8.92) * mm, "end": v(-93.93, 8.87) * mm});
            skLineSegment(sketch, "E5377", {"start": v(-93.93, 8.87) * mm, "end": v(-94.1, 8.83) * mm});
            skLineSegment(sketch, "E5378", {"start": v(-94.1, 8.83) * mm, "end": v(-94.26, 8.78) * mm});
            skLineSegment(sketch, "E5379", {"start": v(-94.26, 8.78) * mm, "end": v(-94.44, 8.74) * mm});
            skLineSegment(sketch, "E5380", {"start": v(-94.44, 8.74) * mm, "end": v(-94.6, 8.69) * mm});
            skLineSegment(sketch, "E5381", {"start": v(-94.6, 8.69) * mm, "end": v(-94.79, 8.64) * mm});
            skLineSegment(sketch, "E5382", {"start": v(-94.79, 8.64) * mm, "end": v(-94.96, 8.59) * mm});
            skLineSegment(sketch, "E5383", {"start": v(-94.96, 8.59) * mm, "end": v(-95.14, 8.53) * mm});
            skLineSegment(sketch, "E5384", {"start": v(-95.14, 8.53) * mm, "end": v(-95.32, 8.48) * mm});
            skLineSegment(sketch, "E5385", {"start": v(-95.32, 8.48) * mm, "end": v(-95.5, 8.42) * mm});
            skLineSegment(sketch, "E5386", {"start": v(-95.5, 8.42) * mm, "end": v(-95.7, 8.36) * mm});
            skLineSegment(sketch, "E5387", {"start": v(-95.7, 8.36) * mm, "end": v(-95.88, 8.3) * mm});
            skLineSegment(sketch, "E5388", {"start": v(-95.88, 8.3) * mm, "end": v(-96.07, 8.24) * mm});
            skLineSegment(sketch, "E5389", {"start": v(-96.07, 8.24) * mm, "end": v(-96.26, 8.17) * mm});
            skLineSegment(sketch, "E5390", {"start": v(-96.26, 8.17) * mm, "end": v(-96.46, 8.1) * mm});
            skLineSegment(sketch, "E5391", {"start": v(-96.46, 8.1) * mm, "end": v(-96.65, 8.04) * mm});
            skLineSegment(sketch, "E5392", {"start": v(-96.65, 8.04) * mm, "end": v(-96.82, 7.97) * mm});
            skLineSegment(sketch, "E5393", {"start": v(-96.82, 7.97) * mm, "end": v(-96.97, 5.82) * mm});
            skLineSegment(sketch, "E5394", {"start": v(-96.97, 5.82) * mm, "end": v(-96.82, 5.72) * mm});
            skLineSegment(sketch, "E5395", {"start": v(-96.82, 5.72) * mm, "end": v(-96.63, 5.63) * mm});
            skLineSegment(sketch, "E5396", {"start": v(-96.63, 5.63) * mm, "end": v(-96.45, 5.54) * mm});
            skLineSegment(sketch, "E5397", {"start": v(-96.45, 5.54) * mm, "end": v(-96.27, 5.45) * mm});
            skLineSegment(sketch, "E5398", {"start": v(-96.27, 5.45) * mm, "end": v(-96.1, 5.36) * mm});
            skLineSegment(sketch, "E5399", {"start": v(-96.1, 5.36) * mm, "end": v(-95.91, 5.27) * mm});
            skLineSegment(sketch, "E5400", {"start": v(-95.91, 5.27) * mm, "end": v(-95.74, 5.19) * mm});
            skLineSegment(sketch, "E5401", {"start": v(-95.74, 5.19) * mm, "end": v(-95.56, 5.1) * mm});
            skLineSegment(sketch, "E5402", {"start": v(-95.56, 5.1) * mm, "end": v(-95.4, 5.02) * mm});
            skLineSegment(sketch, "E5403", {"start": v(-95.4, 5.02) * mm, "end": v(-95.22, 4.94) * mm});
            skLineSegment(sketch, "E5404", {"start": v(-95.22, 4.94) * mm, "end": v(-95.05, 4.87) * mm});
            skLineSegment(sketch, "E5405", {"start": v(-95.05, 4.87) * mm, "end": v(-94.89, 4.8) * mm});
            skLineSegment(sketch, "E5406", {"start": v(-94.89, 4.8) * mm, "end": v(-94.72, 4.72) * mm});
            skLineSegment(sketch, "E5407", {"start": v(-94.72, 4.72) * mm, "end": v(-94.56, 4.65) * mm});
            skLineSegment(sketch, "E5408", {"start": v(-94.56, 4.65) * mm, "end": v(-94.4, 4.58) * mm});
            skLineSegment(sketch, "E5409", {"start": v(-94.4, 4.58) * mm, "end": v(-94.24, 4.51) * mm});
            skLineSegment(sketch, "E5410", {"start": v(-94.24, 4.51) * mm, "end": v(-94.08, 4.45) * mm});
            skLineSegment(sketch, "E5411", {"start": v(-94.08, 4.45) * mm, "end": v(-93.93, 4.38) * mm});
            skLineSegment(sketch, "E5412", {"start": v(-93.93, 4.38) * mm, "end": v(-93.77, 4.32) * mm});
            skLineSegment(sketch, "E5413", {"start": v(-93.77, 4.32) * mm, "end": v(-93.62, 4.26) * mm});
            skLineSegment(sketch, "E5414", {"start": v(-93.62, 4.26) * mm, "end": v(-93.47, 4.2) * mm});
            skLineSegment(sketch, "E5415", {"start": v(-93.47, 4.2) * mm, "end": v(-93.33, 4.14) * mm});
            skLineSegment(sketch, "E5416", {"start": v(-93.33, 4.14) * mm, "end": v(-93.18, 4.09) * mm});
            skLineSegment(sketch, "E5417", {"start": v(-93.18, 4.09) * mm, "end": v(-93.04, 4.03) * mm});
            skLineSegment(sketch, "E5418", {"start": v(-93.04, 4.03) * mm, "end": v(-92.9, 3.98) * mm});
            skLineSegment(sketch, "E5419", {"start": v(-92.9, 3.98) * mm, "end": v(-92.76, 3.93) * mm});
            skLineSegment(sketch, "E5420", {"start": v(-92.76, 3.93) * mm, "end": v(-92.62, 3.88) * mm});
            skLineSegment(sketch, "E5421", {"start": v(-92.62, 3.88) * mm, "end": v(-92.49, 3.84) * mm});
            skLineSegment(sketch, "E5422", {"start": v(-92.49, 3.84) * mm, "end": v(-92.35, 3.79) * mm});
            skLineSegment(sketch, "E5423", {"start": v(-92.35, 3.79) * mm, "end": v(-92.22, 3.75) * mm});
            skLineSegment(sketch, "E5424", {"start": v(-92.22, 3.75) * mm, "end": v(-92.1, 3.7) * mm});
            skLineSegment(sketch, "E5425", {"start": v(-92.1, 3.7) * mm, "end": v(-91.97, 3.66) * mm});
            skLineSegment(sketch, "E5426", {"start": v(-91.97, 3.66) * mm, "end": v(-91.84, 3.62) * mm});
            skLineSegment(sketch, "E5427", {"start": v(-91.84, 3.62) * mm, "end": v(-91.72, 3.58) * mm});
            skLineSegment(sketch, "E5428", {"start": v(-91.72, 3.58) * mm, "end": v(-91.6, 3.54) * mm});
            skLineSegment(sketch, "E5429", {"start": v(-91.6, 3.54) * mm, "end": v(-91.48, 3.5) * mm});
            skLineSegment(sketch, "E5430", {"start": v(-91.48, 3.5) * mm, "end": v(-91.37, 3.47) * mm});
            skLineSegment(sketch, "E5431", {"start": v(-91.37, 3.47) * mm, "end": v(-91.25, 3.44) * mm});
            skLineSegment(sketch, "E5432", {"start": v(-91.25, 3.44) * mm, "end": v(-91.14, 3.4) * mm});
            skLineSegment(sketch, "E5433", {"start": v(-91.14, 3.4) * mm, "end": v(-90.95, 2.97) * mm});
            skLineSegment(sketch, "E5434", {"start": v(-90.95, 2.97) * mm, "end": v(-91, 1.29) * mm});
            skSolve(sketch);
        }
        {
            var Q0;
            Q0 = qSketchRegion(id + "F0", true);
            extrude(context, id + "F1", {"entities" : qUnion([Q0]), "depth" : 8 * mm, "offsetDistance" : 25 * mm});
        }
    });
